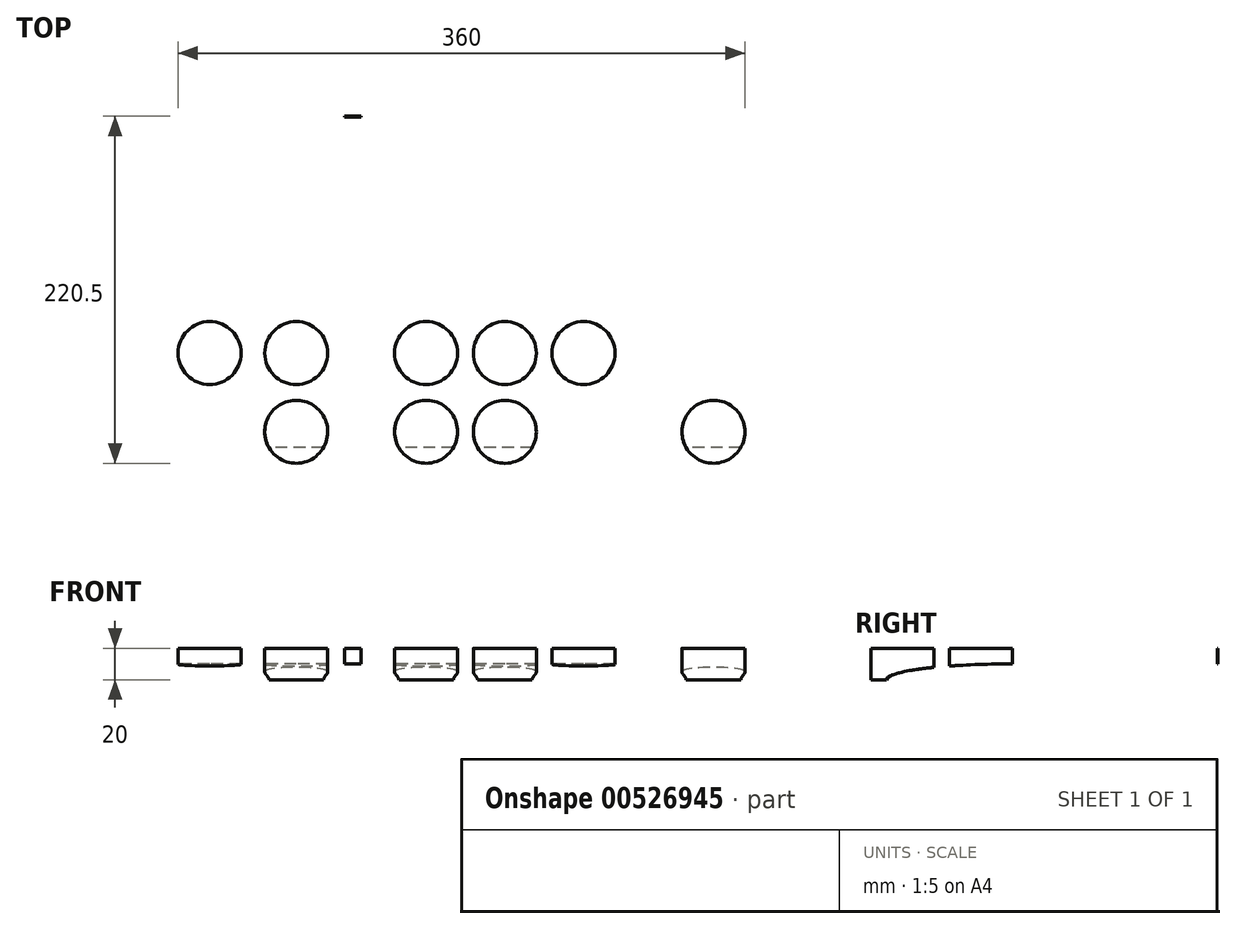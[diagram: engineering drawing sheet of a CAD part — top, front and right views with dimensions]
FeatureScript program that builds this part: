
annotation { "Feature Type Name" : "Feature", "Feature Type Description" : "" }
export const myFeature = defineFeature(function(context is Context, id is Id, definition is map)
    precondition{}
    {
        {
            var Q0;
            Q0=qCreatedBy(makeId("Top.planeOp"),FACE);
            var sketch = newSketch(context, id + "F0", { "sketchPlane" : qUnion([Q0])});
            skLineSegment(sketch, "E0.bottom", {"start": v(-365, 200) * mm, "end": v(365, 200) * mm});
            skLineSegment(sketch, "E0.top", {"start": v(-365, -200) * mm, "end": v(365, -200) * mm});
            skLineSegment(sketch, "E0.left", {"start": v(-365, 200) * mm, "end": v(-365, -200) * mm});
            skLineSegment(sketch, "E0.right", {"start": v(365, 200) * mm, "end": v(365, -200) * mm});
            skPoint(sketch, "E0.middle", {"position": v(0, 0) * mm});
            skEllipticalArc(sketch, "E1", {});
            skEllipticalArc(sketch, "E2.MirrorCS", {});
            skEllipticalArc(sketch, "E3.MirrorCS", {});
            skEllipticalArc(sketch, "E4.MirrorCS", {});
            skLineSegment(sketch, "E5", {"start": v(-365, 200) * mm, "end": v(-105, 200) * mm});
            skLineSegment(sketch, "E6", {"start": v(-365, 200) * mm, "end": v(-365, 50) * mm});
            skLineSegment(sketch, "E7", {"start": v(-365, -200) * mm, "end": v(-365, -50) * mm});
            skLineSegment(sketch, "E8", {"start": v(-365, -200) * mm, "end": v(-182.5, -200) * mm});
            skLineSegment(sketch, "E9", {"start": v(365, 200) * mm, "end": v(105, 200) * mm});
            skLineSegment(sketch, "E10", {"start": v(182.5, -200.11) * mm, "end": v(365, -200) * mm});
            skPoint(sketch, "E11", {"position": v(0, 200) * mm});
            skLineSegment(sketch, "E12", {"start": v(0, 200) * mm, "end": v(-130, 200) * mm});
            skLineSegment(sketch, "E13.MirrorCS", {"start": v(0, -200) * mm, "end": v(-130, -200) * mm});
            skLineSegment(sketch, "E14.MirrorCS", {"start": v(5, 200) * mm, "end": v(130, 200) * mm});
            skLineSegment(sketch, "E15.MirrorCS", {"start": v(-72.5, -200) * mm, "end": v(52.5, -200) * mm});
            skCircle(sketch, "E16", {"center": v(-278.75, 100) * mm, "radius": 20 * mm});
            skCircle(sketch, "E17", {"center": v(-223.75, 150) * mm, "radius": 20 * mm});
            skCircle(sketch, "E18", {"center": v(-223.75, 100) * mm, "radius": 20 * mm});
            skCircle(sketch, "E19", {"center": v(-141.25, 100) * mm, "radius": 20 * mm});
            skCircle(sketch, "E20", {"center": v(-141.25, 150) * mm, "radius": 20 * mm});
            skCircle(sketch, "E21", {"center": v(-91.25, 100) * mm, "radius": 20 * mm});
            skCircle(sketch, "E22", {"center": v(-91.25, 150) * mm, "radius": 20 * mm});
            skCircle(sketch, "E23", {"center": v(-41.25, 100) * mm, "radius": 20 * mm});
            skCircle(sketch, "E24.MirrorC", {"center": v(-41.25, 150) * mm, "radius": 20 * mm});
            skCircle(sketch, "E25.MirrorC", {"center": v(-278.75, -100) * mm, "radius": 20 * mm});
            skCircle(sketch, "E26.MirrorC", {"center": v(-223.75, -150) * mm, "radius": 20 * mm});
            skCircle(sketch, "E27.MirrorC", {"center": v(-223.75, -100) * mm, "radius": 20 * mm});
            skCircle(sketch, "E28.MirrorC", {"center": v(-141.25, -100) * mm, "radius": 20 * mm});
            skCircle(sketch, "E29.MirrorC", {"center": v(-141.25, -150) * mm, "radius": 20 * mm});
            skCircle(sketch, "E30.MirrorC", {"center": v(-91.25, -100) * mm, "radius": 20 * mm});
            skCircle(sketch, "E31.MirrorC", {"center": v(-41.25, -100) * mm, "radius": 20 * mm});
            skCircle(sketch, "E32.MirrorC", {"center": v(-91.25, -150) * mm, "radius": 20 * mm});
            skCircle(sketch, "E33.MirrorC", {"center": v(-41.25, -150) * mm, "radius": 20 * mm});
            skCircle(sketch, "E34.MirrorC", {"center": v(-222.5, -10) * mm, "radius": 20 * mm});
            skLineSegment(sketch, "E35.bottom", {"start": v(210, 15) * mm, "end": v(-210, 15) * mm});
            skLineSegment(sketch, "E35.top", {"start": v(210, -15) * mm, "end": v(-210, -15) * mm});
            skLineSegment(sketch, "E35.left", {"start": v(210, 15) * mm, "end": v(210, -15) * mm});
            skLineSegment(sketch, "E35.right", {"start": v(-210, 15) * mm, "end": v(-210, -15) * mm});
            skLineSegment(sketch, "E36", {"start": v(-365, -50) * mm, "end": v(365, -50) * mm});
            skLineSegment(sketch, "E37", {"start": v(-365, 50) * mm, "end": v(365, 50) * mm});
            skLineSegment(sketch, "E38", {"start": v(-182.5, -200) * mm, "end": v(-182.5, -40.61) * mm});
            skLineSegment(sketch, "E39", {"start": v(0, -200) * mm, "end": v(0, -50) * mm});
            skLineSegment(sketch, "E40", {"start": v(182.5, -200.11) * mm, "end": v(182.4, -40.7) * mm});
            skLineSegment(sketch, "E41.trimOffspring", {"start": v(-182.5, 40.61) * mm, "end": v(-182.5, 200) * mm});
            skLineSegment(sketch, "E42.trimOffspring", {"start": v(-182.5, -15) * mm, "end": v(-182.5, 15) * mm});
            skLineSegment(sketch, "E43.trimOffspring", {"start": v(182.39, -15) * mm, "end": v(182.37, 15) * mm});
            skLineSegment(sketch, "E44.trimOffspring", {"start": v(182.35, 40.73) * mm, "end": v(182.25, 200) * mm});
            skCircle(sketch, "E45", {"center": v(-272.5, 10) * mm, "radius": 20 * mm});
            skCircle(sketch, "E46.MirrorC", {"center": v(-322.5, -8.74) * mm, "radius": 20 * mm});
            skCircle(sketch, "E47.MirrorC", {"center": v(-142.5, -10) * mm, "radius": 20 * mm});
            skCircle(sketch, "E48.MirrorC", {"center": v(-92.5, 10) * mm, "radius": 20 * mm});
            skCircle(sketch, "E49.MirrorC", {"center": v(-42.5, -8.74) * mm, "radius": 20 * mm});
            skCircle(sketch, "E50.MirrorC", {"center": v(42.5, -8.74) * mm, "radius": 20 * mm});
            skCircle(sketch, "E51.MirrorC", {"center": v(142.5, -10) * mm, "radius": 20 * mm});
            skCircle(sketch, "E52.MirrorC", {"center": v(92.5, 10) * mm, "radius": 20 * mm});
            skCircle(sketch, "E53.MirrorC", {"center": v(222.5, -10) * mm, "radius": 20 * mm});
            skCircle(sketch, "E54.MirrorC", {"center": v(272.5, 10) * mm, "radius": 20 * mm});
            skCircle(sketch, "E55.MirrorC", {"center": v(322.5, -8.74) * mm, "radius": 20 * mm});
            skCircle(sketch, "E56.MirrorC", {"center": v(223.75, -100) * mm, "radius": 20 * mm});
            skCircle(sketch, "E57.MirrorC", {"center": v(223.75, -150) * mm, "radius": 20 * mm});
            skCircle(sketch, "E58.MirrorC", {"center": v(278.75, -100) * mm, "radius": 20 * mm});
            skCircle(sketch, "E59.MirrorC", {"center": v(141.25, -100) * mm, "radius": 20 * mm});
            skCircle(sketch, "E60.MirrorC", {"center": v(141.25, -150) * mm, "radius": 20 * mm});
            skCircle(sketch, "E61.MirrorC", {"center": v(91.25, -150) * mm, "radius": 20 * mm});
            skCircle(sketch, "E62.MirrorC", {"center": v(91.25, -100) * mm, "radius": 20 * mm});
            skCircle(sketch, "E63.MirrorC", {"center": v(41.25, -100) * mm, "radius": 20 * mm});
            skCircle(sketch, "E64.MirrorC", {"center": v(41.25, -150) * mm, "radius": 20 * mm});
            skCircle(sketch, "E65.MirrorC", {"center": v(41.25, 100) * mm, "radius": 20 * mm});
            skCircle(sketch, "E66.MirrorC", {"center": v(91.25, 100) * mm, "radius": 20 * mm});
            skCircle(sketch, "E67.MirrorC", {"center": v(141.25, 100) * mm, "radius": 20 * mm});
            skCircle(sketch, "E68.MirrorC", {"center": v(223.75, 100) * mm, "radius": 20 * mm});
            skCircle(sketch, "E69.MirrorC", {"center": v(278.75, 100) * mm, "radius": 20 * mm});
            skCircle(sketch, "E70.MirrorC", {"center": v(223.75, 150) * mm, "radius": 20 * mm});
            skCircle(sketch, "E71.MirrorC", {"center": v(141.25, 150) * mm, "radius": 20 * mm});
            skCircle(sketch, "E72.MirrorC", {"center": v(91.25, 150) * mm, "radius": 20 * mm});
            skCircle(sketch, "E73.MirrorC", {"center": v(41.25, 150) * mm, "radius": 20 * mm});
            const initialGuessF0  = {"E1": [0.215000023161019, -0.00011114199246731203, 0, -1, 0.20000000103052606, 0.15, 6.249845643425636, 1.5707963267948966], "E2.MirrorCS": [-0.215, -0.00011114199246737072, 0, -1, 0.2, 0.15, 4.711833270393751, 0.03333950926130193], "E3.MirrorCS": [-0.215, 0.00011114199246727815, 0, 1, 0.2, 0.15, 6.249845797918284, 1.5707963267948966], "E4.MirrorCS": [0.215, 0.00011114199246735796, 0, 1, 0.2, 0.15, 4.711277560231201, 0.03333950926130226]};
            skSetInitialGuess(sketch, initialGuessF0);
            skSolve(sketch);
        }
        {
            var Q0;
            Q0=qCreatedBy(makeId("Top.planeOp"),FACE);
            cPlane(context, id + "F1", {"entities" : qUnion([Q0]), "cplaneType" : CPlaneType.OFFSET, "offset" : 20 * mm, "width" : 150 * mm, "height" : 150 * mm});
        }
        {
            var Q0;
            Q0=qCreatedBy(id+"F1.planeOp",FACE);
            var sketch = newSketch(context, id + "F2", { "sketchPlane" : qUnion([Q0])});
            skLineSegment(sketch, "E74.bottom", {"start": v(0, 0) * mm, "end": v(365, 0) * mm});
            skLineSegment(sketch, "E74.top", {"start": v(0, -200) * mm, "end": v(210, -200) * mm});
            skLineSegment(sketch, "E74.left", {"start": v(0, 0) * mm, "end": v(0, -200) * mm});
            skLineSegment(sketch, "E75", {"start": v(0, -15) * mm, "end": v(364.58, -15) * mm});
            skLineSegment(sketch, "E76", {"start": v(0, -170) * mm, "end": v(294.02, -170) * mm});
            skLineSegment(sketch, "E77", {"start": v(330, 0) * mm, "end": v(330, -128.4) * mm});
            skLineSegment(sketch, "E78", {"start": v(215, 0) * mm, "end": v(215, -200) * mm});
            skPoint(sketch, "E79", {"position": v(215, -200) * mm});
            skPoint(sketch, "E80", {"position": v(365, 0) * mm});
            skLineSegment(sketch, "E81", {"start": v(275, 0) * mm, "end": v(275, -183.3) * mm});
            skLineSegment(sketch, "E82", {"start": v(275, -140) * mm, "end": v(322.12, -140) * mm});
            skPoint(sketch, "E83", {"position": v(215, -170) * mm});
            skPoint(sketch, "E84", {"position": v(330, 0) * mm});
            skPoint(sketch, "E85", {"position": v(275, -140) * mm});
            skPoint(sketch, "E86", {"position": v(330, -140) * mm});
            skPoint(sketch, "E87", {"position": v(275, -185) * mm});
            skLineSegment(sketch, "E88", {"start": v(315, -149.07) * mm, "end": v(315, 0) * mm});
            skLineSegment(sketch, "E89", {"start": v(210, 0) * mm, "end": v(210, -200) * mm});
            skEllipticalArc(sketch, "E90.trimOffspring", {});
            skEllipticalArc(sketch, "E91", {});
            skPoint(sketch, "E92.orphan", {"position": v(365, -170) * mm});
            skPoint(sketch, "E93.trimOffspring.end.orphan", {"position": v(330, -200) * mm});
            skPoint(sketch, "E94.orphan", {"position": v(365, -200) * mm});
            skPoint(sketch, "E95.orphan", {"position": v(365, -15) * mm});
            skLineSegment(sketch, "E96.MirrorCS", {"start": v(0, 0) * mm, "end": v(-365, 0) * mm});
            skLineSegment(sketch, "E97.MirrorCS", {"start": v(0, -15) * mm, "end": v(-364.58, -15) * mm});
            skLineSegment(sketch, "E98.MirrorCS", {"start": v(0, -170) * mm, "end": v(-294.02, -170) * mm});
            skLineSegment(sketch, "E99.MirrorCS", {"start": v(0, -200) * mm, "end": v(-210, -200) * mm});
            skLineSegment(sketch, "E100.MirrorCS", {"start": v(-210, 0) * mm, "end": v(-210, -200) * mm});
            skLineSegment(sketch, "E101.MirrorCS", {"start": v(-215, 0) * mm, "end": v(-215, -200) * mm});
            skEllipticalArc(sketch, "E102.MirrorCS", {});
            skEllipticalArc(sketch, "E103.MirrorCS", {});
            skLineSegment(sketch, "E104.MirrorCS", {"start": v(-275, 0) * mm, "end": v(-275, -183.3) * mm});
            skLineSegment(sketch, "E105.MirrorCS", {"start": v(-275, -140) * mm, "end": v(-322.12, -140) * mm});
            skLineSegment(sketch, "E106.MirrorCS", {"start": v(-315, -149.07) * mm, "end": v(-315, 0) * mm});
            skLineSegment(sketch, "E107.MirrorCS", {"start": v(-330, 0) * mm, "end": v(-330, -128.4) * mm});
            skLineSegment(sketch, "E108.MirrorCS", {"start": v(0, 15) * mm, "end": v(-364.58, 15) * mm});
            skLineSegment(sketch, "E109.MirrorCS", {"start": v(0, 15) * mm, "end": v(364.58, 15) * mm});
            skEllipticalArc(sketch, "E110.MirrorCS", {});
            skLineSegment(sketch, "E111.MirrorCS", {"start": v(-330, 0) * mm, "end": v(-330, 128.4) * mm});
            skLineSegment(sketch, "E112.MirrorCS", {"start": v(-315, 149.07) * mm, "end": v(-315, 0) * mm});
            skLineSegment(sketch, "E113.MirrorCS", {"start": v(-275, 0) * mm, "end": v(-275, 183.3) * mm});
            skLineSegment(sketch, "E114.MirrorCS", {"start": v(-215, 0) * mm, "end": v(-215, 200) * mm});
            skLineSegment(sketch, "E115.MirrorCS", {"start": v(-210, 0) * mm, "end": v(-210, 200) * mm});
            skLineSegment(sketch, "E116.MirrorCS", {"start": v(0, 0) * mm, "end": v(0, 200) * mm});
            skLineSegment(sketch, "E117.MirrorCS", {"start": v(210, 0) * mm, "end": v(210, 200) * mm});
            skLineSegment(sketch, "E118.MirrorCS", {"start": v(215, 0) * mm, "end": v(215, 200) * mm});
            skLineSegment(sketch, "E119.MirrorCS", {"start": v(275, 0) * mm, "end": v(275, 183.3) * mm});
            skLineSegment(sketch, "E120.MirrorCS", {"start": v(315, 149.07) * mm, "end": v(315, 0) * mm});
            skLineSegment(sketch, "E121.MirrorCS", {"start": v(330, 0) * mm, "end": v(330, 128.4) * mm});
            skEllipticalArc(sketch, "E122.MirrorCS", {});
            skEllipticalArc(sketch, "E123.MirrorCS", {});
            skEllipticalArc(sketch, "E124.MirrorCS", {});
            skLineSegment(sketch, "E125.MirrorCS", {"start": v(-275, 140) * mm, "end": v(-322.12, 140) * mm});
            skLineSegment(sketch, "E126.MirrorCS", {"start": v(0, 170) * mm, "end": v(-294.02, 170) * mm});
            skLineSegment(sketch, "E127.MirrorCS", {"start": v(0, 170) * mm, "end": v(294.02, 170) * mm});
            skLineSegment(sketch, "E128.MirrorCS", {"start": v(0, 200) * mm, "end": v(210, 200) * mm});
            skLineSegment(sketch, "E129.MirrorCS", {"start": v(0, 200) * mm, "end": v(-210, 200) * mm});
            skLineSegment(sketch, "E130.MirrorCS", {"start": v(275, 140) * mm, "end": v(322.12, 140) * mm});
            const initialGuessF2  = {"E90.trimOffspring": [0.215, 0, 1, 0, 0.115, 0.17, 4.71238898038469, 6.283185307179586], "E91": [0.215, 0, 0, -1, 0.2, 0.15, 6.249845797918284, 1.5707963267948966], "E102.MirrorCS": [-0.215, 0, -1, 0, 0.115, 0.17, 6.283185307179586, 1.5707963267948966], "E103.MirrorCS": [-0.215, 0, 0, -1, 0.2, 0.15, 4.71238898038469, 0.03333950926130225], "E110.MirrorCS": [-0.215, 0, 0, 1, 0.2, 0.15, 6.249845797918284, 1.5707963267948966], "E122.MirrorCS": [0.215, 0, 0, 1, 0.2, 0.15, 4.71238898038469, 0.03333950926130225], "E123.MirrorCS": [0.215, 0, 1, 0, 0.115, 0.17, 6.283185307179586, 1.5707963267948966], "E124.MirrorCS": [-0.215, 0, -1, 0, 0.115, 0.17, 4.71238898038469, 6.283185307179586]};
            skSetInitialGuess(sketch, initialGuessF2);
            skSolve(sketch);
        }
        {
            var Q0;
            Q0=qCreatedBy(makeId("Right.planeOp"),FACE);
            var sketch = newSketch(context, id + "F3", { "sketchPlane" : qUnion([Q0])});
            skPoint(sketch, "E131.middle", {"position": v(0, 20) * mm});
            skPoint(sketch, "E132", {"position": v(170, 0) * mm});
            skPoint(sketch, "E133", {"position": v(160, 0) * mm});
            skLineSegment(sketch, "E134.bottom", {"start": v(15, 10.07) * mm, "end": v(80, 10.07) * mm});
            skPoint(sketch, "E135", {"position": v(80, 10.07) * mm});
            skEllipticalArc(sketch, "E136", {});
            skEllipticalArc(sketch, "E137", {});
            skLineSegment(sketch, "E138", {"start": v(0, 20) * mm, "end": v(0, 10.04) * mm});
            skLineSegment(sketch, "E139", {"start": v(0, 20) * mm, "end": v(200, 20) * mm});
            skLineSegment(sketch, "E140", {"start": v(200, 20) * mm, "end": v(0, 20) * mm});
            skLineSegment(sketch, "E141", {"start": v(160, 0) * mm, "end": v(170, 0) * mm});
            skPoint(sketch, "E142.orphan", {"position": v(-200, 20) * mm});
            skLineSegment(sketch, "E143.MirrorCS", {"start": v(-200, 20) * mm, "end": v(0, 20) * mm});
            skLineSegment(sketch, "E144.MirrorCS", {"start": v(-15, 10.07) * mm, "end": v(-80, 10.07) * mm});
            skEllipticalArc(sketch, "E145.MirrorCS", {});
            skLineSegment(sketch, "E146.MirrorCS", {"start": v(-160, 0) * mm, "end": v(-170, 0) * mm});
            skEllipticalArc(sketch, "E147.MirrorCS", {});
            skLineSegment(sketch, "E148.top", {"start": v(-15, 12) * mm, "end": v(15, 12) * mm});
            skLineSegment(sketch, "E148.left", {"start": v(-15, 10.07) * mm, "end": v(-15, 12) * mm});
            skLineSegment(sketch, "E148.right", {"start": v(15, 10.07) * mm, "end": v(15, 12) * mm});
            skLineSegment(sketch, "E149.bottom", {"start": v(15, 18) * mm, "end": v(-15, 18) * mm});
            skLineSegment(sketch, "E149.top", {"start": v(15, 12) * mm, "end": v(-15, 12) * mm});
            skLineSegment(sketch, "E149.left", {"start": v(15, 18) * mm, "end": v(15, 12) * mm});
            skLineSegment(sketch, "E149.right", {"start": v(-15, 18) * mm, "end": v(-15, 12) * mm});
            skLineSegment(sketch, "E150", {"start": v(170, 0) * mm, "end": v(170.12, 20) * mm});
            skLineSegment(sketch, "E151", {"start": v(-170, 0) * mm, "end": v(-170.12, 20) * mm});
            skLineSegment(sketch, "E152", {"start": v(-15, 12) * mm, "end": v(-15, 10.07) * mm});
            skLineSegment(sketch, "E153.bottom", {"start": v(-200, 20) * mm, "end": v(-170, 20) * mm});
            skLineSegment(sketch, "E153.top", {"start": v(-200, 0) * mm, "end": v(-170, 0) * mm});
            skLineSegment(sketch, "E153.left", {"start": v(-200, 20) * mm, "end": v(-200, 0) * mm});
            skLineSegment(sketch, "E153.right", {"start": v(-170, 20) * mm, "end": v(-170, 0) * mm});
            skLineSegment(sketch, "E154.MirrorCS", {"start": v(200, 0) * mm, "end": v(170, 0) * mm});
            skLineSegment(sketch, "E155.MirrorCS", {"start": v(200, 20) * mm, "end": v(200, 0) * mm});
            skLineSegment(sketch, "E156", {"start": v(80, 10.07) * mm, "end": v(80, 20) * mm});
            skLineSegment(sketch, "E157", {"start": v(160, 0) * mm, "end": v(160, 20) * mm});
            skLineSegment(sketch, "E158", {"start": v(149.2, 20) * mm, "end": v(149.2, 5.05) * mm});
            skLineSegment(sketch, "E159", {"start": v(140.08, 20) * mm, "end": v(140.08, 6.65) * mm});
            skLineSegment(sketch, "E160", {"start": v(128.23, 20) * mm, "end": v(128.23, 8.04) * mm});
            skLineSegment(sketch, "E161", {"start": v(102.69, 20) * mm, "end": v(102.69, 9.66) * mm});
            skLineSegment(sketch, "E162.MirrorCS", {"start": v(-80, 10.07) * mm, "end": v(-80, 20) * mm});
            skLineSegment(sketch, "E163.MirrorCS", {"start": v(-102.69, 20) * mm, "end": v(-102.69, 9.66) * mm});
            skLineSegment(sketch, "E164.MirrorCS", {"start": v(-128.23, 20) * mm, "end": v(-128.23, 8.04) * mm});
            skLineSegment(sketch, "E165.MirrorCS", {"start": v(-140.08, 20) * mm, "end": v(-140.08, 6.65) * mm});
            skLineSegment(sketch, "E166.MirrorCS", {"start": v(-149.2, 20) * mm, "end": v(-149.2, 5.05) * mm});
            skLineSegment(sketch, "E167.MirrorCS", {"start": v(-160, 0) * mm, "end": v(-160, 20) * mm});
            skLineSegment(sketch, "E168", {"start": v(45, 20) * mm, "end": v(45, 10.07) * mm});
            skLineSegment(sketch, "E169.MirrorCS", {"start": v(-45, 20) * mm, "end": v(-45, 10.07) * mm});
            const initialGuessF3  = {"E136": [0.17012490332126617, 0.02, -0.006245044279577429, -0.9999804995208388, 0.020000390017188747, 0.02987581400604767, 6.283185307179586, 1.580124845260153], "E137": [0.08, 0, 0, 1, 0.01007139225942586, 0.08, 4.71238898038469, 6.283185307179586], "E145.MirrorCS": [-0.08, 0, 0, 1, 0.01007139225942586, 0.08, 6.283185307179586, 1.5707963267948966], "E147.MirrorCS": [-0.17012490332126617, 0.02, 0.006245044279579518, -0.9999804995208388, 0.020000390017188747, 0.02987581400604767, 4.703060461919433, 6.283185307179586]};
            skSetInitialGuess(sketch, initialGuessF3);
            skSolve(sketch);
        }
        {
            var Q0;
            Q0=qCreatedBy(makeId("Front.planeOp"),FACE);
            var sketch = newSketch(context, id + "F4", { "sketchPlane" : qUnion([Q0])});
            skLineSegment(sketch, "E170", {"start": v(0, 20) * mm, "end": v(365, 20) * mm});
            skPoint(sketch, "E171", {"position": v(210, 20) * mm});
            skLineSegment(sketch, "E172", {"start": v(210, 18) * mm, "end": v(210, 12) * mm});
            skPoint(sketch, "E173", {"position": v(315, 20) * mm});
            skLineSegment(sketch, "E174", {"start": v(315, 18) * mm, "end": v(315, 0) * mm});
            skLineSegment(sketch, "E175", {"start": v(0, 12) * mm, "end": v(0, 20) * mm});
            skLineSegment(sketch, "E176", {"start": v(210, 12) * mm, "end": v(0, 12) * mm});
            skPoint(sketch, "E177", {"position": v(365.07, 0) * mm});
            skPoint(sketch, "E178", {"position": v(365, 20) * mm});
            skEllipticalArc(sketch, "E179", {});
            skLineSegment(sketch, "E180", {"start": v(315, 18) * mm, "end": v(210, 18) * mm});
            skLineSegment(sketch, "E181.MirrorCS", {"start": v(0, 20) * mm, "end": v(-365, 20) * mm});
            skLineSegment(sketch, "E182.MirrorCS", {"start": v(-210, 12) * mm, "end": v(0, 12) * mm});
            skLineSegment(sketch, "E183.MirrorCS", {"start": v(-210, 18) * mm, "end": v(-210, 12) * mm});
            skLineSegment(sketch, "E184.MirrorCS", {"start": v(-315, 18) * mm, "end": v(-210, 18) * mm});
            skLineSegment(sketch, "E185.MirrorCS", {"start": v(-315, 18) * mm, "end": v(-315, 0) * mm});
            skEllipticalArc(sketch, "E186.MirrorCS", {});
            skPoint(sketch, "E187", {"position": v(245, 20) * mm});
            skPoint(sketch, "E188", {"position": v(245, 10.07) * mm});
            skPoint(sketch, "E189", {"position": v(325, 20) * mm});
            skPoint(sketch, "E190", {"position": v(335, 20) * mm});
            skLineSegment(sketch, "E191", {"start": v(335, 20) * mm, "end": v(335, 10.07) * mm});
            skLineSegment(sketch, "E192", {"start": v(335, 10.07) * mm, "end": v(0, 10.07) * mm});
            skLineSegment(sketch, "E193.MirrorCS", {"start": v(-335, 10.07) * mm, "end": v(0, 10.07) * mm});
            skLineSegment(sketch, "E194.MirrorCS", {"start": v(-335, 20) * mm, "end": v(-335, 10.07) * mm});
            skLineSegment(sketch, "E195", {"start": v(365, 20) * mm, "end": v(365.07, 0) * mm});
            skLineSegment(sketch, "E196", {"start": v(315, 0) * mm, "end": v(365.07, 0) * mm});
            skLineSegment(sketch, "E197.MirrorCS", {"start": v(-365, 20) * mm, "end": v(-365.07, 0) * mm});
            skLineSegment(sketch, "E198.MirrorCS", {"start": v(-315, 0) * mm, "end": v(-365.07, 0) * mm});
            skLineSegment(sketch, "E199", {"start": v(335, 10.07) * mm, "end": v(335, 1.67) * mm});
            skLineSegment(sketch, "E200.MirrorCS", {"start": v(-335, 10.07) * mm, "end": v(-335, 1.67) * mm});
            skLineSegment(sketch, "E201", {"start": v(-315, 18) * mm, "end": v(-315, 20) * mm});
            skLineSegment(sketch, "E202", {"start": v(-210, 18) * mm, "end": v(-210, 20) * mm});
            skLineSegment(sketch, "E203.MirrorCS", {"start": v(210, 18) * mm, "end": v(210, 20) * mm});
            skLineSegment(sketch, "E204.MirrorCS", {"start": v(315, 18) * mm, "end": v(315, 20) * mm});
            skPoint(sketch, "E205", {"position": v(275, 20) * mm});
            skPoint(sketch, "E206.MirrorP", {"position": v(-275, 20) * mm});
            skLineSegment(sketch, "E207", {"start": v(275, 20) * mm, "end": v(275, 18) * mm});
            skLineSegment(sketch, "E208.MirrorCS", {"start": v(-275, 20) * mm, "end": v(-275, 18) * mm});
            skPoint(sketch, "E209", {"position": v(-333.25, 14.9) * mm});
            skPoint(sketch, "E210", {"position": v(-218.12, 14.9) * mm});
            skPoint(sketch, "E211", {"position": v(-78.75, 14.9) * mm});
            const initialGuessF4  = {"E179": [0.315, 0.02, 1, 0, 0.05, 0.02, 4.71238898038469, 0], "E186.MirrorCS": [-0.315, 0.02, -1, 0, 0.05, 0.02, 0, 1.5707963267948966]};
            skSetInitialGuess(sketch, initialGuessF4);
            skSolve(sketch);
        }
        {
            var Q0;
            Q0=qSketchRegion(id+"F2",true);
            var Q1;
            {var subQ0=sQuery(id+"F2.wireOp",EDGE,"E125.MirrorCS");var subQ1=sQuery(id+"F2.wireOp",EDGE,"E112.MirrorCS");var subQ2=makeQuery(id+"F2.imprint","INTERSECT",VERTEX,{"derivedFrom":[subQ1,subQ0]});Q1=makeQuery(id+"F2.imprint","IMPRINT",FACE,{"disambiguationData":[TD([[makeQuery(id+"F2.imprint","IMPRINT",EDGE,{"disambiguationData":[TD([[subQ2,-1.0]])],"derivedFrom":subQ1}),1.0]])]});}
            var Q2;
            {var subQ0=sQuery(id+"F2.wireOp",EDGE,"E124.MirrorCS");var subQ1=sQuery(id+"F2.wireOp",EDGE,"E113.MirrorCS");var subQ2=makeQuery(id+"F2.imprint","INTERSECT",VERTEX,{"derivedFrom":[subQ1,subQ0]});Q2=makeQuery(id+"F2.imprint","IMPRINT",FACE,{"disambiguationData":[TD([[makeQuery(id+"F2.imprint","IMPRINT",EDGE,{"disambiguationData":[TD([[subQ2,-1.0]])],"derivedFrom":subQ1}),-1.0]])]});}
            var Q3;
            {var subQ0=sQuery(id+"F2.wireOp",EDGE,"E123.MirrorCS");var subQ1=sQuery(id+"F2.wireOp",EDGE,"E119.MirrorCS");var subQ2=makeQuery(id+"F2.imprint","INTERSECT",VERTEX,{"derivedFrom":[subQ1,subQ0]});Q3=makeQuery(id+"F2.imprint","IMPRINT",FACE,{"disambiguationData":[TD([[makeQuery(id+"F2.imprint","IMPRINT",EDGE,{"disambiguationData":[TD([[subQ2,-1.0]])],"derivedFrom":subQ1}),1.0]])]});}
            var Q4;
            {var subQ0=sQuery(id+"F2.wireOp",EDGE,"E130.MirrorCS");var subQ1=sQuery(id+"F2.wireOp",EDGE,"E120.MirrorCS");var subQ2=makeQuery(id+"F2.imprint","INTERSECT",VERTEX,{"derivedFrom":[subQ1,subQ0]});Q4=makeQuery(id+"F2.imprint","IMPRINT",FACE,{"disambiguationData":[TD([[makeQuery(id+"F2.imprint","IMPRINT",EDGE,{"disambiguationData":[TD([[subQ2,-1.0]])],"derivedFrom":subQ1}),-1.0]])]});}
            var Q5;
            {var subQ0=sQuery(id+"F2.wireOp",EDGE,"E90.trimOffspring");var subQ1=sQuery(id+"F2.wireOp",EDGE,"E82");var subQ2=makeQuery(id+"F2.imprint","INTERSECT",VERTEX,{"derivedFrom":[subQ1,subQ0]});Q5=makeQuery(id+"F2.imprint","IMPRINT",FACE,{"disambiguationData":[TD([[makeQuery(id+"F2.imprint","IMPRINT",EDGE,{"disambiguationData":[TD([[subQ2,-1.0]])],"derivedFrom":subQ1}),1.0]])]});}
            var Q6;
            {var subQ1=sQuery(id+"F2.wireOp",EDGE,"E76");var subQ3=sQuery(id+"F2.wireOp",EDGE,"E81");var subQ4=makeQuery(id+"F2.imprint","INTERSECT",VERTEX,{"derivedFrom":[subQ1,subQ3]});Q6=makeQuery(id+"F2.imprint","IMPRINT",FACE,{"disambiguationData":[TD([[makeQuery(id+"F2.imprint","IMPRINT",EDGE,{"disambiguationData":[TD([[subQ4,1.0]])],"derivedFrom":subQ3}),-1.0]])]});}
            var Q7;
            {var subQ1=sQuery(id+"F2.wireOp",EDGE,"E98.MirrorCS");var subQ3=sQuery(id+"F2.wireOp",EDGE,"E104.MirrorCS");var subQ4=makeQuery(id+"F2.imprint","INTERSECT",VERTEX,{"derivedFrom":[subQ1,subQ3]});Q7=makeQuery(id+"F2.imprint","IMPRINT",FACE,{"disambiguationData":[TD([[makeQuery(id+"F2.imprint","IMPRINT",EDGE,{"disambiguationData":[TD([[subQ4,1.0]])],"derivedFrom":subQ3}),1.0]])]});}
            var Q8;
            {var subQ0=sQuery(id+"F2.wireOp",EDGE,"E106.MirrorCS");var subQ1=sQuery(id+"F2.wireOp",EDGE,"E102.MirrorCS");var subQ2=makeQuery(id+"F2.imprint","INTERSECT",VERTEX,{"derivedFrom":[subQ1,subQ0]});Q8=makeQuery(id+"F2.imprint","IMPRINT",FACE,{"disambiguationData":[TD([[makeQuery(id+"F2.imprint","IMPRINT",EDGE,{"disambiguationData":[TD([[subQ2,-1.0]])],"derivedFrom":subQ1}),-1.0]])]});}
            extrude(context, id + "F5", {"entities" : qUnion([Q0, Q1, Q2, Q3, Q4, Q5, Q6, Q7, Q8]), "oppositeDirection" : true, "depth" : 20 * mm, "offsetDistance" : 25 * mm});
        }
        {
            var Q0;
            {var subQ0=sQuery(id+"F3.wireOp",EDGE,"E149.right");Q0=makeQuery(id+"F3.imprint","IMPRINT",FACE,{"disambiguationData":[TD([[makeQuery(id+"F3.imprint","IMPRINT",EDGE,{"derivedFrom":subQ0}),-1.0]])]});}
            var Q1;
            {var subQ0=sQuery(id+"F3.wireOp",EDGE,"E149.left");Q1=makeQuery(id+"F3.imprint","IMPRINT",FACE,{"disambiguationData":[TD([[makeQuery(id+"F3.imprint","IMPRINT",EDGE,{"derivedFrom":subQ0}),1.0]])]});}
            extrude(context, id + "F6", {"entities" : qUnion([Q0, Q1]), "operationType" : NewBodyOperationType.ADD, "depth" : 420 * mm, "offsetDistance" : 25 * mm, "symmetric" : true});
        }
        {
            var Q0;
            {var subQ0=sQuery(id+"F3.wireOp",EDGE,"E156");Q0=makeQuery(id+"F3.imprint","IMPRINT",FACE,{"disambiguationData":[TD([[makeQuery(id+"F3.imprint","IMPRINT",EDGE,{"derivedFrom":subQ0}),-1.0]])]});}
            var Q1;
            {var subQ0=sQuery(id+"F3.wireOp",EDGE,"E160");Q1=makeQuery(id+"F3.imprint","IMPRINT",FACE,{"disambiguationData":[TD([[makeQuery(id+"F3.imprint","IMPRINT",EDGE,{"derivedFrom":subQ0}),-1.0]])]});}
            var Q2;
            {var subQ0=sQuery(id+"F3.wireOp",EDGE,"E159");Q2=makeQuery(id+"F3.imprint","IMPRINT",FACE,{"disambiguationData":[TD([[makeQuery(id+"F3.imprint","IMPRINT",EDGE,{"derivedFrom":subQ0}),-1.0]])]});}
            var Q3;
            {var subQ0=sQuery(id+"F3.wireOp",EDGE,"E158");Q3=makeQuery(id+"F3.imprint","IMPRINT",FACE,{"disambiguationData":[TD([[makeQuery(id+"F3.imprint","IMPRINT",EDGE,{"derivedFrom":subQ0}),-1.0]])]});}
            var Q4;
            {var subQ0=sQuery(id+"F3.wireOp",EDGE,"E157");Q4=makeQuery(id+"F3.imprint","IMPRINT",FACE,{"disambiguationData":[TD([[makeQuery(id+"F3.imprint","IMPRINT",EDGE,{"derivedFrom":subQ0}),1.0]])]});}
            var Q5;
            Q5=makeQuery(id+"F3.imprint","IMPRINT",FACE,{"disambiguationData":[TD([[makeQuery(id+"F3.imprint","IMPRINT",EDGE,{"derivedFrom":sQuery(id+"F3.wireOp",EDGE,"E141")}),1.0]])]});
            var Q6;
            {var subQ0=sQuery(id+"F3.wireOp",EDGE,"E162.MirrorCS");Q6=makeQuery(id+"F3.imprint","IMPRINT",FACE,{"disambiguationData":[TD([[makeQuery(id+"F3.imprint","IMPRINT",EDGE,{"derivedFrom":subQ0}),1.0]])]});}
            var Q7;
            {var subQ0=sQuery(id+"F3.wireOp",EDGE,"E163.MirrorCS");Q7=makeQuery(id+"F3.imprint","IMPRINT",FACE,{"disambiguationData":[TD([[makeQuery(id+"F3.imprint","IMPRINT",EDGE,{"derivedFrom":subQ0}),-1.0]])]});}
            var Q8;
            {var subQ0=sQuery(id+"F3.wireOp",EDGE,"E164.MirrorCS");Q8=makeQuery(id+"F3.imprint","IMPRINT",FACE,{"disambiguationData":[TD([[makeQuery(id+"F3.imprint","IMPRINT",EDGE,{"derivedFrom":subQ0}),-1.0]])]});}
            var Q9;
            {var subQ0=sQuery(id+"F3.wireOp",EDGE,"E165.MirrorCS");Q9=makeQuery(id+"F3.imprint","IMPRINT",FACE,{"disambiguationData":[TD([[makeQuery(id+"F3.imprint","IMPRINT",EDGE,{"derivedFrom":subQ0}),-1.0]])]});}
            var Q10;
            {var subQ0=sQuery(id+"F3.wireOp",EDGE,"E166.MirrorCS");Q10=makeQuery(id+"F3.imprint","IMPRINT",FACE,{"disambiguationData":[TD([[makeQuery(id+"F3.imprint","IMPRINT",EDGE,{"derivedFrom":subQ0}),-1.0]])]});}
            var Q11;
            Q11=makeQuery(id+"F3.imprint","IMPRINT",FACE,{"disambiguationData":[TD([[makeQuery(id+"F3.imprint","IMPRINT",EDGE,{"derivedFrom":sQuery(id+"F3.wireOp",EDGE,"E146.MirrorCS")}),-1.0]])]});
            var Q12;
            {var subQ0=sQuery(id+"F3.wireOp",EDGE,"E156");Q12=makeQuery(id+"F3.imprint","IMPRINT",FACE,{"disambiguationData":[TD([[makeQuery(id+"F3.imprint","IMPRINT",EDGE,{"derivedFrom":subQ0}),1.0]])]});}
            var Q13;
            {var subQ0=sQuery(id+"F3.wireOp",EDGE,"E162.MirrorCS");Q13=makeQuery(id+"F3.imprint","IMPRINT",FACE,{"disambiguationData":[TD([[makeQuery(id+"F3.imprint","IMPRINT",EDGE,{"derivedFrom":subQ0}),-1.0]])]});}
            extrude(context, id + "F7", {"entities" : qUnion([Q0, Q1, Q2, Q3, Q4, Q5, Q6, Q7, Q8, Q9, Q10, Q11, Q12, Q13]), "operationType" : NewBodyOperationType.ADD, "depth" : 520 * mm, "offsetDistance" : 25 * mm, "symmetric" : true});
        }
        {
            var Q0;
            Q0=makeQuery(id+"F4.imprint","IMPRINT",FACE,{"disambiguationData":[TD([[makeQuery(id+"F4.imprint","IMPRINT",EDGE,{"derivedFrom":sQuery(id+"F4.wireOp",EDGE,"E172")}),-1.0]])]});
            var Q1;
            {var subQ1=sQuery(id+"F4.wireOp",EDGE,"E179");Q1=makeQuery(id+"F4.imprint","IMPRINT",FACE,{"disambiguationData":[TD([[makeQuery(id+"F4.imprint","IMPRINT",EDGE,{"derivedFrom":subQ1}),1.0]])]});}
            var Q2;
            {var subQ2=sQuery(id+"F4.wireOp",EDGE,"E175");Q2=makeQuery(id+"F4.imprint","IMPRINT",FACE,{"disambiguationData":[TD([[makeQuery(id+"F4.imprint","IMPRINT",EDGE,{"derivedFrom":subQ2}),1.0]])]});}
            var Q3;
            {var subQ0=sQuery(id+"F4.wireOp",EDGE,"E186.MirrorCS");Q3=makeQuery(id+"F4.imprint","IMPRINT",FACE,{"disambiguationData":[TD([[makeQuery(id+"F4.imprint","IMPRINT",EDGE,{"derivedFrom":subQ0}),1.0]])]});}
            extrude(context, id + "F8", {"entities" : qUnion([Q0, Q1, Q2, Q3]), "operationType" : NewBodyOperationType.ADD, "depth" : 30 * mm, "offsetDistance" : 25 * mm, "symmetric" : true});
        }
        {
            var Q0;
            {var subQ0=sQuery(id+"F3.wireOp",EDGE,"E153.left");var subQ1=sQuery(id+"F3.wireOp",EDGE,"E147.MirrorCS");var subQ2=makeQuery(id+"F3.imprint","INTERSECT",VERTEX,{"derivedFrom":[subQ1,subQ0]});Q0=makeQuery(id+"F3.imprint","IMPRINT",FACE,{"disambiguationData":[TD([[makeQuery(id+"F3.imprint","IMPRINT",EDGE,{"disambiguationData":[TD([[subQ2,-1.0]])],"derivedFrom":subQ1}),-1.0]])]});}
            var Q1;
            {var subQ0=sQuery(id+"F3.wireOp",EDGE,"E155.MirrorCS");var subQ1=sQuery(id+"F3.wireOp",EDGE,"E136");var subQ2=makeQuery(id+"F3.imprint","INTERSECT",VERTEX,{"derivedFrom":[subQ1,subQ0]});Q1=makeQuery(id+"F3.imprint","IMPRINT",FACE,{"disambiguationData":[TD([[makeQuery(id+"F3.imprint","IMPRINT",EDGE,{"disambiguationData":[TD([[subQ2,1.0]])],"derivedFrom":subQ1}),-1.0]])]});}
            var Q2;
            Q2=sQuery(id+"F3.wireOp",EDGE,"E153.left");
            var Q3;
            Q3=sQuery(id+"F3.wireOp",EDGE,"E153.top");
            var Q4;
            Q4=sQuery(id+"F3.wireOp",EDGE,"E147.MirrorCS");
            extrude(context, id + "F9", {"entities" : qUnion([Q0, Q1]), "operationType" : NewBodyOperationType.REMOVE, "surfaceEntities" : qUnion([Q2, Q3, Q4]), "oppositeDirection" : true, "depth" : 730 * mm, "offsetDistance" : 25 * mm, "symmetric" : true});
        }
        {
            var Q0;
            Q0=makeQuery(id+"F4.imprint","IMPRINT",FACE,{"disambiguationData":[TD([[makeQuery(id+"F4.imprint","IMPRINT",EDGE,{"derivedFrom":sQuery(id+"F4.wireOp",EDGE,"E186.MirrorCS")}),-1.0]])]});
            var Q1;
            Q1=makeQuery(id+"F4.imprint","IMPRINT",FACE,{"disambiguationData":[TD([[makeQuery(id+"F4.imprint","IMPRINT",EDGE,{"derivedFrom":sQuery(id+"F4.wireOp",EDGE,"E179")}),-1.0]])]});
            extrude(context, id + "F10", {"entities" : qUnion([Q0, Q1]), "operationType" : NewBodyOperationType.REMOVE, "oppositeDirection" : true, "depth" : 400 * mm, "offsetDistance" : 25 * mm, "symmetric" : true});
        }
        {
            var Q0;
            Q0=makeQuery(id+"F4.imprint","IMPRINT",FACE,{"disambiguationData":[TD([[makeQuery(id+"F4.imprint","IMPRINT",EDGE,{"derivedFrom":sQuery(id+"F4.wireOp",EDGE,"E172")}),-1.0]])]});
            var Q1;
            {var subQ5=sQuery(id+"F4.wireOp",EDGE,"E199");Q1=makeQuery(id+"F4.imprint","IMPRINT",FACE,{"disambiguationData":[TD([[makeQuery(id+"F4.imprint","IMPRINT",EDGE,{"derivedFrom":subQ5}),-1.0]])]});}
            var Q2;
            {var subQ5=sQuery(id+"F4.wireOp",EDGE,"E200.MirrorCS");Q2=makeQuery(id+"F4.imprint","IMPRINT",FACE,{"disambiguationData":[TD([[makeQuery(id+"F4.imprint","IMPRINT",EDGE,{"derivedFrom":subQ5}),1.0]])]});}
            var Q3;
            {var subQ2=sQuery(id+"F4.wireOp",EDGE,"E175");Q3=makeQuery(id+"F4.imprint","IMPRINT",FACE,{"disambiguationData":[TD([[makeQuery(id+"F4.imprint","IMPRINT",EDGE,{"derivedFrom":subQ2}),1.0]])]});}
            var Q4;
            {var subQ0=sQuery(id+"F4.wireOp",EDGE,"E194.MirrorCS");Q4=makeQuery(id+"F4.imprint","IMPRINT",FACE,{"disambiguationData":[TD([[makeQuery(id+"F4.imprint","IMPRINT",EDGE,{"derivedFrom":subQ0}),1.0]])]});}
            var Q5;
            {var subQ1=sQuery(id+"F4.wireOp",EDGE,"E191");Q5=makeQuery(id+"F4.imprint","IMPRINT",FACE,{"disambiguationData":[TD([[makeQuery(id+"F4.imprint","IMPRINT",EDGE,{"derivedFrom":subQ1}),-1.0]])]});}
            extrude(context, id + "F11", {"entities" : qUnion([Q0, Q1, Q2, Q3, Q4, Q5]), "operationType" : NewBodyOperationType.ADD, "depth" : 169 * mm, "offsetDistance" : 25 * mm, "symmetric" : true});
        }
        {
            var Q0;
            Q0=makeQuery(id+"F4.imprint","IMPRINT",FACE,{"disambiguationData":[TD([[makeQuery(id+"F4.imprint","IMPRINT",EDGE,{"derivedFrom":sQuery(id+"F4.wireOp",EDGE,"E180")}),-1.0]])]});
            var Q1;
            Q1=makeQuery(id+"F4.imprint","IMPRINT",FACE,{"disambiguationData":[TD([[makeQuery(id+"F4.imprint","IMPRINT",EDGE,{"derivedFrom":sQuery(id+"F4.wireOp",EDGE,"E184.MirrorCS")}),1.0]])]});
            extrude(context, id + "F12", {"entities" : qUnion([Q0, Q1]), "operationType" : NewBodyOperationType.ADD, "depth" : 295 * mm, "offsetDistance" : 25 * mm, "symmetric" : true});
        }
        {
            var Q0;
            {var subQ0=sQuery(id+"F4.wireOp",EDGE,"E203.MirrorCS");Q0=makeQuery(id+"F4.imprint","IMPRINT",FACE,{"disambiguationData":[TD([[makeQuery(id+"F4.imprint","IMPRINT",EDGE,{"derivedFrom":subQ0}),-1.0]])]});}
            var Q1;
            {var subQ0=sQuery(id+"F4.wireOp",EDGE,"E202");Q1=makeQuery(id+"F4.imprint","IMPRINT",FACE,{"disambiguationData":[TD([[makeQuery(id+"F4.imprint","IMPRINT",EDGE,{"derivedFrom":subQ0}),1.0]])]});}
            extrude(context, id + "F13", {"entities" : qUnion([Q0, Q1]), "operationType" : NewBodyOperationType.ADD, "depth" : 350 * mm, "offsetDistance" : 25 * mm, "symmetric" : true});
        }
        {
            var Q0;
            {var subQ0=sQuery(id+"F2.wireOp",EDGE,"E122.MirrorCS");var subQ1=sQuery(id+"F2.wireOp",EDGE,"E91");Q0=makeQuery(id+"F10.boolean.opBoolean","SPLIT",EDGE,{"disambiguationData":[TD([makeQuery(id+"F9.boolean.opBoolean","COPY",FACE,{"derivedFrom":makeQuery(id+"F9.opExtrude","SWEPT_FACE",FACE,{"disambiguationData":[OSD([sQuery(id+"F3.wireOp",EDGE,"E136")])]})})])],"derivedFrom":makeQuery(id+"F5.opExtrude","CAP_EDGE",EDGE,{"disambiguationData":[OSD([subQ1,subQ0])],"isStart":false})});}
            var Q1;
            {var subQ0=sQuery(id+"F2.wireOp",EDGE,"E122.MirrorCS");var subQ1=sQuery(id+"F2.wireOp",EDGE,"E91");Q1=makeQuery(id+"F10.boolean.opBoolean","SPLIT",EDGE,{"disambiguationData":[TD([makeQuery(id+"F9.boolean.opBoolean","COPY",FACE,{"derivedFrom":makeQuery(id+"F9.opExtrude","SWEPT_FACE",FACE,{"disambiguationData":[OSD([sQuery(id+"F3.wireOp",EDGE,"E147.MirrorCS")])]})})])],"derivedFrom":makeQuery(id+"F5.opExtrude","CAP_EDGE",EDGE,{"disambiguationData":[OSD([subQ1,subQ0])],"isStart":false})});}
            var Q2;
            {var subQ0=sQuery(id+"F2.wireOp",EDGE,"E110.MirrorCS");var subQ1=sQuery(id+"F2.wireOp",EDGE,"E103.MirrorCS");Q2=makeQuery(id+"F10.boolean.opBoolean","SPLIT",EDGE,{"disambiguationData":[TD([makeQuery(id+"F9.boolean.opBoolean","COPY",FACE,{"derivedFrom":makeQuery(id+"F9.opExtrude","SWEPT_FACE",FACE,{"disambiguationData":[OSD([sQuery(id+"F3.wireOp",EDGE,"E147.MirrorCS")])]})})])],"derivedFrom":makeQuery(id+"F5.opExtrude","CAP_EDGE",EDGE,{"disambiguationData":[OSD([subQ1,subQ0])],"isStart":false})});}
            var Q3;
            {var subQ0=sQuery(id+"F2.wireOp",EDGE,"E110.MirrorCS");var subQ1=sQuery(id+"F2.wireOp",EDGE,"E103.MirrorCS");Q3=makeQuery(id+"F10.boolean.opBoolean","SPLIT",EDGE,{"disambiguationData":[TD([makeQuery(id+"F9.boolean.opBoolean","COPY",FACE,{"derivedFrom":makeQuery(id+"F9.opExtrude","SWEPT_FACE",FACE,{"disambiguationData":[OSD([sQuery(id+"F3.wireOp",EDGE,"E136")])]})})])],"derivedFrom":makeQuery(id+"F5.opExtrude","CAP_EDGE",EDGE,{"disambiguationData":[OSD([subQ1,subQ0])],"isStart":false})});}
            fillet(context, id + "F14", {"entities" : qUnion([Q0, Q1, Q2, Q3]), "radius" : 18 * mm, "tangentPropagation" : true, "allowEdgeOverflow" : false});
        }
        {
            var Q0;
            {var subQ0=sQuery(id+"F3.wireOp",EDGE,"E162.MirrorCS");Q0=makeQuery(id+"F3.imprint","IMPRINT",FACE,{"disambiguationData":[TD([[makeQuery(id+"F3.imprint","IMPRINT",EDGE,{"derivedFrom":subQ0}),-1.0]])]});}
            var Q1;
            {var subQ0=sQuery(id+"F3.wireOp",EDGE,"E156");Q1=makeQuery(id+"F3.imprint","IMPRINT",FACE,{"disambiguationData":[TD([[makeQuery(id+"F3.imprint","IMPRINT",EDGE,{"derivedFrom":subQ0}),1.0]])]});}
            extrude(context, id + "F15", {"entities" : qUnion([Q0, Q1]), "operationType" : NewBodyOperationType.ADD, "depth" : 670 * mm, "offsetDistance" : 25 * mm, "symmetric" : true});
        }
        {
            var Q0;
            {var subQ0=sQuery(id+"F3.wireOp",EDGE,"E156");Q0=makeQuery(id+"F3.imprint","IMPRINT",FACE,{"disambiguationData":[TD([[makeQuery(id+"F3.imprint","IMPRINT",EDGE,{"derivedFrom":subQ0}),-1.0]])]});}
            var Q1;
            {var subQ0=sQuery(id+"F3.wireOp",EDGE,"E162.MirrorCS");Q1=makeQuery(id+"F3.imprint","IMPRINT",FACE,{"disambiguationData":[TD([[makeQuery(id+"F3.imprint","IMPRINT",EDGE,{"derivedFrom":subQ0}),1.0]])]});}
            extrude(context, id + "F16", {"entities" : qUnion([Q0, Q1]), "operationType" : NewBodyOperationType.ADD, "depth" : 630 * mm, "offsetDistance" : 25 * mm, "symmetric" : true});
        }
        {
            var Q0;
            {var subQ0=sQuery(id+"F3.wireOp",EDGE,"E166.MirrorCS");Q0=makeQuery(id+"F3.imprint","IMPRINT",FACE,{"disambiguationData":[TD([[makeQuery(id+"F3.imprint","IMPRINT",EDGE,{"derivedFrom":subQ0}),-1.0]])]});}
            var Q1;
            {var subQ0=sQuery(id+"F3.wireOp",EDGE,"E157");Q1=makeQuery(id+"F3.imprint","IMPRINT",FACE,{"disambiguationData":[TD([[makeQuery(id+"F3.imprint","IMPRINT",EDGE,{"derivedFrom":subQ0}),1.0]])]});}
            extrude(context, id + "F17", {"entities" : qUnion([Q0, Q1]), "operationType" : NewBodyOperationType.ADD, "depth" : 550 * mm, "offsetDistance" : 25 * mm, "symmetric" : true});
        }
        {
            var Q0;
            {var subQ0=sQuery(id+"F3.wireOp",EDGE,"E158");Q0=makeQuery(id+"F3.imprint","IMPRINT",FACE,{"disambiguationData":[TD([[makeQuery(id+"F3.imprint","IMPRINT",EDGE,{"derivedFrom":subQ0}),-1.0]])]});}
            var Q1;
            {var subQ0=sQuery(id+"F3.wireOp",EDGE,"E165.MirrorCS");Q1=makeQuery(id+"F3.imprint","IMPRINT",FACE,{"disambiguationData":[TD([[makeQuery(id+"F3.imprint","IMPRINT",EDGE,{"derivedFrom":subQ0}),-1.0]])]});}
            extrude(context, id + "F18", {"entities" : qUnion([Q0, Q1]), "operationType" : NewBodyOperationType.ADD, "depth" : 600 * mm, "offsetDistance" : 25 * mm, "symmetric" : true});
        }
        {
            var Q0;
            {var subQ0=sQuery(id+"F3.wireOp",EDGE,"E159");Q0=makeQuery(id+"F3.imprint","IMPRINT",FACE,{"disambiguationData":[TD([[makeQuery(id+"F3.imprint","IMPRINT",EDGE,{"derivedFrom":subQ0}),-1.0]])]});}
            var Q1;
            {var subQ0=sQuery(id+"F3.wireOp",EDGE,"E164.MirrorCS");Q1=makeQuery(id+"F3.imprint","IMPRINT",FACE,{"disambiguationData":[TD([[makeQuery(id+"F3.imprint","IMPRINT",EDGE,{"derivedFrom":subQ0}),-1.0]])]});}
            extrude(context, id + "F19", {"entities" : qUnion([Q0, Q1]), "operationType" : NewBodyOperationType.ADD, "depth" : 620 * mm, "offsetDistance" : 25 * mm, "symmetric" : true});
        }
        {
            var Q0;
            {var subQ0=sQuery(id+"F3.wireOp",EDGE,"E163.MirrorCS");Q0=makeQuery(id+"F3.imprint","IMPRINT",FACE,{"disambiguationData":[TD([[makeQuery(id+"F3.imprint","IMPRINT",EDGE,{"derivedFrom":subQ0}),-1.0]])]});}
            var Q1;
            {var subQ0=sQuery(id+"F3.wireOp",EDGE,"E160");Q1=makeQuery(id+"F3.imprint","IMPRINT",FACE,{"disambiguationData":[TD([[makeQuery(id+"F3.imprint","IMPRINT",EDGE,{"derivedFrom":subQ0}),-1.0]])]});}
            extrude(context, id + "F20", {"entities" : qUnion([Q0, Q1]), "operationType" : NewBodyOperationType.ADD, "depth" : 620 * mm, "offsetDistance" : 25 * mm, "symmetric" : true});
        }
        {
            var Q0;
            Q0=makeQuery(id+"F5.opExtrude","CAP_EDGE",EDGE,{"disambiguationData":[OSD([sQuery(id+"F2.wireOp",EDGE,"E124.MirrorCS")])],"isStart":false});
            var Q1;
            Q1=makeQuery(id+"F5.opExtrude","CAP_EDGE",EDGE,{"disambiguationData":[OSD([sQuery(id+"F2.wireOp",EDGE,"E123.MirrorCS")])],"isStart":false});
            var Q2;
            Q2=makeQuery(id+"F5.opExtrude","CAP_EDGE",EDGE,{"disambiguationData":[OSD([sQuery(id+"F2.wireOp",EDGE,"E90.trimOffspring")])],"isStart":false});
            var Q3;
            Q3=makeQuery(id+"F5.opExtrude","CAP_EDGE",EDGE,{"disambiguationData":[OSD([sQuery(id+"F2.wireOp",EDGE,"E102.MirrorCS")])],"isStart":false});
            chamfer(context, id + "F21", {"entities" : qUnion([Q0, Q1, Q2, Q3]), "chamferType" : ChamferType.OFFSET_ANGLE, "width" : 15 * mm, "oppositeDirection" : false, "angle" : 35 * degree, "tangentPropagation" : true});
        }
        {
            var Q0;
            {var subQ0=sQuery(id+"F4.wireOp",EDGE,"E198.MirrorCS");var subQ1=sQuery(id+"F4.wireOp",EDGE,"E186.MirrorCS");var subQ2=sQuery(id+"F4.wireOp",EDGE,"E185.MirrorCS");Q0=makeQuery(id+"F11.boolean.opBoolean","MERGE",EDGE,{"derivedFrom":[makeQuery(id+"F8.opExtrude","SWEPT_EDGE",EDGE,{"disambiguationData":[OSD([subQ2,subQ1,subQ0])]}),makeQuery(id+"F11.opExtrude","SWEPT_EDGE",EDGE,{"disambiguationData":[OSD([subQ2,subQ1,subQ0])]})]});}
            chamfer(context, id + "F22", {"entities" : qUnion([Q0]), "chamferType" : ChamferType.OFFSET_ANGLE, "width" : 10 * mm, "oppositeDirection" : false, "angle" : 42 * degree, "tangentPropagation" : true});
        }
        {
            var Q0;
            {var subQ0=sQuery(id+"F4.wireOp",EDGE,"E196");var subQ1=sQuery(id+"F4.wireOp",EDGE,"E179");var subQ2=sQuery(id+"F4.wireOp",EDGE,"E174");Q0=makeQuery(id+"F11.boolean.opBoolean","MERGE",EDGE,{"derivedFrom":[makeQuery(id+"F8.opExtrude","SWEPT_EDGE",EDGE,{"disambiguationData":[OSD([subQ2,subQ1,subQ0])]}),makeQuery(id+"F11.opExtrude","SWEPT_EDGE",EDGE,{"disambiguationData":[OSD([subQ2,subQ1,subQ0])]})]});}
            chamfer(context, id + "F23", {"entities" : qUnion([Q0]), "chamferType" : ChamferType.OFFSET_ANGLE, "width" : 10 * mm, "oppositeDirection" : false, "angle" : 42 * degree, "tangentPropagation" : true});
        }
        {
            var Q0;
            {var subQ0=sQuery(id+"F0.wireOp",EDGE,"E35.top");var subQ1=sQuery(id+"F0.wireOp",EDGE,"E34.MirrorC");var subQ2=makeQuery(id+"F0.imprint","INTERSECT",VERTEX,{"derivedFrom":[subQ1,subQ0]});Q0=makeQuery(id+"F0.imprint","IMPRINT",FACE,{"disambiguationData":[TD([[makeQuery(id+"F0.imprint","IMPRINT",EDGE,{"disambiguationData":[TD([[subQ2,1.0]])],"derivedFrom":subQ1}),1.0]])]});}
            var Q1;
            {var subQ0=sQuery(id+"F0.wireOp",EDGE,"E10");var subQ3=sQuery(id+"F0.wireOp",EDGE,"E1");var subQ5=makeQuery(id+"F0.imprint","INTERSECT",VERTEX,{"disambiguationData":[OD(0.0)],"derivedFrom":[subQ3,subQ0]});Q1=makeQuery(id+"F0.imprint","IMPRINT",FACE,{"disambiguationData":[TD([[makeQuery(id+"F0.imprint","IMPRINT",EDGE,{"disambiguationData":[TD([[subQ5,-1.0]])],"derivedFrom":subQ3}),-1.0]])]});}
            var Q2;
            {var subQ0=sQuery(id+"F0.wireOp",EDGE,"E36");var subQ1=sQuery(id+"F0.wireOp",EDGE,"E0.right");var subQ2=makeQuery(id+"F0.imprint","INTERSECT",VERTEX,{"derivedFrom":[subQ1,subQ0]});Q2=makeQuery(id+"F0.imprint","IMPRINT",FACE,{"disambiguationData":[TD([[makeQuery(id+"F0.imprint","IMPRINT",EDGE,{"disambiguationData":[TD([[subQ2,1.0]])],"derivedFrom":subQ1}),-1.0]])]});}
            var Q3;
            {var subQ1=sQuery(id+"F0.wireOp",EDGE,"E0.left");var subQ3=sQuery(id+"F0.wireOp",EDGE,"E2.MirrorCS");var subQ4=makeQuery(id+"F0.imprint","INTERSECT",VERTEX,{"disambiguationData":[OD(1.0)],"derivedFrom":[subQ1,subQ3]});Q3=makeQuery(id+"F0.imprint","IMPRINT",FACE,{"disambiguationData":[TD([[makeQuery(id+"F0.imprint","IMPRINT",EDGE,{"disambiguationData":[TD([[subQ4,-1.0]])],"derivedFrom":subQ3}),-1.0]])]});}
            var Q4;
            {var subQ1=sQuery(id+"F0.wireOp",EDGE,"E0.left");var subQ3=sQuery(id+"F0.wireOp",EDGE,"E3.MirrorCS");var subQ4=makeQuery(id+"F0.imprint","INTERSECT",VERTEX,{"derivedFrom":[subQ1,subQ3]});Q4=makeQuery(id+"F0.imprint","IMPRINT",FACE,{"disambiguationData":[TD([[makeQuery(id+"F0.imprint","IMPRINT",EDGE,{"disambiguationData":[TD([[subQ4,1.0]])],"derivedFrom":subQ3}),-1.0]])]});}
            var Q5;
            {var subQ0=sQuery(id+"F0.wireOp",EDGE,"E9");var subQ1=sQuery(id+"F0.wireOp",EDGE,"E0.right");var subQ2=makeQuery(id+"F0.imprint","INTERSECT",VERTEX,{"derivedFrom":[subQ1,subQ0]});Q5=makeQuery(id+"F0.imprint","IMPRINT",FACE,{"disambiguationData":[TD([[makeQuery(id+"F0.imprint","IMPRINT",EDGE,{"disambiguationData":[TD([[subQ2,-1.0]])],"derivedFrom":subQ1}),-1.0]])]});}
            var Q6;
            Q6=makeQuery(id+"F0.imprint","IMPRINT",FACE,{"disambiguationData":[TD([[makeQuery(id+"F0.imprint","IMPRINT",EDGE,{"derivedFrom":sQuery(id+"F0.wireOp",EDGE,"E23")}),1.0]])]});
            var Q7;
            Q7=makeQuery(id+"F0.imprint","IMPRINT",FACE,{"disambiguationData":[TD([[makeQuery(id+"F0.imprint","IMPRINT",EDGE,{"derivedFrom":sQuery(id+"F0.wireOp",EDGE,"E21")}),1.0]])]});
            var Q8;
            Q8=makeQuery(id+"F0.imprint","IMPRINT",FACE,{"disambiguationData":[TD([[makeQuery(id+"F0.imprint","IMPRINT",EDGE,{"derivedFrom":sQuery(id+"F0.wireOp",EDGE,"E22")}),1.0]])]});
            var Q9;
            Q9=makeQuery(id+"F0.imprint","IMPRINT",FACE,{"disambiguationData":[TD([[makeQuery(id+"F0.imprint","IMPRINT",EDGE,{"derivedFrom":sQuery(id+"F0.wireOp",EDGE,"E24.MirrorC")}),-1.0]])]});
            var Q10;
            Q10=makeQuery(id+"F0.imprint","IMPRINT",FACE,{"disambiguationData":[TD([[makeQuery(id+"F0.imprint","IMPRINT",EDGE,{"derivedFrom":sQuery(id+"F0.wireOp",EDGE,"E30.MirrorC")}),-1.0]])]});
            var Q11;
            Q11=makeQuery(id+"F0.imprint","IMPRINT",FACE,{"disambiguationData":[TD([[makeQuery(id+"F0.imprint","IMPRINT",EDGE,{"derivedFrom":sQuery(id+"F0.wireOp",EDGE,"E31.MirrorC")}),-1.0]])]});
            var Q12;
            Q12=makeQuery(id+"F0.imprint","IMPRINT",FACE,{"disambiguationData":[TD([[makeQuery(id+"F0.imprint","IMPRINT",EDGE,{"derivedFrom":sQuery(id+"F0.wireOp",EDGE,"E33.MirrorC")}),1.0]])]});
            var Q13;
            Q13=makeQuery(id+"F0.imprint","IMPRINT",FACE,{"disambiguationData":[TD([[makeQuery(id+"F0.imprint","IMPRINT",EDGE,{"derivedFrom":sQuery(id+"F0.wireOp",EDGE,"E32.MirrorC")}),-1.0]])]});
            var Q14;
            Q14=makeQuery(id+"F0.imprint","IMPRINT",FACE,{"disambiguationData":[TD([[makeQuery(id+"F0.imprint","IMPRINT",EDGE,{"derivedFrom":sQuery(id+"F0.wireOp",EDGE,"E19")}),1.0]])]});
            var Q15;
            Q15=makeQuery(id+"F0.imprint","IMPRINT",FACE,{"disambiguationData":[TD([[makeQuery(id+"F0.imprint","IMPRINT",EDGE,{"derivedFrom":sQuery(id+"F0.wireOp",EDGE,"E20")}),1.0]])]});
            var Q16;
            Q16=makeQuery(id+"F0.imprint","IMPRINT",FACE,{"disambiguationData":[TD([[makeQuery(id+"F0.imprint","IMPRINT",EDGE,{"derivedFrom":sQuery(id+"F0.wireOp",EDGE,"E17")}),1.0]])]});
            var Q17;
            Q17=makeQuery(id+"F0.imprint","IMPRINT",FACE,{"disambiguationData":[TD([[makeQuery(id+"F0.imprint","IMPRINT",EDGE,{"derivedFrom":sQuery(id+"F0.wireOp",EDGE,"E18")}),1.0]])]});
            var Q18;
            Q18=makeQuery(id+"F0.imprint","IMPRINT",FACE,{"disambiguationData":[TD([[makeQuery(id+"F0.imprint","IMPRINT",EDGE,{"derivedFrom":sQuery(id+"F0.wireOp",EDGE,"E16")}),1.0]])]});
            var Q19;
            Q19=makeQuery(id+"F0.imprint","IMPRINT",FACE,{"disambiguationData":[TD([[makeQuery(id+"F0.imprint","IMPRINT",EDGE,{"derivedFrom":sQuery(id+"F0.wireOp",EDGE,"E28.MirrorC")}),-1.0]])]});
            var Q20;
            Q20=makeQuery(id+"F0.imprint","IMPRINT",FACE,{"disambiguationData":[TD([[makeQuery(id+"F0.imprint","IMPRINT",EDGE,{"derivedFrom":sQuery(id+"F0.wireOp",EDGE,"E27.MirrorC")}),-1.0]])]});
            var Q21;
            Q21=makeQuery(id+"F0.imprint","IMPRINT",FACE,{"disambiguationData":[TD([[makeQuery(id+"F0.imprint","IMPRINT",EDGE,{"derivedFrom":sQuery(id+"F0.wireOp",EDGE,"E25.MirrorC")}),-1.0]])]});
            var Q22;
            Q22=makeQuery(id+"F0.imprint","IMPRINT",FACE,{"disambiguationData":[TD([[makeQuery(id+"F0.imprint","IMPRINT",EDGE,{"derivedFrom":sQuery(id+"F0.wireOp",EDGE,"E26.MirrorC")}),-1.0]])]});
            var Q23;
            Q23=makeQuery(id+"F0.imprint","IMPRINT",FACE,{"disambiguationData":[TD([[makeQuery(id+"F0.imprint","IMPRINT",EDGE,{"derivedFrom":sQuery(id+"F0.wireOp",EDGE,"E29.MirrorC")}),-1.0]])]});
            var Q24;
            {var subQ5=sQuery(id+"F0.wireOp",EDGE,"E7");Q24=makeQuery(id+"F0.imprint","IMPRINT",FACE,{"disambiguationData":[TD([[makeQuery(id+"F0.imprint","IMPRINT",EDGE,{"derivedFrom":subQ5}),-1.0]])]});}
            var Q25;
            {var subQ0=sQuery(id+"F0.wireOp",EDGE,"E37");var subQ1=sQuery(id+"F0.wireOp",EDGE,"E0.right");var subQ2=makeQuery(id+"F0.imprint","INTERSECT",VERTEX,{"derivedFrom":[subQ1,subQ0]});Q25=makeQuery(id+"F0.imprint","IMPRINT",FACE,{"disambiguationData":[TD([[makeQuery(id+"F0.imprint","IMPRINT",EDGE,{"disambiguationData":[TD([[subQ2,-1.0]])],"derivedFrom":subQ1}),-1.0]])]});}
            var Q26;
            {var subQ5=sQuery(id+"F0.wireOp",EDGE,"E6");Q26=makeQuery(id+"F0.imprint","IMPRINT",FACE,{"disambiguationData":[TD([[makeQuery(id+"F0.imprint","IMPRINT",EDGE,{"derivedFrom":subQ5}),1.0]])]});}
            var Q27;
            Q27=makeQuery(id+"F0.imprint","IMPRINT",FACE,{"disambiguationData":[TD([[makeQuery(id+"F0.imprint","IMPRINT",EDGE,{"derivedFrom":sQuery(id+"F0.wireOp",EDGE,"E46.MirrorC")}),-1.0]])]});
            var Q28;
            Q28=makeQuery(id+"F0.imprint","IMPRINT",FACE,{"disambiguationData":[TD([[makeQuery(id+"F0.imprint","IMPRINT",EDGE,{"derivedFrom":sQuery(id+"F0.wireOp",EDGE,"E45")}),1.0]])]});
            var Q29;
            {var subQ0=sQuery(id+"F0.wireOp",EDGE,"E47.MirrorC");var subQ1=sQuery(id+"F0.wireOp",EDGE,"E35.top");var subQ2=makeQuery(id+"F0.imprint","INTERSECT",VERTEX,{"disambiguationData":[OD(0.0)],"derivedFrom":[subQ1,subQ0]});Q29=makeQuery(id+"F0.imprint","IMPRINT",FACE,{"disambiguationData":[TD([[makeQuery(id+"F0.imprint","IMPRINT",EDGE,{"disambiguationData":[TD([[subQ2,-1.0]])],"derivedFrom":subQ1}),1.0]])]});}
            var Q30;
            {var subQ0=sQuery(id+"F0.wireOp",EDGE,"E48.MirrorC");var subQ1=sQuery(id+"F0.wireOp",EDGE,"E35.bottom");var subQ2=makeQuery(id+"F0.imprint","INTERSECT",VERTEX,{"disambiguationData":[OD(0.0)],"derivedFrom":[subQ1,subQ0]});Q30=makeQuery(id+"F0.imprint","IMPRINT",FACE,{"disambiguationData":[TD([[makeQuery(id+"F0.imprint","IMPRINT",EDGE,{"disambiguationData":[TD([[subQ2,-1.0]])],"derivedFrom":subQ1}),-1.0]])]});}
            var Q31;
            {var subQ0=sQuery(id+"F0.wireOp",EDGE,"E49.MirrorC");var subQ1=sQuery(id+"F0.wireOp",EDGE,"E35.top");var subQ2=makeQuery(id+"F0.imprint","INTERSECT",VERTEX,{"disambiguationData":[OD(0.0)],"derivedFrom":[subQ1,subQ0]});Q31=makeQuery(id+"F0.imprint","IMPRINT",FACE,{"disambiguationData":[TD([[makeQuery(id+"F0.imprint","IMPRINT",EDGE,{"disambiguationData":[TD([[subQ2,-1.0]])],"derivedFrom":subQ1}),1.0]])]});}
            var Q32;
            {var subQ0=sQuery(id+"F0.wireOp",EDGE,"E50.MirrorC");var subQ1=sQuery(id+"F0.wireOp",EDGE,"E35.top");var subQ2=makeQuery(id+"F0.imprint","INTERSECT",VERTEX,{"disambiguationData":[OD(0.0)],"derivedFrom":[subQ1,subQ0]});Q32=makeQuery(id+"F0.imprint","IMPRINT",FACE,{"disambiguationData":[TD([[makeQuery(id+"F0.imprint","IMPRINT",EDGE,{"disambiguationData":[TD([[subQ2,-1.0]])],"derivedFrom":subQ1}),1.0]])]});}
            var Q33;
            {var subQ0=sQuery(id+"F0.wireOp",EDGE,"E52.MirrorC");var subQ1=sQuery(id+"F0.wireOp",EDGE,"E35.bottom");var subQ2=makeQuery(id+"F0.imprint","INTERSECT",VERTEX,{"disambiguationData":[OD(0.0)],"derivedFrom":[subQ1,subQ0]});Q33=makeQuery(id+"F0.imprint","IMPRINT",FACE,{"disambiguationData":[TD([[makeQuery(id+"F0.imprint","IMPRINT",EDGE,{"disambiguationData":[TD([[subQ2,-1.0]])],"derivedFrom":subQ1}),-1.0]])]});}
            var Q34;
            {var subQ0=sQuery(id+"F0.wireOp",EDGE,"E51.MirrorC");var subQ1=sQuery(id+"F0.wireOp",EDGE,"E35.top");var subQ2=makeQuery(id+"F0.imprint","INTERSECT",VERTEX,{"disambiguationData":[OD(0.0)],"derivedFrom":[subQ1,subQ0]});Q34=makeQuery(id+"F0.imprint","IMPRINT",FACE,{"disambiguationData":[TD([[makeQuery(id+"F0.imprint","IMPRINT",EDGE,{"disambiguationData":[TD([[subQ2,-1.0]])],"derivedFrom":subQ1}),1.0]])]});}
            var Q35;
            {var subQ0=sQuery(id+"F0.wireOp",EDGE,"E35.left");var subQ1=sQuery(id+"F0.wireOp",EDGE,"E35.top");var subQ2=makeQuery(id+"F0.imprint","INTERSECT",VERTEX,{"derivedFrom":[subQ1,subQ0]});Q35=makeQuery(id+"F0.imprint","IMPRINT",FACE,{"disambiguationData":[TD([[makeQuery(id+"F0.imprint","IMPRINT",EDGE,{"disambiguationData":[TD([[subQ2,-1.0]])],"derivedFrom":subQ1}),1.0]])]});}
            var Q36;
            Q36=makeQuery(id+"F0.imprint","IMPRINT",FACE,{"disambiguationData":[TD([[makeQuery(id+"F0.imprint","IMPRINT",EDGE,{"derivedFrom":sQuery(id+"F0.wireOp",EDGE,"E54.MirrorC")}),-1.0]])]});
            var Q37;
            Q37=makeQuery(id+"F0.imprint","IMPRINT",FACE,{"disambiguationData":[TD([[makeQuery(id+"F0.imprint","IMPRINT",EDGE,{"derivedFrom":sQuery(id+"F0.wireOp",EDGE,"E55.MirrorC")}),1.0]])]});
            var Q38;
            Q38=makeQuery(id+"F0.imprint","IMPRINT",FACE,{"disambiguationData":[TD([[makeQuery(id+"F0.imprint","IMPRINT",EDGE,{"derivedFrom":sQuery(id+"F0.wireOp",EDGE,"E64.MirrorC")}),-1.0]])]});
            var Q39;
            Q39=makeQuery(id+"F0.imprint","IMPRINT",FACE,{"disambiguationData":[TD([[makeQuery(id+"F0.imprint","IMPRINT",EDGE,{"derivedFrom":sQuery(id+"F0.wireOp",EDGE,"E63.MirrorC")}),1.0]])]});
            var Q40;
            Q40=makeQuery(id+"F0.imprint","IMPRINT",FACE,{"disambiguationData":[TD([[makeQuery(id+"F0.imprint","IMPRINT",EDGE,{"derivedFrom":sQuery(id+"F0.wireOp",EDGE,"E62.MirrorC")}),1.0]])]});
            var Q41;
            Q41=makeQuery(id+"F0.imprint","IMPRINT",FACE,{"disambiguationData":[TD([[makeQuery(id+"F0.imprint","IMPRINT",EDGE,{"derivedFrom":sQuery(id+"F0.wireOp",EDGE,"E61.MirrorC")}),1.0]])]});
            var Q42;
            Q42=makeQuery(id+"F0.imprint","IMPRINT",FACE,{"disambiguationData":[TD([[makeQuery(id+"F0.imprint","IMPRINT",EDGE,{"derivedFrom":sQuery(id+"F0.wireOp",EDGE,"E60.MirrorC")}),1.0]])]});
            var Q43;
            Q43=makeQuery(id+"F0.imprint","IMPRINT",FACE,{"disambiguationData":[TD([[makeQuery(id+"F0.imprint","IMPRINT",EDGE,{"derivedFrom":sQuery(id+"F0.wireOp",EDGE,"E59.MirrorC")}),1.0]])]});
            var Q44;
            Q44=makeQuery(id+"F0.imprint","IMPRINT",FACE,{"disambiguationData":[TD([[makeQuery(id+"F0.imprint","IMPRINT",EDGE,{"derivedFrom":sQuery(id+"F0.wireOp",EDGE,"E57.MirrorC")}),1.0]])]});
            var Q45;
            Q45=makeQuery(id+"F0.imprint","IMPRINT",FACE,{"disambiguationData":[TD([[makeQuery(id+"F0.imprint","IMPRINT",EDGE,{"derivedFrom":sQuery(id+"F0.wireOp",EDGE,"E56.MirrorC")}),1.0]])]});
            var Q46;
            Q46=makeQuery(id+"F0.imprint","IMPRINT",FACE,{"disambiguationData":[TD([[makeQuery(id+"F0.imprint","IMPRINT",EDGE,{"derivedFrom":sQuery(id+"F0.wireOp",EDGE,"E58.MirrorC")}),1.0]])]});
            var Q47;
            Q47=makeQuery(id+"F0.imprint","IMPRINT",FACE,{"disambiguationData":[TD([[makeQuery(id+"F0.imprint","IMPRINT",EDGE,{"derivedFrom":sQuery(id+"F0.wireOp",EDGE,"E69.MirrorC")}),-1.0]])]});
            var Q48;
            Q48=makeQuery(id+"F0.imprint","IMPRINT",FACE,{"disambiguationData":[TD([[makeQuery(id+"F0.imprint","IMPRINT",EDGE,{"derivedFrom":sQuery(id+"F0.wireOp",EDGE,"E68.MirrorC")}),-1.0]])]});
            var Q49;
            Q49=makeQuery(id+"F0.imprint","IMPRINT",FACE,{"disambiguationData":[TD([[makeQuery(id+"F0.imprint","IMPRINT",EDGE,{"derivedFrom":sQuery(id+"F0.wireOp",EDGE,"E70.MirrorC")}),-1.0]])]});
            var Q50;
            Q50=makeQuery(id+"F0.imprint","IMPRINT",FACE,{"disambiguationData":[TD([[makeQuery(id+"F0.imprint","IMPRINT",EDGE,{"derivedFrom":sQuery(id+"F0.wireOp",EDGE,"E67.MirrorC")}),-1.0]])]});
            var Q51;
            Q51=makeQuery(id+"F0.imprint","IMPRINT",FACE,{"disambiguationData":[TD([[makeQuery(id+"F0.imprint","IMPRINT",EDGE,{"derivedFrom":sQuery(id+"F0.wireOp",EDGE,"E71.MirrorC")}),-1.0]])]});
            var Q52;
            Q52=makeQuery(id+"F0.imprint","IMPRINT",FACE,{"disambiguationData":[TD([[makeQuery(id+"F0.imprint","IMPRINT",EDGE,{"derivedFrom":sQuery(id+"F0.wireOp",EDGE,"E72.MirrorC")}),-1.0]])]});
            var Q53;
            Q53=makeQuery(id+"F0.imprint","IMPRINT",FACE,{"disambiguationData":[TD([[makeQuery(id+"F0.imprint","IMPRINT",EDGE,{"derivedFrom":sQuery(id+"F0.wireOp",EDGE,"E66.MirrorC")}),-1.0]])]});
            var Q54;
            Q54=makeQuery(id+"F0.imprint","IMPRINT",FACE,{"disambiguationData":[TD([[makeQuery(id+"F0.imprint","IMPRINT",EDGE,{"derivedFrom":sQuery(id+"F0.wireOp",EDGE,"E65.MirrorC")}),-1.0]])]});
            var Q55;
            Q55=makeQuery(id+"F0.imprint","IMPRINT",FACE,{"disambiguationData":[TD([[makeQuery(id+"F0.imprint","IMPRINT",EDGE,{"derivedFrom":sQuery(id+"F0.wireOp",EDGE,"E73.MirrorC")}),1.0]])]});
            extrude(context, id + "F24", {"entities" : qUnion([Q0, Q1, Q2, Q3, Q4, Q5, Q6, Q7, Q8, Q9, Q10, Q11, Q12, Q13, Q14, Q15, Q16, Q17, Q18, Q19, Q20, Q21, Q22, Q23, Q24, Q25, Q26, Q27, Q28, Q29, Q30, Q31, Q32, Q33, Q34, Q35, Q36, Q37, Q38, Q39, Q40, Q41, Q42, Q43, Q44, Q45, Q46, Q47, Q48, Q49, Q50, Q51, Q52, Q53, Q54, Q55]), "operationType" : NewBodyOperationType.REMOVE, "depth" : 25 * mm, "offsetDistance" : 25 * mm});
        }
        {
            var Q0;
            Q0=qCreatedBy(makeId("Top.planeOp"),FACE);
            var sketch = newSketch(context, id + "F25", { "sketchPlane" : qUnion([Q0])});
            skLineSegment(sketch, "E212.bottom", {"start": v(-365, -200) * mm, "end": v(365, -200) * mm});
            skLineSegment(sketch, "E212.top", {"start": v(-365, 200) * mm, "end": v(365, 200) * mm});
            skLineSegment(sketch, "E212.left", {"start": v(-365, -200) * mm, "end": v(-365, 200) * mm});
            skLineSegment(sketch, "E212.right", {"start": v(365, -200) * mm, "end": v(365, 200) * mm});
            skPoint(sketch, "E213", {"position": v(0, -200) * mm});
            skPoint(sketch, "E214", {"position": v(-182.5, -200) * mm});
            skPoint(sketch, "E215", {"position": v(182.5, -200) * mm});
            skPoint(sketch, "E216", {"position": v(-365, -50) * mm});
            skPoint(sketch, "E217", {"position": v(-365, 50) * mm});
            skPoint(sketch, "E218", {"position": v(-365, 0) * mm});
            skPoint(sketch, "E219", {"position": v(-365, -125) * mm});
            skPoint(sketch, "E220", {"position": v(-365, -162.5) * mm});
            skPoint(sketch, "E221", {"position": v(-365, -87.5) * mm});
            skLineSegment(sketch, "E222.bottom", {"start": v(-193, 0) * mm, "end": v(-172, 0) * mm});
            skLineSegment(sketch, "E222.right", {"start": v(0, 0) * mm, "end": v(0, -0.5) * mm});
            skLineSegment(sketch, "E223.right", {"start": v(0, -20) * mm, "end": v(0, -20.5) * mm});
            skLineSegment(sketch, "E224.right", {"start": v(0, -20) * mm, "end": v(0, -19.5) * mm});
            skPoint(sketch, "E225", {"position": v(-192.5, -200) * mm});
            skPoint(sketch, "E226", {"position": v(-172.5, -200) * mm});
            skPoint(sketch, "E227", {"position": v(-10, -200) * mm});
            skPoint(sketch, "E228", {"position": v(-365, -60) * mm});
            skPoint(sketch, "E229", {"position": v(-365, -40) * mm});
            skPoint(sketch, "E230", {"position": v(-365, 40) * mm});
            skPoint(sketch, "E231", {"position": v(-365, 60) * mm});
            skLineSegment(sketch, "E232.bottom", {"start": v(-365, -40) * mm, "end": v(-274.25, -40) * mm});
            skLineSegment(sketch, "E232.top", {"start": v(-365, -39.5) * mm, "end": v(-318.88, -39.5) * mm});
            skLineSegment(sketch, "E232.left", {"start": v(-365, -40) * mm, "end": v(-365, -39.5) * mm});
            skLineSegment(sketch, "E232.right", {"start": v(0, -40) * mm, "end": v(0, -39.5) * mm});
            skLineSegment(sketch, "E233.bottom", {"start": v(-193, 0) * mm, "end": v(0, 0) * mm});
            skLineSegment(sketch, "E233.right", {"start": v(0, 0) * mm, "end": v(0, 0.5) * mm});
            skLineSegment(sketch, "E234.bottom", {"start": v(-365, -40) * mm, "end": v(-318.88, -40) * mm});
            skLineSegment(sketch, "E234.top", {"start": v(-365, -40.5) * mm, "end": v(-318.88, -40.5) * mm});
            skLineSegment(sketch, "E234.left", {"start": v(-365, -40) * mm, "end": v(-365, -40.5) * mm});
            skLineSegment(sketch, "E234.right", {"start": v(0, -40) * mm, "end": v(0, -40.5) * mm});
            skLineSegment(sketch, "E235.bottom", {"start": v(-319.87, -60) * mm, "end": v(-273.25, -60) * mm});
            skLineSegment(sketch, "E235.top", {"start": v(-319.87, -59.5) * mm, "end": v(-228.62, -59.5) * mm});
            skLineSegment(sketch, "E235.left", {"start": v(-365, -60) * mm, "end": v(-365, -59.5) * mm});
            skLineSegment(sketch, "E235.right", {"start": v(0, -60) * mm, "end": v(0, -59.5) * mm});
            skLineSegment(sketch, "E236.bottom", {"start": v(-319.87, -60) * mm, "end": v(-228.62, -60) * mm});
            skLineSegment(sketch, "E236.top", {"start": v(-319.87, -60.5) * mm, "end": v(-228.62, -60.5) * mm});
            skLineSegment(sketch, "E236.left", {"start": v(-365, -60) * mm, "end": v(-365, -60.5) * mm});
            skLineSegment(sketch, "E236.right", {"start": v(0, -60) * mm, "end": v(0, -60.5) * mm});
            skLineSegment(sketch, "E237.left", {"start": v(-365, -87.5) * mm, "end": v(-365, -87) * mm});
            skLineSegment(sketch, "E237.right", {"start": v(0, -87.5) * mm, "end": v(0, -87) * mm});
            skLineSegment(sketch, "E238.left", {"start": v(-365, -87.5) * mm, "end": v(-365, -88) * mm});
            skLineSegment(sketch, "E238.right", {"start": v(0, -87.5) * mm, "end": v(0, -88) * mm});
            skLineSegment(sketch, "E239.left", {"start": v(-365, -125) * mm, "end": v(-365, -124.5) * mm});
            skLineSegment(sketch, "E239.right", {"start": v(0, -125) * mm, "end": v(0, -124.5) * mm});
            skLineSegment(sketch, "E240.left", {"start": v(-365, -125) * mm, "end": v(-365, -125.5) * mm});
            skLineSegment(sketch, "E240.right", {"start": v(0, -125) * mm, "end": v(0, -125.5) * mm});
            skLineSegment(sketch, "E241.left", {"start": v(-365, -162.5) * mm, "end": v(-365, -162) * mm});
            skLineSegment(sketch, "E241.right", {"start": v(0, -162.5) * mm, "end": v(0, -162) * mm});
            skLineSegment(sketch, "E242.left", {"start": v(-365, -162.5) * mm, "end": v(-365, -163) * mm});
            skLineSegment(sketch, "E242.right", {"start": v(0, -162.5) * mm, "end": v(0, -163) * mm});
            skLineSegment(sketch, "E243.bottom", {"start": v(-192.5, -200) * mm, "end": v(-193, -200) * mm});
            skLineSegment(sketch, "E243.top", {"start": v(-192.5, 0) * mm, "end": v(-193, 0) * mm});
            skLineSegment(sketch, "E243.left", {"start": v(-192.5, -200) * mm, "end": v(-192.5, -87) * mm});
            skLineSegment(sketch, "E243.right", {"start": v(-193, -200) * mm, "end": v(-193, -87) * mm});
            skLineSegment(sketch, "E244.bottom", {"start": v(-192.5, -200) * mm, "end": v(-192, -200) * mm});
            skLineSegment(sketch, "E244.top", {"start": v(-192.5, 0) * mm, "end": v(-192, 0) * mm});
            skLineSegment(sketch, "E244.right", {"start": v(-192, -200) * mm, "end": v(-192, -87) * mm});
            skLineSegment(sketch, "E245.bottom", {"start": v(-182.5, -200) * mm, "end": v(-183, -200) * mm});
            skLineSegment(sketch, "E245.top", {"start": v(-182.5, 0) * mm, "end": v(-183, 0) * mm});
            skLineSegment(sketch, "E245.left", {"start": v(-182.5, -200) * mm, "end": v(-182.5, -87) * mm});
            skLineSegment(sketch, "E245.right", {"start": v(-183, -200) * mm, "end": v(-183, -87.5) * mm});
            skLineSegment(sketch, "E246.bottom", {"start": v(-182.5, -200) * mm, "end": v(-182, -200) * mm});
            skLineSegment(sketch, "E246.top", {"start": v(-182.5, 0) * mm, "end": v(-182, 0) * mm});
            skLineSegment(sketch, "E246.right", {"start": v(-182, -200) * mm, "end": v(-182, -87) * mm});
            skLineSegment(sketch, "E247.bottom", {"start": v(-172.5, -200) * mm, "end": v(-173, -200) * mm});
            skLineSegment(sketch, "E247.top", {"start": v(-172.5, 0) * mm, "end": v(-173, 0) * mm});
            skLineSegment(sketch, "E247.left", {"start": v(-172.5, -200) * mm, "end": v(-172.5, -59.5) * mm});
            skLineSegment(sketch, "E248.bottom", {"start": v(-172.5, -200) * mm, "end": v(-172, -200) * mm});
            skLineSegment(sketch, "E248.top", {"start": v(-172.5, 0) * mm, "end": v(-172, 0) * mm});
            skLineSegment(sketch, "E248.left", {"start": v(-172.5, -163.05) * mm, "end": v(-172.5, -60) * mm});
            skLineSegment(sketch, "E248.right", {"start": v(-172, -200) * mm, "end": v(-172, -59.5) * mm});
            skLineSegment(sketch, "E249.bottom", {"start": v(0, -200) * mm, "end": v(-0.5, -200) * mm});
            skLineSegment(sketch, "E249.top", {"start": v(0, 0) * mm, "end": v(-0.5, 0) * mm});
            skLineSegment(sketch, "E249.left", {"start": v(0, -200) * mm, "end": v(0, 0) * mm});
            skLineSegment(sketch, "E249.right", {"start": v(-0.5, -200) * mm, "end": v(-0.5, 0) * mm});
            skLineSegment(sketch, "E250.bottom", {"start": v(-10, -200) * mm, "end": v(-9.5, -200) * mm});
            skLineSegment(sketch, "E250.top", {"start": v(-10, 0) * mm, "end": v(-9.5, 0) * mm});
            skLineSegment(sketch, "E250.left", {"start": v(-10, -200) * mm, "end": v(-10, 0) * mm});
            skLineSegment(sketch, "E250.right", {"start": v(-9.5, -200) * mm, "end": v(-9.5, 0) * mm});
            skLineSegment(sketch, "E251.bottom", {"start": v(-10, -200) * mm, "end": v(-10.5, -200) * mm});
            skLineSegment(sketch, "E251.top", {"start": v(-10, 0) * mm, "end": v(-10.5, 0) * mm});
            skLineSegment(sketch, "E251.right", {"start": v(-10.5, -200) * mm, "end": v(-10.5, 0) * mm});
            skLineSegment(sketch, "E252.top", {"start": v(-319.87, -50.5) * mm, "end": v(-318.87, -50.5) * mm});
            skLineSegment(sketch, "E252.left", {"start": v(-365, -50) * mm, "end": v(-365, -50.5) * mm});
            skLineSegment(sketch, "E252.right", {"start": v(0, -50) * mm, "end": v(0, -50.5) * mm});
            skLineSegment(sketch, "E253.bottom", {"start": v(-319.87, -50) * mm, "end": v(-318.87, -50) * mm});
            skLineSegment(sketch, "E253.top", {"start": v(-319.87, -49.5) * mm, "end": v(-318.87, -49.5) * mm});
            skLineSegment(sketch, "E253.left", {"start": v(-365, -50) * mm, "end": v(-365, -49.5) * mm});
            skLineSegment(sketch, "E253.right", {"start": v(0, -50) * mm, "end": v(0, -49.5) * mm});
            skLineSegment(sketch, "E254.trimOffspring", {"start": v(-318.87, -60.5) * mm, "end": v(-318.88, -39.5) * mm});
            skLineSegment(sketch, "E255.trimOffspring", {"start": v(-319.87, -60.5) * mm, "end": v(-319.88, -39.5) * mm});
            skLineSegment(sketch, "E256.trimOffspring", {"start": v(-319.37, -60.5) * mm, "end": v(-319.37, -39.5) * mm});
            skLineSegment(sketch, "E257.trimOffspring", {"start": v(-274.25, -60.5) * mm, "end": v(-274.25, -39.5) * mm});
            skLineSegment(sketch, "E258.trimOffspring", {"start": v(-273.25, -60.5) * mm, "end": v(-273.25, -39.5) * mm});
            skLineSegment(sketch, "E259.trimOffspring", {"start": v(-273.75, -60.5) * mm, "end": v(-273.75, -39.5) * mm});
            skLineSegment(sketch, "E260.trimOffspring", {"start": v(-227.62, -60.5) * mm, "end": v(-227.62, -39.5) * mm});
            skLineSegment(sketch, "E261.trimOffspring", {"start": v(-228.12, -60.5) * mm, "end": v(-228.12, -39.5) * mm});
            skLineSegment(sketch, "E262.trimOffspring", {"start": v(-228.62, -60.5) * mm, "end": v(-228.62, -39.5) * mm});
            skLineSegment(sketch, "E263.trimOffspring", {"start": v(-193, -20.5) * mm, "end": v(-172.5, -20.5) * mm});
            skLineSegment(sketch, "E264.trimOffspring", {"start": v(-193, -19.5) * mm, "end": v(-172, -19.5) * mm});
            skLineSegment(sketch, "E265.trimOffspring", {"start": v(-193, -0.5) * mm, "end": v(-172, -0.5) * mm});
            skLineSegment(sketch, "E266.trimOffspring", {"start": v(-193, -20) * mm, "end": v(-172, -20) * mm});
            skLineSegment(sketch, "E267.trimOffspring", {"start": v(-193, -163) * mm, "end": v(-172, -163) * mm});
            skLineSegment(sketch, "E268.trimOffspring", {"start": v(-193, -162.5) * mm, "end": v(-172, -162.5) * mm});
            skLineSegment(sketch, "E269.trimOffspring", {"start": v(-193, -162) * mm, "end": v(-172, -162) * mm});
            skLineSegment(sketch, "E270.trimOffspring", {"start": v(-193, -125) * mm, "end": v(-172, -125) * mm});
            skLineSegment(sketch, "E271.trimOffspring", {"start": v(-193, -124.5) * mm, "end": v(-172, -124.5) * mm});
            skLineSegment(sketch, "E272.trimOffspring", {"start": v(-193, -88) * mm, "end": v(-172, -88) * mm});
            skLineSegment(sketch, "E273.trimOffspring", {"start": v(-193, -87.5) * mm, "end": v(-172, -87.5) * mm});
            skLineSegment(sketch, "E274.trimOffspring", {"start": v(-193, -125.5) * mm, "end": v(-172, -125.5) * mm});
            skLineSegment(sketch, "E275.trimOffspring", {"start": v(-193, -87) * mm, "end": v(-172, -87) * mm});
            skLineSegment(sketch, "E276.trimOffspring", {"start": v(-137.37, -60.5) * mm, "end": v(-137.37, -39.5) * mm});
            skLineSegment(sketch, "E277.trimOffspring", {"start": v(-136.87, -60.5) * mm, "end": v(-136.87, -39.5) * mm});
            skLineSegment(sketch, "E278.trimOffspring", {"start": v(-91.25, -60.5) * mm, "end": v(-91.25, -40) * mm});
            skLineSegment(sketch, "E279.trimOffspring", {"start": v(-90.75, -60.5) * mm, "end": v(-90.75, -39.5) * mm});
            skLineSegment(sketch, "E280.trimOffspring", {"start": v(-91.75, -60.5) * mm, "end": v(-91.75, -39.5) * mm});
            skLineSegment(sketch, "E281.trimOffspring", {"start": v(-136.38, -60.5) * mm, "end": v(-136.38, -39.5) * mm});
            skLineSegment(sketch, "E282.trimOffspring", {"start": v(-91.25, -60.5) * mm, "end": v(-91.25, -39.5) * mm});
            skLineSegment(sketch, "E283.trimOffspring", {"start": v(-10.5, -19.5) * mm, "end": v(0, -19.5) * mm});
            skLineSegment(sketch, "E284.trimOffspring", {"start": v(-10.5, -0.5) * mm, "end": v(0, -0.5) * mm});
            skLineSegment(sketch, "E285.trimOffspring", {"start": v(-10.5, -20.5) * mm, "end": v(0, -20.5) * mm});
            skLineSegment(sketch, "E286.trimOffspring", {"start": v(-10.5, -20) * mm, "end": v(0, -20) * mm});
            skLineSegment(sketch, "E287.trimOffspring", {"start": v(-46.12, -60.5) * mm, "end": v(-46.12, -39.5) * mm});
            skLineSegment(sketch, "E288.trimOffspring", {"start": v(-10.5, -163) * mm, "end": v(0, -163) * mm});
            skLineSegment(sketch, "E289.trimOffspring", {"start": v(-10.5, -162) * mm, "end": v(0, -162) * mm});
            skLineSegment(sketch, "E290.trimOffspring", {"start": v(-45.62, -60.5) * mm, "end": v(-45.62, -39.5) * mm});
            skLineSegment(sketch, "E291.trimOffspring", {"start": v(-45.13, -60.5) * mm, "end": v(-45.13, -39.5) * mm});
            skLineSegment(sketch, "E292.trimOffspring", {"start": v(-10.5, -162.5) * mm, "end": v(0, -162.5) * mm});
            skLineSegment(sketch, "E293.trimOffspring", {"start": v(-10.5, -125.5) * mm, "end": v(0, -125.5) * mm});
            skLineSegment(sketch, "E294.trimOffspring", {"start": v(-10.5, -124.5) * mm, "end": v(0, -124.5) * mm});
            skLineSegment(sketch, "E295.trimOffspring", {"start": v(-10.5, -88) * mm, "end": v(0, -88) * mm});
            skLineSegment(sketch, "E296.trimOffspring", {"start": v(-10.5, -87.5) * mm, "end": v(0, -87.5) * mm});
            skLineSegment(sketch, "E297.trimOffspring", {"start": v(-10.5, -125) * mm, "end": v(0, -125) * mm});
            skLineSegment(sketch, "E298.trimOffspring", {"start": v(-10.5, -87) * mm, "end": v(0, -87) * mm});
            skLineSegment(sketch, "E299.MirrorCS", {"start": v(172.5, -200) * mm, "end": v(173, -200) * mm});
            skLineSegment(sketch, "E300.MirrorCS", {"start": v(182.5, -200) * mm, "end": v(183, -200) * mm});
            skLineSegment(sketch, "E301.MirrorCS", {"start": v(365, -40) * mm, "end": v(365, -39.5) * mm});
            skLineSegment(sketch, "E302.MirrorCS", {"start": v(182.5, -200) * mm, "end": v(182, -200) * mm});
            skLineSegment(sketch, "E303.MirrorCS", {"start": v(192.5, -200) * mm, "end": v(192, -200) * mm});
            skLineSegment(sketch, "E304.MirrorCS", {"start": v(172.5, -200) * mm, "end": v(172, -200) * mm});
            skLineSegment(sketch, "E305.MirrorCS", {"start": v(192.5, -200) * mm, "end": v(193, -200) * mm});
            skLineSegment(sketch, "E306.MirrorCS", {"start": v(365, -40) * mm, "end": v(365, -40.5) * mm});
            skLineSegment(sketch, "E307.MirrorCS", {"start": v(365, -50) * mm, "end": v(365, -49.5) * mm});
            skLineSegment(sketch, "E308.MirrorCS", {"start": v(365, -50) * mm, "end": v(365, -50.5) * mm});
            skLineSegment(sketch, "E309.MirrorCS", {"start": v(10, -200) * mm, "end": v(10.5, -200) * mm});
            skLineSegment(sketch, "E310.MirrorCS", {"start": v(365, -60) * mm, "end": v(365, -60.5) * mm});
            skLineSegment(sketch, "E311.MirrorCS", {"start": v(0, 0) * mm, "end": v(0.5, 0) * mm});
            skLineSegment(sketch, "E312.MirrorCS", {"start": v(10, -200) * mm, "end": v(9.5, -200) * mm});
            skLineSegment(sketch, "E313.MirrorCS", {"start": v(365, -60) * mm, "end": v(365, -59.5) * mm});
            skLineSegment(sketch, "E314.MirrorCS", {"start": v(10.5, -0.5) * mm, "end": v(0, -0.5) * mm});
            skLineSegment(sketch, "E315.MirrorCS", {"start": v(10, 0) * mm, "end": v(9.5, 0) * mm});
            skLineSegment(sketch, "E316.MirrorCS", {"start": v(10, 0) * mm, "end": v(10.5, 0) * mm});
            skLineSegment(sketch, "E317.MirrorCS", {"start": v(365, -125) * mm, "end": v(365, -125.5) * mm});
            skLineSegment(sketch, "E318.MirrorCS", {"start": v(0, -200) * mm, "end": v(0.5, -200) * mm});
            skLineSegment(sketch, "E319.MirrorCS", {"start": v(365, -87.5) * mm, "end": v(365, -87) * mm});
            skLineSegment(sketch, "E320.MirrorCS", {"start": v(365, -162.5) * mm, "end": v(365, -162) * mm});
            skLineSegment(sketch, "E321.MirrorCS", {"start": v(365, -87.5) * mm, "end": v(365, -88) * mm});
            skLineSegment(sketch, "E322.MirrorCS", {"start": v(365, -125) * mm, "end": v(365, -124.5) * mm});
            skLineSegment(sketch, "E323.MirrorCS", {"start": v(365, -162.5) * mm, "end": v(365, -163) * mm});
            skLineSegment(sketch, "E324.MirrorCS", {"start": v(10.5, -19.5) * mm, "end": v(0, -19.5) * mm});
            skLineSegment(sketch, "E325.MirrorCS", {"start": v(365, -40) * mm, "end": v(0, -40) * mm});
            skLineSegment(sketch, "E326.MirrorCS", {"start": v(318.87, -60.5) * mm, "end": v(318.87, -39.5) * mm});
            skLineSegment(sketch, "E327.MirrorCS", {"start": v(172, -200) * mm, "end": v(172, -39.5) * mm});
            skLineSegment(sketch, "E328.MirrorCS", {"start": v(192, -200) * mm, "end": v(192, -39.5) * mm});
            skLineSegment(sketch, "E329.MirrorCS", {"start": v(193, -88) * mm, "end": v(172, -88) * mm});
            skLineSegment(sketch, "E330.MirrorCS", {"start": v(45.62, -60.5) * mm, "end": v(45.62, -39.5) * mm});
            skLineSegment(sketch, "E331.MirrorCS", {"start": v(193, -125) * mm, "end": v(172, -125) * mm});
            skLineSegment(sketch, "E332.MirrorCS", {"start": v(193, -163) * mm, "end": v(172, -163) * mm});
            skLineSegment(sketch, "E333.MirrorCS", {"start": v(182.5, -200) * mm, "end": v(182.5, -40.5) * mm});
            skLineSegment(sketch, "E334.MirrorCS", {"start": v(10, -200) * mm, "end": v(10, 0) * mm});
            skLineSegment(sketch, "E335.MirrorCS", {"start": v(365, -40.5) * mm, "end": v(0, -40.5) * mm});
            skLineSegment(sketch, "E336.MirrorCS", {"start": v(273.25, -60.5) * mm, "end": v(273.25, -39.5) * mm});
            skLineSegment(sketch, "E337.MirrorCS", {"start": v(192.5, -200) * mm, "end": v(192.5, -40) * mm});
            skLineSegment(sketch, "E338.MirrorCS", {"start": v(172.5, -200) * mm, "end": v(172.5, -40.5) * mm});
            skLineSegment(sketch, "E339.MirrorCS", {"start": v(10.5, -125.5) * mm, "end": v(0, -125.5) * mm});
            skLineSegment(sketch, "E340.MirrorCS", {"start": v(193, -162.5) * mm, "end": v(172, -162.5) * mm});
            skLineSegment(sketch, "E341.MirrorCS", {"start": v(10.5, -163) * mm, "end": v(0, -163) * mm});
            skLineSegment(sketch, "E342.MirrorCS", {"start": v(183, -200) * mm, "end": v(183, -39.5) * mm});
            skLineSegment(sketch, "E343.MirrorCS", {"start": v(136.87, -60.5) * mm, "end": v(136.87, -39.5) * mm});
            skLineSegment(sketch, "E344.MirrorCS", {"start": v(365, -60) * mm, "end": v(0, -60) * mm});
            skLineSegment(sketch, "E345.MirrorCS", {"start": v(193, -87.5) * mm, "end": v(172, -87.5) * mm});
            skLineSegment(sketch, "E346.MirrorCS", {"start": v(45.12, -60.5) * mm, "end": v(45.12, -39.5) * mm});
            skLineSegment(sketch, "E347.MirrorCS", {"start": v(10.5, -88) * mm, "end": v(0, -88) * mm});
            skLineSegment(sketch, "E348.MirrorCS", {"start": v(365, -50) * mm, "end": v(0, -50) * mm});
            skLineSegment(sketch, "E349.MirrorCS", {"start": v(10.5, -20.5) * mm, "end": v(0, -20.5) * mm});
            skLineSegment(sketch, "E350.MirrorCS", {"start": v(228.12, -60.5) * mm, "end": v(228.12, -39.5) * mm});
            skLineSegment(sketch, "E351.MirrorCS", {"start": v(319.87, -60.5) * mm, "end": v(319.87, -39.5) * mm});
            skLineSegment(sketch, "E352.MirrorCS", {"start": v(91.25, -60.5) * mm, "end": v(91.25, -40) * mm});
            skLineSegment(sketch, "E353.MirrorCS", {"start": v(91.75, -60.5) * mm, "end": v(91.75, -39.5) * mm});
            skLineSegment(sketch, "E354.MirrorCS", {"start": v(193, -87) * mm, "end": v(172, -87) * mm});
            skLineSegment(sketch, "E355.MirrorCS", {"start": v(193, -124.5) * mm, "end": v(172, -124.5) * mm});
            skLineSegment(sketch, "E356.MirrorCS", {"start": v(10.5, -162.5) * mm, "end": v(0, -162.5) * mm});
            skLineSegment(sketch, "E357.MirrorCS", {"start": v(319.37, -60.5) * mm, "end": v(319.37, -39.5) * mm});
            skLineSegment(sketch, "E358.MirrorCS", {"start": v(193, -200) * mm, "end": v(193, -39.5) * mm});
            skLineSegment(sketch, "E359.MirrorCS", {"start": v(182.5, -200) * mm, "end": v(182.5, -39.5) * mm});
            skLineSegment(sketch, "E360.MirrorCS", {"start": v(273.75, -60.5) * mm, "end": v(273.75, -39.5) * mm});
            skLineSegment(sketch, "E361.MirrorCS", {"start": v(10.5, -125) * mm, "end": v(0, -125) * mm});
            skLineSegment(sketch, "E362.MirrorCS", {"start": v(10.5, -20) * mm, "end": v(0, -20) * mm});
            skLineSegment(sketch, "E363.MirrorCS", {"start": v(193, -125.5) * mm, "end": v(172, -125.5) * mm});
            skLineSegment(sketch, "E364.MirrorCS", {"start": v(173, -200) * mm, "end": v(173, -39.5) * mm});
            skLineSegment(sketch, "E365.MirrorCS", {"start": v(9.5, -200) * mm, "end": v(9.5, 0) * mm});
            skLineSegment(sketch, "E366.MirrorCS", {"start": v(10.5, -87.5) * mm, "end": v(0, -87.5) * mm});
            skLineSegment(sketch, "E367.MirrorCS", {"start": v(193, -162) * mm, "end": v(172, -162) * mm});
            skLineSegment(sketch, "E368.MirrorCS", {"start": v(365, -39.5) * mm, "end": v(0, -39.5) * mm});
            skLineSegment(sketch, "E369.MirrorCS", {"start": v(365, -49.5) * mm, "end": v(0, -49.5) * mm});
            skLineSegment(sketch, "E370.MirrorCS", {"start": v(90.75, -60.5) * mm, "end": v(90.75, -39.5) * mm});
            skPoint(sketch, "E371.MirrorP", {"position": v(365, 0) * mm});
            skLineSegment(sketch, "E372.MirrorCS", {"start": v(10.5, -124.5) * mm, "end": v(0, -124.5) * mm});
            skLineSegment(sketch, "E373.MirrorCS", {"start": v(365, -59.5) * mm, "end": v(0, -59.5) * mm});
            skLineSegment(sketch, "E374.MirrorCS", {"start": v(10.5, -162) * mm, "end": v(0, -162) * mm});
            skPoint(sketch, "E375.MirrorP", {"position": v(365, -60) * mm});
            skPoint(sketch, "E376.MirrorP", {"position": v(172.5, -200) * mm});
            skPoint(sketch, "E377.MirrorP", {"position": v(365, -50) * mm});
            skLineSegment(sketch, "E378.MirrorCS", {"start": v(365, -50.5) * mm, "end": v(0, -50.5) * mm});
            skPoint(sketch, "E379.MirrorP", {"position": v(365, -40) * mm});
            skLineSegment(sketch, "E380.MirrorCS", {"start": v(137.37, -60.5) * mm, "end": v(137.37, -39.5) * mm});
            skPoint(sketch, "E381.MirrorP", {"position": v(192.5, -200) * mm});
            skPoint(sketch, "E382.MirrorP", {"position": v(365, -87.5) * mm});
            skLineSegment(sketch, "E383.MirrorCS", {"start": v(228.62, -60.5) * mm, "end": v(228.62, -39.5) * mm});
            skLineSegment(sketch, "E384.MirrorCS", {"start": v(365, -60.5) * mm, "end": v(0, -60.5) * mm});
            skLineSegment(sketch, "E385.MirrorCS", {"start": v(46.12, -60.5) * mm, "end": v(46.12, -39.5) * mm});
            skLineSegment(sketch, "E386.MirrorCS", {"start": v(10.5, -200) * mm, "end": v(10.5, 0) * mm});
            skLineSegment(sketch, "E387.MirrorCS", {"start": v(0.5, -200) * mm, "end": v(0.5, 0) * mm});
            skLineSegment(sketch, "E388.MirrorCS", {"start": v(182, -200) * mm, "end": v(182, -39.5) * mm});
            skLineSegment(sketch, "E389.MirrorCS", {"start": v(91.25, -60.5) * mm, "end": v(91.25, -39.5) * mm});
            skLineSegment(sketch, "E390.MirrorCS", {"start": v(136.38, -60.5) * mm, "end": v(136.38, -39.5) * mm});
            skLineSegment(sketch, "E391.MirrorCS", {"start": v(192.5, -200) * mm, "end": v(192.5, -39.5) * mm});
            skLineSegment(sketch, "E392.MirrorCS", {"start": v(172.5, -200) * mm, "end": v(172.5, -39.5) * mm});
            skLineSegment(sketch, "E393.MirrorCS", {"start": v(227.62, -60.5) * mm, "end": v(227.62, -39.5) * mm});
            skLineSegment(sketch, "E394.MirrorCS", {"start": v(274.25, -60.5) * mm, "end": v(274.25, -39.5) * mm});
            skPoint(sketch, "E395.MirrorP", {"position": v(365, -162.5) * mm});
            skPoint(sketch, "E396.MirrorP", {"position": v(365, -125) * mm});
            skPoint(sketch, "E397.MirrorP", {"position": v(10, -200) * mm});
            skLineSegment(sketch, "E398.MirrorCS", {"start": v(10.5, -87) * mm, "end": v(0, -87) * mm});
            skLineSegment(sketch, "E399.MirrorCS", {"start": v(0, 50) * mm, "end": v(0, 50.5) * mm});
            skLineSegment(sketch, "E400.MirrorCS", {"start": v(0, 50) * mm, "end": v(0, 49.5) * mm});
            skLineSegment(sketch, "E401.MirrorCS", {"start": v(0, 40) * mm, "end": v(0, 40.5) * mm});
            skLineSegment(sketch, "E402.MirrorCS", {"start": v(0, 60) * mm, "end": v(0, 59.5) * mm});
            skLineSegment(sketch, "E403.MirrorCS", {"start": v(0, 20) * mm, "end": v(0, 20.5) * mm});
            skLineSegment(sketch, "E404.MirrorCS", {"start": v(0, 20) * mm, "end": v(0, 19.5) * mm});
            skLineSegment(sketch, "E405.MirrorCS", {"start": v(0, 40) * mm, "end": v(0, 39.5) * mm});
            skLineSegment(sketch, "E406.MirrorCS", {"start": v(0, 60) * mm, "end": v(0, 60.5) * mm});
            skLineSegment(sketch, "E407.MirrorCS", {"start": v(-365, 40) * mm, "end": v(-365, 40.5) * mm});
            skLineSegment(sketch, "E408.MirrorCS", {"start": v(-365, 50) * mm, "end": v(-365, 49.5) * mm});
            skLineSegment(sketch, "E409.MirrorCS", {"start": v(10.5, 0.5) * mm, "end": v(0, 0.5) * mm});
            skLineSegment(sketch, "E410.MirrorCS", {"start": v(-365, 60) * mm, "end": v(-365, 59.5) * mm});
            skLineSegment(sketch, "E411.MirrorCS", {"start": v(-365, 50) * mm, "end": v(-365, 50.5) * mm});
            skLineSegment(sketch, "E412.MirrorCS", {"start": v(-365, 60) * mm, "end": v(-365, 60.5) * mm});
            skLineSegment(sketch, "E413.MirrorCS", {"start": v(-365, 40) * mm, "end": v(-365, 39.5) * mm});
            skLineSegment(sketch, "E414.MirrorCS", {"start": v(-193, 0.5) * mm, "end": v(-172, 0.5) * mm});
            skLineSegment(sketch, "E415.MirrorCS", {"start": v(-10.5, 0.5) * mm, "end": v(0, 0.5) * mm});
            skLineSegment(sketch, "E416.MirrorCS", {"start": v(-10.5, 20.5) * mm, "end": v(0, 20.5) * mm});
            skLineSegment(sketch, "E417.MirrorCS", {"start": v(10.5, 20) * mm, "end": v(0, 20) * mm});
            skLineSegment(sketch, "E418.MirrorCS", {"start": v(-10.5, 20) * mm, "end": v(0, 20) * mm});
            skLineSegment(sketch, "E419.MirrorCS", {"start": v(10.5, 20.5) * mm, "end": v(0, 20.5) * mm});
            skLineSegment(sketch, "E420.MirrorCS", {"start": v(10.5, 19.5) * mm, "end": v(0, 19.5) * mm});
            skLineSegment(sketch, "E421.MirrorCS", {"start": v(-10.5, 19.5) * mm, "end": v(0, 19.5) * mm});
            skLineSegment(sketch, "E422.MirrorCS", {"start": v(-91.25, 60.5) * mm, "end": v(-91.25, 40) * mm});
            skLineSegment(sketch, "E423.MirrorCS", {"start": v(-137.37, 60.5) * mm, "end": v(-137.37, 39.5) * mm});
            skLineSegment(sketch, "E424.MirrorCS", {"start": v(-274.25, 60.5) * mm, "end": v(-274.25, 39.5) * mm});
            skLineSegment(sketch, "E425.MirrorCS", {"start": v(-318.87, 60.5) * mm, "end": v(-318.88, 39.5) * mm});
            skLineSegment(sketch, "E426.MirrorCS", {"start": v(-319.88, 40) * mm, "end": v(-228.62, 40) * mm});
            skLineSegment(sketch, "E427.MirrorCS", {"start": v(-136.87, 60.5) * mm, "end": v(-136.87, 39.5) * mm});
            skLineSegment(sketch, "E428.MirrorCS", {"start": v(-319.87, 60.5) * mm, "end": v(-319.88, 39.5) * mm});
            skLineSegment(sketch, "E429.MirrorCS", {"start": v(-273.25, 60.5) * mm, "end": v(-273.25, 39.5) * mm});
            skLineSegment(sketch, "E430.MirrorCS", {"start": v(-319.87, 50) * mm, "end": v(-318.87, 50) * mm});
            skLineSegment(sketch, "E431.MirrorCS", {"start": v(-90.75, 60.5) * mm, "end": v(-90.75, 39.5) * mm});
            skLineSegment(sketch, "E432.MirrorCS", {"start": v(-365, 60) * mm, "end": v(-318.87, 60) * mm});
            skLineSegment(sketch, "E433.MirrorCS", {"start": v(-193, 20.5) * mm, "end": v(-172, 20.5) * mm});
            skLineSegment(sketch, "E434.MirrorCS", {"start": v(-228.12, 60.5) * mm, "end": v(-228.12, 39.5) * mm});
            skLineSegment(sketch, "E435.MirrorCS", {"start": v(-45.62, 60.5) * mm, "end": v(-45.62, 39.5) * mm});
            skLineSegment(sketch, "E436.MirrorCS", {"start": v(-319.37, 40.5) * mm, "end": v(-228.62, 40.5) * mm});
            skLineSegment(sketch, "E437.MirrorCS", {"start": v(-319.37, 60.5) * mm, "end": v(-319.37, 39.5) * mm});
            skLineSegment(sketch, "E438.MirrorCS", {"start": v(-365, 59.5) * mm, "end": v(-318.87, 59.5) * mm});
            skLineSegment(sketch, "E439.MirrorCS", {"start": v(-273.75, 60.5) * mm, "end": v(-273.75, 39.5) * mm});
            skLineSegment(sketch, "E440.MirrorCS", {"start": v(-91.75, 60.5) * mm, "end": v(-91.75, 39.5) * mm});
            skLineSegment(sketch, "E441.MirrorCS", {"start": v(-193, 20) * mm, "end": v(-172, 20) * mm});
            skLineSegment(sketch, "E442.MirrorCS", {"start": v(-319.87, 49.5) * mm, "end": v(-318.87, 49.5) * mm});
            skLineSegment(sketch, "E443.MirrorCS", {"start": v(-227.62, 60.5) * mm, "end": v(-227.62, 39.5) * mm});
            skLineSegment(sketch, "E444.MirrorCS", {"start": v(-45.13, 60.5) * mm, "end": v(-45.13, 39.5) * mm});
            skLineSegment(sketch, "E445.MirrorCS", {"start": v(-228.62, 60.5) * mm, "end": v(-228.62, 39.5) * mm});
            skLineSegment(sketch, "E446.MirrorCS", {"start": v(-46.12, 60.5) * mm, "end": v(-46.12, 39.5) * mm});
            skLineSegment(sketch, "E447.MirrorCS", {"start": v(-365, 60.5) * mm, "end": v(-318.87, 60.5) * mm});
            skLineSegment(sketch, "E448.MirrorCS", {"start": v(-91.25, 60.5) * mm, "end": v(-91.25, 39.5) * mm});
            skLineSegment(sketch, "E449.MirrorCS", {"start": v(-319.88, 39.5) * mm, "end": v(-273.25, 39.5) * mm});
            skLineSegment(sketch, "E450.MirrorCS", {"start": v(-319.37, 40) * mm, "end": v(-273.25, 40) * mm});
            skLineSegment(sketch, "E451.MirrorCS", {"start": v(-136.38, 60.5) * mm, "end": v(-136.38, 39.5) * mm});
            skLineSegment(sketch, "E452.MirrorCS", {"start": v(-319.87, 50.5) * mm, "end": v(-318.87, 50.5) * mm});
            skLineSegment(sketch, "E453.MirrorCS", {"start": v(-365, 60) * mm, "end": v(-274.25, 60) * mm});
            skLineSegment(sketch, "E454.MirrorCS", {"start": v(-193, 19.5) * mm, "end": v(-172, 19.5) * mm});
            skLineSegment(sketch, "E455.MirrorCS", {"start": v(0, 60.5) * mm, "end": v(0, 0) * mm});
            skLineSegment(sketch, "E456.MirrorCS", {"start": v(-193, 20.5) * mm, "end": v(-172.5, 20.5) * mm});
            skLineSegment(sketch, "E457.MirrorCS", {"start": v(-319.88, 40) * mm, "end": v(-273.25, 40) * mm});
            skLineSegment(sketch, "E458.MirrorCS", {"start": v(10.5, 40) * mm, "end": v(0, 40) * mm});
            skLineSegment(sketch, "E459.MirrorCS", {"start": v(10.5, 60) * mm, "end": v(0, 60) * mm});
            skLineSegment(sketch, "E460.MirrorCS", {"start": v(-319.88, 40.5) * mm, "end": v(-273.25, 40.5) * mm});
            skLineSegment(sketch, "E461.MirrorCS", {"start": v(10.5, 50) * mm, "end": v(0, 50) * mm});
            skLineSegment(sketch, "E462.MirrorCS", {"start": v(-365, 59.5) * mm, "end": v(-274.25, 59.5) * mm});
            skLineSegment(sketch, "E463.MirrorCS", {"start": v(-365, 60.5) * mm, "end": v(-274.25, 60.5) * mm});
            skLineSegment(sketch, "E464.MirrorCS", {"start": v(-319.88, 39.5) * mm, "end": v(-228.62, 39.5) * mm});
            skLineSegment(sketch, "E465.MirrorCS", {"start": v(10.5, 49.5) * mm, "end": v(0, 49.5) * mm});
            skLineSegment(sketch, "E466.MirrorCS", {"start": v(10.5, 50.5) * mm, "end": v(0, 50.5) * mm});
            skLineSegment(sketch, "E467.MirrorCS", {"start": v(10.5, 59.5) * mm, "end": v(0, 59.5) * mm});
            skLineSegment(sketch, "E468.MirrorCS", {"start": v(10.5, 39.5) * mm, "end": v(0, 39.5) * mm});
            skLineSegment(sketch, "E469.MirrorCS", {"start": v(10.5, 60.5) * mm, "end": v(0, 60.5) * mm});
            skLineSegment(sketch, "E470.MirrorCS", {"start": v(-365, 60) * mm, "end": v(-319.37, 60) * mm});
            skLineSegment(sketch, "E471.MirrorCS", {"start": v(-319.87, 50) * mm, "end": v(-319.37, 50) * mm});
            skLineSegment(sketch, "E472.MirrorCS", {"start": v(10.5, 40.5) * mm, "end": v(0, 40.5) * mm});
            skLineSegment(sketch, "E473.trimOffspring", {"start": v(-10.5, 60.5) * mm, "end": v(-10.5, 0) * mm});
            skLineSegment(sketch, "E474.trimOffspring", {"start": v(-10, 60.5) * mm, "end": v(-10, 0) * mm});
            skLineSegment(sketch, "E475.trimOffspring", {"start": v(-0.5, 60.5) * mm, "end": v(-0.5, 0) * mm});
            skLineSegment(sketch, "E476.trimOffspring", {"start": v(-9.5, 60.5) * mm, "end": v(-9.5, 0) * mm});
            skLineSegment(sketch, "E477.trimOffspring", {"start": v(0.5, 60.5) * mm, "end": v(0.5, 0) * mm});
            skLineSegment(sketch, "E478.trimOffspring", {"start": v(10.5, 60.5) * mm, "end": v(10.5, 49.5) * mm});
            skLineSegment(sketch, "E479.trimOffspring", {"start": v(10, 60.5) * mm, "end": v(10, 49.5) * mm});
            skLineSegment(sketch, "E480.trimOffspring", {"start": v(9.5, 60.5) * mm, "end": v(9.5, 49.5) * mm});
            skLineSegment(sketch, "E481.trimOffspring", {"start": v(-173, 60.5) * mm, "end": v(-173, 49.5) * mm});
            skLineSegment(sketch, "E482.trimOffspring", {"start": v(-172.5, 60.5) * mm, "end": v(-172.5, 50) * mm});
            skLineSegment(sketch, "E483.trimOffspring", {"start": v(-172, 60.5) * mm, "end": v(-172, 49.5) * mm});
            skLineSegment(sketch, "E484.trimOffspring", {"start": v(-172.5, 60.5) * mm, "end": v(-172.5, 49.5) * mm});
            skPoint(sketch, "E485.orphan", {"position": v(365, 60.5) * mm});
            skPoint(sketch, "E486.orphan", {"position": v(365, 59.5) * mm});
            skPoint(sketch, "E487.orphan", {"position": v(365, 60) * mm});
            skPoint(sketch, "E488.orphan", {"position": v(365, 40) * mm});
            skPoint(sketch, "E489.orphan", {"position": v(365, 39.5) * mm});
            skPoint(sketch, "E490.orphan", {"position": v(365, 49.5) * mm});
            skPoint(sketch, "E491.orphan", {"position": v(365, 50) * mm});
            skPoint(sketch, "E492.orphan", {"position": v(365, 50.5) * mm});
            skPoint(sketch, "E493.orphan", {"position": v(365, 40.5) * mm});
            skPoint(sketch, "E494.orphan", {"position": v(0, 200) * mm});
            skLineSegment(sketch, "E495.trimOffspring", {"start": v(-10.5, 0) * mm, "end": v(0, 0) * mm});
            skLineSegment(sketch, "E496.trimOffspring", {"start": v(-318.88, -39.5) * mm, "end": v(-227.62, -39.5) * mm});
            skLineSegment(sketch, "E497.trimOffspring", {"start": v(-318.88, -40.5) * mm, "end": v(-227.62, -40.5) * mm});
            skLineSegment(sketch, "E498.trimOffspring", {"start": v(-274.25, -40) * mm, "end": v(-227.62, -40) * mm});
            skLineSegment(sketch, "E499.trimOffspring", {"start": v(-274.25, -49.5) * mm, "end": v(-273.25, -49.5) * mm});
            skLineSegment(sketch, "E500.trimOffspring", {"start": v(-274.25, -50) * mm, "end": v(-273.25, -50) * mm});
            skLineSegment(sketch, "E501.trimOffspring", {"start": v(-228.62, -60.5) * mm, "end": v(-192, -60.5) * mm});
            skLineSegment(sketch, "E502.trimOffspring", {"start": v(-228.62, -60) * mm, "end": v(-192, -60) * mm});
            skLineSegment(sketch, "E503.trimOffspring", {"start": v(-228.62, -59.5) * mm, "end": v(-192, -59.5) * mm});
            skLineSegment(sketch, "E504.trimOffspring", {"start": v(-228.62, -60) * mm, "end": v(-192.5, -60) * mm});
            skLineSegment(sketch, "E505.trimOffspring", {"start": v(-228.62, -50.5) * mm, "end": v(-227.62, -50.5) * mm});
            skLineSegment(sketch, "E506.trimOffspring", {"start": v(-228.62, -50) * mm, "end": v(-227.62, -50) * mm});
            skLineSegment(sketch, "E507.trimOffspring", {"start": v(-193, -50.5) * mm, "end": v(0, -50.5) * mm});
            skLineSegment(sketch, "E508.trimOffspring", {"start": v(-193, -39.5) * mm, "end": v(-182, -39.5) * mm});
            skLineSegment(sketch, "E509.trimOffspring", {"start": v(-193, -40) * mm, "end": v(-182, -40) * mm});
            skLineSegment(sketch, "E510.trimOffspring", {"start": v(-193, -49.5) * mm, "end": v(0, -49.5) * mm});
            skLineSegment(sketch, "E511.trimOffspring", {"start": v(-228.62, -49.5) * mm, "end": v(-227.62, -49.5) * mm});
            skLineSegment(sketch, "E512.trimOffspring", {"start": v(-193, -50) * mm, "end": v(0, -50) * mm});
            skLineSegment(sketch, "E513.trimOffspring", {"start": v(-193, -40.5) * mm, "end": v(-182, -40.5) * mm});
            skLineSegment(sketch, "E514.trimOffspring", {"start": v(-193, -40.5) * mm, "end": v(-193, 0) * mm});
            skLineSegment(sketch, "E515.trimOffspring", {"start": v(-192.5, -40.5) * mm, "end": v(-192.5, 0) * mm});
            skLineSegment(sketch, "E516.trimOffspring", {"start": v(-192, -40.5) * mm, "end": v(-192, 0) * mm});
            skLineSegment(sketch, "E517.trimOffspring", {"start": v(-183, -60.5) * mm, "end": v(0, -60.5) * mm});
            skLineSegment(sketch, "E518.trimOffspring", {"start": v(-183, -59.5) * mm, "end": v(0, -59.5) * mm});
            skLineSegment(sketch, "E519.trimOffspring", {"start": v(-183, -60) * mm, "end": v(0, -60) * mm});
            skLineSegment(sketch, "E520.trimOffspring", {"start": v(-172.5, -50.5) * mm, "end": v(-172.5, -39.5) * mm});
            skLineSegment(sketch, "E521.trimOffspring", {"start": v(-172.5, -40) * mm, "end": v(0, -40) * mm});
            skLineSegment(sketch, "E522.trimOffspring", {"start": v(-173, -40.5) * mm, "end": v(0, -40.5) * mm});
            skLineSegment(sketch, "E523.trimOffspring", {"start": v(-172, -50.5) * mm, "end": v(-172, -39.5) * mm});
            skLineSegment(sketch, "E524.trimOffspring", {"start": v(-173, -40) * mm, "end": v(0, -40) * mm});
            skLineSegment(sketch, "E525.trimOffspring", {"start": v(-172.5, -39.5) * mm, "end": v(0, -39.5) * mm});
            skLineSegment(sketch, "E526.trimOffspring", {"start": v(-192.5, -60.5) * mm, "end": v(-192.5, -50) * mm});
            skLineSegment(sketch, "E527.trimOffspring", {"start": v(-182.5, -60.5) * mm, "end": v(-182.5, 0) * mm});
            skLineSegment(sketch, "E528.trimOffspring", {"start": v(-172.5, -20.5) * mm, "end": v(-172.5, 0) * mm});
            skLineSegment(sketch, "E529.trimOffspring", {"start": v(-193, -60.5) * mm, "end": v(-193, -49.5) * mm});
            skLineSegment(sketch, "E530.trimOffspring", {"start": v(-192.5, -60.5) * mm, "end": v(-192.5, -49.5) * mm});
            skLineSegment(sketch, "E531.trimOffspring", {"start": v(-192, -60.5) * mm, "end": v(-192, -49.5) * mm});
            skLineSegment(sketch, "E532.trimOffspring", {"start": v(-183, -60.5) * mm, "end": v(-183, 0) * mm});
            skLineSegment(sketch, "E533.trimOffspring", {"start": v(-182, -60.5) * mm, "end": v(-182, 0) * mm});
            skLineSegment(sketch, "E534.MirrorCS", {"start": v(-173, -200) * mm, "end": v(-173, -59.5) * mm});
            skLineSegment(sketch, "E535.trimOffspring", {"start": v(-173, -50.5) * mm, "end": v(-173, -39.5) * mm});
            skLineSegment(sketch, "E536.trimOffspring", {"start": v(-172, -20) * mm, "end": v(-172, 0) * mm});
            skLineSegment(sketch, "E537.MirrorCS", {"start": v(-172, -39.5) * mm, "end": v(-173, -39.5) * mm});
            skLineSegment(sketch, "E538.trimOffspring", {"start": v(-173, -20.5) * mm, "end": v(-173, 0) * mm});
            skLineSegment(sketch, "E539.MirrorCS", {"start": v(-172, -40.5) * mm, "end": v(-172, -39.5) * mm});
            skLineSegment(sketch, "E540.MirrorCS", {"start": v(-172, -20.5) * mm, "end": v(-192.5, -20.5) * mm});
            skLineSegment(sketch, "E541.trimOffspring", {"start": v(-182, -39.5) * mm, "end": v(-183, -39.5) * mm});
            skLineSegment(sketch, "E542.trimOffspring", {"start": v(-172, -20.5) * mm, "end": v(-172, 0) * mm});
            skPoint(sketch, "E543.orphan", {"position": v(-365, 39.5) * mm});
            skLineSegment(sketch, "E544.trimOffspring", {"start": v(-274.25, 60) * mm, "end": v(-228.12, 60) * mm});
            skLineSegment(sketch, "E545.trimOffspring", {"start": v(-274.25, 50) * mm, "end": v(-273.25, 50) * mm});
            skPoint(sketch, "E546.orphan", {"position": v(-365, 40.5) * mm});
            skLineSegment(sketch, "E547.trimOffspring", {"start": v(-228.62, 50) * mm, "end": v(-227.62, 50) * mm});
            skLineSegment(sketch, "E548.trimOffspring", {"start": v(-228.62, 40) * mm, "end": v(-193, 40) * mm});
            skLineSegment(sketch, "E549.trimOffspring", {"start": v(-228.62, 50) * mm, "end": v(-228.12, 50) * mm});
            skPoint(sketch, "E550.orphan", {"position": v(-365, 49.5) * mm});
            skPoint(sketch, "E551.orphan", {"position": v(-365, 50.5) * mm});
            skLineSegment(sketch, "E552.trimOffspring", {"start": v(-274.25, 59.5) * mm, "end": v(-227.62, 59.5) * mm});
            skLineSegment(sketch, "E553.trimOffspring", {"start": v(-274.25, 49.5) * mm, "end": v(-273.25, 49.5) * mm});
            skLineSegment(sketch, "E554.trimOffspring", {"start": v(-274.25, 50.5) * mm, "end": v(-273.25, 50.5) * mm});
            skLineSegment(sketch, "E555.trimOffspring", {"start": v(-274.25, 60) * mm, "end": v(-227.62, 60) * mm});
            skLineSegment(sketch, "E556.trimOffspring", {"start": v(-274.25, 60.5) * mm, "end": v(-228.12, 60.5) * mm});
            skLineSegment(sketch, "E557.trimOffspring", {"start": v(-228.62, 49.5) * mm, "end": v(-227.62, 49.5) * mm});
            skLineSegment(sketch, "E558.trimOffspring", {"start": v(-228.62, 40) * mm, "end": v(-192, 40) * mm});
            skLineSegment(sketch, "E559.trimOffspring", {"start": v(-228.62, 39.5) * mm, "end": v(-192, 39.5) * mm});
            skLineSegment(sketch, "E560.trimOffspring", {"start": v(-228.62, 40.5) * mm, "end": v(-192, 40.5) * mm});
            skLineSegment(sketch, "E561.trimOffspring", {"start": v(-228.62, 50.5) * mm, "end": v(-228.12, 50.5) * mm});
            skLineSegment(sketch, "E562.trimOffspring", {"start": v(-274.25, 60.5) * mm, "end": v(-227.62, 60.5) * mm});
            skLineSegment(sketch, "E563.trimOffspring", {"start": v(-228.62, 49.5) * mm, "end": v(-228.12, 49.5) * mm});
            skLineSegment(sketch, "E564.trimOffspring", {"start": v(-228.62, 50.5) * mm, "end": v(-227.62, 50.5) * mm});
            skLineSegment(sketch, "E565.trimOffspring", {"start": v(-193, 49.5) * mm, "end": v(0, 49.5) * mm});
            skLineSegment(sketch, "E566.trimOffspring", {"start": v(-193, 50.5) * mm, "end": v(0, 50.5) * mm});
            skLineSegment(sketch, "E567.trimOffspring", {"start": v(-193, 50) * mm, "end": v(0, 50) * mm});
            skLineSegment(sketch, "E568.trimOffspring", {"start": v(-193, 49.5) * mm, "end": v(-173, 49.5) * mm});
            skLineSegment(sketch, "E569.trimOffspring", {"start": v(-193, 50) * mm, "end": v(-172, 50) * mm});
            skLineSegment(sketch, "E570.trimOffspring", {"start": v(-193, 50.5) * mm, "end": v(-172, 50.5) * mm});
            skLineSegment(sketch, "E571.trimOffspring", {"start": v(-193, 50.5) * mm, "end": v(-193, 39.5) * mm});
            skLineSegment(sketch, "E572.trimOffspring", {"start": v(-192.5, 50.5) * mm, "end": v(-192.5, 39.5) * mm});
            skLineSegment(sketch, "E573.trimOffspring", {"start": v(-183, 39.5) * mm, "end": v(-172.5, 39.5) * mm});
            skLineSegment(sketch, "E574.trimOffspring", {"start": v(-192, 20.5) * mm, "end": v(-192, 0) * mm});
            skLineSegment(sketch, "E575.trimOffspring", {"start": v(-183, 40) * mm, "end": v(-172, 40) * mm});
            skLineSegment(sketch, "E576.trimOffspring", {"start": v(-183, 39.5) * mm, "end": v(-172, 39.5) * mm});
            skLineSegment(sketch, "E577.trimOffspring", {"start": v(-193, 20.5) * mm, "end": v(-193, 0) * mm});
            skLineSegment(sketch, "E578.trimOffspring", {"start": v(-192.5, 20.5) * mm, "end": v(-192.5, 0) * mm});
            skLineSegment(sketch, "E579.trimOffspring", {"start": v(-182.5, 20.5) * mm, "end": v(-182.5, 0) * mm});
            skLineSegment(sketch, "E580.trimOffspring", {"start": v(-183, 20.5) * mm, "end": v(-183, 0) * mm});
            skLineSegment(sketch, "E581.trimOffspring", {"start": v(-182, 20.5) * mm, "end": v(-182, 0) * mm});
            skLineSegment(sketch, "E582.trimOffspring", {"start": v(-183, 40.5) * mm, "end": v(-172, 40.5) * mm});
            skLineSegment(sketch, "E583.trimOffspring", {"start": v(-192, 50.5) * mm, "end": v(-192, 39.5) * mm});
            skLineSegment(sketch, "E584.trimOffspring", {"start": v(-173, 59.5) * mm, "end": v(-9.5, 59.5) * mm});
            skLineSegment(sketch, "E585.trimOffspring", {"start": v(-173, 40.5) * mm, "end": v(-173, 0) * mm});
            skLineSegment(sketch, "E586.trimOffspring", {"start": v(-172.5, 40.5) * mm, "end": v(-172.5, 0) * mm});
            skLineSegment(sketch, "E587.trimOffspring", {"start": v(-173, 60) * mm, "end": v(-10, 60) * mm});
            skLineSegment(sketch, "E588.trimOffspring", {"start": v(-183, 40) * mm, "end": v(0, 40) * mm});
            skLineSegment(sketch, "E589.trimOffspring", {"start": v(-172, 40.5) * mm, "end": v(-172, 0.5) * mm});
            skLineSegment(sketch, "E590.trimOffspring", {"start": v(-137.37, 49.5) * mm, "end": v(0, 49.5) * mm});
            skLineSegment(sketch, "E591.trimOffspring", {"start": v(-137.37, 39.5) * mm, "end": v(0, 39.5) * mm});
            skLineSegment(sketch, "E592.trimOffspring", {"start": v(-183, 40) * mm, "end": v(-172.5, 40) * mm});
            skLineSegment(sketch, "E593.trimOffspring", {"start": v(-137.37, 40.5) * mm, "end": v(0, 40.5) * mm});
            skLineSegment(sketch, "E594.trimOffspring", {"start": v(-137.37, 50.5) * mm, "end": v(-136.38, 50.5) * mm});
            skLineSegment(sketch, "E595.trimOffspring", {"start": v(-137.37, 40) * mm, "end": v(0, 40) * mm});
            skLineSegment(sketch, "E596.trimOffspring", {"start": v(-183, 50.5) * mm, "end": v(-183, 39.5) * mm});
            skLineSegment(sketch, "E597.trimOffspring", {"start": v(-182, 50.5) * mm, "end": v(-182, 39.5) * mm});
            skLineSegment(sketch, "E598.trimOffspring", {"start": v(-182.5, 50.5) * mm, "end": v(-182.5, 39.5) * mm});
            skLineSegment(sketch, "E599.trimOffspring", {"start": v(-173, 59.5) * mm, "end": v(-136.38, 59.5) * mm});
            skLineSegment(sketch, "E600.trimOffspring", {"start": v(-173, 60.5) * mm, "end": v(-9.5, 60.5) * mm});
            skLineSegment(sketch, "E601.trimOffspring", {"start": v(-91.75, 50) * mm, "end": v(0, 50) * mm});
            skLineSegment(sketch, "E602.trimOffspring", {"start": v(-91.75, 50.5) * mm, "end": v(0, 50.5) * mm});
            skLineSegment(sketch, "E603.trimOffspring", {"start": v(-91.75, 59.5) * mm, "end": v(-9.5, 59.5) * mm});
            skLineSegment(sketch, "E604.trimOffspring", {"start": v(-91.75, 60) * mm, "end": v(-9.5, 60) * mm});
            skLineSegment(sketch, "E605.trimOffspring", {"start": v(-91.75, 60.5) * mm, "end": v(-9.5, 60.5) * mm});
            skLineSegment(sketch, "E606.trimOffspring", {"start": v(-173, 60) * mm, "end": v(-136.38, 60) * mm});
            skLineSegment(sketch, "E607.trimOffspring", {"start": v(-173, 60.5) * mm, "end": v(-136.38, 60.5) * mm});
            skLineSegment(sketch, "E608.trimOffspring", {"start": v(-173, 60) * mm, "end": v(-9.5, 60) * mm});
            skPoint(sketch, "E609.orphan", {"position": v(-172.5, -163) * mm});
            skPoint(sketch, "E610.orphan", {"position": v(-172.5, -125.5) * mm});
            skPoint(sketch, "E611.orphan", {"position": v(-172.5, -124.5) * mm});
            skPoint(sketch, "E612.orphan", {"position": v(-172.5, 20.5) * mm});
            skPoint(sketch, "E613.orphan", {"position": v(172.5, -125.5) * mm});
            skPoint(sketch, "E614.orphan", {"position": v(172.5, -124.5) * mm});
            skPoint(sketch, "E615.orphan", {"position": v(172.5, -163) * mm});
            skLineSegment(sketch, "E616.trimOffspring", {"start": v(9.5, 40.5) * mm, "end": v(9.5, 0) * mm});
            skLineSegment(sketch, "E617.trimOffspring", {"start": v(10, 40.5) * mm, "end": v(10, 0) * mm});
            skLineSegment(sketch, "E618.trimOffspring", {"start": v(10.5, 40.5) * mm, "end": v(10.5, 0) * mm});
            skLineSegment(sketch, "E619.trimOffspring", {"start": v(-0.5, 59.5) * mm, "end": v(0, 59.5) * mm});
            skLineSegment(sketch, "E620.trimOffspring", {"start": v(-0.5, 60) * mm, "end": v(0, 60) * mm});
            skLineSegment(sketch, "E621.trimOffspring", {"start": v(-0.5, 60.5) * mm, "end": v(0, 60.5) * mm});
            skLineSegment(sketch, "E622", {"start": v(-172, 0.5) * mm, "end": v(-172, 0) * mm});
            skSolve(sketch);
        }
        {
            var Q0;
            Q0=qCreatedBy(makeId("Right.planeOp"),FACE);
            cPlane(context, id + "F26", {"entities" : qUnion([Q0]), "cplaneType" : CPlaneType.OFFSET, "offset" : 182.5 * mm, "width" : 150 * mm, "height" : 150 * mm});
        }
        {
            var Q0;
            Q0=qCreatedBy(makeId("Front.planeOp"),FACE);
            cPlane(context, id + "F27", {"entities" : qUnion([Q0]), "cplaneType" : CPlaneType.OFFSET, "offset" : 50 * mm, "width" : 150 * mm, "height" : 150 * mm});
        }
        {
            var Q0;
            Q0=qCreatedBy(makeId("Right.planeOp"),FACE);
            cPlane(context, id + "F28", {"entities" : qUnion([Q0]), "cplaneType" : CPlaneType.OFFSET, "offset" : 172.5 * mm, "oppositeDirection" : true, "width" : 150 * mm, "height" : 150 * mm});
        }
        {
            var Q0;
            Q0=qCreatedBy(makeId("Front.planeOp"),FACE);
            cPlane(context, id + "F29", {"entities" : qUnion([Q0]), "cplaneType" : CPlaneType.OFFSET, "offset" : 50 * mm, "oppositeDirection" : true, "width" : 150 * mm, "height" : 150 * mm});
        }
        {
            var Q0;
            Q0=qCreatedBy(makeId("Right.planeOp"),FACE);
            var sketch = newSketch(context, id + "F30", { "sketchPlane" : qUnion([Q0])});
            skLineSegment(sketch, "E623", {"start": v(0, 20) * mm, "end": v(-200, 20) * mm});
            skPoint(sketch, "E624", {"position": v(-20, 20) * mm});
            skPoint(sketch, "E625", {"position": v(-40, 20) * mm});
            skPoint(sketch, "E626", {"position": v(-165, 20) * mm});
            skPoint(sketch, "E627", {"position": v(-60, 20) * mm});
            skPoint(sketch, "E628", {"position": v(-95, 20) * mm});
            skPoint(sketch, "E629", {"position": v(-130, 20) * mm});
            skPoint(sketch, "E630", {"position": v(-100, 20) * mm});
            skPoint(sketch, "E631.MirrorP", {"position": v(20, 20) * mm});
            skPoint(sketch, "E632.MirrorP", {"position": v(40, 20) * mm});
            skLineSegment(sketch, "E633", {"start": v(40, 20) * mm, "end": v(0, 20) * mm});
            skLineSegment(sketch, "E634.bottom", {"start": v(40, 20) * mm, "end": v(-200, 20) * mm});
            skLineSegment(sketch, "E634.top", {"start": v(40, 10) * mm, "end": v(-200, 10) * mm});
            skLineSegment(sketch, "E634.left", {"start": v(40, 20) * mm, "end": v(40, 10) * mm});
            skLineSegment(sketch, "E634.right", {"start": v(-200, 20) * mm, "end": v(-200, 10) * mm});
            skLineSegment(sketch, "E635", {"start": v(20, 20) * mm, "end": v(20, 10) * mm});
            skLineSegment(sketch, "E636", {"start": v(40, 15) * mm, "end": v(-200, 15) * mm});
            skLineSegment(sketch, "E637", {"start": v(-20, 20) * mm, "end": v(-20, 10) * mm});
            skLineSegment(sketch, "E638", {"start": v(0, 20) * mm, "end": v(0, 10) * mm});
            skLineSegment(sketch, "E639", {"start": v(-40, 20) * mm, "end": v(-40, 10) * mm});
            skLineSegment(sketch, "E640", {"start": v(-60, 20) * mm, "end": v(-60, 10) * mm});
            skLineSegment(sketch, "E641", {"start": v(-95, 20) * mm, "end": v(-95, 10) * mm});
            skLineSegment(sketch, "E642", {"start": v(-130, 20) * mm, "end": v(-130, 10) * mm});
            skLineSegment(sketch, "E643", {"start": v(-165, 20) * mm, "end": v(-165, 10) * mm});
            skLineSegment(sketch, "E644.bottom", {"start": v(-200, 10) * mm, "end": v(40, 10) * mm});
            skLineSegment(sketch, "E644.top", {"start": v(-200, 0) * mm, "end": v(40, 0) * mm});
            skLineSegment(sketch, "E644.left", {"start": v(-200, 10) * mm, "end": v(-200, 0) * mm});
            skLineSegment(sketch, "E644.right", {"start": v(40, 10) * mm, "end": v(40, 0) * mm});
            skLineSegment(sketch, "E645.bottom", {"start": v(200, 10.5) * mm, "end": v(-200, 10.5) * mm});
            skLineSegment(sketch, "E645.top", {"start": v(200, 9.5) * mm, "end": v(-200, 9.5) * mm});
            skLineSegment(sketch, "E645.left", {"start": v(200, 10.5) * mm, "end": v(200, 9.5) * mm});
            skLineSegment(sketch, "E645.right", {"start": v(-200, 10.5) * mm, "end": v(-200, 9.5) * mm});
            skPoint(sketch, "E645.middle", {"position": v(0, 10) * mm});
            skLineSegment(sketch, "E646.bottom", {"start": v(200, 14.5) * mm, "end": v(-200, 14.5) * mm});
            skLineSegment(sketch, "E646.top", {"start": v(200, 15.5) * mm, "end": v(-200, 15.5) * mm});
            skLineSegment(sketch, "E646.left", {"start": v(200, 14.5) * mm, "end": v(200, 15.5) * mm});
            skLineSegment(sketch, "E646.right", {"start": v(-200, 14.5) * mm, "end": v(-200, 15.5) * mm});
            skPoint(sketch, "E646.middle", {"position": v(0, 15) * mm});
            skLineSegment(sketch, "E647.bottom", {"start": v(-200, 19.5) * mm, "end": v(200, 19.5) * mm});
            skLineSegment(sketch, "E647.top", {"start": v(-200, 20.5) * mm, "end": v(200, 20.5) * mm});
            skLineSegment(sketch, "E647.left", {"start": v(-200, 19.5) * mm, "end": v(-200, 20.5) * mm});
            skLineSegment(sketch, "E647.right", {"start": v(200, 19.5) * mm, "end": v(200, 20.5) * mm});
            skPoint(sketch, "E647.middle", {"position": v(0, 20) * mm});
            skLineSegment(sketch, "E648.bottom", {"start": v(40.5, 20) * mm, "end": v(39.5, 20) * mm});
            skLineSegment(sketch, "E648.top", {"start": v(40.5, 10) * mm, "end": v(39.5, 10) * mm});
            skLineSegment(sketch, "E648.left", {"start": v(40.5, 20) * mm, "end": v(40.5, 10) * mm});
            skLineSegment(sketch, "E648.right", {"start": v(39.5, 20) * mm, "end": v(39.5, 10) * mm});
            skPoint(sketch, "E648.middle", {"position": v(40, 15) * mm});
            skLineSegment(sketch, "E649.bottom", {"start": v(20.5, 20) * mm, "end": v(19.5, 20) * mm});
            skLineSegment(sketch, "E649.top", {"start": v(20.5, 10) * mm, "end": v(19.5, 10) * mm});
            skLineSegment(sketch, "E649.left", {"start": v(20.5, 20) * mm, "end": v(20.5, 10) * mm});
            skLineSegment(sketch, "E649.right", {"start": v(19.5, 20) * mm, "end": v(19.5, 10) * mm});
            skPoint(sketch, "E649.middle", {"position": v(20, 15) * mm});
            skLineSegment(sketch, "E650.bottom", {"start": v(0.5, 20) * mm, "end": v(-0.5, 20) * mm});
            skLineSegment(sketch, "E650.top", {"start": v(0.5, 10) * mm, "end": v(-0.5, 10) * mm});
            skLineSegment(sketch, "E650.left", {"start": v(0.5, 20) * mm, "end": v(0.5, 10) * mm});
            skLineSegment(sketch, "E650.right", {"start": v(-0.5, 20) * mm, "end": v(-0.5, 10) * mm});
            skLineSegment(sketch, "E651.bottom", {"start": v(-19.5, 20) * mm, "end": v(-20.5, 20) * mm});
            skLineSegment(sketch, "E651.top", {"start": v(-19.5, 10) * mm, "end": v(-20.5, 10) * mm});
            skLineSegment(sketch, "E651.left", {"start": v(-19.5, 20) * mm, "end": v(-19.5, 10) * mm});
            skLineSegment(sketch, "E651.right", {"start": v(-20.5, 20) * mm, "end": v(-20.5, 10) * mm});
            skPoint(sketch, "E651.middle", {"position": v(-20, 15) * mm});
            skLineSegment(sketch, "E652.bottom", {"start": v(-39.5, 20) * mm, "end": v(-40.5, 20) * mm});
            skLineSegment(sketch, "E652.top", {"start": v(-39.5, 10) * mm, "end": v(-40.5, 10) * mm});
            skLineSegment(sketch, "E652.left", {"start": v(-39.5, 20) * mm, "end": v(-39.5, 10) * mm});
            skLineSegment(sketch, "E652.right", {"start": v(-40.5, 20) * mm, "end": v(-40.5, 10) * mm});
            skPoint(sketch, "E652.middle", {"position": v(-40, 15) * mm});
            skLineSegment(sketch, "E653.bottom", {"start": v(-59.5, 20) * mm, "end": v(-60.5, 20) * mm});
            skLineSegment(sketch, "E653.top", {"start": v(-59.5, 10) * mm, "end": v(-60.5, 10) * mm});
            skLineSegment(sketch, "E653.left", {"start": v(-59.5, 20) * mm, "end": v(-59.5, 10) * mm});
            skLineSegment(sketch, "E653.right", {"start": v(-60.5, 20) * mm, "end": v(-60.5, 10) * mm});
            skPoint(sketch, "E653.middle", {"position": v(-60, 15) * mm});
            skLineSegment(sketch, "E654.bottom", {"start": v(-95.5, 20) * mm, "end": v(-94.5, 20) * mm});
            skLineSegment(sketch, "E654.top", {"start": v(-95.5, 10) * mm, "end": v(-94.5, 10) * mm});
            skLineSegment(sketch, "E654.left", {"start": v(-95.5, 20) * mm, "end": v(-95.5, 10) * mm});
            skLineSegment(sketch, "E654.right", {"start": v(-94.5, 20) * mm, "end": v(-94.5, 10) * mm});
            skPoint(sketch, "E654.middle", {"position": v(-95, 15) * mm});
            skLineSegment(sketch, "E655.bottom", {"start": v(-129.5, 20) * mm, "end": v(-130.5, 20) * mm});
            skLineSegment(sketch, "E655.top", {"start": v(-129.5, 10) * mm, "end": v(-130.5, 10) * mm});
            skLineSegment(sketch, "E655.left", {"start": v(-129.5, 20) * mm, "end": v(-129.5, 10) * mm});
            skLineSegment(sketch, "E655.right", {"start": v(-130.5, 20) * mm, "end": v(-130.5, 10) * mm});
            skPoint(sketch, "E655.middle", {"position": v(-130, 15) * mm});
            skLineSegment(sketch, "E656.bottom", {"start": v(-164.5, 20) * mm, "end": v(-165.5, 20) * mm});
            skLineSegment(sketch, "E656.top", {"start": v(-164.5, 10) * mm, "end": v(-165.5, 10) * mm});
            skLineSegment(sketch, "E656.left", {"start": v(-164.5, 20) * mm, "end": v(-164.5, 10) * mm});
            skLineSegment(sketch, "E656.right", {"start": v(-165.5, 20) * mm, "end": v(-165.5, 10) * mm});
            skPoint(sketch, "E656.middle", {"position": v(-165, 15) * mm});
            skSolve(sketch);
        }
        {
            var Q0;
            Q0=qCreatedBy(id+"F27.planeOp",FACE);
            var sketch = newSketch(context, id + "F31", { "sketchPlane" : qUnion([Q0])});
            skLineSegment(sketch, "E657.bottom", {"start": v(-365, 20) * mm, "end": v(365, 20) * mm});
            skLineSegment(sketch, "E657.top", {"start": v(-365, 0) * mm, "end": v(365, 0) * mm});
            skLineSegment(sketch, "E657.left", {"start": v(-365, 20) * mm, "end": v(-365, 0) * mm});
            skLineSegment(sketch, "E657.right", {"start": v(365, 20) * mm, "end": v(365, 0) * mm});
            skLineSegment(sketch, "E658", {"start": v(-365, 10) * mm, "end": v(365, 10) * mm});
            skLineSegment(sketch, "E659", {"start": v(-365, 15) * mm, "end": v(365, 15) * mm});
            skPoint(sketch, "E660", {"position": v(10, 20) * mm});
            skPoint(sketch, "E661", {"position": v(50.63, 20) * mm});
            skPoint(sketch, "E662", {"position": v(91.25, 20) * mm});
            skPoint(sketch, "E663", {"position": v(131.88, 20) * mm});
            skPoint(sketch, "E664", {"position": v(172.5, 20) * mm});
            skPoint(sketch, "E665", {"position": v(321.88, 20) * mm});
            skPoint(sketch, "E666", {"position": v(192.5, 20) * mm});
            skPoint(sketch, "E667", {"position": v(235.63, 20) * mm});
            skPoint(sketch, "E668", {"position": v(278.75, 20) * mm});
            skLineSegment(sketch, "E669", {"start": v(10, 20) * mm, "end": v(10, 10) * mm});
            skLineSegment(sketch, "E670", {"start": v(50.63, 20) * mm, "end": v(50.63, 10) * mm});
            skLineSegment(sketch, "E671", {"start": v(91.25, 20) * mm, "end": v(91.25, 10) * mm});
            skLineSegment(sketch, "E672", {"start": v(131.88, 20) * mm, "end": v(131.88, 10) * mm});
            skLineSegment(sketch, "E673", {"start": v(172.5, 20) * mm, "end": v(172.5, 10) * mm});
            skLineSegment(sketch, "E674", {"start": v(192.5, 20) * mm, "end": v(192.5, 10) * mm});
            skLineSegment(sketch, "E675", {"start": v(235.63, 20) * mm, "end": v(235.63, 10) * mm});
            skLineSegment(sketch, "E676", {"start": v(278.75, 20) * mm, "end": v(278.75, 10) * mm});
            skLineSegment(sketch, "E677", {"start": v(321.88, 20) * mm, "end": v(321.88, 10) * mm});
            skLineSegment(sketch, "E678.MirrorCS", {"start": v(-10, 20) * mm, "end": v(-10, 10) * mm});
            skLineSegment(sketch, "E679.MirrorCS", {"start": v(-50.63, 20) * mm, "end": v(-50.63, 10) * mm});
            skLineSegment(sketch, "E680.MirrorCS", {"start": v(-91.25, 20) * mm, "end": v(-91.25, 10) * mm});
            skLineSegment(sketch, "E681.MirrorCS", {"start": v(-131.88, 20) * mm, "end": v(-131.88, 10) * mm});
            skLineSegment(sketch, "E682.MirrorCS", {"start": v(-172.5, 20) * mm, "end": v(-172.5, 10) * mm});
            skLineSegment(sketch, "E683.MirrorCS", {"start": v(-192.5, 20) * mm, "end": v(-192.5, 10) * mm});
            skLineSegment(sketch, "E684.MirrorCS", {"start": v(-235.63, 20) * mm, "end": v(-235.63, 10) * mm});
            skLineSegment(sketch, "E685.MirrorCS", {"start": v(-278.75, 20) * mm, "end": v(-278.75, 10) * mm});
            skLineSegment(sketch, "E686.MirrorCS", {"start": v(-321.88, 20) * mm, "end": v(-321.88, 10) * mm});
            skLineSegment(sketch, "E687.bottom", {"start": v(-365, 10.5) * mm, "end": v(365, 10.5) * mm});
            skLineSegment(sketch, "E687.top", {"start": v(-365, 9.5) * mm, "end": v(365, 9.5) * mm});
            skLineSegment(sketch, "E687.left", {"start": v(-365, 10.5) * mm, "end": v(-365, 9.5) * mm});
            skLineSegment(sketch, "E687.right", {"start": v(365, 10.5) * mm, "end": v(365, 9.5) * mm});
            skPoint(sketch, "E687.middle", {"position": v(0, 10) * mm});
            skLineSegment(sketch, "E688.bottom", {"start": v(-365, 15.5) * mm, "end": v(365, 15.5) * mm});
            skLineSegment(sketch, "E688.top", {"start": v(-365, 14.5) * mm, "end": v(365, 14.5) * mm});
            skLineSegment(sketch, "E688.left", {"start": v(-365, 15.5) * mm, "end": v(-365, 14.5) * mm});
            skLineSegment(sketch, "E688.right", {"start": v(365, 15.5) * mm, "end": v(365, 14.5) * mm});
            skPoint(sketch, "E688.middle", {"position": v(0, 15) * mm});
            skLineSegment(sketch, "E689.bottom", {"start": v(-365, 20.5) * mm, "end": v(365, 20.5) * mm});
            skLineSegment(sketch, "E689.top", {"start": v(-365, 19.5) * mm, "end": v(365, 19.5) * mm});
            skLineSegment(sketch, "E689.left", {"start": v(-365, 20.5) * mm, "end": v(-365, 19.5) * mm});
            skLineSegment(sketch, "E689.right", {"start": v(365, 20.5) * mm, "end": v(365, 19.5) * mm});
            skPoint(sketch, "E689.middle", {"position": v(0, 20) * mm});
            skLineSegment(sketch, "E690.bottom", {"start": v(-10.5, 20) * mm, "end": v(-9.5, 20) * mm});
            skLineSegment(sketch, "E690.top", {"start": v(-10.5, 10) * mm, "end": v(-9.5, 10) * mm});
            skLineSegment(sketch, "E690.left", {"start": v(-10.5, 20) * mm, "end": v(-10.5, 10) * mm});
            skLineSegment(sketch, "E690.right", {"start": v(-9.5, 20) * mm, "end": v(-9.5, 10) * mm});
            skPoint(sketch, "E690.middle", {"position": v(-10, 15) * mm});
            skLineSegment(sketch, "E691.bottom", {"start": v(-0.5, 20) * mm, "end": v(0.5, 20) * mm});
            skLineSegment(sketch, "E691.top", {"start": v(-0.5, 10) * mm, "end": v(0.5, 10) * mm});
            skLineSegment(sketch, "E691.left", {"start": v(-0.5, 20) * mm, "end": v(-0.5, 10) * mm});
            skLineSegment(sketch, "E691.right", {"start": v(0.5, 20) * mm, "end": v(0.5, 10) * mm});
            skLineSegment(sketch, "E692.bottom", {"start": v(-51.13, 20) * mm, "end": v(-50.13, 20) * mm});
            skLineSegment(sketch, "E692.top", {"start": v(-51.13, 10) * mm, "end": v(-50.13, 10) * mm});
            skLineSegment(sketch, "E692.left", {"start": v(-51.13, 20) * mm, "end": v(-51.13, 10) * mm});
            skLineSegment(sketch, "E692.right", {"start": v(-50.13, 20) * mm, "end": v(-50.13, 10) * mm});
            skPoint(sketch, "E692.middle", {"position": v(-50.63, 15) * mm});
            skLineSegment(sketch, "E693.bottom", {"start": v(-91.75, 20) * mm, "end": v(-90.75, 20) * mm});
            skLineSegment(sketch, "E693.top", {"start": v(-91.75, 10) * mm, "end": v(-90.75, 10) * mm});
            skLineSegment(sketch, "E693.left", {"start": v(-91.75, 20) * mm, "end": v(-91.75, 10) * mm});
            skLineSegment(sketch, "E693.right", {"start": v(-90.75, 20) * mm, "end": v(-90.75, 10) * mm});
            skPoint(sketch, "E693.middle", {"position": v(-91.25, 15) * mm});
            skLineSegment(sketch, "E694.bottom", {"start": v(-131.38, 20) * mm, "end": v(-132.38, 20) * mm});
            skLineSegment(sketch, "E694.top", {"start": v(-131.38, 10) * mm, "end": v(-132.38, 10) * mm});
            skLineSegment(sketch, "E694.left", {"start": v(-131.38, 20) * mm, "end": v(-131.38, 10) * mm});
            skLineSegment(sketch, "E694.right", {"start": v(-132.38, 20) * mm, "end": v(-132.38, 10) * mm});
            skPoint(sketch, "E694.middle", {"position": v(-131.88, 15) * mm});
            skLineSegment(sketch, "E695.bottom", {"start": v(-173, 20) * mm, "end": v(-172, 20) * mm});
            skLineSegment(sketch, "E695.top", {"start": v(-173, 10) * mm, "end": v(-172, 10) * mm});
            skLineSegment(sketch, "E695.left", {"start": v(-173, 20) * mm, "end": v(-173, 10) * mm});
            skLineSegment(sketch, "E695.right", {"start": v(-172, 20) * mm, "end": v(-172, 10) * mm});
            skPoint(sketch, "E695.middle", {"position": v(-172.5, 15) * mm});
            skLineSegment(sketch, "E696.bottom", {"start": v(-192, 20) * mm, "end": v(-193, 20) * mm});
            skLineSegment(sketch, "E696.top", {"start": v(-192, 10) * mm, "end": v(-193, 10) * mm});
            skLineSegment(sketch, "E696.left", {"start": v(-192, 20) * mm, "end": v(-192, 10) * mm});
            skLineSegment(sketch, "E696.right", {"start": v(-193, 20) * mm, "end": v(-193, 10) * mm});
            skPoint(sketch, "E696.middle", {"position": v(-192.5, 15) * mm});
            skLineSegment(sketch, "E697.bottom", {"start": v(-235.13, 20) * mm, "end": v(-236.13, 20) * mm});
            skLineSegment(sketch, "E697.top", {"start": v(-235.13, 10) * mm, "end": v(-236.13, 10) * mm});
            skLineSegment(sketch, "E697.left", {"start": v(-235.13, 20) * mm, "end": v(-235.13, 10) * mm});
            skLineSegment(sketch, "E697.right", {"start": v(-236.13, 20) * mm, "end": v(-236.13, 10) * mm});
            skPoint(sketch, "E697.middle", {"position": v(-235.63, 15) * mm});
            skLineSegment(sketch, "E698.bottom", {"start": v(-278.25, 20) * mm, "end": v(-279.25, 20) * mm});
            skLineSegment(sketch, "E698.top", {"start": v(-278.25, 10) * mm, "end": v(-279.25, 10) * mm});
            skLineSegment(sketch, "E698.left", {"start": v(-278.25, 20) * mm, "end": v(-278.25, 10) * mm});
            skLineSegment(sketch, "E698.right", {"start": v(-279.25, 20) * mm, "end": v(-279.25, 10) * mm});
            skPoint(sketch, "E698.middle", {"position": v(-278.75, 15) * mm});
            skLineSegment(sketch, "E699.bottom", {"start": v(-321.38, 20) * mm, "end": v(-322.38, 20) * mm});
            skLineSegment(sketch, "E699.top", {"start": v(-321.38, 10) * mm, "end": v(-322.38, 10) * mm});
            skLineSegment(sketch, "E699.left", {"start": v(-321.38, 20) * mm, "end": v(-321.38, 10) * mm});
            skLineSegment(sketch, "E699.right", {"start": v(-322.38, 20) * mm, "end": v(-322.38, 10) * mm});
            skPoint(sketch, "E699.middle", {"position": v(-321.88, 15) * mm});
            skLineSegment(sketch, "E700.MirrorCS", {"start": v(9.5, 20) * mm, "end": v(9.5, 10) * mm});
            skLineSegment(sketch, "E701.MirrorCS", {"start": v(10.5, 20) * mm, "end": v(10.5, 10) * mm});
            skLineSegment(sketch, "E702.MirrorCS", {"start": v(50.13, 20) * mm, "end": v(50.13, 10) * mm});
            skLineSegment(sketch, "E703.MirrorCS", {"start": v(51.13, 20) * mm, "end": v(51.13, 10) * mm});
            skLineSegment(sketch, "E704.MirrorCS", {"start": v(90.75, 20) * mm, "end": v(90.75, 10) * mm});
            skLineSegment(sketch, "E705.MirrorCS", {"start": v(91.75, 20) * mm, "end": v(91.75, 10) * mm});
            skLineSegment(sketch, "E706.MirrorCS", {"start": v(132.38, 20) * mm, "end": v(132.38, 10) * mm});
            skLineSegment(sketch, "E707.MirrorCS", {"start": v(131.38, 20) * mm, "end": v(131.38, 10) * mm});
            skLineSegment(sketch, "E708.MirrorCS", {"start": v(172, 20) * mm, "end": v(172, 10) * mm});
            skLineSegment(sketch, "E709.MirrorCS", {"start": v(173, 20) * mm, "end": v(173, 10) * mm});
            skLineSegment(sketch, "E710.MirrorCS", {"start": v(192, 20) * mm, "end": v(192, 10) * mm});
            skLineSegment(sketch, "E711.MirrorCS", {"start": v(193, 20) * mm, "end": v(193, 10) * mm});
            skLineSegment(sketch, "E712.MirrorCS", {"start": v(235.13, 20) * mm, "end": v(235.13, 10) * mm});
            skLineSegment(sketch, "E713.MirrorCS", {"start": v(236.13, 20) * mm, "end": v(236.13, 10) * mm});
            skLineSegment(sketch, "E714.MirrorCS", {"start": v(321.38, 20) * mm, "end": v(321.38, 10) * mm});
            skLineSegment(sketch, "E715.MirrorCS", {"start": v(322.38, 20) * mm, "end": v(322.38, 10) * mm});
            skSolve(sketch);
        }
        {
            var Q0;
            {var subQ76=sQuery(id+"F25.wireOp",EDGE,"E212.top");Q0=makeQuery(id+"F25.imprint","IMPRINT",FACE,{"disambiguationData":[TD([[makeQuery(id+"F25.imprint","IMPRINT",EDGE,{"derivedFrom":subQ76}),-1.0]])]});}
            extrude(context, id + "F32", {"entities" : qUnion([Q0]), "operationType" : NewBodyOperationType.REMOVE, "depth" : 25 * mm, "offsetDistance" : 25 * mm});
        }
        {
            var Q0;
            {var subQ0=sQuery(id+"F25.wireOp",EDGE,"E533.trimOffspring");var subQ1=sQuery(id+"F25.wireOp",EDGE,"E517.trimOffspring");var subQ2=makeQuery(id+"F25.imprint","INTERSECT",VERTEX,{"derivedFrom":[subQ1,subQ0]});Q0=makeQuery(id+"F25.imprint","IMPRINT",FACE,{"disambiguationData":[TD([[makeQuery(id+"F25.imprint","IMPRINT",EDGE,{"disambiguationData":[TD([[subQ2,-1.0]])],"derivedFrom":subQ1}),1.0]])]});}
            var Q1;
            {var subQ1=sQuery(id+"F25.wireOp",EDGE,"E248.left");var subQ3=sQuery(id+"F25.wireOp",EDGE,"E517.trimOffspring");var subQ4=makeQuery(id+"F25.imprint","INTERSECT",VERTEX,{"derivedFrom":[subQ1,subQ3]});Q1=makeQuery(id+"F25.imprint","IMPRINT",FACE,{"disambiguationData":[TD([[makeQuery(id+"F25.imprint","IMPRINT",EDGE,{"disambiguationData":[TD([[subQ4,1.0]])],"derivedFrom":subQ3}),1.0]])]});}
            var Q2;
            {var subQ0=sQuery(id+"F25.wireOp",EDGE,"E275.trimOffspring");var subQ1=sQuery(id+"F25.wireOp",EDGE,"E248.left");var subQ2=makeQuery(id+"F25.imprint","INTERSECT",VERTEX,{"derivedFrom":[subQ1,subQ0]});Q2=makeQuery(id+"F25.imprint","IMPRINT",FACE,{"disambiguationData":[TD([[makeQuery(id+"F25.imprint","IMPRINT",EDGE,{"disambiguationData":[TD([[subQ2,-1.0]])],"derivedFrom":subQ1}),1.0]])]});}
            var Q3;
            {var subQ0=sQuery(id+"F25.wireOp",EDGE,"E273.trimOffspring");var subQ1=sQuery(id+"F25.wireOp",EDGE,"E248.left");var subQ2=makeQuery(id+"F25.imprint","INTERSECT",VERTEX,{"derivedFrom":[subQ1,subQ0]});Q3=makeQuery(id+"F25.imprint","IMPRINT",FACE,{"disambiguationData":[TD([[makeQuery(id+"F25.imprint","IMPRINT",EDGE,{"disambiguationData":[TD([[subQ2,-1.0]])],"derivedFrom":subQ1}),1.0]])]});}
            var Q4;
            {var subQ0=sQuery(id+"F25.wireOp",EDGE,"E272.trimOffspring");var subQ1=sQuery(id+"F25.wireOp",EDGE,"E248.left");var subQ2=makeQuery(id+"F25.imprint","INTERSECT",VERTEX,{"derivedFrom":[subQ1,subQ0]});Q4=makeQuery(id+"F25.imprint","IMPRINT",FACE,{"disambiguationData":[TD([[makeQuery(id+"F25.imprint","IMPRINT",EDGE,{"disambiguationData":[TD([[subQ2,-1.0]])],"derivedFrom":subQ1}),1.0]])]});}
            var Q5;
            {var subQ0=sQuery(id+"F25.wireOp",EDGE,"E274.trimOffspring");var subQ1=sQuery(id+"F25.wireOp",EDGE,"E248.left");var subQ2=makeQuery(id+"F25.imprint","INTERSECT",VERTEX,{"derivedFrom":[subQ1,subQ0]});Q5=makeQuery(id+"F25.imprint","IMPRINT",FACE,{"disambiguationData":[TD([[makeQuery(id+"F25.imprint","IMPRINT",EDGE,{"disambiguationData":[TD([[subQ2,-1.0]])],"derivedFrom":subQ1}),1.0]])]});}
            var Q6;
            {var subQ0=sQuery(id+"F25.wireOp",EDGE,"E270.trimOffspring");var subQ1=sQuery(id+"F25.wireOp",EDGE,"E248.left");var subQ2=makeQuery(id+"F25.imprint","INTERSECT",VERTEX,{"derivedFrom":[subQ1,subQ0]});Q6=makeQuery(id+"F25.imprint","IMPRINT",FACE,{"disambiguationData":[TD([[makeQuery(id+"F25.imprint","IMPRINT",EDGE,{"disambiguationData":[TD([[subQ2,-1.0]])],"derivedFrom":subQ1}),1.0]])]});}
            var Q7;
            {var subQ0=sQuery(id+"F25.wireOp",EDGE,"E268.trimOffspring");var subQ1=sQuery(id+"F25.wireOp",EDGE,"E248.left");var subQ2=makeQuery(id+"F25.imprint","INTERSECT",VERTEX,{"derivedFrom":[subQ1,subQ0]});Q7=makeQuery(id+"F25.imprint","IMPRINT",FACE,{"disambiguationData":[TD([[makeQuery(id+"F25.imprint","IMPRINT",EDGE,{"disambiguationData":[TD([[subQ2,-1.0]])],"derivedFrom":subQ1}),1.0]])]});}
            var Q8;
            {var subQ0=sQuery(id+"F25.wireOp",EDGE,"E268.trimOffspring");var subQ1=sQuery(id+"F25.wireOp",EDGE,"E246.right");var subQ2=makeQuery(id+"F25.imprint","INTERSECT",VERTEX,{"derivedFrom":[subQ1,subQ0]});Q8=makeQuery(id+"F25.imprint","IMPRINT",FACE,{"disambiguationData":[TD([[makeQuery(id+"F25.imprint","IMPRINT",EDGE,{"disambiguationData":[TD([[subQ2,-1.0]])],"derivedFrom":subQ1}),-1.0]])]});}
            var Q9;
            {var subQ0=sQuery(id+"F25.wireOp",EDGE,"E268.trimOffspring");var subQ1=sQuery(id+"F25.wireOp",EDGE,"E245.right");var subQ2=makeQuery(id+"F25.imprint","INTERSECT",VERTEX,{"derivedFrom":[subQ1,subQ0]});Q9=makeQuery(id+"F25.imprint","IMPRINT",FACE,{"disambiguationData":[TD([[makeQuery(id+"F25.imprint","IMPRINT",EDGE,{"disambiguationData":[TD([[subQ2,-1.0]])],"derivedFrom":subQ1}),-1.0]])]});}
            var Q10;
            {var subQ0=sQuery(id+"F25.wireOp",EDGE,"E268.trimOffspring");var subQ1=sQuery(id+"F25.wireOp",EDGE,"E245.left");var subQ2=makeQuery(id+"F25.imprint","INTERSECT",VERTEX,{"derivedFrom":[subQ1,subQ0]});Q10=makeQuery(id+"F25.imprint","IMPRINT",FACE,{"disambiguationData":[TD([[makeQuery(id+"F25.imprint","IMPRINT",EDGE,{"disambiguationData":[TD([[subQ2,-1.0]])],"derivedFrom":subQ1}),-1.0]])]});}
            var Q11;
            {var subQ0=sQuery(id+"F25.wireOp",EDGE,"E268.trimOffspring");var subQ1=sQuery(id+"F25.wireOp",EDGE,"E244.right");var subQ2=makeQuery(id+"F25.imprint","INTERSECT",VERTEX,{"derivedFrom":[subQ1,subQ0]});Q11=makeQuery(id+"F25.imprint","IMPRINT",FACE,{"disambiguationData":[TD([[makeQuery(id+"F25.imprint","IMPRINT",EDGE,{"disambiguationData":[TD([[subQ2,-1.0]])],"derivedFrom":subQ1}),-1.0]])]});}
            var Q12;
            {var subQ0=sQuery(id+"F25.wireOp",EDGE,"E268.trimOffspring");var subQ1=sQuery(id+"F25.wireOp",EDGE,"E243.left");var subQ2=makeQuery(id+"F25.imprint","INTERSECT",VERTEX,{"derivedFrom":[subQ1,subQ0]});Q12=makeQuery(id+"F25.imprint","IMPRINT",FACE,{"disambiguationData":[TD([[makeQuery(id+"F25.imprint","IMPRINT",EDGE,{"disambiguationData":[TD([[subQ2,-1.0]])],"derivedFrom":subQ1}),-1.0]])]});}
            var Q13;
            {var subQ0=sQuery(id+"F25.wireOp",EDGE,"E269.trimOffspring");var subQ1=sQuery(id+"F25.wireOp",EDGE,"E243.right");var subQ2=makeQuery(id+"F25.imprint","INTERSECT",VERTEX,{"derivedFrom":[subQ1,subQ0]});Q13=makeQuery(id+"F25.imprint","IMPRINT",FACE,{"disambiguationData":[TD([[makeQuery(id+"F25.imprint","IMPRINT",EDGE,{"disambiguationData":[TD([[subQ2,1.0]])],"derivedFrom":subQ1}),-1.0]])]});}
            var Q14;
            {var subQ0=sQuery(id+"F25.wireOp",EDGE,"E267.trimOffspring");var subQ1=sQuery(id+"F25.wireOp",EDGE,"E243.right");var subQ2=makeQuery(id+"F25.imprint","INTERSECT",VERTEX,{"derivedFrom":[subQ1,subQ0]});Q14=makeQuery(id+"F25.imprint","IMPRINT",FACE,{"disambiguationData":[TD([[makeQuery(id+"F25.imprint","IMPRINT",EDGE,{"disambiguationData":[TD([[subQ2,-1.0]])],"derivedFrom":subQ1}),-1.0]])]});}
            var Q15;
            {var subQ0=sQuery(id+"F25.wireOp",EDGE,"E243.bottom");Q15=makeQuery(id+"F25.imprint","IMPRINT",FACE,{"disambiguationData":[TD([[makeQuery(id+"F25.imprint","IMPRINT",EDGE,{"derivedFrom":subQ0}),-1.0]])]});}
            var Q16;
            {var subQ0=sQuery(id+"F25.wireOp",EDGE,"E533.trimOffspring");var subQ1=sQuery(id+"F25.wireOp",EDGE,"E517.trimOffspring");var subQ2=makeQuery(id+"F25.imprint","INTERSECT",VERTEX,{"derivedFrom":[subQ1,subQ0]});Q16=makeQuery(id+"F25.imprint","IMPRINT",FACE,{"disambiguationData":[TD([[makeQuery(id+"F25.imprint","IMPRINT",EDGE,{"disambiguationData":[TD([[subQ2,1.0]])],"derivedFrom":subQ1}),1.0]])]});}
            var Q17;
            {var subQ0=sQuery(id+"F25.wireOp",EDGE,"E532.trimOffspring");var subQ1=sQuery(id+"F25.wireOp",EDGE,"E517.trimOffspring");var subQ2=makeQuery(id+"F25.imprint","INTERSECT",VERTEX,{"derivedFrom":[subQ1,subQ0]});Q17=makeQuery(id+"F25.imprint","IMPRINT",FACE,{"disambiguationData":[TD([[makeQuery(id+"F25.imprint","IMPRINT",EDGE,{"disambiguationData":[TD([[subQ2,-1.0]])],"derivedFrom":subQ1}),1.0]])]});}
            var Q18;
            {var subQ0=sQuery(id+"F25.wireOp",EDGE,"E532.trimOffspring");var subQ1=sQuery(id+"F25.wireOp",EDGE,"E518.trimOffspring");var subQ2=makeQuery(id+"F25.imprint","INTERSECT",VERTEX,{"derivedFrom":[subQ1,subQ0]});Q18=makeQuery(id+"F25.imprint","IMPRINT",FACE,{"disambiguationData":[TD([[makeQuery(id+"F25.imprint","IMPRINT",EDGE,{"disambiguationData":[TD([[subQ2,-1.0]])],"derivedFrom":subQ1}),-1.0]])]});}
            var Q19;
            {var subQ0=sQuery(id+"F25.wireOp",EDGE,"E532.trimOffspring");var subQ1=sQuery(id+"F25.wireOp",EDGE,"E507.trimOffspring");var subQ2=makeQuery(id+"F25.imprint","INTERSECT",VERTEX,{"derivedFrom":[subQ1,subQ0]});Q19=makeQuery(id+"F25.imprint","IMPRINT",FACE,{"disambiguationData":[TD([[makeQuery(id+"F25.imprint","IMPRINT",EDGE,{"disambiguationData":[TD([[subQ2,-1.0]])],"derivedFrom":subQ1}),-1.0]])]});}
            var Q20;
            {var subQ0=sQuery(id+"F25.wireOp",EDGE,"E532.trimOffspring");var subQ1=sQuery(id+"F25.wireOp",EDGE,"E517.trimOffspring");var subQ2=makeQuery(id+"F25.imprint","INTERSECT",VERTEX,{"derivedFrom":[subQ1,subQ0]});Q20=makeQuery(id+"F25.imprint","IMPRINT",FACE,{"disambiguationData":[TD([[makeQuery(id+"F25.imprint","IMPRINT",EDGE,{"disambiguationData":[TD([[subQ2,-1.0]])],"derivedFrom":subQ1}),1.0]])]});}
            var Q21;
            {var subQ0=sQuery(id+"F25.wireOp",EDGE,"E518.trimOffspring");var subQ1=sQuery(id+"F25.wireOp",EDGE,"E247.left");var subQ2=makeQuery(id+"F25.imprint","INTERSECT",VERTEX,{"derivedFrom":[subQ1,subQ0]});Q21=makeQuery(id+"F25.imprint","IMPRINT",FACE,{"disambiguationData":[TD([[makeQuery(id+"F25.imprint","IMPRINT",EDGE,{"disambiguationData":[TD([[subQ2,1.0]])],"derivedFrom":subQ0}),-1.0]])]});}
            var Q22;
            {var subQ0=sQuery(id+"F25.wireOp",EDGE,"E534.MirrorCS");var subQ1=sQuery(id+"F25.wireOp",EDGE,"E518.trimOffspring");var subQ2=makeQuery(id+"F25.imprint","INTERSECT",VERTEX,{"derivedFrom":[subQ1,subQ0]});Q22=makeQuery(id+"F25.imprint","IMPRINT",FACE,{"disambiguationData":[TD([[makeQuery(id+"F25.imprint","IMPRINT",EDGE,{"disambiguationData":[TD([[subQ2,1.0]])],"derivedFrom":subQ1}),-1.0]])]});}
            var Q23;
            {var subQ0=sQuery(id+"F25.wireOp",EDGE,"E527.trimOffspring");var subQ1=sQuery(id+"F25.wireOp",EDGE,"E518.trimOffspring");var subQ2=makeQuery(id+"F25.imprint","INTERSECT",VERTEX,{"derivedFrom":[subQ1,subQ0]});Q23=makeQuery(id+"F25.imprint","IMPRINT",FACE,{"disambiguationData":[TD([[makeQuery(id+"F25.imprint","IMPRINT",EDGE,{"disambiguationData":[TD([[subQ2,-1.0]])],"derivedFrom":subQ1}),-1.0]])]});}
            var Q24;
            {var subQ0=sQuery(id+"F25.wireOp",EDGE,"E532.trimOffspring");var subQ1=sQuery(id+"F25.wireOp",EDGE,"E507.trimOffspring");var subQ2=makeQuery(id+"F25.imprint","INTERSECT",VERTEX,{"derivedFrom":[subQ1,subQ0]});Q24=makeQuery(id+"F25.imprint","IMPRINT",FACE,{"disambiguationData":[TD([[makeQuery(id+"F25.imprint","IMPRINT",EDGE,{"disambiguationData":[TD([[subQ2,-1.0]])],"derivedFrom":subQ1}),1.0]])]});}
            var Q25;
            {var subQ0=sQuery(id+"F25.wireOp",EDGE,"E527.trimOffspring");var subQ1=sQuery(id+"F25.wireOp",EDGE,"E507.trimOffspring");var subQ2=makeQuery(id+"F25.imprint","INTERSECT",VERTEX,{"derivedFrom":[subQ1,subQ0]});Q25=makeQuery(id+"F25.imprint","IMPRINT",FACE,{"disambiguationData":[TD([[makeQuery(id+"F25.imprint","IMPRINT",EDGE,{"disambiguationData":[TD([[subQ2,-1.0]])],"derivedFrom":subQ1}),1.0]])]});}
            var Q26;
            {var subQ0=sQuery(id+"F25.wireOp",EDGE,"E535.trimOffspring");var subQ1=sQuery(id+"F25.wireOp",EDGE,"E507.trimOffspring");var subQ2=makeQuery(id+"F25.imprint","INTERSECT",VERTEX,{"derivedFrom":[subQ1,subQ0]});Q26=makeQuery(id+"F25.imprint","IMPRINT",FACE,{"disambiguationData":[TD([[makeQuery(id+"F25.imprint","IMPRINT",EDGE,{"disambiguationData":[TD([[subQ2,1.0]])],"derivedFrom":subQ1}),1.0]])]});}
            var Q27;
            {var subQ0=sQuery(id+"F25.wireOp",EDGE,"E527.trimOffspring");var subQ1=sQuery(id+"F25.wireOp",EDGE,"E507.trimOffspring");var subQ2=makeQuery(id+"F25.imprint","INTERSECT",VERTEX,{"derivedFrom":[subQ1,subQ0]});Q27=makeQuery(id+"F25.imprint","IMPRINT",FACE,{"disambiguationData":[TD([[makeQuery(id+"F25.imprint","IMPRINT",EDGE,{"disambiguationData":[TD([[subQ2,-1.0]])],"derivedFrom":subQ1}),-1.0]])]});}
            var Q28;
            {var subQ0=sQuery(id+"F25.wireOp",EDGE,"E520.trimOffspring");var subQ1=sQuery(id+"F25.wireOp",EDGE,"E507.trimOffspring");var subQ2=makeQuery(id+"F25.imprint","INTERSECT",VERTEX,{"derivedFrom":[subQ1,subQ0]});Q28=makeQuery(id+"F25.imprint","IMPRINT",FACE,{"disambiguationData":[TD([[makeQuery(id+"F25.imprint","IMPRINT",EDGE,{"disambiguationData":[TD([[subQ2,1.0]])],"derivedFrom":subQ1}),1.0]])]});}
            var Q29;
            {var subQ0=sQuery(id+"F25.wireOp",EDGE,"E523.trimOffspring");var subQ1=sQuery(id+"F25.wireOp",EDGE,"E507.trimOffspring");var subQ2=makeQuery(id+"F25.imprint","INTERSECT",VERTEX,{"derivedFrom":[subQ1,subQ0]});Q29=makeQuery(id+"F25.imprint","IMPRINT",FACE,{"disambiguationData":[TD([[makeQuery(id+"F25.imprint","IMPRINT",EDGE,{"disambiguationData":[TD([[subQ2,1.0]])],"derivedFrom":subQ1}),1.0]])]});}
            var Q30;
            {var subQ0=sQuery(id+"F25.wireOp",EDGE,"E532.trimOffspring");var subQ1=sQuery(id+"F25.wireOp",EDGE,"E510.trimOffspring");var subQ2=makeQuery(id+"F25.imprint","INTERSECT",VERTEX,{"derivedFrom":[subQ1,subQ0]});Q30=makeQuery(id+"F25.imprint","IMPRINT",FACE,{"disambiguationData":[TD([[makeQuery(id+"F25.imprint","IMPRINT",EDGE,{"disambiguationData":[TD([[subQ2,-1.0]])],"derivedFrom":subQ1}),-1.0]])]});}
            var Q31;
            {var subQ0=sQuery(id+"F25.wireOp",EDGE,"E527.trimOffspring");var subQ1=sQuery(id+"F25.wireOp",EDGE,"E510.trimOffspring");var subQ2=makeQuery(id+"F25.imprint","INTERSECT",VERTEX,{"derivedFrom":[subQ1,subQ0]});Q31=makeQuery(id+"F25.imprint","IMPRINT",FACE,{"disambiguationData":[TD([[makeQuery(id+"F25.imprint","IMPRINT",EDGE,{"disambiguationData":[TD([[subQ2,-1.0]])],"derivedFrom":subQ1}),-1.0]])]});}
            var Q32;
            {var subQ0=sQuery(id+"F25.wireOp",EDGE,"E533.trimOffspring");var subQ1=sQuery(id+"F25.wireOp",EDGE,"E510.trimOffspring");var subQ2=makeQuery(id+"F25.imprint","INTERSECT",VERTEX,{"derivedFrom":[subQ1,subQ0]});Q32=makeQuery(id+"F25.imprint","IMPRINT",FACE,{"disambiguationData":[TD([[makeQuery(id+"F25.imprint","IMPRINT",EDGE,{"disambiguationData":[TD([[subQ2,-1.0]])],"derivedFrom":subQ1}),-1.0]])]});}
            var Q33;
            {var subQ0=sQuery(id+"F25.wireOp",EDGE,"E532.trimOffspring");var subQ1=sQuery(id+"F25.wireOp",EDGE,"E510.trimOffspring");var subQ2=makeQuery(id+"F25.imprint","INTERSECT",VERTEX,{"derivedFrom":[subQ1,subQ0]});Q33=makeQuery(id+"F25.imprint","IMPRINT",FACE,{"disambiguationData":[TD([[makeQuery(id+"F25.imprint","IMPRINT",EDGE,{"disambiguationData":[TD([[subQ2,-1.0]])],"derivedFrom":subQ1}),-1.0]])]});}
            var Q34;
            {var subQ0=sQuery(id+"F25.wireOp",EDGE,"E535.trimOffspring");var subQ1=sQuery(id+"F25.wireOp",EDGE,"E510.trimOffspring");var subQ2=makeQuery(id+"F25.imprint","INTERSECT",VERTEX,{"derivedFrom":[subQ1,subQ0]});Q34=makeQuery(id+"F25.imprint","IMPRINT",FACE,{"disambiguationData":[TD([[makeQuery(id+"F25.imprint","IMPRINT",EDGE,{"disambiguationData":[TD([[subQ2,-1.0]])],"derivedFrom":subQ1}),-1.0]])]});}
            var Q35;
            {var subQ0=sQuery(id+"F25.wireOp",EDGE,"E520.trimOffspring");var subQ1=sQuery(id+"F25.wireOp",EDGE,"E510.trimOffspring");var subQ2=makeQuery(id+"F25.imprint","INTERSECT",VERTEX,{"derivedFrom":[subQ1,subQ0]});Q35=makeQuery(id+"F25.imprint","IMPRINT",FACE,{"disambiguationData":[TD([[makeQuery(id+"F25.imprint","IMPRINT",EDGE,{"disambiguationData":[TD([[subQ2,-1.0]])],"derivedFrom":subQ1}),-1.0]])]});}
            var Q36;
            {var subQ0=sQuery(id+"F25.wireOp",EDGE,"E518.trimOffspring");var subQ5=sQuery(id+"F25.wireOp",EDGE,"E248.right");var subQ7=makeQuery(id+"F25.imprint","INTERSECT",VERTEX,{"derivedFrom":[subQ5,subQ0]});Q36=makeQuery(id+"F25.imprint","IMPRINT",FACE,{"disambiguationData":[TD([[makeQuery(id+"F25.imprint","IMPRINT",EDGE,{"disambiguationData":[TD([[subQ7,1.0]])],"derivedFrom":subQ5}),1.0]])]});}
            var Q37;
            {var subQ3=sQuery(id+"F25.wireOp",EDGE,"E517.trimOffspring");var subQ5=sQuery(id+"F25.wireOp",EDGE,"E248.right");var subQ6=makeQuery(id+"F25.imprint","INTERSECT",VERTEX,{"derivedFrom":[subQ5,subQ3]});Q37=makeQuery(id+"F25.imprint","IMPRINT",FACE,{"disambiguationData":[TD([[makeQuery(id+"F25.imprint","IMPRINT",EDGE,{"disambiguationData":[TD([[subQ6,-1.0]])],"derivedFrom":subQ5}),1.0]])]});}
            var Q38;
            {var subQ0=sQuery(id+"F25.wireOp",EDGE,"E275.trimOffspring");var subQ1=sQuery(id+"F25.wireOp",EDGE,"E248.left");var subQ2=makeQuery(id+"F25.imprint","INTERSECT",VERTEX,{"derivedFrom":[subQ1,subQ0]});Q38=makeQuery(id+"F25.imprint","IMPRINT",FACE,{"disambiguationData":[TD([[makeQuery(id+"F25.imprint","IMPRINT",EDGE,{"disambiguationData":[TD([[subQ2,-1.0]])],"derivedFrom":subQ1}),-1.0]])]});}
            var Q39;
            {var subQ0=sQuery(id+"F25.wireOp",EDGE,"E273.trimOffspring");var subQ1=sQuery(id+"F25.wireOp",EDGE,"E248.left");var subQ2=makeQuery(id+"F25.imprint","INTERSECT",VERTEX,{"derivedFrom":[subQ1,subQ0]});Q39=makeQuery(id+"F25.imprint","IMPRINT",FACE,{"disambiguationData":[TD([[makeQuery(id+"F25.imprint","IMPRINT",EDGE,{"disambiguationData":[TD([[subQ2,-1.0]])],"derivedFrom":subQ1}),-1.0]])]});}
            var Q40;
            {var subQ0=sQuery(id+"F25.wireOp",EDGE,"E272.trimOffspring");var subQ1=sQuery(id+"F25.wireOp",EDGE,"E248.left");var subQ2=makeQuery(id+"F25.imprint","INTERSECT",VERTEX,{"derivedFrom":[subQ1,subQ0]});Q40=makeQuery(id+"F25.imprint","IMPRINT",FACE,{"disambiguationData":[TD([[makeQuery(id+"F25.imprint","IMPRINT",EDGE,{"disambiguationData":[TD([[subQ2,-1.0]])],"derivedFrom":subQ1}),-1.0]])]});}
            var Q41;
            {var subQ0=sQuery(id+"F25.wireOp",EDGE,"E272.trimOffspring");var subQ1=sQuery(id+"F25.wireOp",EDGE,"E246.right");var subQ2=makeQuery(id+"F25.imprint","INTERSECT",VERTEX,{"derivedFrom":[subQ1,subQ0]});Q41=makeQuery(id+"F25.imprint","IMPRINT",FACE,{"disambiguationData":[TD([[makeQuery(id+"F25.imprint","IMPRINT",EDGE,{"disambiguationData":[TD([[subQ2,-1.0]])],"derivedFrom":subQ1}),-1.0]])]});}
            var Q42;
            {var subQ0=sQuery(id+"F25.wireOp",EDGE,"E272.trimOffspring");var subQ1=sQuery(id+"F25.wireOp",EDGE,"E245.left");var subQ2=makeQuery(id+"F25.imprint","INTERSECT",VERTEX,{"derivedFrom":[subQ1,subQ0]});Q42=makeQuery(id+"F25.imprint","IMPRINT",FACE,{"disambiguationData":[TD([[makeQuery(id+"F25.imprint","IMPRINT",EDGE,{"disambiguationData":[TD([[subQ2,-1.0]])],"derivedFrom":subQ1}),-1.0]])]});}
            var Q43;
            {var subQ0=sQuery(id+"F25.wireOp",EDGE,"E273.trimOffspring");var subQ1=sQuery(id+"F25.wireOp",EDGE,"E245.right");var subQ2=makeQuery(id+"F25.imprint","INTERSECT",VERTEX,{"derivedFrom":[subQ1,subQ0]});Q43=makeQuery(id+"F25.imprint","IMPRINT",FACE,{"disambiguationData":[TD([[makeQuery(id+"F25.imprint","IMPRINT",EDGE,{"disambiguationData":[TD([[subQ2,1.0]])],"derivedFrom":subQ1}),-1.0]])]});}
            var Q44;
            {var subQ0=sQuery(id+"F25.wireOp",EDGE,"E272.trimOffspring");var subQ1=sQuery(id+"F25.wireOp",EDGE,"E244.right");var subQ2=makeQuery(id+"F25.imprint","INTERSECT",VERTEX,{"derivedFrom":[subQ1,subQ0]});Q44=makeQuery(id+"F25.imprint","IMPRINT",FACE,{"disambiguationData":[TD([[makeQuery(id+"F25.imprint","IMPRINT",EDGE,{"disambiguationData":[TD([[subQ2,-1.0]])],"derivedFrom":subQ1}),-1.0]])]});}
            var Q45;
            {var subQ0=sQuery(id+"F25.wireOp",EDGE,"E272.trimOffspring");var subQ1=sQuery(id+"F25.wireOp",EDGE,"E243.left");var subQ2=makeQuery(id+"F25.imprint","INTERSECT",VERTEX,{"derivedFrom":[subQ1,subQ0]});Q45=makeQuery(id+"F25.imprint","IMPRINT",FACE,{"disambiguationData":[TD([[makeQuery(id+"F25.imprint","IMPRINT",EDGE,{"disambiguationData":[TD([[subQ2,-1.0]])],"derivedFrom":subQ1}),-1.0]])]});}
            var Q46;
            {var subQ0=sQuery(id+"F25.wireOp",EDGE,"E271.trimOffspring");var subQ1=sQuery(id+"F25.wireOp",EDGE,"E243.left");var subQ2=makeQuery(id+"F25.imprint","INTERSECT",VERTEX,{"derivedFrom":[subQ1,subQ0]});Q46=makeQuery(id+"F25.imprint","IMPRINT",FACE,{"disambiguationData":[TD([[makeQuery(id+"F25.imprint","IMPRINT",EDGE,{"disambiguationData":[TD([[subQ2,-1.0]])],"derivedFrom":subQ1}),-1.0]])]});}
            var Q47;
            {var subQ0=sQuery(id+"F25.wireOp",EDGE,"E270.trimOffspring");var subQ1=sQuery(id+"F25.wireOp",EDGE,"E243.left");var subQ2=makeQuery(id+"F25.imprint","INTERSECT",VERTEX,{"derivedFrom":[subQ1,subQ0]});Q47=makeQuery(id+"F25.imprint","IMPRINT",FACE,{"disambiguationData":[TD([[makeQuery(id+"F25.imprint","IMPRINT",EDGE,{"disambiguationData":[TD([[subQ2,-1.0]])],"derivedFrom":subQ1}),-1.0]])]});}
            var Q48;
            {var subQ0=sQuery(id+"F25.wireOp",EDGE,"E274.trimOffspring");var subQ1=sQuery(id+"F25.wireOp",EDGE,"E243.left");var subQ2=makeQuery(id+"F25.imprint","INTERSECT",VERTEX,{"derivedFrom":[subQ1,subQ0]});Q48=makeQuery(id+"F25.imprint","IMPRINT",FACE,{"disambiguationData":[TD([[makeQuery(id+"F25.imprint","IMPRINT",EDGE,{"disambiguationData":[TD([[subQ2,-1.0]])],"derivedFrom":subQ1}),-1.0]])]});}
            var Q49;
            {var subQ0=sQuery(id+"F25.wireOp",EDGE,"E269.trimOffspring");var subQ1=sQuery(id+"F25.wireOp",EDGE,"E243.left");var subQ2=makeQuery(id+"F25.imprint","INTERSECT",VERTEX,{"derivedFrom":[subQ1,subQ0]});Q49=makeQuery(id+"F25.imprint","IMPRINT",FACE,{"disambiguationData":[TD([[makeQuery(id+"F25.imprint","IMPRINT",EDGE,{"disambiguationData":[TD([[subQ2,-1.0]])],"derivedFrom":subQ1}),-1.0]])]});}
            var Q50;
            {var subQ0=sQuery(id+"F25.wireOp",EDGE,"E274.trimOffspring");var subQ1=sQuery(id+"F25.wireOp",EDGE,"E244.right");var subQ2=makeQuery(id+"F25.imprint","INTERSECT",VERTEX,{"derivedFrom":[subQ1,subQ0]});Q50=makeQuery(id+"F25.imprint","IMPRINT",FACE,{"disambiguationData":[TD([[makeQuery(id+"F25.imprint","IMPRINT",EDGE,{"disambiguationData":[TD([[subQ2,-1.0]])],"derivedFrom":subQ1}),-1.0]])]});}
            var Q51;
            {var subQ0=sQuery(id+"F25.wireOp",EDGE,"E270.trimOffspring");var subQ1=sQuery(id+"F25.wireOp",EDGE,"E244.right");var subQ2=makeQuery(id+"F25.imprint","INTERSECT",VERTEX,{"derivedFrom":[subQ1,subQ0]});Q51=makeQuery(id+"F25.imprint","IMPRINT",FACE,{"disambiguationData":[TD([[makeQuery(id+"F25.imprint","IMPRINT",EDGE,{"disambiguationData":[TD([[subQ2,-1.0]])],"derivedFrom":subQ1}),-1.0]])]});}
            var Q52;
            {var subQ0=sQuery(id+"F25.wireOp",EDGE,"E274.trimOffspring");var subQ1=sQuery(id+"F25.wireOp",EDGE,"E245.right");var subQ2=makeQuery(id+"F25.imprint","INTERSECT",VERTEX,{"derivedFrom":[subQ1,subQ0]});Q52=makeQuery(id+"F25.imprint","IMPRINT",FACE,{"disambiguationData":[TD([[makeQuery(id+"F25.imprint","IMPRINT",EDGE,{"disambiguationData":[TD([[subQ2,-1.0]])],"derivedFrom":subQ1}),-1.0]])]});}
            var Q53;
            {var subQ0=sQuery(id+"F25.wireOp",EDGE,"E270.trimOffspring");var subQ1=sQuery(id+"F25.wireOp",EDGE,"E245.right");var subQ2=makeQuery(id+"F25.imprint","INTERSECT",VERTEX,{"derivedFrom":[subQ1,subQ0]});Q53=makeQuery(id+"F25.imprint","IMPRINT",FACE,{"disambiguationData":[TD([[makeQuery(id+"F25.imprint","IMPRINT",EDGE,{"disambiguationData":[TD([[subQ2,-1.0]])],"derivedFrom":subQ1}),-1.0]])]});}
            var Q54;
            {var subQ0=sQuery(id+"F25.wireOp",EDGE,"E274.trimOffspring");var subQ1=sQuery(id+"F25.wireOp",EDGE,"E245.left");var subQ2=makeQuery(id+"F25.imprint","INTERSECT",VERTEX,{"derivedFrom":[subQ1,subQ0]});Q54=makeQuery(id+"F25.imprint","IMPRINT",FACE,{"disambiguationData":[TD([[makeQuery(id+"F25.imprint","IMPRINT",EDGE,{"disambiguationData":[TD([[subQ2,-1.0]])],"derivedFrom":subQ1}),-1.0]])]});}
            var Q55;
            {var subQ0=sQuery(id+"F25.wireOp",EDGE,"E270.trimOffspring");var subQ1=sQuery(id+"F25.wireOp",EDGE,"E245.left");var subQ2=makeQuery(id+"F25.imprint","INTERSECT",VERTEX,{"derivedFrom":[subQ1,subQ0]});Q55=makeQuery(id+"F25.imprint","IMPRINT",FACE,{"disambiguationData":[TD([[makeQuery(id+"F25.imprint","IMPRINT",EDGE,{"disambiguationData":[TD([[subQ2,-1.0]])],"derivedFrom":subQ1}),-1.0]])]});}
            var Q56;
            {var subQ0=sQuery(id+"F25.wireOp",EDGE,"E274.trimOffspring");var subQ1=sQuery(id+"F25.wireOp",EDGE,"E246.right");var subQ2=makeQuery(id+"F25.imprint","INTERSECT",VERTEX,{"derivedFrom":[subQ1,subQ0]});Q56=makeQuery(id+"F25.imprint","IMPRINT",FACE,{"disambiguationData":[TD([[makeQuery(id+"F25.imprint","IMPRINT",EDGE,{"disambiguationData":[TD([[subQ2,-1.0]])],"derivedFrom":subQ1}),-1.0]])]});}
            var Q57;
            {var subQ0=sQuery(id+"F25.wireOp",EDGE,"E270.trimOffspring");var subQ1=sQuery(id+"F25.wireOp",EDGE,"E246.right");var subQ2=makeQuery(id+"F25.imprint","INTERSECT",VERTEX,{"derivedFrom":[subQ1,subQ0]});Q57=makeQuery(id+"F25.imprint","IMPRINT",FACE,{"disambiguationData":[TD([[makeQuery(id+"F25.imprint","IMPRINT",EDGE,{"disambiguationData":[TD([[subQ2,-1.0]])],"derivedFrom":subQ1}),-1.0]])]});}
            var Q58;
            {var subQ0=sQuery(id+"F25.wireOp",EDGE,"E270.trimOffspring");var subQ1=sQuery(id+"F25.wireOp",EDGE,"E248.left");var subQ2=makeQuery(id+"F25.imprint","INTERSECT",VERTEX,{"derivedFrom":[subQ1,subQ0]});Q58=makeQuery(id+"F25.imprint","IMPRINT",FACE,{"disambiguationData":[TD([[makeQuery(id+"F25.imprint","IMPRINT",EDGE,{"disambiguationData":[TD([[subQ2,-1.0]])],"derivedFrom":subQ1}),-1.0]])]});}
            var Q59;
            {var subQ0=sQuery(id+"F25.wireOp",EDGE,"E274.trimOffspring");var subQ1=sQuery(id+"F25.wireOp",EDGE,"E248.left");var subQ2=makeQuery(id+"F25.imprint","INTERSECT",VERTEX,{"derivedFrom":[subQ1,subQ0]});Q59=makeQuery(id+"F25.imprint","IMPRINT",FACE,{"disambiguationData":[TD([[makeQuery(id+"F25.imprint","IMPRINT",EDGE,{"disambiguationData":[TD([[subQ2,-1.0]])],"derivedFrom":subQ1}),-1.0]])]});}
            var Q60;
            {var subQ0=sQuery(id+"F25.wireOp",EDGE,"E244.bottom");Q60=makeQuery(id+"F25.imprint","IMPRINT",FACE,{"disambiguationData":[TD([[makeQuery(id+"F25.imprint","IMPRINT",EDGE,{"derivedFrom":subQ0}),1.0]])]});}
            var Q61;
            {var subQ0=sQuery(id+"F25.wireOp",EDGE,"E267.trimOffspring");var subQ1=sQuery(id+"F25.wireOp",EDGE,"E243.left");var subQ2=makeQuery(id+"F25.imprint","INTERSECT",VERTEX,{"derivedFrom":[subQ1,subQ0]});Q61=makeQuery(id+"F25.imprint","IMPRINT",FACE,{"disambiguationData":[TD([[makeQuery(id+"F25.imprint","IMPRINT",EDGE,{"disambiguationData":[TD([[subQ2,-1.0]])],"derivedFrom":subQ1}),-1.0]])]});}
            var Q62;
            {var subQ0=sQuery(id+"F25.wireOp",EDGE,"E267.trimOffspring");var subQ1=sQuery(id+"F25.wireOp",EDGE,"E244.right");var subQ2=makeQuery(id+"F25.imprint","INTERSECT",VERTEX,{"derivedFrom":[subQ1,subQ0]});Q62=makeQuery(id+"F25.imprint","IMPRINT",FACE,{"disambiguationData":[TD([[makeQuery(id+"F25.imprint","IMPRINT",EDGE,{"disambiguationData":[TD([[subQ2,-1.0]])],"derivedFrom":subQ1}),-1.0]])]});}
            var Q63;
            {var subQ0=sQuery(id+"F25.wireOp",EDGE,"E267.trimOffspring");var subQ1=sQuery(id+"F25.wireOp",EDGE,"E245.right");var subQ2=makeQuery(id+"F25.imprint","INTERSECT",VERTEX,{"derivedFrom":[subQ1,subQ0]});Q63=makeQuery(id+"F25.imprint","IMPRINT",FACE,{"disambiguationData":[TD([[makeQuery(id+"F25.imprint","IMPRINT",EDGE,{"disambiguationData":[TD([[subQ2,-1.0]])],"derivedFrom":subQ1}),-1.0]])]});}
            var Q64;
            {var subQ0=sQuery(id+"F25.wireOp",EDGE,"E267.trimOffspring");var subQ1=sQuery(id+"F25.wireOp",EDGE,"E245.left");var subQ2=makeQuery(id+"F25.imprint","INTERSECT",VERTEX,{"derivedFrom":[subQ1,subQ0]});Q64=makeQuery(id+"F25.imprint","IMPRINT",FACE,{"disambiguationData":[TD([[makeQuery(id+"F25.imprint","IMPRINT",EDGE,{"disambiguationData":[TD([[subQ2,-1.0]])],"derivedFrom":subQ1}),-1.0]])]});}
            var Q65;
            {var subQ0=sQuery(id+"F25.wireOp",EDGE,"E267.trimOffspring");var subQ1=sQuery(id+"F25.wireOp",EDGE,"E246.right");var subQ2=makeQuery(id+"F25.imprint","INTERSECT",VERTEX,{"derivedFrom":[subQ1,subQ0]});Q65=makeQuery(id+"F25.imprint","IMPRINT",FACE,{"disambiguationData":[TD([[makeQuery(id+"F25.imprint","IMPRINT",EDGE,{"disambiguationData":[TD([[subQ2,-1.0]])],"derivedFrom":subQ1}),-1.0]])]});}
            var Q66;
            {var subQ0=sQuery(id+"F25.wireOp",EDGE,"E267.trimOffspring");var subQ1=sQuery(id+"F25.wireOp",EDGE,"E248.left");var subQ2=makeQuery(id+"F25.imprint","INTERSECT",VERTEX,{"derivedFrom":[subQ1,subQ0]});Q66=makeQuery(id+"F25.imprint","IMPRINT",FACE,{"disambiguationData":[TD([[makeQuery(id+"F25.imprint","IMPRINT",EDGE,{"disambiguationData":[TD([[subQ2,-1.0]])],"derivedFrom":subQ1}),1.0]])]});}
            var Q67;
            {var subQ0=sQuery(id+"F25.wireOp",EDGE,"E267.trimOffspring");var subQ1=sQuery(id+"F25.wireOp",EDGE,"E248.left");var subQ2=makeQuery(id+"F25.imprint","INTERSECT",VERTEX,{"derivedFrom":[subQ1,subQ0]});Q67=makeQuery(id+"F25.imprint","IMPRINT",FACE,{"disambiguationData":[TD([[makeQuery(id+"F25.imprint","IMPRINT",EDGE,{"disambiguationData":[TD([[subQ2,-1.0]])],"derivedFrom":subQ1}),-1.0]])]});}
            var Q68;
            {var subQ0=sQuery(id+"F25.wireOp",EDGE,"E268.trimOffspring");var subQ1=sQuery(id+"F25.wireOp",EDGE,"E248.left");var subQ2=makeQuery(id+"F25.imprint","INTERSECT",VERTEX,{"derivedFrom":[subQ1,subQ0]});Q68=makeQuery(id+"F25.imprint","IMPRINT",FACE,{"disambiguationData":[TD([[makeQuery(id+"F25.imprint","IMPRINT",EDGE,{"disambiguationData":[TD([[subQ2,-1.0]])],"derivedFrom":subQ1}),-1.0]])]});}
            var Q69;
            {var subQ0=sQuery(id+"F25.wireOp",EDGE,"E535.trimOffspring");var subQ1=sQuery(id+"F25.wireOp",EDGE,"E510.trimOffspring");var subQ2=makeQuery(id+"F25.imprint","INTERSECT",VERTEX,{"derivedFrom":[subQ1,subQ0]});Q69=makeQuery(id+"F25.imprint","IMPRINT",FACE,{"disambiguationData":[TD([[makeQuery(id+"F25.imprint","IMPRINT",EDGE,{"disambiguationData":[TD([[subQ2,-1.0]])],"derivedFrom":subQ1}),1.0]])]});}
            var Q70;
            {var subQ0=sQuery(id+"F25.wireOp",EDGE,"E520.trimOffspring");var subQ1=sQuery(id+"F25.wireOp",EDGE,"E510.trimOffspring");var subQ2=makeQuery(id+"F25.imprint","INTERSECT",VERTEX,{"derivedFrom":[subQ1,subQ0]});Q70=makeQuery(id+"F25.imprint","IMPRINT",FACE,{"disambiguationData":[TD([[makeQuery(id+"F25.imprint","IMPRINT",EDGE,{"disambiguationData":[TD([[subQ2,-1.0]])],"derivedFrom":subQ1}),1.0]])]});}
            var Q71;
            {var subQ0=sQuery(id+"F25.wireOp",EDGE,"E535.trimOffspring");var subQ1=sQuery(id+"F25.wireOp",EDGE,"E522.trimOffspring");var subQ2=makeQuery(id+"F25.imprint","INTERSECT",VERTEX,{"derivedFrom":[subQ1,subQ0]});Q71=makeQuery(id+"F25.imprint","IMPRINT",FACE,{"disambiguationData":[TD([[makeQuery(id+"F25.imprint","IMPRINT",EDGE,{"disambiguationData":[TD([[subQ2,-1.0]])],"derivedFrom":subQ1}),1.0]])]});}
            var Q72;
            {var subQ1=sQuery(id+"F25.wireOp",EDGE,"E522.trimOffspring");var subQ3=sQuery(id+"F25.wireOp",EDGE,"E520.trimOffspring");var subQ4=makeQuery(id+"F25.imprint","INTERSECT",VERTEX,{"derivedFrom":[subQ1,subQ3]});Q72=makeQuery(id+"F25.imprint","IMPRINT",FACE,{"disambiguationData":[TD([[makeQuery(id+"F25.imprint","IMPRINT",EDGE,{"disambiguationData":[TD([[subQ4,-1.0]])],"derivedFrom":subQ3}),-1.0]])]});}
            var Q73;
            {var subQ0=sQuery(id+"F25.wireOp",EDGE,"E537.MirrorCS");var subQ1=sQuery(id+"F25.wireOp",EDGE,"E520.trimOffspring");var subQ2=makeQuery(id+"F25.imprint","INTERSECT",VERTEX,{"derivedFrom":[subQ1,subQ0]});Q73=makeQuery(id+"F25.imprint","IMPRINT",FACE,{"disambiguationData":[TD([[makeQuery(id+"F25.imprint","IMPRINT",EDGE,{"disambiguationData":[TD([[subQ2,1.0]])],"derivedFrom":subQ1}),1.0]])]});}
            var Q74;
            {var subQ0=sQuery(id+"F25.wireOp",EDGE,"E537.MirrorCS");var subQ1=sQuery(id+"F25.wireOp",EDGE,"E520.trimOffspring");var subQ2=makeQuery(id+"F25.imprint","INTERSECT",VERTEX,{"derivedFrom":[subQ1,subQ0]});Q74=makeQuery(id+"F25.imprint","IMPRINT",FACE,{"disambiguationData":[TD([[makeQuery(id+"F25.imprint","IMPRINT",EDGE,{"disambiguationData":[TD([[subQ2,1.0]])],"derivedFrom":subQ1}),-1.0]])]});}
            var Q75;
            {var subQ0=sQuery(id+"F25.wireOp",EDGE,"E522.trimOffspring");var subQ1=sQuery(id+"F25.wireOp",EDGE,"E276.trimOffspring");var subQ2=makeQuery(id+"F25.imprint","INTERSECT",VERTEX,{"derivedFrom":[subQ1,subQ0]});Q75=makeQuery(id+"F25.imprint","IMPRINT",FACE,{"disambiguationData":[TD([[makeQuery(id+"F25.imprint","IMPRINT",EDGE,{"disambiguationData":[TD([[subQ2,-1.0]])],"derivedFrom":subQ1}),1.0]])]});}
            var Q76;
            {var subQ0=sQuery(id+"F25.wireOp",EDGE,"E525.trimOffspring");var subQ1=sQuery(id+"F25.wireOp",EDGE,"E276.trimOffspring");var subQ2=makeQuery(id+"F25.imprint","INTERSECT",VERTEX,{"derivedFrom":[subQ1,subQ0]});Q76=makeQuery(id+"F25.imprint","IMPRINT",FACE,{"disambiguationData":[TD([[makeQuery(id+"F25.imprint","IMPRINT",EDGE,{"disambiguationData":[TD([[subQ2,1.0]])],"derivedFrom":subQ1}),1.0]])]});}
            var Q77;
            {var subQ0=sQuery(id+"F25.wireOp",EDGE,"E517.trimOffspring");var subQ1=sQuery(id+"F25.wireOp",EDGE,"E276.trimOffspring");var subQ2=makeQuery(id+"F25.imprint","INTERSECT",VERTEX,{"derivedFrom":[subQ1,subQ0]});Q77=makeQuery(id+"F25.imprint","IMPRINT",FACE,{"disambiguationData":[TD([[makeQuery(id+"F25.imprint","IMPRINT",EDGE,{"disambiguationData":[TD([[subQ2,-1.0]])],"derivedFrom":subQ1}),-1.0]])]});}
            var Q78;
            {var subQ0=sQuery(id+"F25.wireOp",EDGE,"E517.trimOffspring");var subQ1=sQuery(id+"F25.wireOp",EDGE,"E277.trimOffspring");var subQ2=makeQuery(id+"F25.imprint","INTERSECT",VERTEX,{"derivedFrom":[subQ1,subQ0]});Q78=makeQuery(id+"F25.imprint","IMPRINT",FACE,{"disambiguationData":[TD([[makeQuery(id+"F25.imprint","IMPRINT",EDGE,{"disambiguationData":[TD([[subQ2,-1.0]])],"derivedFrom":subQ1}),-1.0]])]});}
            var Q79;
            {var subQ0=sQuery(id+"F25.wireOp",EDGE,"E519.trimOffspring");var subQ1=sQuery(id+"F25.wireOp",EDGE,"E277.trimOffspring");var subQ2=makeQuery(id+"F25.imprint","INTERSECT",VERTEX,{"derivedFrom":[subQ1,subQ0]});Q79=makeQuery(id+"F25.imprint","IMPRINT",FACE,{"disambiguationData":[TD([[makeQuery(id+"F25.imprint","IMPRINT",EDGE,{"disambiguationData":[TD([[subQ2,-1.0]])],"derivedFrom":subQ1}),-1.0]])]});}
            var Q80;
            {var subQ0=sQuery(id+"F25.wireOp",EDGE,"E519.trimOffspring");var subQ1=sQuery(id+"F25.wireOp",EDGE,"E276.trimOffspring");var subQ2=makeQuery(id+"F25.imprint","INTERSECT",VERTEX,{"derivedFrom":[subQ1,subQ0]});Q80=makeQuery(id+"F25.imprint","IMPRINT",FACE,{"disambiguationData":[TD([[makeQuery(id+"F25.imprint","IMPRINT",EDGE,{"disambiguationData":[TD([[subQ2,-1.0]])],"derivedFrom":subQ1}),-1.0]])]});}
            var Q81;
            {var subQ0=sQuery(id+"F25.wireOp",EDGE,"E518.trimOffspring");var subQ1=sQuery(id+"F25.wireOp",EDGE,"E276.trimOffspring");var subQ2=makeQuery(id+"F25.imprint","INTERSECT",VERTEX,{"derivedFrom":[subQ1,subQ0]});Q81=makeQuery(id+"F25.imprint","IMPRINT",FACE,{"disambiguationData":[TD([[makeQuery(id+"F25.imprint","IMPRINT",EDGE,{"disambiguationData":[TD([[subQ2,-1.0]])],"derivedFrom":subQ1}),-1.0]])]});}
            var Q82;
            {var subQ0=sQuery(id+"F25.wireOp",EDGE,"E518.trimOffspring");var subQ1=sQuery(id+"F25.wireOp",EDGE,"E277.trimOffspring");var subQ2=makeQuery(id+"F25.imprint","INTERSECT",VERTEX,{"derivedFrom":[subQ1,subQ0]});Q82=makeQuery(id+"F25.imprint","IMPRINT",FACE,{"disambiguationData":[TD([[makeQuery(id+"F25.imprint","IMPRINT",EDGE,{"disambiguationData":[TD([[subQ2,-1.0]])],"derivedFrom":subQ1}),-1.0]])]});}
            var Q83;
            {var subQ0=sQuery(id+"F25.wireOp",EDGE,"E507.trimOffspring");var subQ1=sQuery(id+"F25.wireOp",EDGE,"E276.trimOffspring");var subQ2=makeQuery(id+"F25.imprint","INTERSECT",VERTEX,{"derivedFrom":[subQ1,subQ0]});Q83=makeQuery(id+"F25.imprint","IMPRINT",FACE,{"disambiguationData":[TD([[makeQuery(id+"F25.imprint","IMPRINT",EDGE,{"disambiguationData":[TD([[subQ2,-1.0]])],"derivedFrom":subQ1}),-1.0]])]});}
            var Q84;
            {var subQ0=sQuery(id+"F25.wireOp",EDGE,"E507.trimOffspring");var subQ1=sQuery(id+"F25.wireOp",EDGE,"E277.trimOffspring");var subQ2=makeQuery(id+"F25.imprint","INTERSECT",VERTEX,{"derivedFrom":[subQ1,subQ0]});Q84=makeQuery(id+"F25.imprint","IMPRINT",FACE,{"disambiguationData":[TD([[makeQuery(id+"F25.imprint","IMPRINT",EDGE,{"disambiguationData":[TD([[subQ2,-1.0]])],"derivedFrom":subQ1}),-1.0]])]});}
            var Q85;
            {var subQ0=sQuery(id+"F25.wireOp",EDGE,"E512.trimOffspring");var subQ1=sQuery(id+"F25.wireOp",EDGE,"E276.trimOffspring");var subQ2=makeQuery(id+"F25.imprint","INTERSECT",VERTEX,{"derivedFrom":[subQ1,subQ0]});Q85=makeQuery(id+"F25.imprint","IMPRINT",FACE,{"disambiguationData":[TD([[makeQuery(id+"F25.imprint","IMPRINT",EDGE,{"disambiguationData":[TD([[subQ2,-1.0]])],"derivedFrom":subQ1}),-1.0]])]});}
            var Q86;
            {var subQ0=sQuery(id+"F25.wireOp",EDGE,"E512.trimOffspring");var subQ1=sQuery(id+"F25.wireOp",EDGE,"E277.trimOffspring");var subQ2=makeQuery(id+"F25.imprint","INTERSECT",VERTEX,{"derivedFrom":[subQ1,subQ0]});Q86=makeQuery(id+"F25.imprint","IMPRINT",FACE,{"disambiguationData":[TD([[makeQuery(id+"F25.imprint","IMPRINT",EDGE,{"disambiguationData":[TD([[subQ2,-1.0]])],"derivedFrom":subQ1}),-1.0]])]});}
            var Q87;
            {var subQ0=sQuery(id+"F25.wireOp",EDGE,"E510.trimOffspring");var subQ1=sQuery(id+"F25.wireOp",EDGE,"E277.trimOffspring");var subQ2=makeQuery(id+"F25.imprint","INTERSECT",VERTEX,{"derivedFrom":[subQ1,subQ0]});Q87=makeQuery(id+"F25.imprint","IMPRINT",FACE,{"disambiguationData":[TD([[makeQuery(id+"F25.imprint","IMPRINT",EDGE,{"disambiguationData":[TD([[subQ2,-1.0]])],"derivedFrom":subQ1}),-1.0]])]});}
            var Q88;
            {var subQ0=sQuery(id+"F25.wireOp",EDGE,"E510.trimOffspring");var subQ1=sQuery(id+"F25.wireOp",EDGE,"E276.trimOffspring");var subQ2=makeQuery(id+"F25.imprint","INTERSECT",VERTEX,{"derivedFrom":[subQ1,subQ0]});Q88=makeQuery(id+"F25.imprint","IMPRINT",FACE,{"disambiguationData":[TD([[makeQuery(id+"F25.imprint","IMPRINT",EDGE,{"disambiguationData":[TD([[subQ2,-1.0]])],"derivedFrom":subQ1}),-1.0]])]});}
            var Q89;
            {var subQ0=sQuery(id+"F25.wireOp",EDGE,"E522.trimOffspring");var subQ1=sQuery(id+"F25.wireOp",EDGE,"E276.trimOffspring");var subQ2=makeQuery(id+"F25.imprint","INTERSECT",VERTEX,{"derivedFrom":[subQ1,subQ0]});Q89=makeQuery(id+"F25.imprint","IMPRINT",FACE,{"disambiguationData":[TD([[makeQuery(id+"F25.imprint","IMPRINT",EDGE,{"disambiguationData":[TD([[subQ2,-1.0]])],"derivedFrom":subQ1}),-1.0]])]});}
            var Q90;
            {var subQ0=sQuery(id+"F25.wireOp",EDGE,"E522.trimOffspring");var subQ1=sQuery(id+"F25.wireOp",EDGE,"E277.trimOffspring");var subQ2=makeQuery(id+"F25.imprint","INTERSECT",VERTEX,{"derivedFrom":[subQ1,subQ0]});Q90=makeQuery(id+"F25.imprint","IMPRINT",FACE,{"disambiguationData":[TD([[makeQuery(id+"F25.imprint","IMPRINT",EDGE,{"disambiguationData":[TD([[subQ2,-1.0]])],"derivedFrom":subQ1}),-1.0]])]});}
            var Q91;
            {var subQ0=sQuery(id+"F25.wireOp",EDGE,"E525.trimOffspring");var subQ1=sQuery(id+"F25.wireOp",EDGE,"E277.trimOffspring");var subQ2=makeQuery(id+"F25.imprint","INTERSECT",VERTEX,{"derivedFrom":[subQ1,subQ0]});Q91=makeQuery(id+"F25.imprint","IMPRINT",FACE,{"disambiguationData":[TD([[makeQuery(id+"F25.imprint","IMPRINT",EDGE,{"disambiguationData":[TD([[subQ2,1.0]])],"derivedFrom":subQ1}),-1.0]])]});}
            var Q92;
            {var subQ0=sQuery(id+"F25.wireOp",EDGE,"E525.trimOffspring");var subQ1=sQuery(id+"F25.wireOp",EDGE,"E276.trimOffspring");var subQ2=makeQuery(id+"F25.imprint","INTERSECT",VERTEX,{"derivedFrom":[subQ1,subQ0]});Q92=makeQuery(id+"F25.imprint","IMPRINT",FACE,{"disambiguationData":[TD([[makeQuery(id+"F25.imprint","IMPRINT",EDGE,{"disambiguationData":[TD([[subQ2,1.0]])],"derivedFrom":subQ1}),-1.0]])]});}
            var Q93;
            {var subQ0=sQuery(id+"F25.wireOp",EDGE,"E522.trimOffspring");var subQ1=sQuery(id+"F25.wireOp",EDGE,"E280.trimOffspring");var subQ2=makeQuery(id+"F25.imprint","INTERSECT",VERTEX,{"derivedFrom":[subQ1,subQ0]});Q93=makeQuery(id+"F25.imprint","IMPRINT",FACE,{"disambiguationData":[TD([[makeQuery(id+"F25.imprint","IMPRINT",EDGE,{"disambiguationData":[TD([[subQ2,-1.0]])],"derivedFrom":subQ1}),1.0]])]});}
            var Q94;
            {var subQ0=sQuery(id+"F25.wireOp",EDGE,"E525.trimOffspring");var subQ1=sQuery(id+"F25.wireOp",EDGE,"E280.trimOffspring");var subQ2=makeQuery(id+"F25.imprint","INTERSECT",VERTEX,{"derivedFrom":[subQ1,subQ0]});Q94=makeQuery(id+"F25.imprint","IMPRINT",FACE,{"disambiguationData":[TD([[makeQuery(id+"F25.imprint","IMPRINT",EDGE,{"disambiguationData":[TD([[subQ2,1.0]])],"derivedFrom":subQ1}),1.0]])]});}
            var Q95;
            {var subQ0=sQuery(id+"F25.wireOp",EDGE,"E525.trimOffspring");var subQ1=sQuery(id+"F25.wireOp",EDGE,"E280.trimOffspring");var subQ2=makeQuery(id+"F25.imprint","INTERSECT",VERTEX,{"derivedFrom":[subQ1,subQ0]});Q95=makeQuery(id+"F25.imprint","IMPRINT",FACE,{"disambiguationData":[TD([[makeQuery(id+"F25.imprint","IMPRINT",EDGE,{"disambiguationData":[TD([[subQ2,1.0]])],"derivedFrom":subQ1}),-1.0]])]});}
            var Q96;
            {var subQ0=sQuery(id+"F25.wireOp",EDGE,"E525.trimOffspring");var subQ1=sQuery(id+"F25.wireOp",EDGE,"E279.trimOffspring");var subQ2=makeQuery(id+"F25.imprint","INTERSECT",VERTEX,{"derivedFrom":[subQ1,subQ0]});Q96=makeQuery(id+"F25.imprint","IMPRINT",FACE,{"disambiguationData":[TD([[makeQuery(id+"F25.imprint","IMPRINT",EDGE,{"disambiguationData":[TD([[subQ2,1.0]])],"derivedFrom":subQ1}),1.0]])]});}
            var Q97;
            {var subQ0=sQuery(id+"F25.wireOp",EDGE,"E522.trimOffspring");var subQ1=sQuery(id+"F25.wireOp",EDGE,"E280.trimOffspring");var subQ2=makeQuery(id+"F25.imprint","INTERSECT",VERTEX,{"derivedFrom":[subQ1,subQ0]});Q97=makeQuery(id+"F25.imprint","IMPRINT",FACE,{"disambiguationData":[TD([[makeQuery(id+"F25.imprint","IMPRINT",EDGE,{"disambiguationData":[TD([[subQ2,-1.0]])],"derivedFrom":subQ1}),-1.0]])]});}
            var Q98;
            {var subQ0=sQuery(id+"F25.wireOp",EDGE,"E510.trimOffspring");var subQ1=sQuery(id+"F25.wireOp",EDGE,"E280.trimOffspring");var subQ2=makeQuery(id+"F25.imprint","INTERSECT",VERTEX,{"derivedFrom":[subQ1,subQ0]});Q98=makeQuery(id+"F25.imprint","IMPRINT",FACE,{"disambiguationData":[TD([[makeQuery(id+"F25.imprint","IMPRINT",EDGE,{"disambiguationData":[TD([[subQ2,-1.0]])],"derivedFrom":subQ1}),-1.0]])]});}
            var Q99;
            {var subQ0=sQuery(id+"F25.wireOp",EDGE,"E510.trimOffspring");var subQ1=sQuery(id+"F25.wireOp",EDGE,"E279.trimOffspring");var subQ2=makeQuery(id+"F25.imprint","INTERSECT",VERTEX,{"derivedFrom":[subQ1,subQ0]});Q99=makeQuery(id+"F25.imprint","IMPRINT",FACE,{"disambiguationData":[TD([[makeQuery(id+"F25.imprint","IMPRINT",EDGE,{"disambiguationData":[TD([[subQ2,-1.0]])],"derivedFrom":subQ1}),1.0]])]});}
            var Q100;
            {var subQ0=sQuery(id+"F25.wireOp",EDGE,"E517.trimOffspring");var subQ1=sQuery(id+"F25.wireOp",EDGE,"E280.trimOffspring");var subQ2=makeQuery(id+"F25.imprint","INTERSECT",VERTEX,{"derivedFrom":[subQ1,subQ0]});Q100=makeQuery(id+"F25.imprint","IMPRINT",FACE,{"disambiguationData":[TD([[makeQuery(id+"F25.imprint","IMPRINT",EDGE,{"disambiguationData":[TD([[subQ2,-1.0]])],"derivedFrom":subQ1}),-1.0]])]});}
            var Q101;
            {var subQ0=sQuery(id+"F25.wireOp",EDGE,"E517.trimOffspring");var subQ1=sQuery(id+"F25.wireOp",EDGE,"E279.trimOffspring");var subQ2=makeQuery(id+"F25.imprint","INTERSECT",VERTEX,{"derivedFrom":[subQ1,subQ0]});Q101=makeQuery(id+"F25.imprint","IMPRINT",FACE,{"disambiguationData":[TD([[makeQuery(id+"F25.imprint","IMPRINT",EDGE,{"disambiguationData":[TD([[subQ2,-1.0]])],"derivedFrom":subQ1}),1.0]])]});}
            var Q102;
            {var subQ0=sQuery(id+"F25.wireOp",EDGE,"E519.trimOffspring");var subQ1=sQuery(id+"F25.wireOp",EDGE,"E279.trimOffspring");var subQ2=makeQuery(id+"F25.imprint","INTERSECT",VERTEX,{"derivedFrom":[subQ1,subQ0]});Q102=makeQuery(id+"F25.imprint","IMPRINT",FACE,{"disambiguationData":[TD([[makeQuery(id+"F25.imprint","IMPRINT",EDGE,{"disambiguationData":[TD([[subQ2,-1.0]])],"derivedFrom":subQ1}),1.0]])]});}
            var Q103;
            {var subQ0=sQuery(id+"F25.wireOp",EDGE,"E519.trimOffspring");var subQ1=sQuery(id+"F25.wireOp",EDGE,"E280.trimOffspring");var subQ2=makeQuery(id+"F25.imprint","INTERSECT",VERTEX,{"derivedFrom":[subQ1,subQ0]});Q103=makeQuery(id+"F25.imprint","IMPRINT",FACE,{"disambiguationData":[TD([[makeQuery(id+"F25.imprint","IMPRINT",EDGE,{"disambiguationData":[TD([[subQ2,-1.0]])],"derivedFrom":subQ1}),-1.0]])]});}
            var Q104;
            {var subQ0=sQuery(id+"F25.wireOp",EDGE,"E518.trimOffspring");var subQ1=sQuery(id+"F25.wireOp",EDGE,"E280.trimOffspring");var subQ2=makeQuery(id+"F25.imprint","INTERSECT",VERTEX,{"derivedFrom":[subQ1,subQ0]});Q104=makeQuery(id+"F25.imprint","IMPRINT",FACE,{"disambiguationData":[TD([[makeQuery(id+"F25.imprint","IMPRINT",EDGE,{"disambiguationData":[TD([[subQ2,-1.0]])],"derivedFrom":subQ1}),-1.0]])]});}
            var Q105;
            {var subQ0=sQuery(id+"F25.wireOp",EDGE,"E518.trimOffspring");var subQ1=sQuery(id+"F25.wireOp",EDGE,"E279.trimOffspring");var subQ2=makeQuery(id+"F25.imprint","INTERSECT",VERTEX,{"derivedFrom":[subQ1,subQ0]});Q105=makeQuery(id+"F25.imprint","IMPRINT",FACE,{"disambiguationData":[TD([[makeQuery(id+"F25.imprint","IMPRINT",EDGE,{"disambiguationData":[TD([[subQ2,-1.0]])],"derivedFrom":subQ1}),1.0]])]});}
            var Q106;
            {var subQ0=sQuery(id+"F25.wireOp",EDGE,"E507.trimOffspring");var subQ1=sQuery(id+"F25.wireOp",EDGE,"E280.trimOffspring");var subQ2=makeQuery(id+"F25.imprint","INTERSECT",VERTEX,{"derivedFrom":[subQ1,subQ0]});Q106=makeQuery(id+"F25.imprint","IMPRINT",FACE,{"disambiguationData":[TD([[makeQuery(id+"F25.imprint","IMPRINT",EDGE,{"disambiguationData":[TD([[subQ2,-1.0]])],"derivedFrom":subQ1}),-1.0]])]});}
            var Q107;
            {var subQ0=sQuery(id+"F25.wireOp",EDGE,"E507.trimOffspring");var subQ1=sQuery(id+"F25.wireOp",EDGE,"E279.trimOffspring");var subQ2=makeQuery(id+"F25.imprint","INTERSECT",VERTEX,{"derivedFrom":[subQ1,subQ0]});Q107=makeQuery(id+"F25.imprint","IMPRINT",FACE,{"disambiguationData":[TD([[makeQuery(id+"F25.imprint","IMPRINT",EDGE,{"disambiguationData":[TD([[subQ2,-1.0]])],"derivedFrom":subQ1}),1.0]])]});}
            var Q108;
            {var subQ0=sQuery(id+"F25.wireOp",EDGE,"E512.trimOffspring");var subQ1=sQuery(id+"F25.wireOp",EDGE,"E280.trimOffspring");var subQ2=makeQuery(id+"F25.imprint","INTERSECT",VERTEX,{"derivedFrom":[subQ1,subQ0]});Q108=makeQuery(id+"F25.imprint","IMPRINT",FACE,{"disambiguationData":[TD([[makeQuery(id+"F25.imprint","IMPRINT",EDGE,{"disambiguationData":[TD([[subQ2,-1.0]])],"derivedFrom":subQ1}),-1.0]])]});}
            var Q109;
            {var subQ0=sQuery(id+"F25.wireOp",EDGE,"E512.trimOffspring");var subQ1=sQuery(id+"F25.wireOp",EDGE,"E279.trimOffspring");var subQ2=makeQuery(id+"F25.imprint","INTERSECT",VERTEX,{"derivedFrom":[subQ1,subQ0]});Q109=makeQuery(id+"F25.imprint","IMPRINT",FACE,{"disambiguationData":[TD([[makeQuery(id+"F25.imprint","IMPRINT",EDGE,{"disambiguationData":[TD([[subQ2,-1.0]])],"derivedFrom":subQ1}),1.0]])]});}
            var Q110;
            {var subQ0=sQuery(id+"F25.wireOp",EDGE,"E522.trimOffspring");var subQ1=sQuery(id+"F25.wireOp",EDGE,"E279.trimOffspring");var subQ2=makeQuery(id+"F25.imprint","INTERSECT",VERTEX,{"derivedFrom":[subQ1,subQ0]});Q110=makeQuery(id+"F25.imprint","IMPRINT",FACE,{"disambiguationData":[TD([[makeQuery(id+"F25.imprint","IMPRINT",EDGE,{"disambiguationData":[TD([[subQ2,-1.0]])],"derivedFrom":subQ1}),1.0]])]});}
            var Q111;
            {var subQ0=sQuery(id+"F25.wireOp",EDGE,"E522.trimOffspring");var subQ1=sQuery(id+"F25.wireOp",EDGE,"E279.trimOffspring");var subQ2=makeQuery(id+"F25.imprint","INTERSECT",VERTEX,{"derivedFrom":[subQ1,subQ0]});Q111=makeQuery(id+"F25.imprint","IMPRINT",FACE,{"disambiguationData":[TD([[makeQuery(id+"F25.imprint","IMPRINT",EDGE,{"disambiguationData":[TD([[subQ2,-1.0]])],"derivedFrom":subQ1}),-1.0]])]});}
            var Q112;
            {var subQ0=sQuery(id+"F25.wireOp",EDGE,"E525.trimOffspring");var subQ1=sQuery(id+"F25.wireOp",EDGE,"E279.trimOffspring");var subQ2=makeQuery(id+"F25.imprint","INTERSECT",VERTEX,{"derivedFrom":[subQ1,subQ0]});Q112=makeQuery(id+"F25.imprint","IMPRINT",FACE,{"disambiguationData":[TD([[makeQuery(id+"F25.imprint","IMPRINT",EDGE,{"disambiguationData":[TD([[subQ2,1.0]])],"derivedFrom":subQ1}),-1.0]])]});}
            var Q113;
            {var subQ0=sQuery(id+"F25.wireOp",EDGE,"E525.trimOffspring");var subQ1=sQuery(id+"F25.wireOp",EDGE,"E287.trimOffspring");var subQ2=makeQuery(id+"F25.imprint","INTERSECT",VERTEX,{"derivedFrom":[subQ1,subQ0]});Q113=makeQuery(id+"F25.imprint","IMPRINT",FACE,{"disambiguationData":[TD([[makeQuery(id+"F25.imprint","IMPRINT",EDGE,{"disambiguationData":[TD([[subQ2,1.0]])],"derivedFrom":subQ1}),-1.0]])]});}
            var Q114;
            {var subQ0=sQuery(id+"F25.wireOp",EDGE,"E525.trimOffspring");var subQ1=sQuery(id+"F25.wireOp",EDGE,"E291.trimOffspring");var subQ2=makeQuery(id+"F25.imprint","INTERSECT",VERTEX,{"derivedFrom":[subQ1,subQ0]});Q114=makeQuery(id+"F25.imprint","IMPRINT",FACE,{"disambiguationData":[TD([[makeQuery(id+"F25.imprint","IMPRINT",EDGE,{"disambiguationData":[TD([[subQ2,1.0]])],"derivedFrom":subQ1}),1.0]])]});}
            var Q115;
            {var subQ0=sQuery(id+"F25.wireOp",EDGE,"E522.trimOffspring");var subQ1=sQuery(id+"F25.wireOp",EDGE,"E287.trimOffspring");var subQ2=makeQuery(id+"F25.imprint","INTERSECT",VERTEX,{"derivedFrom":[subQ1,subQ0]});Q115=makeQuery(id+"F25.imprint","IMPRINT",FACE,{"disambiguationData":[TD([[makeQuery(id+"F25.imprint","IMPRINT",EDGE,{"disambiguationData":[TD([[subQ2,-1.0]])],"derivedFrom":subQ1}),-1.0]])]});}
            var Q116;
            {var subQ0=sQuery(id+"F25.wireOp",EDGE,"E522.trimOffspring");var subQ1=sQuery(id+"F25.wireOp",EDGE,"E291.trimOffspring");var subQ2=makeQuery(id+"F25.imprint","INTERSECT",VERTEX,{"derivedFrom":[subQ1,subQ0]});Q116=makeQuery(id+"F25.imprint","IMPRINT",FACE,{"disambiguationData":[TD([[makeQuery(id+"F25.imprint","IMPRINT",EDGE,{"disambiguationData":[TD([[subQ2,-1.0]])],"derivedFrom":subQ1}),1.0]])]});}
            var Q117;
            {var subQ0=sQuery(id+"F25.wireOp",EDGE,"E510.trimOffspring");var subQ1=sQuery(id+"F25.wireOp",EDGE,"E287.trimOffspring");var subQ2=makeQuery(id+"F25.imprint","INTERSECT",VERTEX,{"derivedFrom":[subQ1,subQ0]});Q117=makeQuery(id+"F25.imprint","IMPRINT",FACE,{"disambiguationData":[TD([[makeQuery(id+"F25.imprint","IMPRINT",EDGE,{"disambiguationData":[TD([[subQ2,-1.0]])],"derivedFrom":subQ1}),-1.0]])]});}
            var Q118;
            {var subQ0=sQuery(id+"F25.wireOp",EDGE,"E510.trimOffspring");var subQ1=sQuery(id+"F25.wireOp",EDGE,"E291.trimOffspring");var subQ2=makeQuery(id+"F25.imprint","INTERSECT",VERTEX,{"derivedFrom":[subQ1,subQ0]});Q118=makeQuery(id+"F25.imprint","IMPRINT",FACE,{"disambiguationData":[TD([[makeQuery(id+"F25.imprint","IMPRINT",EDGE,{"disambiguationData":[TD([[subQ2,-1.0]])],"derivedFrom":subQ1}),1.0]])]});}
            var Q119;
            {var subQ0=sQuery(id+"F25.wireOp",EDGE,"E512.trimOffspring");var subQ1=sQuery(id+"F25.wireOp",EDGE,"E287.trimOffspring");var subQ2=makeQuery(id+"F25.imprint","INTERSECT",VERTEX,{"derivedFrom":[subQ1,subQ0]});Q119=makeQuery(id+"F25.imprint","IMPRINT",FACE,{"disambiguationData":[TD([[makeQuery(id+"F25.imprint","IMPRINT",EDGE,{"disambiguationData":[TD([[subQ2,-1.0]])],"derivedFrom":subQ1}),-1.0]])]});}
            var Q120;
            {var subQ0=sQuery(id+"F25.wireOp",EDGE,"E512.trimOffspring");var subQ1=sQuery(id+"F25.wireOp",EDGE,"E291.trimOffspring");var subQ2=makeQuery(id+"F25.imprint","INTERSECT",VERTEX,{"derivedFrom":[subQ1,subQ0]});Q120=makeQuery(id+"F25.imprint","IMPRINT",FACE,{"disambiguationData":[TD([[makeQuery(id+"F25.imprint","IMPRINT",EDGE,{"disambiguationData":[TD([[subQ2,-1.0]])],"derivedFrom":subQ1}),1.0]])]});}
            var Q121;
            {var subQ0=sQuery(id+"F25.wireOp",EDGE,"E507.trimOffspring");var subQ1=sQuery(id+"F25.wireOp",EDGE,"E291.trimOffspring");var subQ2=makeQuery(id+"F25.imprint","INTERSECT",VERTEX,{"derivedFrom":[subQ1,subQ0]});Q121=makeQuery(id+"F25.imprint","IMPRINT",FACE,{"disambiguationData":[TD([[makeQuery(id+"F25.imprint","IMPRINT",EDGE,{"disambiguationData":[TD([[subQ2,-1.0]])],"derivedFrom":subQ1}),1.0]])]});}
            var Q122;
            {var subQ0=sQuery(id+"F25.wireOp",EDGE,"E507.trimOffspring");var subQ1=sQuery(id+"F25.wireOp",EDGE,"E287.trimOffspring");var subQ2=makeQuery(id+"F25.imprint","INTERSECT",VERTEX,{"derivedFrom":[subQ1,subQ0]});Q122=makeQuery(id+"F25.imprint","IMPRINT",FACE,{"disambiguationData":[TD([[makeQuery(id+"F25.imprint","IMPRINT",EDGE,{"disambiguationData":[TD([[subQ2,-1.0]])],"derivedFrom":subQ1}),-1.0]])]});}
            var Q123;
            {var subQ0=sQuery(id+"F25.wireOp",EDGE,"E518.trimOffspring");var subQ1=sQuery(id+"F25.wireOp",EDGE,"E287.trimOffspring");var subQ2=makeQuery(id+"F25.imprint","INTERSECT",VERTEX,{"derivedFrom":[subQ1,subQ0]});Q123=makeQuery(id+"F25.imprint","IMPRINT",FACE,{"disambiguationData":[TD([[makeQuery(id+"F25.imprint","IMPRINT",EDGE,{"disambiguationData":[TD([[subQ2,-1.0]])],"derivedFrom":subQ1}),-1.0]])]});}
            var Q124;
            {var subQ0=sQuery(id+"F25.wireOp",EDGE,"E518.trimOffspring");var subQ1=sQuery(id+"F25.wireOp",EDGE,"E291.trimOffspring");var subQ2=makeQuery(id+"F25.imprint","INTERSECT",VERTEX,{"derivedFrom":[subQ1,subQ0]});Q124=makeQuery(id+"F25.imprint","IMPRINT",FACE,{"disambiguationData":[TD([[makeQuery(id+"F25.imprint","IMPRINT",EDGE,{"disambiguationData":[TD([[subQ2,-1.0]])],"derivedFrom":subQ1}),1.0]])]});}
            var Q125;
            {var subQ0=sQuery(id+"F25.wireOp",EDGE,"E519.trimOffspring");var subQ1=sQuery(id+"F25.wireOp",EDGE,"E287.trimOffspring");var subQ2=makeQuery(id+"F25.imprint","INTERSECT",VERTEX,{"derivedFrom":[subQ1,subQ0]});Q125=makeQuery(id+"F25.imprint","IMPRINT",FACE,{"disambiguationData":[TD([[makeQuery(id+"F25.imprint","IMPRINT",EDGE,{"disambiguationData":[TD([[subQ2,-1.0]])],"derivedFrom":subQ1}),-1.0]])]});}
            var Q126;
            {var subQ0=sQuery(id+"F25.wireOp",EDGE,"E517.trimOffspring");var subQ1=sQuery(id+"F25.wireOp",EDGE,"E287.trimOffspring");var subQ2=makeQuery(id+"F25.imprint","INTERSECT",VERTEX,{"derivedFrom":[subQ1,subQ0]});Q126=makeQuery(id+"F25.imprint","IMPRINT",FACE,{"disambiguationData":[TD([[makeQuery(id+"F25.imprint","IMPRINT",EDGE,{"disambiguationData":[TD([[subQ2,-1.0]])],"derivedFrom":subQ1}),-1.0]])]});}
            var Q127;
            {var subQ0=sQuery(id+"F25.wireOp",EDGE,"E517.trimOffspring");var subQ1=sQuery(id+"F25.wireOp",EDGE,"E291.trimOffspring");var subQ2=makeQuery(id+"F25.imprint","INTERSECT",VERTEX,{"derivedFrom":[subQ1,subQ0]});Q127=makeQuery(id+"F25.imprint","IMPRINT",FACE,{"disambiguationData":[TD([[makeQuery(id+"F25.imprint","IMPRINT",EDGE,{"disambiguationData":[TD([[subQ2,-1.0]])],"derivedFrom":subQ1}),1.0]])]});}
            var Q128;
            {var subQ0=sQuery(id+"F25.wireOp",EDGE,"E519.trimOffspring");var subQ1=sQuery(id+"F25.wireOp",EDGE,"E291.trimOffspring");var subQ2=makeQuery(id+"F25.imprint","INTERSECT",VERTEX,{"derivedFrom":[subQ1,subQ0]});Q128=makeQuery(id+"F25.imprint","IMPRINT",FACE,{"disambiguationData":[TD([[makeQuery(id+"F25.imprint","IMPRINT",EDGE,{"disambiguationData":[TD([[subQ2,-1.0]])],"derivedFrom":subQ1}),1.0]])]});}
            var Q129;
            {var subQ0=sQuery(id+"F25.wireOp",EDGE,"E517.trimOffspring");var subQ1=sQuery(id+"F25.wireOp",EDGE,"E251.right");var subQ2=makeQuery(id+"F25.imprint","INTERSECT",VERTEX,{"derivedFrom":[subQ1,subQ0]});Q129=makeQuery(id+"F25.imprint","IMPRINT",FACE,{"disambiguationData":[TD([[makeQuery(id+"F25.imprint","IMPRINT",EDGE,{"disambiguationData":[TD([[subQ2,-1.0]])],"derivedFrom":subQ1}),1.0]])]});}
            var Q130;
            {var subQ0=sQuery(id+"F25.wireOp",EDGE,"E519.trimOffspring");var subQ1=sQuery(id+"F25.wireOp",EDGE,"E251.right");var subQ2=makeQuery(id+"F25.imprint","INTERSECT",VERTEX,{"derivedFrom":[subQ1,subQ0]});Q130=makeQuery(id+"F25.imprint","IMPRINT",FACE,{"disambiguationData":[TD([[makeQuery(id+"F25.imprint","IMPRINT",EDGE,{"disambiguationData":[TD([[subQ2,-1.0]])],"derivedFrom":subQ1}),1.0]])]});}
            var Q131;
            {var subQ0=sQuery(id+"F25.wireOp",EDGE,"E519.trimOffspring");var subQ1=sQuery(id+"F25.wireOp",EDGE,"E250.left");var subQ2=makeQuery(id+"F25.imprint","INTERSECT",VERTEX,{"derivedFrom":[subQ1,subQ0]});Q131=makeQuery(id+"F25.imprint","IMPRINT",FACE,{"disambiguationData":[TD([[makeQuery(id+"F25.imprint","IMPRINT",EDGE,{"disambiguationData":[TD([[subQ2,-1.0]])],"derivedFrom":subQ1}),1.0]])]});}
            var Q132;
            {var subQ0=sQuery(id+"F25.wireOp",EDGE,"E517.trimOffspring");var subQ1=sQuery(id+"F25.wireOp",EDGE,"E250.left");var subQ2=makeQuery(id+"F25.imprint","INTERSECT",VERTEX,{"derivedFrom":[subQ1,subQ0]});Q132=makeQuery(id+"F25.imprint","IMPRINT",FACE,{"disambiguationData":[TD([[makeQuery(id+"F25.imprint","IMPRINT",EDGE,{"disambiguationData":[TD([[subQ2,-1.0]])],"derivedFrom":subQ1}),1.0]])]});}
            var Q133;
            {var subQ0=sQuery(id+"F25.wireOp",EDGE,"E517.trimOffspring");var subQ1=sQuery(id+"F25.wireOp",EDGE,"E250.right");var subQ2=makeQuery(id+"F25.imprint","INTERSECT",VERTEX,{"derivedFrom":[subQ1,subQ0]});Q133=makeQuery(id+"F25.imprint","IMPRINT",FACE,{"disambiguationData":[TD([[makeQuery(id+"F25.imprint","IMPRINT",EDGE,{"disambiguationData":[TD([[subQ2,-1.0]])],"derivedFrom":subQ1}),1.0]])]});}
            var Q134;
            {var subQ0=sQuery(id+"F25.wireOp",EDGE,"E519.trimOffspring");var subQ1=sQuery(id+"F25.wireOp",EDGE,"E250.right");var subQ2=makeQuery(id+"F25.imprint","INTERSECT",VERTEX,{"derivedFrom":[subQ1,subQ0]});Q134=makeQuery(id+"F25.imprint","IMPRINT",FACE,{"disambiguationData":[TD([[makeQuery(id+"F25.imprint","IMPRINT",EDGE,{"disambiguationData":[TD([[subQ2,-1.0]])],"derivedFrom":subQ1}),1.0]])]});}
            var Q135;
            {var subQ0=sQuery(id+"F25.wireOp",EDGE,"E518.trimOffspring");var subQ1=sQuery(id+"F25.wireOp",EDGE,"E250.right");var subQ2=makeQuery(id+"F25.imprint","INTERSECT",VERTEX,{"derivedFrom":[subQ1,subQ0]});Q135=makeQuery(id+"F25.imprint","IMPRINT",FACE,{"disambiguationData":[TD([[makeQuery(id+"F25.imprint","IMPRINT",EDGE,{"disambiguationData":[TD([[subQ2,-1.0]])],"derivedFrom":subQ1}),1.0]])]});}
            var Q136;
            {var subQ0=sQuery(id+"F25.wireOp",EDGE,"E518.trimOffspring");var subQ1=sQuery(id+"F25.wireOp",EDGE,"E250.left");var subQ2=makeQuery(id+"F25.imprint","INTERSECT",VERTEX,{"derivedFrom":[subQ1,subQ0]});Q136=makeQuery(id+"F25.imprint","IMPRINT",FACE,{"disambiguationData":[TD([[makeQuery(id+"F25.imprint","IMPRINT",EDGE,{"disambiguationData":[TD([[subQ2,-1.0]])],"derivedFrom":subQ1}),1.0]])]});}
            var Q137;
            {var subQ0=sQuery(id+"F25.wireOp",EDGE,"E507.trimOffspring");var subQ1=sQuery(id+"F25.wireOp",EDGE,"E250.left");var subQ2=makeQuery(id+"F25.imprint","INTERSECT",VERTEX,{"derivedFrom":[subQ1,subQ0]});Q137=makeQuery(id+"F25.imprint","IMPRINT",FACE,{"disambiguationData":[TD([[makeQuery(id+"F25.imprint","IMPRINT",EDGE,{"disambiguationData":[TD([[subQ2,-1.0]])],"derivedFrom":subQ1}),1.0]])]});}
            var Q138;
            {var subQ0=sQuery(id+"F25.wireOp",EDGE,"E507.trimOffspring");var subQ1=sQuery(id+"F25.wireOp",EDGE,"E250.right");var subQ2=makeQuery(id+"F25.imprint","INTERSECT",VERTEX,{"derivedFrom":[subQ1,subQ0]});Q138=makeQuery(id+"F25.imprint","IMPRINT",FACE,{"disambiguationData":[TD([[makeQuery(id+"F25.imprint","IMPRINT",EDGE,{"disambiguationData":[TD([[subQ2,-1.0]])],"derivedFrom":subQ1}),1.0]])]});}
            var Q139;
            {var subQ0=sQuery(id+"F25.wireOp",EDGE,"E512.trimOffspring");var subQ1=sQuery(id+"F25.wireOp",EDGE,"E250.left");var subQ2=makeQuery(id+"F25.imprint","INTERSECT",VERTEX,{"derivedFrom":[subQ1,subQ0]});Q139=makeQuery(id+"F25.imprint","IMPRINT",FACE,{"disambiguationData":[TD([[makeQuery(id+"F25.imprint","IMPRINT",EDGE,{"disambiguationData":[TD([[subQ2,-1.0]])],"derivedFrom":subQ1}),1.0]])]});}
            var Q140;
            {var subQ0=sQuery(id+"F25.wireOp",EDGE,"E512.trimOffspring");var subQ1=sQuery(id+"F25.wireOp",EDGE,"E250.right");var subQ2=makeQuery(id+"F25.imprint","INTERSECT",VERTEX,{"derivedFrom":[subQ1,subQ0]});Q140=makeQuery(id+"F25.imprint","IMPRINT",FACE,{"disambiguationData":[TD([[makeQuery(id+"F25.imprint","IMPRINT",EDGE,{"disambiguationData":[TD([[subQ2,-1.0]])],"derivedFrom":subQ1}),1.0]])]});}
            var Q141;
            {var subQ0=sQuery(id+"F25.wireOp",EDGE,"E512.trimOffspring");var subQ1=sQuery(id+"F25.wireOp",EDGE,"E249.right");var subQ2=makeQuery(id+"F25.imprint","INTERSECT",VERTEX,{"derivedFrom":[subQ1,subQ0]});Q141=makeQuery(id+"F25.imprint","IMPRINT",FACE,{"disambiguationData":[TD([[makeQuery(id+"F25.imprint","IMPRINT",EDGE,{"disambiguationData":[TD([[subQ2,-1.0]])],"derivedFrom":subQ1}),1.0]])]});}
            var Q142;
            {var subQ0=sQuery(id+"F25.wireOp",EDGE,"E507.trimOffspring");var subQ1=sQuery(id+"F25.wireOp",EDGE,"E249.right");var subQ2=makeQuery(id+"F25.imprint","INTERSECT",VERTEX,{"derivedFrom":[subQ1,subQ0]});Q142=makeQuery(id+"F25.imprint","IMPRINT",FACE,{"disambiguationData":[TD([[makeQuery(id+"F25.imprint","IMPRINT",EDGE,{"disambiguationData":[TD([[subQ2,-1.0]])],"derivedFrom":subQ1}),1.0]])]});}
            var Q143;
            {var subQ5=sQuery(id+"F25.wireOp",EDGE,"E253.right");Q143=makeQuery(id+"F25.imprint","IMPRINT",FACE,{"disambiguationData":[TD([[makeQuery(id+"F25.imprint","IMPRINT",EDGE,{"derivedFrom":subQ5}),1.0]])]});}
            var Q144;
            {var subQ5=sQuery(id+"F25.wireOp",EDGE,"E252.right");Q144=makeQuery(id+"F25.imprint","IMPRINT",FACE,{"disambiguationData":[TD([[makeQuery(id+"F25.imprint","IMPRINT",EDGE,{"derivedFrom":subQ5}),-1.0]])]});}
            var Q145;
            {var subQ0=sQuery(id+"F25.wireOp",EDGE,"E253.right");Q145=makeQuery(id+"F25.imprint","IMPRINT",FACE,{"disambiguationData":[TD([[makeQuery(id+"F25.imprint","IMPRINT",EDGE,{"derivedFrom":subQ0}),-1.0]])]});}
            var Q146;
            {var subQ0=sQuery(id+"F25.wireOp",EDGE,"E252.right");Q146=makeQuery(id+"F25.imprint","IMPRINT",FACE,{"disambiguationData":[TD([[makeQuery(id+"F25.imprint","IMPRINT",EDGE,{"derivedFrom":subQ0}),1.0]])]});}
            var Q147;
            {var subQ0=sQuery(id+"F25.wireOp",EDGE,"E518.trimOffspring");var subQ5=sQuery(id+"F25.wireOp",EDGE,"E249.right");var subQ7=makeQuery(id+"F25.imprint","INTERSECT",VERTEX,{"derivedFrom":[subQ5,subQ0]});Q147=makeQuery(id+"F25.imprint","IMPRINT",FACE,{"disambiguationData":[TD([[makeQuery(id+"F25.imprint","IMPRINT",EDGE,{"disambiguationData":[TD([[subQ7,-1.0]])],"derivedFrom":subQ5}),-1.0]])]});}
            var Q148;
            {var subQ0=sQuery(id+"F25.wireOp",EDGE,"E373.MirrorCS");var subQ5=sQuery(id+"F25.wireOp",EDGE,"E387.MirrorCS");var subQ6=makeQuery(id+"F25.imprint","INTERSECT",VERTEX,{"derivedFrom":[subQ0,subQ5]});Q148=makeQuery(id+"F25.imprint","IMPRINT",FACE,{"disambiguationData":[TD([[makeQuery(id+"F25.imprint","IMPRINT",EDGE,{"disambiguationData":[TD([[subQ6,-1.0]])],"derivedFrom":subQ5}),1.0]])]});}
            var Q149;
            {var subQ5=sQuery(id+"F25.wireOp",EDGE,"E236.right");Q149=makeQuery(id+"F25.imprint","IMPRINT",FACE,{"disambiguationData":[TD([[makeQuery(id+"F25.imprint","IMPRINT",EDGE,{"derivedFrom":subQ5}),-1.0]])]});}
            var Q150;
            {var subQ5=sQuery(id+"F25.wireOp",EDGE,"E235.right");Q150=makeQuery(id+"F25.imprint","IMPRINT",FACE,{"disambiguationData":[TD([[makeQuery(id+"F25.imprint","IMPRINT",EDGE,{"derivedFrom":subQ5}),1.0]])]});}
            var Q151;
            {var subQ0=sQuery(id+"F25.wireOp",EDGE,"E365.MirrorCS");var subQ1=sQuery(id+"F25.wireOp",EDGE,"E344.MirrorCS");var subQ2=makeQuery(id+"F25.imprint","INTERSECT",VERTEX,{"derivedFrom":[subQ1,subQ0]});Q151=makeQuery(id+"F25.imprint","IMPRINT",FACE,{"disambiguationData":[TD([[makeQuery(id+"F25.imprint","IMPRINT",EDGE,{"disambiguationData":[TD([[subQ2,-1.0]])],"derivedFrom":subQ1}),-1.0]])]});}
            var Q152;
            {var subQ0=sQuery(id+"F25.wireOp",EDGE,"E334.MirrorCS");var subQ1=sQuery(id+"F25.wireOp",EDGE,"E344.MirrorCS");var subQ2=makeQuery(id+"F25.imprint","INTERSECT",VERTEX,{"derivedFrom":[subQ1,subQ0]});Q152=makeQuery(id+"F25.imprint","IMPRINT",FACE,{"disambiguationData":[TD([[makeQuery(id+"F25.imprint","IMPRINT",EDGE,{"disambiguationData":[TD([[subQ2,-1.0]])],"derivedFrom":subQ1}),1.0]])]});}
            var Q153;
            {var subQ0=sQuery(id+"F25.wireOp",EDGE,"E334.MirrorCS");var subQ1=sQuery(id+"F25.wireOp",EDGE,"E344.MirrorCS");var subQ2=makeQuery(id+"F25.imprint","INTERSECT",VERTEX,{"derivedFrom":[subQ1,subQ0]});Q153=makeQuery(id+"F25.imprint","IMPRINT",FACE,{"disambiguationData":[TD([[makeQuery(id+"F25.imprint","IMPRINT",EDGE,{"disambiguationData":[TD([[subQ2,-1.0]])],"derivedFrom":subQ1}),-1.0]])]});}
            var Q154;
            {var subQ0=sQuery(id+"F25.wireOp",EDGE,"E386.MirrorCS");var subQ1=sQuery(id+"F25.wireOp",EDGE,"E344.MirrorCS");var subQ2=makeQuery(id+"F25.imprint","INTERSECT",VERTEX,{"derivedFrom":[subQ1,subQ0]});Q154=makeQuery(id+"F25.imprint","IMPRINT",FACE,{"disambiguationData":[TD([[makeQuery(id+"F25.imprint","IMPRINT",EDGE,{"disambiguationData":[TD([[subQ2,-1.0]])],"derivedFrom":subQ1}),-1.0]])]});}
            var Q155;
            {var subQ0=sQuery(id+"F25.wireOp",EDGE,"E386.MirrorCS");var subQ1=sQuery(id+"F25.wireOp",EDGE,"E344.MirrorCS");var subQ2=makeQuery(id+"F25.imprint","INTERSECT",VERTEX,{"derivedFrom":[subQ1,subQ0]});Q155=makeQuery(id+"F25.imprint","IMPRINT",FACE,{"disambiguationData":[TD([[makeQuery(id+"F25.imprint","IMPRINT",EDGE,{"disambiguationData":[TD([[subQ2,-1.0]])],"derivedFrom":subQ1}),1.0]])]});}
            var Q156;
            {var subQ0=sQuery(id+"F25.wireOp",EDGE,"E398.MirrorCS");var subQ1=sQuery(id+"F25.wireOp",EDGE,"E334.MirrorCS");var subQ2=makeQuery(id+"F25.imprint","INTERSECT",VERTEX,{"derivedFrom":[subQ1,subQ0]});Q156=makeQuery(id+"F25.imprint","IMPRINT",FACE,{"disambiguationData":[TD([[makeQuery(id+"F25.imprint","IMPRINT",EDGE,{"disambiguationData":[TD([[subQ2,-1.0]])],"derivedFrom":subQ1}),-1.0]])]});}
            var Q157;
            {var subQ0=sQuery(id+"F25.wireOp",EDGE,"E398.MirrorCS");var subQ1=sQuery(id+"F25.wireOp",EDGE,"E365.MirrorCS");var subQ2=makeQuery(id+"F25.imprint","INTERSECT",VERTEX,{"derivedFrom":[subQ1,subQ0]});Q157=makeQuery(id+"F25.imprint","IMPRINT",FACE,{"disambiguationData":[TD([[makeQuery(id+"F25.imprint","IMPRINT",EDGE,{"disambiguationData":[TD([[subQ2,-1.0]])],"derivedFrom":subQ1}),-1.0]])]});}
            var Q158;
            {var subQ0=sQuery(id+"F25.wireOp",EDGE,"E366.MirrorCS");var subQ1=sQuery(id+"F25.wireOp",EDGE,"E334.MirrorCS");var subQ2=makeQuery(id+"F25.imprint","INTERSECT",VERTEX,{"derivedFrom":[subQ1,subQ0]});Q158=makeQuery(id+"F25.imprint","IMPRINT",FACE,{"disambiguationData":[TD([[makeQuery(id+"F25.imprint","IMPRINT",EDGE,{"disambiguationData":[TD([[subQ2,-1.0]])],"derivedFrom":subQ1}),-1.0]])]});}
            var Q159;
            {var subQ0=sQuery(id+"F25.wireOp",EDGE,"E366.MirrorCS");var subQ1=sQuery(id+"F25.wireOp",EDGE,"E365.MirrorCS");var subQ2=makeQuery(id+"F25.imprint","INTERSECT",VERTEX,{"derivedFrom":[subQ1,subQ0]});Q159=makeQuery(id+"F25.imprint","IMPRINT",FACE,{"disambiguationData":[TD([[makeQuery(id+"F25.imprint","IMPRINT",EDGE,{"disambiguationData":[TD([[subQ2,-1.0]])],"derivedFrom":subQ1}),-1.0]])]});}
            var Q160;
            {var subQ0=sQuery(id+"F25.wireOp",EDGE,"E366.MirrorCS");var subQ1=sQuery(id+"F25.wireOp",EDGE,"E365.MirrorCS");var subQ2=makeQuery(id+"F25.imprint","INTERSECT",VERTEX,{"derivedFrom":[subQ1,subQ0]});Q160=makeQuery(id+"F25.imprint","IMPRINT",FACE,{"disambiguationData":[TD([[makeQuery(id+"F25.imprint","IMPRINT",EDGE,{"disambiguationData":[TD([[subQ2,-1.0]])],"derivedFrom":subQ1}),1.0]])]});}
            var Q161;
            {var subQ0=sQuery(id+"F25.wireOp",EDGE,"E365.MirrorCS");var subQ1=sQuery(id+"F25.wireOp",EDGE,"E347.MirrorCS");var subQ2=makeQuery(id+"F25.imprint","INTERSECT",VERTEX,{"derivedFrom":[subQ1,subQ0]});Q161=makeQuery(id+"F25.imprint","IMPRINT",FACE,{"disambiguationData":[TD([[makeQuery(id+"F25.imprint","IMPRINT",EDGE,{"disambiguationData":[TD([[subQ2,-1.0]])],"derivedFrom":subQ1}),-1.0]])]});}
            var Q162;
            {var subQ0=sQuery(id+"F25.wireOp",EDGE,"E334.MirrorCS");var subQ1=sQuery(id+"F25.wireOp",EDGE,"E347.MirrorCS");var subQ2=makeQuery(id+"F25.imprint","INTERSECT",VERTEX,{"derivedFrom":[subQ1,subQ0]});Q162=makeQuery(id+"F25.imprint","IMPRINT",FACE,{"disambiguationData":[TD([[makeQuery(id+"F25.imprint","IMPRINT",EDGE,{"disambiguationData":[TD([[subQ2,-1.0]])],"derivedFrom":subQ1}),-1.0]])]});}
            var Q163;
            {var subQ0=sQuery(id+"F25.wireOp",EDGE,"E386.MirrorCS");var subQ1=sQuery(id+"F25.wireOp",EDGE,"E347.MirrorCS");var subQ2=makeQuery(id+"F25.imprint","INTERSECT",VERTEX,{"derivedFrom":[subQ1,subQ0]});Q163=makeQuery(id+"F25.imprint","IMPRINT",FACE,{"disambiguationData":[TD([[makeQuery(id+"F25.imprint","IMPRINT",EDGE,{"disambiguationData":[TD([[subQ2,-1.0]])],"derivedFrom":subQ1}),-1.0]])]});}
            var Q164;
            {var subQ0=sQuery(id+"F25.wireOp",EDGE,"E386.MirrorCS");var subQ1=sQuery(id+"F25.wireOp",EDGE,"E347.MirrorCS");var subQ2=makeQuery(id+"F25.imprint","INTERSECT",VERTEX,{"derivedFrom":[subQ1,subQ0]});Q164=makeQuery(id+"F25.imprint","IMPRINT",FACE,{"disambiguationData":[TD([[makeQuery(id+"F25.imprint","IMPRINT",EDGE,{"disambiguationData":[TD([[subQ2,-1.0]])],"derivedFrom":subQ1}),1.0]])]});}
            var Q165;
            {var subQ0=sQuery(id+"F25.wireOp",EDGE,"E334.MirrorCS");var subQ1=sQuery(id+"F25.wireOp",EDGE,"E347.MirrorCS");var subQ2=makeQuery(id+"F25.imprint","INTERSECT",VERTEX,{"derivedFrom":[subQ1,subQ0]});Q165=makeQuery(id+"F25.imprint","IMPRINT",FACE,{"disambiguationData":[TD([[makeQuery(id+"F25.imprint","IMPRINT",EDGE,{"disambiguationData":[TD([[subQ2,-1.0]])],"derivedFrom":subQ1}),1.0]])]});}
            var Q166;
            {var subQ0=sQuery(id+"F25.wireOp",EDGE,"E237.right");Q166=makeQuery(id+"F25.imprint","IMPRINT",FACE,{"disambiguationData":[TD([[makeQuery(id+"F25.imprint","IMPRINT",EDGE,{"derivedFrom":subQ0}),-1.0]])]});}
            var Q167;
            {var subQ0=sQuery(id+"F25.wireOp",EDGE,"E238.right");Q167=makeQuery(id+"F25.imprint","IMPRINT",FACE,{"disambiguationData":[TD([[makeQuery(id+"F25.imprint","IMPRINT",EDGE,{"derivedFrom":subQ0}),1.0]])]});}
            var Q168;
            {var subQ0=sQuery(id+"F25.wireOp",EDGE,"E236.right");Q168=makeQuery(id+"F25.imprint","IMPRINT",FACE,{"disambiguationData":[TD([[makeQuery(id+"F25.imprint","IMPRINT",EDGE,{"derivedFrom":subQ0}),1.0]])]});}
            var Q169;
            {var subQ0=sQuery(id+"F25.wireOp",EDGE,"E365.MirrorCS");var subQ1=sQuery(id+"F25.wireOp",EDGE,"E344.MirrorCS");var subQ2=makeQuery(id+"F25.imprint","INTERSECT",VERTEX,{"derivedFrom":[subQ1,subQ0]});Q169=makeQuery(id+"F25.imprint","IMPRINT",FACE,{"disambiguationData":[TD([[makeQuery(id+"F25.imprint","IMPRINT",EDGE,{"disambiguationData":[TD([[subQ2,-1.0]])],"derivedFrom":subQ1}),1.0]])]});}
            var Q170;
            {var subQ5=sQuery(id+"F25.wireOp",EDGE,"E237.right");Q170=makeQuery(id+"F25.imprint","IMPRINT",FACE,{"disambiguationData":[TD([[makeQuery(id+"F25.imprint","IMPRINT",EDGE,{"derivedFrom":subQ5}),1.0]])]});}
            var Q171;
            {var subQ5=sQuery(id+"F25.wireOp",EDGE,"E238.right");Q171=makeQuery(id+"F25.imprint","IMPRINT",FACE,{"disambiguationData":[TD([[makeQuery(id+"F25.imprint","IMPRINT",EDGE,{"derivedFrom":subQ5}),-1.0]])]});}
            var Q172;
            {var subQ0=sQuery(id+"F25.wireOp",EDGE,"E295.trimOffspring");var subQ1=sQuery(id+"F25.wireOp",EDGE,"E249.right");var subQ2=makeQuery(id+"F25.imprint","INTERSECT",VERTEX,{"derivedFrom":[subQ1,subQ0]});Q172=makeQuery(id+"F25.imprint","IMPRINT",FACE,{"disambiguationData":[TD([[makeQuery(id+"F25.imprint","IMPRINT",EDGE,{"disambiguationData":[TD([[subQ2,-1.0]])],"derivedFrom":subQ1}),1.0]])]});}
            var Q173;
            {var subQ0=sQuery(id+"F25.wireOp",EDGE,"E296.trimOffspring");var subQ1=sQuery(id+"F25.wireOp",EDGE,"E249.right");var subQ2=makeQuery(id+"F25.imprint","INTERSECT",VERTEX,{"derivedFrom":[subQ1,subQ0]});Q173=makeQuery(id+"F25.imprint","IMPRINT",FACE,{"disambiguationData":[TD([[makeQuery(id+"F25.imprint","IMPRINT",EDGE,{"disambiguationData":[TD([[subQ2,-1.0]])],"derivedFrom":subQ1}),1.0]])]});}
            var Q174;
            {var subQ0=sQuery(id+"F25.wireOp",EDGE,"E296.trimOffspring");var subQ1=sQuery(id+"F25.wireOp",EDGE,"E250.right");var subQ2=makeQuery(id+"F25.imprint","INTERSECT",VERTEX,{"derivedFrom":[subQ1,subQ0]});Q174=makeQuery(id+"F25.imprint","IMPRINT",FACE,{"disambiguationData":[TD([[makeQuery(id+"F25.imprint","IMPRINT",EDGE,{"disambiguationData":[TD([[subQ2,-1.0]])],"derivedFrom":subQ1}),1.0]])]});}
            var Q175;
            {var subQ0=sQuery(id+"F25.wireOp",EDGE,"E296.trimOffspring");var subQ1=sQuery(id+"F25.wireOp",EDGE,"E250.left");var subQ2=makeQuery(id+"F25.imprint","INTERSECT",VERTEX,{"derivedFrom":[subQ1,subQ0]});Q175=makeQuery(id+"F25.imprint","IMPRINT",FACE,{"disambiguationData":[TD([[makeQuery(id+"F25.imprint","IMPRINT",EDGE,{"disambiguationData":[TD([[subQ2,-1.0]])],"derivedFrom":subQ1}),1.0]])]});}
            var Q176;
            {var subQ0=sQuery(id+"F25.wireOp",EDGE,"E295.trimOffspring");var subQ1=sQuery(id+"F25.wireOp",EDGE,"E250.left");var subQ2=makeQuery(id+"F25.imprint","INTERSECT",VERTEX,{"derivedFrom":[subQ1,subQ0]});Q176=makeQuery(id+"F25.imprint","IMPRINT",FACE,{"disambiguationData":[TD([[makeQuery(id+"F25.imprint","IMPRINT",EDGE,{"disambiguationData":[TD([[subQ2,-1.0]])],"derivedFrom":subQ1}),1.0]])]});}
            var Q177;
            {var subQ0=sQuery(id+"F25.wireOp",EDGE,"E295.trimOffspring");var subQ1=sQuery(id+"F25.wireOp",EDGE,"E250.right");var subQ2=makeQuery(id+"F25.imprint","INTERSECT",VERTEX,{"derivedFrom":[subQ1,subQ0]});Q177=makeQuery(id+"F25.imprint","IMPRINT",FACE,{"disambiguationData":[TD([[makeQuery(id+"F25.imprint","IMPRINT",EDGE,{"disambiguationData":[TD([[subQ2,-1.0]])],"derivedFrom":subQ1}),1.0]])]});}
            var Q178;
            {var subQ0=sQuery(id+"F25.wireOp",EDGE,"E251.bottom");Q178=makeQuery(id+"F25.imprint","IMPRINT",FACE,{"disambiguationData":[TD([[makeQuery(id+"F25.imprint","IMPRINT",EDGE,{"derivedFrom":subQ0}),-1.0]])]});}
            var Q179;
            {var subQ0=sQuery(id+"F25.wireOp",EDGE,"E250.bottom");Q179=makeQuery(id+"F25.imprint","IMPRINT",FACE,{"disambiguationData":[TD([[makeQuery(id+"F25.imprint","IMPRINT",EDGE,{"derivedFrom":subQ0}),1.0]])]});}
            var Q180;
            {var subQ0=sQuery(id+"F25.wireOp",EDGE,"E288.trimOffspring");var subQ1=sQuery(id+"F25.wireOp",EDGE,"E250.left");var subQ2=makeQuery(id+"F25.imprint","INTERSECT",VERTEX,{"derivedFrom":[subQ1,subQ0]});Q180=makeQuery(id+"F25.imprint","IMPRINT",FACE,{"disambiguationData":[TD([[makeQuery(id+"F25.imprint","IMPRINT",EDGE,{"disambiguationData":[TD([[subQ2,-1.0]])],"derivedFrom":subQ1}),1.0]])]});}
            var Q181;
            {var subQ0=sQuery(id+"F25.wireOp",EDGE,"E292.trimOffspring");var subQ1=sQuery(id+"F25.wireOp",EDGE,"E250.left");var subQ2=makeQuery(id+"F25.imprint","INTERSECT",VERTEX,{"derivedFrom":[subQ1,subQ0]});Q181=makeQuery(id+"F25.imprint","IMPRINT",FACE,{"disambiguationData":[TD([[makeQuery(id+"F25.imprint","IMPRINT",EDGE,{"disambiguationData":[TD([[subQ2,-1.0]])],"derivedFrom":subQ1}),1.0]])]});}
            var Q182;
            {var subQ0=sQuery(id+"F25.wireOp",EDGE,"E288.trimOffspring");var subQ1=sQuery(id+"F25.wireOp",EDGE,"E250.right");var subQ2=makeQuery(id+"F25.imprint","INTERSECT",VERTEX,{"derivedFrom":[subQ1,subQ0]});Q182=makeQuery(id+"F25.imprint","IMPRINT",FACE,{"disambiguationData":[TD([[makeQuery(id+"F25.imprint","IMPRINT",EDGE,{"disambiguationData":[TD([[subQ2,-1.0]])],"derivedFrom":subQ1}),1.0]])]});}
            var Q183;
            {var subQ0=sQuery(id+"F25.wireOp",EDGE,"E292.trimOffspring");var subQ1=sQuery(id+"F25.wireOp",EDGE,"E250.right");var subQ2=makeQuery(id+"F25.imprint","INTERSECT",VERTEX,{"derivedFrom":[subQ1,subQ0]});Q183=makeQuery(id+"F25.imprint","IMPRINT",FACE,{"disambiguationData":[TD([[makeQuery(id+"F25.imprint","IMPRINT",EDGE,{"disambiguationData":[TD([[subQ2,-1.0]])],"derivedFrom":subQ1}),1.0]])]});}
            var Q184;
            {var subQ0=sQuery(id+"F25.wireOp",EDGE,"E288.trimOffspring");var subQ1=sQuery(id+"F25.wireOp",EDGE,"E249.right");var subQ2=makeQuery(id+"F25.imprint","INTERSECT",VERTEX,{"derivedFrom":[subQ1,subQ0]});Q184=makeQuery(id+"F25.imprint","IMPRINT",FACE,{"disambiguationData":[TD([[makeQuery(id+"F25.imprint","IMPRINT",EDGE,{"disambiguationData":[TD([[subQ2,-1.0]])],"derivedFrom":subQ1}),1.0]])]});}
            var Q185;
            {var subQ0=sQuery(id+"F25.wireOp",EDGE,"E292.trimOffspring");var subQ1=sQuery(id+"F25.wireOp",EDGE,"E249.right");var subQ2=makeQuery(id+"F25.imprint","INTERSECT",VERTEX,{"derivedFrom":[subQ1,subQ0]});Q185=makeQuery(id+"F25.imprint","IMPRINT",FACE,{"disambiguationData":[TD([[makeQuery(id+"F25.imprint","IMPRINT",EDGE,{"disambiguationData":[TD([[subQ2,-1.0]])],"derivedFrom":subQ1}),1.0]])]});}
            var Q186;
            {var subQ5=sQuery(id+"F25.wireOp",EDGE,"E242.right");Q186=makeQuery(id+"F25.imprint","IMPRINT",FACE,{"disambiguationData":[TD([[makeQuery(id+"F25.imprint","IMPRINT",EDGE,{"derivedFrom":subQ5}),-1.0]])]});}
            var Q187;
            {var subQ0=sQuery(id+"F25.wireOp",EDGE,"E242.right");Q187=makeQuery(id+"F25.imprint","IMPRINT",FACE,{"disambiguationData":[TD([[makeQuery(id+"F25.imprint","IMPRINT",EDGE,{"derivedFrom":subQ0}),1.0]])]});}
            var Q188;
            {var subQ5=sQuery(id+"F25.wireOp",EDGE,"E241.right");Q188=makeQuery(id+"F25.imprint","IMPRINT",FACE,{"disambiguationData":[TD([[makeQuery(id+"F25.imprint","IMPRINT",EDGE,{"derivedFrom":subQ5}),1.0]])]});}
            var Q189;
            {var subQ0=sQuery(id+"F25.wireOp",EDGE,"E241.right");Q189=makeQuery(id+"F25.imprint","IMPRINT",FACE,{"disambiguationData":[TD([[makeQuery(id+"F25.imprint","IMPRINT",EDGE,{"derivedFrom":subQ0}),-1.0]])]});}
            var Q190;
            {var subQ0=sQuery(id+"F25.wireOp",EDGE,"E365.MirrorCS");var subQ1=sQuery(id+"F25.wireOp",EDGE,"E341.MirrorCS");var subQ2=makeQuery(id+"F25.imprint","INTERSECT",VERTEX,{"derivedFrom":[subQ1,subQ0]});Q190=makeQuery(id+"F25.imprint","IMPRINT",FACE,{"disambiguationData":[TD([[makeQuery(id+"F25.imprint","IMPRINT",EDGE,{"disambiguationData":[TD([[subQ2,-1.0]])],"derivedFrom":subQ1}),-1.0]])]});}
            var Q191;
            {var subQ0=sQuery(id+"F25.wireOp",EDGE,"E356.MirrorCS");var subQ1=sQuery(id+"F25.wireOp",EDGE,"E365.MirrorCS");var subQ2=makeQuery(id+"F25.imprint","INTERSECT",VERTEX,{"derivedFrom":[subQ1,subQ0]});Q191=makeQuery(id+"F25.imprint","IMPRINT",FACE,{"disambiguationData":[TD([[makeQuery(id+"F25.imprint","IMPRINT",EDGE,{"disambiguationData":[TD([[subQ2,-1.0]])],"derivedFrom":subQ1}),1.0]])]});}
            var Q192;
            {var subQ0=sQuery(id+"F25.wireOp",EDGE,"E334.MirrorCS");var subQ1=sQuery(id+"F25.wireOp",EDGE,"E341.MirrorCS");var subQ2=makeQuery(id+"F25.imprint","INTERSECT",VERTEX,{"derivedFrom":[subQ1,subQ0]});Q192=makeQuery(id+"F25.imprint","IMPRINT",FACE,{"disambiguationData":[TD([[makeQuery(id+"F25.imprint","IMPRINT",EDGE,{"disambiguationData":[TD([[subQ2,-1.0]])],"derivedFrom":subQ1}),-1.0]])]});}
            var Q193;
            {var subQ0=sQuery(id+"F25.wireOp",EDGE,"E356.MirrorCS");var subQ1=sQuery(id+"F25.wireOp",EDGE,"E365.MirrorCS");var subQ2=makeQuery(id+"F25.imprint","INTERSECT",VERTEX,{"derivedFrom":[subQ1,subQ0]});Q193=makeQuery(id+"F25.imprint","IMPRINT",FACE,{"disambiguationData":[TD([[makeQuery(id+"F25.imprint","IMPRINT",EDGE,{"disambiguationData":[TD([[subQ2,-1.0]])],"derivedFrom":subQ1}),-1.0]])]});}
            var Q194;
            {var subQ0=sQuery(id+"F25.wireOp",EDGE,"E386.MirrorCS");var subQ1=sQuery(id+"F25.wireOp",EDGE,"E341.MirrorCS");var subQ2=makeQuery(id+"F25.imprint","INTERSECT",VERTEX,{"derivedFrom":[subQ1,subQ0]});Q194=makeQuery(id+"F25.imprint","IMPRINT",FACE,{"disambiguationData":[TD([[makeQuery(id+"F25.imprint","IMPRINT",EDGE,{"disambiguationData":[TD([[subQ2,-1.0]])],"derivedFrom":subQ1}),-1.0]])]});}
            var Q195;
            {var subQ0=sQuery(id+"F25.wireOp",EDGE,"E356.MirrorCS");var subQ1=sQuery(id+"F25.wireOp",EDGE,"E334.MirrorCS");var subQ2=makeQuery(id+"F25.imprint","INTERSECT",VERTEX,{"derivedFrom":[subQ1,subQ0]});Q195=makeQuery(id+"F25.imprint","IMPRINT",FACE,{"disambiguationData":[TD([[makeQuery(id+"F25.imprint","IMPRINT",EDGE,{"disambiguationData":[TD([[subQ2,-1.0]])],"derivedFrom":subQ1}),-1.0]])]});}
            var Q196;
            {var subQ0=sQuery(id+"F25.wireOp",EDGE,"E386.MirrorCS");var subQ1=sQuery(id+"F25.wireOp",EDGE,"E339.MirrorCS");var subQ2=makeQuery(id+"F25.imprint","INTERSECT",VERTEX,{"derivedFrom":[subQ1,subQ0]});Q196=makeQuery(id+"F25.imprint","IMPRINT",FACE,{"disambiguationData":[TD([[makeQuery(id+"F25.imprint","IMPRINT",EDGE,{"disambiguationData":[TD([[subQ2,-1.0]])],"derivedFrom":subQ1}),1.0]])]});}
            var Q197;
            {var subQ0=sQuery(id+"F25.wireOp",EDGE,"E334.MirrorCS");var subQ1=sQuery(id+"F25.wireOp",EDGE,"E339.MirrorCS");var subQ2=makeQuery(id+"F25.imprint","INTERSECT",VERTEX,{"derivedFrom":[subQ1,subQ0]});Q197=makeQuery(id+"F25.imprint","IMPRINT",FACE,{"disambiguationData":[TD([[makeQuery(id+"F25.imprint","IMPRINT",EDGE,{"disambiguationData":[TD([[subQ2,-1.0]])],"derivedFrom":subQ1}),1.0]])]});}
            var Q198;
            {var subQ0=sQuery(id+"F25.wireOp",EDGE,"E334.MirrorCS");var subQ1=sQuery(id+"F25.wireOp",EDGE,"E339.MirrorCS");var subQ2=makeQuery(id+"F25.imprint","INTERSECT",VERTEX,{"derivedFrom":[subQ1,subQ0]});Q198=makeQuery(id+"F25.imprint","IMPRINT",FACE,{"disambiguationData":[TD([[makeQuery(id+"F25.imprint","IMPRINT",EDGE,{"disambiguationData":[TD([[subQ2,-1.0]])],"derivedFrom":subQ1}),-1.0]])]});}
            var Q199;
            {var subQ0=sQuery(id+"F25.wireOp",EDGE,"E361.MirrorCS");var subQ1=sQuery(id+"F25.wireOp",EDGE,"E365.MirrorCS");var subQ2=makeQuery(id+"F25.imprint","INTERSECT",VERTEX,{"derivedFrom":[subQ1,subQ0]});Q199=makeQuery(id+"F25.imprint","IMPRINT",FACE,{"disambiguationData":[TD([[makeQuery(id+"F25.imprint","IMPRINT",EDGE,{"disambiguationData":[TD([[subQ2,-1.0]])],"derivedFrom":subQ1}),-1.0]])]});}
            var Q200;
            {var subQ0=sQuery(id+"F25.wireOp",EDGE,"E361.MirrorCS");var subQ1=sQuery(id+"F25.wireOp",EDGE,"E334.MirrorCS");var subQ2=makeQuery(id+"F25.imprint","INTERSECT",VERTEX,{"derivedFrom":[subQ1,subQ0]});Q200=makeQuery(id+"F25.imprint","IMPRINT",FACE,{"disambiguationData":[TD([[makeQuery(id+"F25.imprint","IMPRINT",EDGE,{"disambiguationData":[TD([[subQ2,-1.0]])],"derivedFrom":subQ1}),-1.0]])]});}
            var Q201;
            {var subQ0=sQuery(id+"F25.wireOp",EDGE,"E386.MirrorCS");var subQ1=sQuery(id+"F25.wireOp",EDGE,"E339.MirrorCS");var subQ2=makeQuery(id+"F25.imprint","INTERSECT",VERTEX,{"derivedFrom":[subQ1,subQ0]});Q201=makeQuery(id+"F25.imprint","IMPRINT",FACE,{"disambiguationData":[TD([[makeQuery(id+"F25.imprint","IMPRINT",EDGE,{"disambiguationData":[TD([[subQ2,-1.0]])],"derivedFrom":subQ1}),-1.0]])]});}
            var Q202;
            {var subQ0=sQuery(id+"F25.wireOp",EDGE,"E361.MirrorCS");var subQ1=sQuery(id+"F25.wireOp",EDGE,"E365.MirrorCS");var subQ2=makeQuery(id+"F25.imprint","INTERSECT",VERTEX,{"derivedFrom":[subQ1,subQ0]});Q202=makeQuery(id+"F25.imprint","IMPRINT",FACE,{"disambiguationData":[TD([[makeQuery(id+"F25.imprint","IMPRINT",EDGE,{"disambiguationData":[TD([[subQ2,-1.0]])],"derivedFrom":subQ1}),1.0]])]});}
            var Q203;
            {var subQ0=sQuery(id+"F25.wireOp",EDGE,"E365.MirrorCS");var subQ1=sQuery(id+"F25.wireOp",EDGE,"E339.MirrorCS");var subQ2=makeQuery(id+"F25.imprint","INTERSECT",VERTEX,{"derivedFrom":[subQ1,subQ0]});Q203=makeQuery(id+"F25.imprint","IMPRINT",FACE,{"disambiguationData":[TD([[makeQuery(id+"F25.imprint","IMPRINT",EDGE,{"disambiguationData":[TD([[subQ2,-1.0]])],"derivedFrom":subQ1}),-1.0]])]});}
            var Q204;
            {var subQ0=sQuery(id+"F25.wireOp",EDGE,"E386.MirrorCS");var subQ1=sQuery(id+"F25.wireOp",EDGE,"E339.MirrorCS");var subQ2=makeQuery(id+"F25.imprint","INTERSECT",VERTEX,{"derivedFrom":[subQ1,subQ0]});Q204=makeQuery(id+"F25.imprint","IMPRINT",FACE,{"disambiguationData":[TD([[makeQuery(id+"F25.imprint","IMPRINT",EDGE,{"disambiguationData":[TD([[subQ2,-1.0]])],"derivedFrom":subQ1}),-1.0]])]});}
            var Q205;
            {var subQ0=sQuery(id+"F25.wireOp",EDGE,"E240.right");Q205=makeQuery(id+"F25.imprint","IMPRINT",FACE,{"disambiguationData":[TD([[makeQuery(id+"F25.imprint","IMPRINT",EDGE,{"derivedFrom":subQ0}),1.0]])]});}
            var Q206;
            {var subQ0=sQuery(id+"F25.wireOp",EDGE,"E239.right");Q206=makeQuery(id+"F25.imprint","IMPRINT",FACE,{"disambiguationData":[TD([[makeQuery(id+"F25.imprint","IMPRINT",EDGE,{"derivedFrom":subQ0}),-1.0]])]});}
            var Q207;
            {var subQ5=sQuery(id+"F25.wireOp",EDGE,"E239.right");Q207=makeQuery(id+"F25.imprint","IMPRINT",FACE,{"disambiguationData":[TD([[makeQuery(id+"F25.imprint","IMPRINT",EDGE,{"derivedFrom":subQ5}),1.0]])]});}
            var Q208;
            {var subQ5=sQuery(id+"F25.wireOp",EDGE,"E240.right");Q208=makeQuery(id+"F25.imprint","IMPRINT",FACE,{"disambiguationData":[TD([[makeQuery(id+"F25.imprint","IMPRINT",EDGE,{"derivedFrom":subQ5}),-1.0]])]});}
            var Q209;
            {var subQ0=sQuery(id+"F25.wireOp",EDGE,"E293.trimOffspring");var subQ1=sQuery(id+"F25.wireOp",EDGE,"E249.right");var subQ2=makeQuery(id+"F25.imprint","INTERSECT",VERTEX,{"derivedFrom":[subQ1,subQ0]});Q209=makeQuery(id+"F25.imprint","IMPRINT",FACE,{"disambiguationData":[TD([[makeQuery(id+"F25.imprint","IMPRINT",EDGE,{"disambiguationData":[TD([[subQ2,-1.0]])],"derivedFrom":subQ1}),1.0]])]});}
            var Q210;
            {var subQ0=sQuery(id+"F25.wireOp",EDGE,"E297.trimOffspring");var subQ1=sQuery(id+"F25.wireOp",EDGE,"E249.right");var subQ2=makeQuery(id+"F25.imprint","INTERSECT",VERTEX,{"derivedFrom":[subQ1,subQ0]});Q210=makeQuery(id+"F25.imprint","IMPRINT",FACE,{"disambiguationData":[TD([[makeQuery(id+"F25.imprint","IMPRINT",EDGE,{"disambiguationData":[TD([[subQ2,-1.0]])],"derivedFrom":subQ1}),1.0]])]});}
            var Q211;
            {var subQ0=sQuery(id+"F25.wireOp",EDGE,"E297.trimOffspring");var subQ1=sQuery(id+"F25.wireOp",EDGE,"E250.right");var subQ2=makeQuery(id+"F25.imprint","INTERSECT",VERTEX,{"derivedFrom":[subQ1,subQ0]});Q211=makeQuery(id+"F25.imprint","IMPRINT",FACE,{"disambiguationData":[TD([[makeQuery(id+"F25.imprint","IMPRINT",EDGE,{"disambiguationData":[TD([[subQ2,-1.0]])],"derivedFrom":subQ1}),1.0]])]});}
            var Q212;
            {var subQ0=sQuery(id+"F25.wireOp",EDGE,"E297.trimOffspring");var subQ1=sQuery(id+"F25.wireOp",EDGE,"E250.left");var subQ2=makeQuery(id+"F25.imprint","INTERSECT",VERTEX,{"derivedFrom":[subQ1,subQ0]});Q212=makeQuery(id+"F25.imprint","IMPRINT",FACE,{"disambiguationData":[TD([[makeQuery(id+"F25.imprint","IMPRINT",EDGE,{"disambiguationData":[TD([[subQ2,-1.0]])],"derivedFrom":subQ1}),1.0]])]});}
            var Q213;
            {var subQ0=sQuery(id+"F25.wireOp",EDGE,"E293.trimOffspring");var subQ1=sQuery(id+"F25.wireOp",EDGE,"E250.left");var subQ2=makeQuery(id+"F25.imprint","INTERSECT",VERTEX,{"derivedFrom":[subQ1,subQ0]});Q213=makeQuery(id+"F25.imprint","IMPRINT",FACE,{"disambiguationData":[TD([[makeQuery(id+"F25.imprint","IMPRINT",EDGE,{"disambiguationData":[TD([[subQ2,-1.0]])],"derivedFrom":subQ1}),1.0]])]});}
            var Q214;
            {var subQ0=sQuery(id+"F25.wireOp",EDGE,"E293.trimOffspring");var subQ1=sQuery(id+"F25.wireOp",EDGE,"E250.right");var subQ2=makeQuery(id+"F25.imprint","INTERSECT",VERTEX,{"derivedFrom":[subQ1,subQ0]});Q214=makeQuery(id+"F25.imprint","IMPRINT",FACE,{"disambiguationData":[TD([[makeQuery(id+"F25.imprint","IMPRINT",EDGE,{"disambiguationData":[TD([[subQ2,-1.0]])],"derivedFrom":subQ1}),1.0]])]});}
            var Q215;
            {var subQ0=sQuery(id+"F25.wireOp",EDGE,"E232.left");Q215=makeQuery(id+"F25.imprint","IMPRINT",FACE,{"disambiguationData":[TD([[makeQuery(id+"F25.imprint","IMPRINT",EDGE,{"derivedFrom":subQ0}),-1.0]])]});}
            var Q216;
            {var subQ0=sQuery(id+"F25.wireOp",EDGE,"E255.trimOffspring");var subQ1=sQuery(id+"F25.wireOp",EDGE,"E232.top");var subQ2=makeQuery(id+"F25.imprint","INTERSECT",VERTEX,{"derivedFrom":[subQ1,subQ0]});Q216=makeQuery(id+"F25.imprint","IMPRINT",FACE,{"disambiguationData":[TD([[makeQuery(id+"F25.imprint","IMPRINT",EDGE,{"disambiguationData":[TD([[subQ2,-1.0]])],"derivedFrom":subQ1}),-1.0]])]});}
            var Q217;
            {var subQ1=sQuery(id+"F25.wireOp",EDGE,"E232.top");var subQ3=sQuery(id+"F25.wireOp",EDGE,"E256.trimOffspring");var subQ4=makeQuery(id+"F25.imprint","INTERSECT",VERTEX,{"derivedFrom":[subQ1,subQ3]});Q217=makeQuery(id+"F25.imprint","IMPRINT",FACE,{"disambiguationData":[TD([[makeQuery(id+"F25.imprint","IMPRINT",EDGE,{"disambiguationData":[TD([[subQ4,1.0]])],"derivedFrom":subQ3}),-1.0]])]});}
            var Q218;
            {var subQ1=sQuery(id+"F25.wireOp",EDGE,"E234.bottom");var subQ3=sQuery(id+"F25.wireOp",EDGE,"E256.trimOffspring");var subQ4=makeQuery(id+"F25.imprint","INTERSECT",VERTEX,{"derivedFrom":[subQ1,subQ3]});Q218=makeQuery(id+"F25.imprint","IMPRINT",FACE,{"disambiguationData":[TD([[makeQuery(id+"F25.imprint","IMPRINT",EDGE,{"disambiguationData":[TD([[subQ4,1.0]])],"derivedFrom":subQ3}),-1.0]])]});}
            var Q219;
            {var subQ0=sQuery(id+"F25.wireOp",EDGE,"E254.trimOffspring");var subQ5=sQuery(id+"F25.wireOp",EDGE,"E253.top");var subQ6=makeQuery(id+"F25.imprint","INTERSECT",VERTEX,{"derivedFrom":[subQ5,subQ0]});Q219=makeQuery(id+"F25.imprint","IMPRINT",FACE,{"disambiguationData":[TD([[makeQuery(id+"F25.imprint","IMPRINT",EDGE,{"disambiguationData":[TD([[subQ6,1.0]])],"derivedFrom":subQ5}),1.0]])]});}
            var Q220;
            {var subQ0=sQuery(id+"F25.wireOp",EDGE,"E254.trimOffspring");var subQ1=sQuery(id+"F25.wireOp",EDGE,"E253.bottom");var subQ2=makeQuery(id+"F25.imprint","INTERSECT",VERTEX,{"derivedFrom":[subQ1,subQ0]});Q220=makeQuery(id+"F25.imprint","IMPRINT",FACE,{"disambiguationData":[TD([[makeQuery(id+"F25.imprint","IMPRINT",EDGE,{"disambiguationData":[TD([[subQ2,1.0]])],"derivedFrom":subQ1}),1.0]])]});}
            var Q221;
            {var subQ0=sQuery(id+"F25.wireOp",EDGE,"E254.trimOffspring");var subQ1=sQuery(id+"F25.wireOp",EDGE,"E252.top");var subQ2=makeQuery(id+"F25.imprint","INTERSECT",VERTEX,{"derivedFrom":[subQ1,subQ0]});Q221=makeQuery(id+"F25.imprint","IMPRINT",FACE,{"disambiguationData":[TD([[makeQuery(id+"F25.imprint","IMPRINT",EDGE,{"disambiguationData":[TD([[subQ2,1.0]])],"derivedFrom":subQ1}),1.0]])]});}
            var Q222;
            {var subQ0=sQuery(id+"F25.wireOp",EDGE,"E256.trimOffspring");var subQ1=sQuery(id+"F25.wireOp",EDGE,"E235.top");var subQ2=makeQuery(id+"F25.imprint","INTERSECT",VERTEX,{"derivedFrom":[subQ1,subQ0]});Q222=makeQuery(id+"F25.imprint","IMPRINT",FACE,{"disambiguationData":[TD([[makeQuery(id+"F25.imprint","IMPRINT",EDGE,{"disambiguationData":[TD([[subQ2,-1.0]])],"derivedFrom":subQ1}),1.0]])]});}
            var Q223;
            {var subQ0=sQuery(id+"F25.wireOp",EDGE,"E256.trimOffspring");var subQ1=sQuery(id+"F25.wireOp",EDGE,"E235.top");var subQ2=makeQuery(id+"F25.imprint","INTERSECT",VERTEX,{"derivedFrom":[subQ1,subQ0]});Q223=makeQuery(id+"F25.imprint","IMPRINT",FACE,{"disambiguationData":[TD([[makeQuery(id+"F25.imprint","IMPRINT",EDGE,{"disambiguationData":[TD([[subQ2,-1.0]])],"derivedFrom":subQ1}),-1.0]])]});}
            var Q224;
            {var subQ0=sQuery(id+"F25.wireOp",EDGE,"E254.trimOffspring");var subQ1=sQuery(id+"F25.wireOp",EDGE,"E235.top");var subQ2=makeQuery(id+"F25.imprint","INTERSECT",VERTEX,{"derivedFrom":[subQ1,subQ0]});Q224=makeQuery(id+"F25.imprint","IMPRINT",FACE,{"disambiguationData":[TD([[makeQuery(id+"F25.imprint","IMPRINT",EDGE,{"disambiguationData":[TD([[subQ2,-1.0]])],"derivedFrom":subQ1}),-1.0]])]});}
            var Q225;
            {var subQ0=sQuery(id+"F25.wireOp",EDGE,"E257.trimOffspring");var subQ1=sQuery(id+"F25.wireOp",EDGE,"E235.top");var subQ2=makeQuery(id+"F25.imprint","INTERSECT",VERTEX,{"derivedFrom":[subQ1,subQ0]});Q225=makeQuery(id+"F25.imprint","IMPRINT",FACE,{"disambiguationData":[TD([[makeQuery(id+"F25.imprint","IMPRINT",EDGE,{"disambiguationData":[TD([[subQ2,-1.0]])],"derivedFrom":subQ1}),-1.0]])]});}
            var Q226;
            {var subQ0=sQuery(id+"F25.wireOp",EDGE,"E259.trimOffspring");var subQ1=sQuery(id+"F25.wireOp",EDGE,"E235.top");var subQ2=makeQuery(id+"F25.imprint","INTERSECT",VERTEX,{"derivedFrom":[subQ1,subQ0]});Q226=makeQuery(id+"F25.imprint","IMPRINT",FACE,{"disambiguationData":[TD([[makeQuery(id+"F25.imprint","IMPRINT",EDGE,{"disambiguationData":[TD([[subQ2,-1.0]])],"derivedFrom":subQ1}),-1.0]])]});}
            var Q227;
            {var subQ1=sQuery(id+"F25.wireOp",EDGE,"E235.top");var subQ3=sQuery(id+"F25.wireOp",EDGE,"E258.trimOffspring");var subQ4=makeQuery(id+"F25.imprint","INTERSECT",VERTEX,{"derivedFrom":[subQ1,subQ3]});Q227=makeQuery(id+"F25.imprint","IMPRINT",FACE,{"disambiguationData":[TD([[makeQuery(id+"F25.imprint","IMPRINT",EDGE,{"disambiguationData":[TD([[subQ4,1.0]])],"derivedFrom":subQ3}),-1.0]])]});}
            var Q228;
            {var subQ0=sQuery(id+"F25.wireOp",EDGE,"E257.trimOffspring");var subQ1=sQuery(id+"F25.wireOp",EDGE,"E235.top");var subQ2=makeQuery(id+"F25.imprint","INTERSECT",VERTEX,{"derivedFrom":[subQ1,subQ0]});Q228=makeQuery(id+"F25.imprint","IMPRINT",FACE,{"disambiguationData":[TD([[makeQuery(id+"F25.imprint","IMPRINT",EDGE,{"disambiguationData":[TD([[subQ2,-1.0]])],"derivedFrom":subQ1}),1.0]])]});}
            var Q229;
            {var subQ0=sQuery(id+"F25.wireOp",EDGE,"E259.trimOffspring");var subQ1=sQuery(id+"F25.wireOp",EDGE,"E235.top");var subQ2=makeQuery(id+"F25.imprint","INTERSECT",VERTEX,{"derivedFrom":[subQ1,subQ0]});Q229=makeQuery(id+"F25.imprint","IMPRINT",FACE,{"disambiguationData":[TD([[makeQuery(id+"F25.imprint","IMPRINT",EDGE,{"disambiguationData":[TD([[subQ2,-1.0]])],"derivedFrom":subQ1}),1.0]])]});}
            var Q230;
            {var subQ0=sQuery(id+"F25.wireOp",EDGE,"E499.trimOffspring");var subQ1=sQuery(id+"F25.wireOp",EDGE,"E257.trimOffspring");var subQ2=makeQuery(id+"F25.imprint","INTERSECT",VERTEX,{"derivedFrom":[subQ1,subQ0]});Q230=makeQuery(id+"F25.imprint","IMPRINT",FACE,{"disambiguationData":[TD([[makeQuery(id+"F25.imprint","IMPRINT",EDGE,{"disambiguationData":[TD([[subQ2,1.0]])],"derivedFrom":subQ1}),-1.0]])]});}
            var Q231;
            {var subQ0=sQuery(id+"F25.wireOp",EDGE,"E499.trimOffspring");var subQ1=sQuery(id+"F25.wireOp",EDGE,"E258.trimOffspring");var subQ2=makeQuery(id+"F25.imprint","INTERSECT",VERTEX,{"derivedFrom":[subQ1,subQ0]});Q231=makeQuery(id+"F25.imprint","IMPRINT",FACE,{"disambiguationData":[TD([[makeQuery(id+"F25.imprint","IMPRINT",EDGE,{"disambiguationData":[TD([[subQ2,1.0]])],"derivedFrom":subQ1}),1.0]])]});}
            var Q232;
            {var subQ0=sQuery(id+"F25.wireOp",EDGE,"E499.trimOffspring");var subQ1=sQuery(id+"F25.wireOp",EDGE,"E257.trimOffspring");var subQ2=makeQuery(id+"F25.imprint","INTERSECT",VERTEX,{"derivedFrom":[subQ1,subQ0]});Q232=makeQuery(id+"F25.imprint","IMPRINT",FACE,{"disambiguationData":[TD([[makeQuery(id+"F25.imprint","IMPRINT",EDGE,{"disambiguationData":[TD([[subQ2,-1.0]])],"derivedFrom":subQ1}),-1.0]])]});}
            var Q233;
            {var subQ0=sQuery(id+"F25.wireOp",EDGE,"E499.trimOffspring");var subQ1=sQuery(id+"F25.wireOp",EDGE,"E258.trimOffspring");var subQ2=makeQuery(id+"F25.imprint","INTERSECT",VERTEX,{"derivedFrom":[subQ1,subQ0]});Q233=makeQuery(id+"F25.imprint","IMPRINT",FACE,{"disambiguationData":[TD([[makeQuery(id+"F25.imprint","IMPRINT",EDGE,{"disambiguationData":[TD([[subQ2,-1.0]])],"derivedFrom":subQ1}),1.0]])]});}
            var Q234;
            {var subQ3=sQuery(id+"F25.wireOp",EDGE,"E497.trimOffspring");var subQ5=sQuery(id+"F25.wireOp",EDGE,"E259.trimOffspring");var subQ6=makeQuery(id+"F25.imprint","INTERSECT",VERTEX,{"derivedFrom":[subQ5,subQ3]});Q234=makeQuery(id+"F25.imprint","IMPRINT",FACE,{"disambiguationData":[TD([[makeQuery(id+"F25.imprint","IMPRINT",EDGE,{"disambiguationData":[TD([[subQ6,-1.0]])],"derivedFrom":subQ5}),1.0]])]});}
            var Q235;
            {var subQ0=sQuery(id+"F25.wireOp",EDGE,"E497.trimOffspring");var subQ1=sQuery(id+"F25.wireOp",EDGE,"E258.trimOffspring");var subQ2=makeQuery(id+"F25.imprint","INTERSECT",VERTEX,{"derivedFrom":[subQ1,subQ0]});Q235=makeQuery(id+"F25.imprint","IMPRINT",FACE,{"disambiguationData":[TD([[makeQuery(id+"F25.imprint","IMPRINT",EDGE,{"disambiguationData":[TD([[subQ2,-1.0]])],"derivedFrom":subQ1}),1.0]])]});}
            var Q236;
            {var subQ3=sQuery(id+"F25.wireOp",EDGE,"E496.trimOffspring");var subQ5=sQuery(id+"F25.wireOp",EDGE,"E259.trimOffspring");var subQ6=makeQuery(id+"F25.imprint","INTERSECT",VERTEX,{"derivedFrom":[subQ5,subQ3]});Q236=makeQuery(id+"F25.imprint","IMPRINT",FACE,{"disambiguationData":[TD([[makeQuery(id+"F25.imprint","IMPRINT",EDGE,{"disambiguationData":[TD([[subQ6,1.0]])],"derivedFrom":subQ5}),1.0]])]});}
            var Q237;
            {var subQ0=sQuery(id+"F25.wireOp",EDGE,"E496.trimOffspring");var subQ1=sQuery(id+"F25.wireOp",EDGE,"E258.trimOffspring");var subQ2=makeQuery(id+"F25.imprint","INTERSECT",VERTEX,{"derivedFrom":[subQ1,subQ0]});Q237=makeQuery(id+"F25.imprint","IMPRINT",FACE,{"disambiguationData":[TD([[makeQuery(id+"F25.imprint","IMPRINT",EDGE,{"disambiguationData":[TD([[subQ2,1.0]])],"derivedFrom":subQ1}),1.0]])]});}
            var Q238;
            {var subQ3=sQuery(id+"F25.wireOp",EDGE,"E504.trimOffspring");var subQ5=sQuery(id+"F25.wireOp",EDGE,"E261.trimOffspring");var subQ6=makeQuery(id+"F25.imprint","INTERSECT",VERTEX,{"derivedFrom":[subQ5,subQ3]});Q238=makeQuery(id+"F25.imprint","IMPRINT",FACE,{"disambiguationData":[TD([[makeQuery(id+"F25.imprint","IMPRINT",EDGE,{"disambiguationData":[TD([[subQ6,-1.0]])],"derivedFrom":subQ5}),1.0]])]});}
            var Q239;
            {var subQ0=sQuery(id+"F25.wireOp",EDGE,"E504.trimOffspring");var subQ1=sQuery(id+"F25.wireOp",EDGE,"E260.trimOffspring");var subQ2=makeQuery(id+"F25.imprint","INTERSECT",VERTEX,{"derivedFrom":[subQ1,subQ0]});Q239=makeQuery(id+"F25.imprint","IMPRINT",FACE,{"disambiguationData":[TD([[makeQuery(id+"F25.imprint","IMPRINT",EDGE,{"disambiguationData":[TD([[subQ2,-1.0]])],"derivedFrom":subQ1}),1.0]])]});}
            var Q240;
            {var subQ0=sQuery(id+"F25.wireOp",EDGE,"E504.trimOffspring");var subQ1=sQuery(id+"F25.wireOp",EDGE,"E260.trimOffspring");var subQ2=makeQuery(id+"F25.imprint","INTERSECT",VERTEX,{"derivedFrom":[subQ1,subQ0]});Q240=makeQuery(id+"F25.imprint","IMPRINT",FACE,{"disambiguationData":[TD([[makeQuery(id+"F25.imprint","IMPRINT",EDGE,{"disambiguationData":[TD([[subQ2,-1.0]])],"derivedFrom":subQ1}),-1.0]])]});}
            var Q241;
            {var subQ0=sQuery(id+"F25.wireOp",EDGE,"E503.trimOffspring");var subQ5=sQuery(id+"F25.wireOp",EDGE,"E261.trimOffspring");var subQ6=makeQuery(id+"F25.imprint","INTERSECT",VERTEX,{"derivedFrom":[subQ5,subQ0]});Q241=makeQuery(id+"F25.imprint","IMPRINT",FACE,{"disambiguationData":[TD([[makeQuery(id+"F25.imprint","IMPRINT",EDGE,{"disambiguationData":[TD([[subQ6,-1.0]])],"derivedFrom":subQ5}),1.0]])]});}
            var Q242;
            {var subQ0=sQuery(id+"F25.wireOp",EDGE,"E505.trimOffspring");var subQ1=sQuery(id+"F25.wireOp",EDGE,"E260.trimOffspring");var subQ2=makeQuery(id+"F25.imprint","INTERSECT",VERTEX,{"derivedFrom":[subQ1,subQ0]});Q242=makeQuery(id+"F25.imprint","IMPRINT",FACE,{"disambiguationData":[TD([[makeQuery(id+"F25.imprint","IMPRINT",EDGE,{"disambiguationData":[TD([[subQ2,1.0]])],"derivedFrom":subQ1}),1.0]])]});}
            var Q243;
            {var subQ0=sQuery(id+"F25.wireOp",EDGE,"E505.trimOffspring");var subQ1=sQuery(id+"F25.wireOp",EDGE,"E262.trimOffspring");var subQ2=makeQuery(id+"F25.imprint","INTERSECT",VERTEX,{"derivedFrom":[subQ1,subQ0]});Q243=makeQuery(id+"F25.imprint","IMPRINT",FACE,{"disambiguationData":[TD([[makeQuery(id+"F25.imprint","IMPRINT",EDGE,{"disambiguationData":[TD([[subQ2,-1.0]])],"derivedFrom":subQ1}),-1.0]])]});}
            var Q244;
            {var subQ0=sQuery(id+"F25.wireOp",EDGE,"E505.trimOffspring");var subQ1=sQuery(id+"F25.wireOp",EDGE,"E260.trimOffspring");var subQ2=makeQuery(id+"F25.imprint","INTERSECT",VERTEX,{"derivedFrom":[subQ1,subQ0]});Q244=makeQuery(id+"F25.imprint","IMPRINT",FACE,{"disambiguationData":[TD([[makeQuery(id+"F25.imprint","IMPRINT",EDGE,{"disambiguationData":[TD([[subQ2,-1.0]])],"derivedFrom":subQ1}),1.0]])]});}
            var Q245;
            {var subQ0=sQuery(id+"F25.wireOp",EDGE,"E511.trimOffspring");var subQ1=sQuery(id+"F25.wireOp",EDGE,"E262.trimOffspring");var subQ2=makeQuery(id+"F25.imprint","INTERSECT",VERTEX,{"derivedFrom":[subQ1,subQ0]});Q245=makeQuery(id+"F25.imprint","IMPRINT",FACE,{"disambiguationData":[TD([[makeQuery(id+"F25.imprint","IMPRINT",EDGE,{"disambiguationData":[TD([[subQ2,1.0]])],"derivedFrom":subQ1}),-1.0]])]});}
            var Q246;
            {var subQ0=sQuery(id+"F25.wireOp",EDGE,"E511.trimOffspring");var subQ1=sQuery(id+"F25.wireOp",EDGE,"E260.trimOffspring");var subQ2=makeQuery(id+"F25.imprint","INTERSECT",VERTEX,{"derivedFrom":[subQ1,subQ0]});Q246=makeQuery(id+"F25.imprint","IMPRINT",FACE,{"disambiguationData":[TD([[makeQuery(id+"F25.imprint","IMPRINT",EDGE,{"disambiguationData":[TD([[subQ2,1.0]])],"derivedFrom":subQ1}),1.0]])]});}
            var Q247;
            {var subQ0=sQuery(id+"F25.wireOp",EDGE,"E511.trimOffspring");var subQ1=sQuery(id+"F25.wireOp",EDGE,"E262.trimOffspring");var subQ2=makeQuery(id+"F25.imprint","INTERSECT",VERTEX,{"derivedFrom":[subQ1,subQ0]});Q247=makeQuery(id+"F25.imprint","IMPRINT",FACE,{"disambiguationData":[TD([[makeQuery(id+"F25.imprint","IMPRINT",EDGE,{"disambiguationData":[TD([[subQ2,-1.0]])],"derivedFrom":subQ1}),-1.0]])]});}
            var Q248;
            {var subQ0=sQuery(id+"F25.wireOp",EDGE,"E497.trimOffspring");var subQ1=sQuery(id+"F25.wireOp",EDGE,"E260.trimOffspring");var subQ2=makeQuery(id+"F25.imprint","INTERSECT",VERTEX,{"derivedFrom":[subQ1,subQ0]});Q248=makeQuery(id+"F25.imprint","IMPRINT",FACE,{"disambiguationData":[TD([[makeQuery(id+"F25.imprint","IMPRINT",EDGE,{"disambiguationData":[TD([[subQ2,1.0]])],"derivedFrom":subQ1}),1.0]])]});}
            var Q249;
            {var subQ0=sQuery(id+"F25.wireOp",EDGE,"E497.trimOffspring");var subQ1=sQuery(id+"F25.wireOp",EDGE,"E262.trimOffspring");var subQ2=makeQuery(id+"F25.imprint","INTERSECT",VERTEX,{"derivedFrom":[subQ1,subQ0]});Q249=makeQuery(id+"F25.imprint","IMPRINT",FACE,{"disambiguationData":[TD([[makeQuery(id+"F25.imprint","IMPRINT",EDGE,{"disambiguationData":[TD([[subQ2,-1.0]])],"derivedFrom":subQ1}),-1.0]])]});}
            var Q250;
            {var subQ0=sQuery(id+"F25.wireOp",EDGE,"E497.trimOffspring");var subQ1=sQuery(id+"F25.wireOp",EDGE,"E260.trimOffspring");var subQ2=makeQuery(id+"F25.imprint","INTERSECT",VERTEX,{"derivedFrom":[subQ1,subQ0]});Q250=makeQuery(id+"F25.imprint","IMPRINT",FACE,{"disambiguationData":[TD([[makeQuery(id+"F25.imprint","IMPRINT",EDGE,{"disambiguationData":[TD([[subQ2,-1.0]])],"derivedFrom":subQ1}),1.0]])]});}
            var Q251;
            {var subQ0=sQuery(id+"F25.wireOp",EDGE,"E496.trimOffspring");var subQ1=sQuery(id+"F25.wireOp",EDGE,"E262.trimOffspring");var subQ2=makeQuery(id+"F25.imprint","INTERSECT",VERTEX,{"derivedFrom":[subQ1,subQ0]});Q251=makeQuery(id+"F25.imprint","IMPRINT",FACE,{"disambiguationData":[TD([[makeQuery(id+"F25.imprint","IMPRINT",EDGE,{"disambiguationData":[TD([[subQ2,1.0]])],"derivedFrom":subQ1}),-1.0]])]});}
            var Q252;
            {var subQ0=sQuery(id+"F25.wireOp",EDGE,"E496.trimOffspring");var subQ1=sQuery(id+"F25.wireOp",EDGE,"E260.trimOffspring");var subQ2=makeQuery(id+"F25.imprint","INTERSECT",VERTEX,{"derivedFrom":[subQ1,subQ0]});Q252=makeQuery(id+"F25.imprint","IMPRINT",FACE,{"disambiguationData":[TD([[makeQuery(id+"F25.imprint","IMPRINT",EDGE,{"disambiguationData":[TD([[subQ2,1.0]])],"derivedFrom":subQ1}),1.0]])]});}
            var Q253;
            {var subQ0=sQuery(id+"F25.wireOp",EDGE,"E529.trimOffspring");var subQ1=sQuery(id+"F25.wireOp",EDGE,"E503.trimOffspring");var subQ2=makeQuery(id+"F25.imprint","INTERSECT",VERTEX,{"derivedFrom":[subQ1,subQ0]});Q253=makeQuery(id+"F25.imprint","IMPRINT",FACE,{"disambiguationData":[TD([[makeQuery(id+"F25.imprint","IMPRINT",EDGE,{"disambiguationData":[TD([[subQ2,-1.0]])],"derivedFrom":subQ1}),-1.0]])]});}
            var Q254;
            {var subQ0=sQuery(id+"F25.wireOp",EDGE,"E529.trimOffspring");var subQ1=sQuery(id+"F25.wireOp",EDGE,"E503.trimOffspring");var subQ2=makeQuery(id+"F25.imprint","INTERSECT",VERTEX,{"derivedFrom":[subQ1,subQ0]});Q254=makeQuery(id+"F25.imprint","IMPRINT",FACE,{"disambiguationData":[TD([[makeQuery(id+"F25.imprint","IMPRINT",EDGE,{"disambiguationData":[TD([[subQ2,-1.0]])],"derivedFrom":subQ1}),1.0]])]});}
            var Q255;
            {var subQ0=sQuery(id+"F25.wireOp",EDGE,"E529.trimOffspring");var subQ1=sQuery(id+"F25.wireOp",EDGE,"E507.trimOffspring");var subQ2=makeQuery(id+"F25.imprint","INTERSECT",VERTEX,{"derivedFrom":[subQ1,subQ0]});Q255=makeQuery(id+"F25.imprint","IMPRINT",FACE,{"disambiguationData":[TD([[makeQuery(id+"F25.imprint","IMPRINT",EDGE,{"disambiguationData":[TD([[subQ2,-1.0]])],"derivedFrom":subQ1}),1.0]])]});}
            var Q256;
            {var subQ0=sQuery(id+"F25.wireOp",EDGE,"E529.trimOffspring");var subQ1=sQuery(id+"F25.wireOp",EDGE,"E510.trimOffspring");var subQ2=makeQuery(id+"F25.imprint","INTERSECT",VERTEX,{"derivedFrom":[subQ1,subQ0]});Q256=makeQuery(id+"F25.imprint","IMPRINT",FACE,{"disambiguationData":[TD([[makeQuery(id+"F25.imprint","IMPRINT",EDGE,{"disambiguationData":[TD([[subQ2,-1.0]])],"derivedFrom":subQ1}),-1.0]])]});}
            var Q257;
            {var subQ0=sQuery(id+"F25.wireOp",EDGE,"E530.trimOffspring");var subQ1=sQuery(id+"F25.wireOp",EDGE,"E510.trimOffspring");var subQ2=makeQuery(id+"F25.imprint","INTERSECT",VERTEX,{"derivedFrom":[subQ1,subQ0]});Q257=makeQuery(id+"F25.imprint","IMPRINT",FACE,{"disambiguationData":[TD([[makeQuery(id+"F25.imprint","IMPRINT",EDGE,{"disambiguationData":[TD([[subQ2,-1.0]])],"derivedFrom":subQ1}),-1.0]])]});}
            var Q258;
            {var subQ0=sQuery(id+"F25.wireOp",EDGE,"E531.trimOffspring");var subQ1=sQuery(id+"F25.wireOp",EDGE,"E510.trimOffspring");var subQ2=makeQuery(id+"F25.imprint","INTERSECT",VERTEX,{"derivedFrom":[subQ1,subQ0]});Q258=makeQuery(id+"F25.imprint","IMPRINT",FACE,{"disambiguationData":[TD([[makeQuery(id+"F25.imprint","IMPRINT",EDGE,{"disambiguationData":[TD([[subQ2,-1.0]])],"derivedFrom":subQ1}),-1.0]])]});}
            var Q259;
            {var subQ0=sQuery(id+"F25.wireOp",EDGE,"E532.trimOffspring");var subQ1=sQuery(id+"F25.wireOp",EDGE,"E510.trimOffspring");var subQ2=makeQuery(id+"F25.imprint","INTERSECT",VERTEX,{"derivedFrom":[subQ1,subQ0]});Q259=makeQuery(id+"F25.imprint","IMPRINT",FACE,{"disambiguationData":[TD([[makeQuery(id+"F25.imprint","IMPRINT",EDGE,{"disambiguationData":[TD([[subQ2,-1.0]])],"derivedFrom":subQ1}),1.0]])]});}
            var Q260;
            {var subQ0=sQuery(id+"F25.wireOp",EDGE,"E527.trimOffspring");var subQ1=sQuery(id+"F25.wireOp",EDGE,"E510.trimOffspring");var subQ2=makeQuery(id+"F25.imprint","INTERSECT",VERTEX,{"derivedFrom":[subQ1,subQ0]});Q260=makeQuery(id+"F25.imprint","IMPRINT",FACE,{"disambiguationData":[TD([[makeQuery(id+"F25.imprint","IMPRINT",EDGE,{"disambiguationData":[TD([[subQ2,-1.0]])],"derivedFrom":subQ1}),1.0]])]});}
            var Q261;
            {var subQ0=sQuery(id+"F25.wireOp",EDGE,"E532.trimOffspring");var subQ1=sQuery(id+"F25.wireOp",EDGE,"E509.trimOffspring");var subQ2=makeQuery(id+"F25.imprint","INTERSECT",VERTEX,{"derivedFrom":[subQ1,subQ0]});Q261=makeQuery(id+"F25.imprint","IMPRINT",FACE,{"disambiguationData":[TD([[makeQuery(id+"F25.imprint","IMPRINT",EDGE,{"disambiguationData":[TD([[subQ2,-1.0]])],"derivedFrom":subQ1}),-1.0]])]});}
            var Q262;
            {var subQ0=sQuery(id+"F25.wireOp",EDGE,"E533.trimOffspring");var subQ1=sQuery(id+"F25.wireOp",EDGE,"E509.trimOffspring");var subQ2=makeQuery(id+"F25.imprint","INTERSECT",VERTEX,{"derivedFrom":[subQ1,subQ0]});Q262=makeQuery(id+"F25.imprint","IMPRINT",FACE,{"disambiguationData":[TD([[makeQuery(id+"F25.imprint","IMPRINT",EDGE,{"disambiguationData":[TD([[subQ2,1.0]])],"derivedFrom":subQ1}),-1.0]])]});}
            var Q263;
            {var subQ0=sQuery(id+"F25.wireOp",EDGE,"E533.trimOffspring");var subQ1=sQuery(id+"F25.wireOp",EDGE,"E509.trimOffspring");var subQ2=makeQuery(id+"F25.imprint","INTERSECT",VERTEX,{"derivedFrom":[subQ1,subQ0]});Q263=makeQuery(id+"F25.imprint","IMPRINT",FACE,{"disambiguationData":[TD([[makeQuery(id+"F25.imprint","IMPRINT",EDGE,{"disambiguationData":[TD([[subQ2,1.0]])],"derivedFrom":subQ1}),1.0]])]});}
            var Q264;
            {var subQ0=sQuery(id+"F25.wireOp",EDGE,"E532.trimOffspring");var subQ1=sQuery(id+"F25.wireOp",EDGE,"E509.trimOffspring");var subQ2=makeQuery(id+"F25.imprint","INTERSECT",VERTEX,{"derivedFrom":[subQ1,subQ0]});Q264=makeQuery(id+"F25.imprint","IMPRINT",FACE,{"disambiguationData":[TD([[makeQuery(id+"F25.imprint","IMPRINT",EDGE,{"disambiguationData":[TD([[subQ2,-1.0]])],"derivedFrom":subQ1}),1.0]])]});}
            var Q265;
            {var subQ0=sQuery(id+"F25.wireOp",EDGE,"E516.trimOffspring");var subQ1=sQuery(id+"F25.wireOp",EDGE,"E509.trimOffspring");var subQ2=makeQuery(id+"F25.imprint","INTERSECT",VERTEX,{"derivedFrom":[subQ1,subQ0]});Q265=makeQuery(id+"F25.imprint","IMPRINT",FACE,{"disambiguationData":[TD([[makeQuery(id+"F25.imprint","IMPRINT",EDGE,{"disambiguationData":[TD([[subQ2,-1.0]])],"derivedFrom":subQ1}),-1.0]])]});}
            var Q266;
            {var subQ3=sQuery(id+"F25.wireOp",EDGE,"E516.trimOffspring");var subQ5=sQuery(id+"F25.wireOp",EDGE,"E509.trimOffspring");var subQ6=makeQuery(id+"F25.imprint","INTERSECT",VERTEX,{"derivedFrom":[subQ5,subQ3]});Q266=makeQuery(id+"F25.imprint","IMPRINT",FACE,{"disambiguationData":[TD([[makeQuery(id+"F25.imprint","IMPRINT",EDGE,{"disambiguationData":[TD([[subQ6,-1.0]])],"derivedFrom":subQ5}),1.0]])]});}
            var Q267;
            {var subQ0=sQuery(id+"F25.wireOp",EDGE,"E514.trimOffspring");var subQ1=sQuery(id+"F25.wireOp",EDGE,"E508.trimOffspring");var subQ2=makeQuery(id+"F25.imprint","INTERSECT",VERTEX,{"derivedFrom":[subQ1,subQ0]});Q267=makeQuery(id+"F25.imprint","IMPRINT",FACE,{"disambiguationData":[TD([[makeQuery(id+"F25.imprint","IMPRINT",EDGE,{"disambiguationData":[TD([[subQ2,-1.0]])],"derivedFrom":subQ1}),-1.0]])]});}
            var Q268;
            {var subQ0=sQuery(id+"F25.wireOp",EDGE,"E514.trimOffspring");var subQ1=sQuery(id+"F25.wireOp",EDGE,"E509.trimOffspring");var subQ2=makeQuery(id+"F25.imprint","INTERSECT",VERTEX,{"derivedFrom":[subQ1,subQ0]});Q268=makeQuery(id+"F25.imprint","IMPRINT",FACE,{"disambiguationData":[TD([[makeQuery(id+"F25.imprint","IMPRINT",EDGE,{"disambiguationData":[TD([[subQ2,-1.0]])],"derivedFrom":subQ1}),-1.0]])]});}
            var Q269;
            {var subQ0=sQuery(id+"F25.wireOp",EDGE,"E515.trimOffspring");var subQ1=sQuery(id+"F25.wireOp",EDGE,"E509.trimOffspring");var subQ2=makeQuery(id+"F25.imprint","INTERSECT",VERTEX,{"derivedFrom":[subQ1,subQ0]});Q269=makeQuery(id+"F25.imprint","IMPRINT",FACE,{"disambiguationData":[TD([[makeQuery(id+"F25.imprint","IMPRINT",EDGE,{"disambiguationData":[TD([[subQ2,-1.0]])],"derivedFrom":subQ1}),-1.0]])]});}
            var Q270;
            {var subQ0=sQuery(id+"F25.wireOp",EDGE,"E515.trimOffspring");var subQ1=sQuery(id+"F25.wireOp",EDGE,"E508.trimOffspring");var subQ2=makeQuery(id+"F25.imprint","INTERSECT",VERTEX,{"derivedFrom":[subQ1,subQ0]});Q270=makeQuery(id+"F25.imprint","IMPRINT",FACE,{"disambiguationData":[TD([[makeQuery(id+"F25.imprint","IMPRINT",EDGE,{"disambiguationData":[TD([[subQ2,-1.0]])],"derivedFrom":subQ1}),-1.0]])]});}
            var Q271;
            {var subQ0=sQuery(id+"F25.wireOp",EDGE,"E263.trimOffspring");Q271=makeQuery(id+"F25.imprint","IMPRINT",FACE,{"disambiguationData":[TD([[makeQuery(id+"F25.imprint","IMPRINT",EDGE,{"derivedFrom":subQ0}),-1.0]])]});}
            var Q272;
            {var subQ0=sQuery(id+"F25.wireOp",EDGE,"E515.trimOffspring");var subQ1=sQuery(id+"F25.wireOp",EDGE,"E508.trimOffspring");var subQ2=makeQuery(id+"F25.imprint","INTERSECT",VERTEX,{"derivedFrom":[subQ1,subQ0]});Q272=makeQuery(id+"F25.imprint","IMPRINT",FACE,{"disambiguationData":[TD([[makeQuery(id+"F25.imprint","IMPRINT",EDGE,{"disambiguationData":[TD([[subQ2,-1.0]])],"derivedFrom":subQ1}),1.0]])]});}
            var Q273;
            {var subQ0=sQuery(id+"F25.wireOp",EDGE,"E263.trimOffspring");Q273=makeQuery(id+"F25.imprint","IMPRINT",FACE,{"disambiguationData":[TD([[makeQuery(id+"F25.imprint","IMPRINT",EDGE,{"derivedFrom":subQ0}),1.0]])]});}
            var Q274;
            {var subQ0=sQuery(id+"F25.wireOp",EDGE,"E514.trimOffspring");var subQ1=sQuery(id+"F25.wireOp",EDGE,"E264.trimOffspring");var subQ2=makeQuery(id+"F25.imprint","INTERSECT",VERTEX,{"derivedFrom":[subQ1,subQ0]});Q274=makeQuery(id+"F25.imprint","IMPRINT",FACE,{"disambiguationData":[TD([[makeQuery(id+"F25.imprint","IMPRINT",EDGE,{"disambiguationData":[TD([[subQ2,-1.0]])],"derivedFrom":subQ1}),-1.0]])]});}
            var Q275;
            {var subQ0=sQuery(id+"F25.wireOp",EDGE,"E515.trimOffspring");var subQ1=sQuery(id+"F25.wireOp",EDGE,"E266.trimOffspring");var subQ2=makeQuery(id+"F25.imprint","INTERSECT",VERTEX,{"derivedFrom":[subQ1,subQ0]});Q275=makeQuery(id+"F25.imprint","IMPRINT",FACE,{"disambiguationData":[TD([[makeQuery(id+"F25.imprint","IMPRINT",EDGE,{"disambiguationData":[TD([[subQ2,-1.0]])],"derivedFrom":subQ1}),-1.0]])]});}
            var Q276;
            {var subQ0=sQuery(id+"F25.wireOp",EDGE,"E515.trimOffspring");var subQ1=sQuery(id+"F25.wireOp",EDGE,"E264.trimOffspring");var subQ2=makeQuery(id+"F25.imprint","INTERSECT",VERTEX,{"derivedFrom":[subQ1,subQ0]});Q276=makeQuery(id+"F25.imprint","IMPRINT",FACE,{"disambiguationData":[TD([[makeQuery(id+"F25.imprint","IMPRINT",EDGE,{"disambiguationData":[TD([[subQ2,-1.0]])],"derivedFrom":subQ1}),-1.0]])]});}
            var Q277;
            {var subQ0=sQuery(id+"F25.wireOp",EDGE,"E516.trimOffspring");var subQ1=sQuery(id+"F25.wireOp",EDGE,"E266.trimOffspring");var subQ2=makeQuery(id+"F25.imprint","INTERSECT",VERTEX,{"derivedFrom":[subQ1,subQ0]});Q277=makeQuery(id+"F25.imprint","IMPRINT",FACE,{"disambiguationData":[TD([[makeQuery(id+"F25.imprint","IMPRINT",EDGE,{"disambiguationData":[TD([[subQ2,-1.0]])],"derivedFrom":subQ1}),-1.0]])]});}
            var Q278;
            {var subQ0=sQuery(id+"F25.wireOp",EDGE,"E516.trimOffspring");var subQ1=sQuery(id+"F25.wireOp",EDGE,"E264.trimOffspring");var subQ2=makeQuery(id+"F25.imprint","INTERSECT",VERTEX,{"derivedFrom":[subQ1,subQ0]});Q278=makeQuery(id+"F25.imprint","IMPRINT",FACE,{"disambiguationData":[TD([[makeQuery(id+"F25.imprint","IMPRINT",EDGE,{"disambiguationData":[TD([[subQ2,-1.0]])],"derivedFrom":subQ1}),-1.0]])]});}
            var Q279;
            {var subQ0=sQuery(id+"F25.wireOp",EDGE,"E532.trimOffspring");var subQ1=sQuery(id+"F25.wireOp",EDGE,"E266.trimOffspring");var subQ2=makeQuery(id+"F25.imprint","INTERSECT",VERTEX,{"derivedFrom":[subQ1,subQ0]});Q279=makeQuery(id+"F25.imprint","IMPRINT",FACE,{"disambiguationData":[TD([[makeQuery(id+"F25.imprint","IMPRINT",EDGE,{"disambiguationData":[TD([[subQ2,-1.0]])],"derivedFrom":subQ1}),-1.0]])]});}
            var Q280;
            {var subQ0=sQuery(id+"F25.wireOp",EDGE,"E532.trimOffspring");var subQ1=sQuery(id+"F25.wireOp",EDGE,"E264.trimOffspring");var subQ2=makeQuery(id+"F25.imprint","INTERSECT",VERTEX,{"derivedFrom":[subQ1,subQ0]});Q280=makeQuery(id+"F25.imprint","IMPRINT",FACE,{"disambiguationData":[TD([[makeQuery(id+"F25.imprint","IMPRINT",EDGE,{"disambiguationData":[TD([[subQ2,-1.0]])],"derivedFrom":subQ1}),-1.0]])]});}
            var Q281;
            {var subQ0=sQuery(id+"F25.wireOp",EDGE,"E527.trimOffspring");var subQ1=sQuery(id+"F25.wireOp",EDGE,"E266.trimOffspring");var subQ2=makeQuery(id+"F25.imprint","INTERSECT",VERTEX,{"derivedFrom":[subQ1,subQ0]});Q281=makeQuery(id+"F25.imprint","IMPRINT",FACE,{"disambiguationData":[TD([[makeQuery(id+"F25.imprint","IMPRINT",EDGE,{"disambiguationData":[TD([[subQ2,-1.0]])],"derivedFrom":subQ1}),-1.0]])]});}
            var Q282;
            {var subQ0=sQuery(id+"F25.wireOp",EDGE,"E527.trimOffspring");var subQ1=sQuery(id+"F25.wireOp",EDGE,"E264.trimOffspring");var subQ2=makeQuery(id+"F25.imprint","INTERSECT",VERTEX,{"derivedFrom":[subQ1,subQ0]});Q282=makeQuery(id+"F25.imprint","IMPRINT",FACE,{"disambiguationData":[TD([[makeQuery(id+"F25.imprint","IMPRINT",EDGE,{"disambiguationData":[TD([[subQ2,-1.0]])],"derivedFrom":subQ1}),-1.0]])]});}
            var Q283;
            {var subQ0=sQuery(id+"F25.wireOp",EDGE,"E533.trimOffspring");var subQ1=sQuery(id+"F25.wireOp",EDGE,"E266.trimOffspring");var subQ2=makeQuery(id+"F25.imprint","INTERSECT",VERTEX,{"derivedFrom":[subQ1,subQ0]});Q283=makeQuery(id+"F25.imprint","IMPRINT",FACE,{"disambiguationData":[TD([[makeQuery(id+"F25.imprint","IMPRINT",EDGE,{"disambiguationData":[TD([[subQ2,-1.0]])],"derivedFrom":subQ1}),-1.0]])]});}
            var Q284;
            {var subQ0=sQuery(id+"F25.wireOp",EDGE,"E533.trimOffspring");var subQ1=sQuery(id+"F25.wireOp",EDGE,"E264.trimOffspring");var subQ2=makeQuery(id+"F25.imprint","INTERSECT",VERTEX,{"derivedFrom":[subQ1,subQ0]});Q284=makeQuery(id+"F25.imprint","IMPRINT",FACE,{"disambiguationData":[TD([[makeQuery(id+"F25.imprint","IMPRINT",EDGE,{"disambiguationData":[TD([[subQ2,-1.0]])],"derivedFrom":subQ1}),-1.0]])]});}
            var Q285;
            {var subQ0=sQuery(id+"F25.wireOp",EDGE,"E538.trimOffspring");var subQ1=sQuery(id+"F25.wireOp",EDGE,"E266.trimOffspring");var subQ2=makeQuery(id+"F25.imprint","INTERSECT",VERTEX,{"derivedFrom":[subQ1,subQ0]});Q285=makeQuery(id+"F25.imprint","IMPRINT",FACE,{"disambiguationData":[TD([[makeQuery(id+"F25.imprint","IMPRINT",EDGE,{"disambiguationData":[TD([[subQ2,-1.0]])],"derivedFrom":subQ1}),-1.0]])]});}
            var Q286;
            {var subQ0=sQuery(id+"F25.wireOp",EDGE,"E542.trimOffspring");var subQ1=sQuery(id+"F25.wireOp",EDGE,"E266.trimOffspring");var subQ2=makeQuery(id+"F25.imprint","INTERSECT",VERTEX,{"derivedFrom":[subQ1,subQ0]});Q286=makeQuery(id+"F25.imprint","IMPRINT",FACE,{"disambiguationData":[TD([[makeQuery(id+"F25.imprint","IMPRINT",EDGE,{"disambiguationData":[TD([[subQ2,1.0]])],"derivedFrom":subQ1}),-1.0]])]});}
            var Q287;
            {var subQ0=sQuery(id+"F25.wireOp",EDGE,"E538.trimOffspring");var subQ1=sQuery(id+"F25.wireOp",EDGE,"E264.trimOffspring");var subQ2=makeQuery(id+"F25.imprint","INTERSECT",VERTEX,{"derivedFrom":[subQ1,subQ0]});Q287=makeQuery(id+"F25.imprint","IMPRINT",FACE,{"disambiguationData":[TD([[makeQuery(id+"F25.imprint","IMPRINT",EDGE,{"disambiguationData":[TD([[subQ2,-1.0]])],"derivedFrom":subQ1}),-1.0]])]});}
            var Q288;
            {var subQ0=sQuery(id+"F25.wireOp",EDGE,"E542.trimOffspring");var subQ1=sQuery(id+"F25.wireOp",EDGE,"E264.trimOffspring");var subQ2=makeQuery(id+"F25.imprint","INTERSECT",VERTEX,{"derivedFrom":[subQ1,subQ0]});Q288=makeQuery(id+"F25.imprint","IMPRINT",FACE,{"disambiguationData":[TD([[makeQuery(id+"F25.imprint","IMPRINT",EDGE,{"disambiguationData":[TD([[subQ2,1.0]])],"derivedFrom":subQ1}),-1.0]])]});}
            var Q289;
            {var subQ0=sQuery(id+"F25.wireOp",EDGE,"E243.top");Q289=makeQuery(id+"F25.imprint","IMPRINT",FACE,{"disambiguationData":[TD([[makeQuery(id+"F25.imprint","IMPRINT",EDGE,{"derivedFrom":subQ0}),1.0]])]});}
            var Q290;
            {var subQ0=sQuery(id+"F25.wireOp",EDGE,"E244.top");Q290=makeQuery(id+"F25.imprint","IMPRINT",FACE,{"disambiguationData":[TD([[makeQuery(id+"F25.imprint","IMPRINT",EDGE,{"derivedFrom":subQ0}),-1.0]])]});}
            var Q291;
            {var subQ0=sQuery(id+"F25.wireOp",EDGE,"E516.trimOffspring");var subQ5=sQuery(id+"F25.wireOp",EDGE,"E265.trimOffspring");var subQ6=makeQuery(id+"F25.imprint","INTERSECT",VERTEX,{"derivedFrom":[subQ5,subQ0]});Q291=makeQuery(id+"F25.imprint","IMPRINT",FACE,{"disambiguationData":[TD([[makeQuery(id+"F25.imprint","IMPRINT",EDGE,{"disambiguationData":[TD([[subQ6,-1.0]])],"derivedFrom":subQ5}),1.0]])]});}
            var Q292;
            {var subQ0=sQuery(id+"F25.wireOp",EDGE,"E243.top");Q292=makeQuery(id+"F25.imprint","IMPRINT",FACE,{"disambiguationData":[TD([[makeQuery(id+"F25.imprint","IMPRINT",EDGE,{"derivedFrom":subQ0}),-1.0]])]});}
            var Q293;
            {var subQ0=sQuery(id+"F25.wireOp",EDGE,"E244.top");Q293=makeQuery(id+"F25.imprint","IMPRINT",FACE,{"disambiguationData":[TD([[makeQuery(id+"F25.imprint","IMPRINT",EDGE,{"derivedFrom":subQ0}),1.0]])]});}
            var Q294;
            {var subQ0=sQuery(id+"F25.wireOp",EDGE,"E574.trimOffspring");var subQ5=sQuery(id+"F25.wireOp",EDGE,"E414.MirrorCS");var subQ6=makeQuery(id+"F25.imprint","INTERSECT",VERTEX,{"derivedFrom":[subQ5,subQ0]});Q294=makeQuery(id+"F25.imprint","IMPRINT",FACE,{"disambiguationData":[TD([[makeQuery(id+"F25.imprint","IMPRINT",EDGE,{"disambiguationData":[TD([[subQ6,-1.0]])],"derivedFrom":subQ5}),-1.0]])]});}
            var Q295;
            {var subQ0=sQuery(id+"F25.wireOp",EDGE,"E245.top");Q295=makeQuery(id+"F25.imprint","IMPRINT",FACE,{"disambiguationData":[TD([[makeQuery(id+"F25.imprint","IMPRINT",EDGE,{"derivedFrom":subQ0}),1.0]])]});}
            var Q296;
            {var subQ0=sQuery(id+"F25.wireOp",EDGE,"E245.top");Q296=makeQuery(id+"F25.imprint","IMPRINT",FACE,{"disambiguationData":[TD([[makeQuery(id+"F25.imprint","IMPRINT",EDGE,{"derivedFrom":subQ0}),-1.0]])]});}
            var Q297;
            {var subQ0=sQuery(id+"F25.wireOp",EDGE,"E246.top");Q297=makeQuery(id+"F25.imprint","IMPRINT",FACE,{"disambiguationData":[TD([[makeQuery(id+"F25.imprint","IMPRINT",EDGE,{"derivedFrom":subQ0}),-1.0]])]});}
            var Q298;
            {var subQ0=sQuery(id+"F25.wireOp",EDGE,"E246.top");Q298=makeQuery(id+"F25.imprint","IMPRINT",FACE,{"disambiguationData":[TD([[makeQuery(id+"F25.imprint","IMPRINT",EDGE,{"derivedFrom":subQ0}),1.0]])]});}
            var Q299;
            {var subQ0=sQuery(id+"F25.wireOp",EDGE,"E533.trimOffspring");var subQ5=sQuery(id+"F25.wireOp",EDGE,"E265.trimOffspring");var subQ6=makeQuery(id+"F25.imprint","INTERSECT",VERTEX,{"derivedFrom":[subQ5,subQ0]});Q299=makeQuery(id+"F25.imprint","IMPRINT",FACE,{"disambiguationData":[TD([[makeQuery(id+"F25.imprint","IMPRINT",EDGE,{"disambiguationData":[TD([[subQ6,-1.0]])],"derivedFrom":subQ5}),1.0]])]});}
            var Q300;
            {var subQ0=sQuery(id+"F25.wireOp",EDGE,"E581.trimOffspring");var subQ5=sQuery(id+"F25.wireOp",EDGE,"E414.MirrorCS");var subQ6=makeQuery(id+"F25.imprint","INTERSECT",VERTEX,{"derivedFrom":[subQ5,subQ0]});Q300=makeQuery(id+"F25.imprint","IMPRINT",FACE,{"disambiguationData":[TD([[makeQuery(id+"F25.imprint","IMPRINT",EDGE,{"disambiguationData":[TD([[subQ6,-1.0]])],"derivedFrom":subQ5}),-1.0]])]});}
            var Q301;
            {var subQ0=sQuery(id+"F25.wireOp",EDGE,"E247.top");Q301=makeQuery(id+"F25.imprint","IMPRINT",FACE,{"disambiguationData":[TD([[makeQuery(id+"F25.imprint","IMPRINT",EDGE,{"derivedFrom":subQ0}),-1.0]])]});}
            var Q302;
            {var subQ0=sQuery(id+"F25.wireOp",EDGE,"E247.top");Q302=makeQuery(id+"F25.imprint","IMPRINT",FACE,{"disambiguationData":[TD([[makeQuery(id+"F25.imprint","IMPRINT",EDGE,{"derivedFrom":subQ0}),1.0]])]});}
            var Q303;
            {var subQ5=sQuery(id+"F25.wireOp",EDGE,"E248.top");Q303=makeQuery(id+"F25.imprint","IMPRINT",FACE,{"disambiguationData":[TD([[makeQuery(id+"F25.imprint","IMPRINT",EDGE,{"derivedFrom":subQ5}),-1.0]])]});}
            var Q304;
            {var subQ0=sQuery(id+"F25.wireOp",EDGE,"E410.MirrorCS");Q304=makeQuery(id+"F25.imprint","IMPRINT",FACE,{"disambiguationData":[TD([[makeQuery(id+"F25.imprint","IMPRINT",EDGE,{"derivedFrom":subQ0}),1.0]])]});}
            var Q305;
            {var subQ0=sQuery(id+"F25.wireOp",EDGE,"E470.MirrorCS");var subQ1=sQuery(id+"F25.wireOp",EDGE,"E428.MirrorCS");var subQ2=makeQuery(id+"F25.imprint","INTERSECT",VERTEX,{"derivedFrom":[subQ1,subQ0]});Q305=makeQuery(id+"F25.imprint","IMPRINT",FACE,{"disambiguationData":[TD([[makeQuery(id+"F25.imprint","IMPRINT",EDGE,{"disambiguationData":[TD([[subQ2,-1.0]])],"derivedFrom":subQ1}),1.0]])]});}
            var Q306;
            {var subQ0=sQuery(id+"F25.wireOp",EDGE,"E452.MirrorCS");var subQ1=sQuery(id+"F25.wireOp",EDGE,"E428.MirrorCS");var subQ2=makeQuery(id+"F25.imprint","INTERSECT",VERTEX,{"derivedFrom":[subQ1,subQ0]});Q306=makeQuery(id+"F25.imprint","IMPRINT",FACE,{"disambiguationData":[TD([[makeQuery(id+"F25.imprint","IMPRINT",EDGE,{"disambiguationData":[TD([[subQ2,1.0]])],"derivedFrom":subQ1}),1.0]])]});}
            var Q307;
            {var subQ3=sQuery(id+"F25.wireOp",EDGE,"E471.MirrorCS");Q307=makeQuery(id+"F25.imprint","IMPRINT",FACE,{"disambiguationData":[TD([[makeQuery(id+"F25.imprint","IMPRINT",EDGE,{"derivedFrom":subQ3}),1.0]])]});}
            var Q308;
            {var subQ3=sQuery(id+"F25.wireOp",EDGE,"E471.MirrorCS");Q308=makeQuery(id+"F25.imprint","IMPRINT",FACE,{"disambiguationData":[TD([[makeQuery(id+"F25.imprint","IMPRINT",EDGE,{"derivedFrom":subQ3}),-1.0]])]});}
            var Q309;
            {var subQ0=sQuery(id+"F25.wireOp",EDGE,"E460.MirrorCS");var subQ1=sQuery(id+"F25.wireOp",EDGE,"E428.MirrorCS");var subQ2=makeQuery(id+"F25.imprint","INTERSECT",VERTEX,{"derivedFrom":[subQ1,subQ0]});Q309=makeQuery(id+"F25.imprint","IMPRINT",FACE,{"disambiguationData":[TD([[makeQuery(id+"F25.imprint","IMPRINT",EDGE,{"disambiguationData":[TD([[subQ2,1.0]])],"derivedFrom":subQ1}),1.0]])]});}
            var Q310;
            {var subQ0=sQuery(id+"F25.wireOp",EDGE,"E432.MirrorCS");Q310=makeQuery(id+"F25.imprint","IMPRINT",FACE,{"disambiguationData":[TD([[makeQuery(id+"F25.imprint","IMPRINT",EDGE,{"derivedFrom":subQ0}),-1.0]])]});}
            var Q311;
            {var subQ0=sQuery(id+"F25.wireOp",EDGE,"E453.MirrorCS");Q311=makeQuery(id+"F25.imprint","IMPRINT",FACE,{"disambiguationData":[TD([[makeQuery(id+"F25.imprint","IMPRINT",EDGE,{"derivedFrom":subQ0}),-1.0]])]});}
            var Q312;
            {var subQ0=sQuery(id+"F25.wireOp",EDGE,"E452.MirrorCS");var subQ1=sQuery(id+"F25.wireOp",EDGE,"E425.MirrorCS");var subQ2=makeQuery(id+"F25.imprint","INTERSECT",VERTEX,{"derivedFrom":[subQ1,subQ0]});Q312=makeQuery(id+"F25.imprint","IMPRINT",FACE,{"disambiguationData":[TD([[makeQuery(id+"F25.imprint","IMPRINT",EDGE,{"disambiguationData":[TD([[subQ2,1.0]])],"derivedFrom":subQ1}),-1.0]])]});}
            var Q313;
            {var subQ0=sQuery(id+"F25.wireOp",EDGE,"E430.MirrorCS");Q313=makeQuery(id+"F25.imprint","IMPRINT",FACE,{"disambiguationData":[TD([[makeQuery(id+"F25.imprint","IMPRINT",EDGE,{"derivedFrom":subQ0}),1.0]])]});}
            var Q314;
            {var subQ0=sQuery(id+"F25.wireOp",EDGE,"E430.MirrorCS");Q314=makeQuery(id+"F25.imprint","IMPRINT",FACE,{"disambiguationData":[TD([[makeQuery(id+"F25.imprint","IMPRINT",EDGE,{"derivedFrom":subQ0}),-1.0]])]});}
            var Q315;
            {var subQ0=sQuery(id+"F25.wireOp",EDGE,"E442.MirrorCS");var subQ1=sQuery(id+"F25.wireOp",EDGE,"E425.MirrorCS");var subQ2=makeQuery(id+"F25.imprint","INTERSECT",VERTEX,{"derivedFrom":[subQ1,subQ0]});Q315=makeQuery(id+"F25.imprint","IMPRINT",FACE,{"disambiguationData":[TD([[makeQuery(id+"F25.imprint","IMPRINT",EDGE,{"disambiguationData":[TD([[subQ2,-1.0]])],"derivedFrom":subQ1}),-1.0]])]});}
            var Q316;
            {var subQ0=sQuery(id+"F25.wireOp",EDGE,"E464.MirrorCS");var subQ1=sQuery(id+"F25.wireOp",EDGE,"E428.MirrorCS");var subQ2=makeQuery(id+"F25.imprint","INTERSECT",VERTEX,{"derivedFrom":[subQ1,subQ0]});Q316=makeQuery(id+"F25.imprint","IMPRINT",FACE,{"disambiguationData":[TD([[makeQuery(id+"F25.imprint","IMPRINT",EDGE,{"disambiguationData":[TD([[subQ2,1.0]])],"derivedFrom":subQ1}),1.0]])]});}
            var Q317;
            {var subQ0=sQuery(id+"F25.wireOp",EDGE,"E460.MirrorCS");var subQ1=sQuery(id+"F25.wireOp",EDGE,"E428.MirrorCS");var subQ2=makeQuery(id+"F25.imprint","INTERSECT",VERTEX,{"derivedFrom":[subQ1,subQ0]});Q317=makeQuery(id+"F25.imprint","IMPRINT",FACE,{"disambiguationData":[TD([[makeQuery(id+"F25.imprint","IMPRINT",EDGE,{"disambiguationData":[TD([[subQ2,-1.0]])],"derivedFrom":subQ1}),1.0]])]});}
            var Q318;
            {var subQ0=sQuery(id+"F25.wireOp",EDGE,"E460.MirrorCS");var subQ1=sQuery(id+"F25.wireOp",EDGE,"E425.MirrorCS");var subQ2=makeQuery(id+"F25.imprint","INTERSECT",VERTEX,{"derivedFrom":[subQ1,subQ0]});Q318=makeQuery(id+"F25.imprint","IMPRINT",FACE,{"disambiguationData":[TD([[makeQuery(id+"F25.imprint","IMPRINT",EDGE,{"disambiguationData":[TD([[subQ2,-1.0]])],"derivedFrom":subQ1}),-1.0]])]});}
            var Q319;
            {var subQ0=sQuery(id+"F25.wireOp",EDGE,"E464.MirrorCS");var subQ1=sQuery(id+"F25.wireOp",EDGE,"E425.MirrorCS");var subQ2=makeQuery(id+"F25.imprint","INTERSECT",VERTEX,{"derivedFrom":[subQ1,subQ0]});Q319=makeQuery(id+"F25.imprint","IMPRINT",FACE,{"disambiguationData":[TD([[makeQuery(id+"F25.imprint","IMPRINT",EDGE,{"disambiguationData":[TD([[subQ2,1.0]])],"derivedFrom":subQ1}),-1.0]])]});}
            var Q320;
            {var subQ0=sQuery(id+"F25.wireOp",EDGE,"E555.trimOffspring");var subQ5=sQuery(id+"F25.wireOp",EDGE,"E439.MirrorCS");var subQ6=makeQuery(id+"F25.imprint","INTERSECT",VERTEX,{"derivedFrom":[subQ5,subQ0]});Q320=makeQuery(id+"F25.imprint","IMPRINT",FACE,{"disambiguationData":[TD([[makeQuery(id+"F25.imprint","IMPRINT",EDGE,{"disambiguationData":[TD([[subQ6,-1.0]])],"derivedFrom":subQ5}),-1.0]])]});}
            var Q321;
            {var subQ0=sQuery(id+"F25.wireOp",EDGE,"E555.trimOffspring");var subQ1=sQuery(id+"F25.wireOp",EDGE,"E429.MirrorCS");var subQ2=makeQuery(id+"F25.imprint","INTERSECT",VERTEX,{"derivedFrom":[subQ1,subQ0]});Q321=makeQuery(id+"F25.imprint","IMPRINT",FACE,{"disambiguationData":[TD([[makeQuery(id+"F25.imprint","IMPRINT",EDGE,{"disambiguationData":[TD([[subQ2,-1.0]])],"derivedFrom":subQ1}),-1.0]])]});}
            var Q322;
            {var subQ0=sQuery(id+"F25.wireOp",EDGE,"E555.trimOffspring");var subQ1=sQuery(id+"F25.wireOp",EDGE,"E429.MirrorCS");var subQ2=makeQuery(id+"F25.imprint","INTERSECT",VERTEX,{"derivedFrom":[subQ1,subQ0]});Q322=makeQuery(id+"F25.imprint","IMPRINT",FACE,{"disambiguationData":[TD([[makeQuery(id+"F25.imprint","IMPRINT",EDGE,{"disambiguationData":[TD([[subQ2,-1.0]])],"derivedFrom":subQ1}),1.0]])]});}
            var Q323;
            {var subQ0=sQuery(id+"F25.wireOp",EDGE,"E552.trimOffspring");var subQ5=sQuery(id+"F25.wireOp",EDGE,"E439.MirrorCS");var subQ6=makeQuery(id+"F25.imprint","INTERSECT",VERTEX,{"derivedFrom":[subQ5,subQ0]});Q323=makeQuery(id+"F25.imprint","IMPRINT",FACE,{"disambiguationData":[TD([[makeQuery(id+"F25.imprint","IMPRINT",EDGE,{"disambiguationData":[TD([[subQ6,-1.0]])],"derivedFrom":subQ5}),-1.0]])]});}
            var Q324;
            {var subQ0=sQuery(id+"F25.wireOp",EDGE,"E554.trimOffspring");var subQ1=sQuery(id+"F25.wireOp",EDGE,"E429.MirrorCS");var subQ2=makeQuery(id+"F25.imprint","INTERSECT",VERTEX,{"derivedFrom":[subQ1,subQ0]});Q324=makeQuery(id+"F25.imprint","IMPRINT",FACE,{"disambiguationData":[TD([[makeQuery(id+"F25.imprint","IMPRINT",EDGE,{"disambiguationData":[TD([[subQ2,1.0]])],"derivedFrom":subQ1}),-1.0]])]});}
            var Q325;
            {var subQ0=sQuery(id+"F25.wireOp",EDGE,"E545.trimOffspring");var subQ1=sQuery(id+"F25.wireOp",EDGE,"E424.MirrorCS");var subQ2=makeQuery(id+"F25.imprint","INTERSECT",VERTEX,{"derivedFrom":[subQ1,subQ0]});Q325=makeQuery(id+"F25.imprint","IMPRINT",FACE,{"disambiguationData":[TD([[makeQuery(id+"F25.imprint","IMPRINT",EDGE,{"disambiguationData":[TD([[subQ2,1.0]])],"derivedFrom":subQ1}),1.0]])]});}
            var Q326;
            {var subQ0=sQuery(id+"F25.wireOp",EDGE,"E545.trimOffspring");var subQ1=sQuery(id+"F25.wireOp",EDGE,"E429.MirrorCS");var subQ2=makeQuery(id+"F25.imprint","INTERSECT",VERTEX,{"derivedFrom":[subQ1,subQ0]});Q326=makeQuery(id+"F25.imprint","IMPRINT",FACE,{"disambiguationData":[TD([[makeQuery(id+"F25.imprint","IMPRINT",EDGE,{"disambiguationData":[TD([[subQ2,1.0]])],"derivedFrom":subQ1}),-1.0]])]});}
            var Q327;
            {var subQ0=sQuery(id+"F25.wireOp",EDGE,"E545.trimOffspring");var subQ1=sQuery(id+"F25.wireOp",EDGE,"E424.MirrorCS");var subQ2=makeQuery(id+"F25.imprint","INTERSECT",VERTEX,{"derivedFrom":[subQ1,subQ0]});Q327=makeQuery(id+"F25.imprint","IMPRINT",FACE,{"disambiguationData":[TD([[makeQuery(id+"F25.imprint","IMPRINT",EDGE,{"disambiguationData":[TD([[subQ2,-1.0]])],"derivedFrom":subQ1}),1.0]])]});}
            var Q328;
            {var subQ0=sQuery(id+"F25.wireOp",EDGE,"E545.trimOffspring");var subQ1=sQuery(id+"F25.wireOp",EDGE,"E429.MirrorCS");var subQ2=makeQuery(id+"F25.imprint","INTERSECT",VERTEX,{"derivedFrom":[subQ1,subQ0]});Q328=makeQuery(id+"F25.imprint","IMPRINT",FACE,{"disambiguationData":[TD([[makeQuery(id+"F25.imprint","IMPRINT",EDGE,{"disambiguationData":[TD([[subQ2,-1.0]])],"derivedFrom":subQ1}),-1.0]])]});}
            var Q329;
            {var subQ0=sQuery(id+"F25.wireOp",EDGE,"E553.trimOffspring");var subQ1=sQuery(id+"F25.wireOp",EDGE,"E424.MirrorCS");var subQ2=makeQuery(id+"F25.imprint","INTERSECT",VERTEX,{"derivedFrom":[subQ1,subQ0]});Q329=makeQuery(id+"F25.imprint","IMPRINT",FACE,{"disambiguationData":[TD([[makeQuery(id+"F25.imprint","IMPRINT",EDGE,{"disambiguationData":[TD([[subQ2,-1.0]])],"derivedFrom":subQ1}),1.0]])]});}
            var Q330;
            {var subQ3=sQuery(id+"F25.wireOp",EDGE,"E553.trimOffspring");var subQ5=sQuery(id+"F25.wireOp",EDGE,"E439.MirrorCS");var subQ6=makeQuery(id+"F25.imprint","INTERSECT",VERTEX,{"derivedFrom":[subQ5,subQ3]});Q330=makeQuery(id+"F25.imprint","IMPRINT",FACE,{"disambiguationData":[TD([[makeQuery(id+"F25.imprint","IMPRINT",EDGE,{"disambiguationData":[TD([[subQ6,-1.0]])],"derivedFrom":subQ5}),1.0]])]});}
            var Q331;
            {var subQ0=sQuery(id+"F25.wireOp",EDGE,"E460.MirrorCS");var subQ1=sQuery(id+"F25.wireOp",EDGE,"E424.MirrorCS");var subQ2=makeQuery(id+"F25.imprint","INTERSECT",VERTEX,{"derivedFrom":[subQ1,subQ0]});Q331=makeQuery(id+"F25.imprint","IMPRINT",FACE,{"disambiguationData":[TD([[makeQuery(id+"F25.imprint","IMPRINT",EDGE,{"disambiguationData":[TD([[subQ2,-1.0]])],"derivedFrom":subQ1}),1.0]])]});}
            var Q332;
            {var subQ3=sQuery(id+"F25.wireOp",EDGE,"E460.MirrorCS");var subQ5=sQuery(id+"F25.wireOp",EDGE,"E439.MirrorCS");var subQ6=makeQuery(id+"F25.imprint","INTERSECT",VERTEX,{"derivedFrom":[subQ5,subQ3]});Q332=makeQuery(id+"F25.imprint","IMPRINT",FACE,{"disambiguationData":[TD([[makeQuery(id+"F25.imprint","IMPRINT",EDGE,{"disambiguationData":[TD([[subQ6,-1.0]])],"derivedFrom":subQ5}),1.0]])]});}
            var Q333;
            {var subQ0=sQuery(id+"F25.wireOp",EDGE,"E464.MirrorCS");var subQ1=sQuery(id+"F25.wireOp",EDGE,"E424.MirrorCS");var subQ2=makeQuery(id+"F25.imprint","INTERSECT",VERTEX,{"derivedFrom":[subQ1,subQ0]});Q333=makeQuery(id+"F25.imprint","IMPRINT",FACE,{"disambiguationData":[TD([[makeQuery(id+"F25.imprint","IMPRINT",EDGE,{"disambiguationData":[TD([[subQ2,1.0]])],"derivedFrom":subQ1}),1.0]])]});}
            var Q334;
            {var subQ3=sQuery(id+"F25.wireOp",EDGE,"E464.MirrorCS");var subQ5=sQuery(id+"F25.wireOp",EDGE,"E439.MirrorCS");var subQ6=makeQuery(id+"F25.imprint","INTERSECT",VERTEX,{"derivedFrom":[subQ5,subQ3]});Q334=makeQuery(id+"F25.imprint","IMPRINT",FACE,{"disambiguationData":[TD([[makeQuery(id+"F25.imprint","IMPRINT",EDGE,{"disambiguationData":[TD([[subQ6,1.0]])],"derivedFrom":subQ5}),1.0]])]});}
            var Q335;
            {var subQ0=sQuery(id+"F25.wireOp",EDGE,"E555.trimOffspring");var subQ1=sQuery(id+"F25.wireOp",EDGE,"E445.MirrorCS");var subQ2=makeQuery(id+"F25.imprint","INTERSECT",VERTEX,{"derivedFrom":[subQ1,subQ0]});Q335=makeQuery(id+"F25.imprint","IMPRINT",FACE,{"disambiguationData":[TD([[makeQuery(id+"F25.imprint","IMPRINT",EDGE,{"disambiguationData":[TD([[subQ2,-1.0]])],"derivedFrom":subQ1}),1.0]])]});}
            var Q336;
            {var subQ0=sQuery(id+"F25.wireOp",EDGE,"E564.trimOffspring");var subQ1=sQuery(id+"F25.wireOp",EDGE,"E445.MirrorCS");var subQ2=makeQuery(id+"F25.imprint","INTERSECT",VERTEX,{"derivedFrom":[subQ1,subQ0]});Q336=makeQuery(id+"F25.imprint","IMPRINT",FACE,{"disambiguationData":[TD([[makeQuery(id+"F25.imprint","IMPRINT",EDGE,{"disambiguationData":[TD([[subQ2,1.0]])],"derivedFrom":subQ1}),1.0]])]});}
            var Q337;
            {var subQ0=sQuery(id+"F25.wireOp",EDGE,"E547.trimOffspring");var subQ1=sQuery(id+"F25.wireOp",EDGE,"E445.MirrorCS");var subQ2=makeQuery(id+"F25.imprint","INTERSECT",VERTEX,{"derivedFrom":[subQ1,subQ0]});Q337=makeQuery(id+"F25.imprint","IMPRINT",FACE,{"disambiguationData":[TD([[makeQuery(id+"F25.imprint","IMPRINT",EDGE,{"disambiguationData":[TD([[subQ2,1.0]])],"derivedFrom":subQ1}),1.0]])]});}
            var Q338;
            {var subQ3=sQuery(id+"F25.wireOp",EDGE,"E563.trimOffspring");Q338=makeQuery(id+"F25.imprint","IMPRINT",FACE,{"disambiguationData":[TD([[makeQuery(id+"F25.imprint","IMPRINT",EDGE,{"derivedFrom":subQ3}),1.0]])]});}
            var Q339;
            {var subQ3=sQuery(id+"F25.wireOp",EDGE,"E563.trimOffspring");Q339=makeQuery(id+"F25.imprint","IMPRINT",FACE,{"disambiguationData":[TD([[makeQuery(id+"F25.imprint","IMPRINT",EDGE,{"derivedFrom":subQ3}),-1.0]])]});}
            var Q340;
            {var subQ3=sQuery(id+"F25.wireOp",EDGE,"E560.trimOffspring");var subQ5=sQuery(id+"F25.wireOp",EDGE,"E434.MirrorCS");var subQ6=makeQuery(id+"F25.imprint","INTERSECT",VERTEX,{"derivedFrom":[subQ5,subQ3]});Q340=makeQuery(id+"F25.imprint","IMPRINT",FACE,{"disambiguationData":[TD([[makeQuery(id+"F25.imprint","IMPRINT",EDGE,{"disambiguationData":[TD([[subQ6,-1.0]])],"derivedFrom":subQ5}),-1.0]])]});}
            var Q341;
            {var subQ3=sQuery(id+"F25.wireOp",EDGE,"E559.trimOffspring");var subQ5=sQuery(id+"F25.wireOp",EDGE,"E434.MirrorCS");var subQ6=makeQuery(id+"F25.imprint","INTERSECT",VERTEX,{"derivedFrom":[subQ5,subQ3]});Q341=makeQuery(id+"F25.imprint","IMPRINT",FACE,{"disambiguationData":[TD([[makeQuery(id+"F25.imprint","IMPRINT",EDGE,{"disambiguationData":[TD([[subQ6,1.0]])],"derivedFrom":subQ5}),-1.0]])]});}
            var Q342;
            {var subQ0=sQuery(id+"F25.wireOp",EDGE,"E559.trimOffspring");var subQ1=sQuery(id+"F25.wireOp",EDGE,"E443.MirrorCS");var subQ2=makeQuery(id+"F25.imprint","INTERSECT",VERTEX,{"derivedFrom":[subQ1,subQ0]});Q342=makeQuery(id+"F25.imprint","IMPRINT",FACE,{"disambiguationData":[TD([[makeQuery(id+"F25.imprint","IMPRINT",EDGE,{"disambiguationData":[TD([[subQ2,1.0]])],"derivedFrom":subQ1}),-1.0]])]});}
            var Q343;
            {var subQ0=sQuery(id+"F25.wireOp",EDGE,"E559.trimOffspring");var subQ1=sQuery(id+"F25.wireOp",EDGE,"E443.MirrorCS");var subQ2=makeQuery(id+"F25.imprint","INTERSECT",VERTEX,{"derivedFrom":[subQ1,subQ0]});Q343=makeQuery(id+"F25.imprint","IMPRINT",FACE,{"disambiguationData":[TD([[makeQuery(id+"F25.imprint","IMPRINT",EDGE,{"disambiguationData":[TD([[subQ2,1.0]])],"derivedFrom":subQ1}),1.0]])]});}
            var Q344;
            {var subQ0=sQuery(id+"F25.wireOp",EDGE,"E571.trimOffspring");var subQ1=sQuery(id+"F25.wireOp",EDGE,"E559.trimOffspring");var subQ2=makeQuery(id+"F25.imprint","INTERSECT",VERTEX,{"derivedFrom":[subQ1,subQ0]});Q344=makeQuery(id+"F25.imprint","IMPRINT",FACE,{"disambiguationData":[TD([[makeQuery(id+"F25.imprint","IMPRINT",EDGE,{"disambiguationData":[TD([[subQ2,-1.0]])],"derivedFrom":subQ1}),1.0]])]});}
            var Q345;
            {var subQ0=sQuery(id+"F25.wireOp",EDGE,"E583.trimOffspring");var subQ1=sQuery(id+"F25.wireOp",EDGE,"E559.trimOffspring");var subQ2=makeQuery(id+"F25.imprint","INTERSECT",VERTEX,{"derivedFrom":[subQ1,subQ0]});Q345=makeQuery(id+"F25.imprint","IMPRINT",FACE,{"disambiguationData":[TD([[makeQuery(id+"F25.imprint","IMPRINT",EDGE,{"disambiguationData":[TD([[subQ2,1.0]])],"derivedFrom":subQ1}),1.0]])]});}
            var Q346;
            {var subQ0=sQuery(id+"F25.wireOp",EDGE,"E583.trimOffspring");var subQ1=sQuery(id+"F25.wireOp",EDGE,"E560.trimOffspring");var subQ2=makeQuery(id+"F25.imprint","INTERSECT",VERTEX,{"derivedFrom":[subQ1,subQ0]});Q346=makeQuery(id+"F25.imprint","IMPRINT",FACE,{"disambiguationData":[TD([[makeQuery(id+"F25.imprint","IMPRINT",EDGE,{"disambiguationData":[TD([[subQ2,1.0]])],"derivedFrom":subQ1}),-1.0]])]});}
            var Q347;
            {var subQ0=sQuery(id+"F25.wireOp",EDGE,"E583.trimOffspring");var subQ1=sQuery(id+"F25.wireOp",EDGE,"E560.trimOffspring");var subQ2=makeQuery(id+"F25.imprint","INTERSECT",VERTEX,{"derivedFrom":[subQ1,subQ0]});Q347=makeQuery(id+"F25.imprint","IMPRINT",FACE,{"disambiguationData":[TD([[makeQuery(id+"F25.imprint","IMPRINT",EDGE,{"disambiguationData":[TD([[subQ2,1.0]])],"derivedFrom":subQ1}),1.0]])]});}
            var Q348;
            {var subQ0=sQuery(id+"F25.wireOp",EDGE,"E572.trimOffspring");var subQ1=sQuery(id+"F25.wireOp",EDGE,"E568.trimOffspring");var subQ2=makeQuery(id+"F25.imprint","INTERSECT",VERTEX,{"derivedFrom":[subQ1,subQ0]});Q348=makeQuery(id+"F25.imprint","IMPRINT",FACE,{"disambiguationData":[TD([[makeQuery(id+"F25.imprint","IMPRINT",EDGE,{"disambiguationData":[TD([[subQ2,-1.0]])],"derivedFrom":subQ1}),1.0]])]});}
            var Q349;
            {var subQ0=sQuery(id+"F25.wireOp",EDGE,"E583.trimOffspring");var subQ1=sQuery(id+"F25.wireOp",EDGE,"E568.trimOffspring");var subQ2=makeQuery(id+"F25.imprint","INTERSECT",VERTEX,{"derivedFrom":[subQ1,subQ0]});Q349=makeQuery(id+"F25.imprint","IMPRINT",FACE,{"disambiguationData":[TD([[makeQuery(id+"F25.imprint","IMPRINT",EDGE,{"disambiguationData":[TD([[subQ2,-1.0]])],"derivedFrom":subQ1}),1.0]])]});}
            var Q350;
            {var subQ0=sQuery(id+"F25.wireOp",EDGE,"E596.trimOffspring");var subQ1=sQuery(id+"F25.wireOp",EDGE,"E568.trimOffspring");var subQ2=makeQuery(id+"F25.imprint","INTERSECT",VERTEX,{"derivedFrom":[subQ1,subQ0]});Q350=makeQuery(id+"F25.imprint","IMPRINT",FACE,{"disambiguationData":[TD([[makeQuery(id+"F25.imprint","IMPRINT",EDGE,{"disambiguationData":[TD([[subQ2,-1.0]])],"derivedFrom":subQ1}),1.0]])]});}
            var Q351;
            {var subQ0=sQuery(id+"F25.wireOp",EDGE,"E598.trimOffspring");var subQ1=sQuery(id+"F25.wireOp",EDGE,"E568.trimOffspring");var subQ2=makeQuery(id+"F25.imprint","INTERSECT",VERTEX,{"derivedFrom":[subQ1,subQ0]});Q351=makeQuery(id+"F25.imprint","IMPRINT",FACE,{"disambiguationData":[TD([[makeQuery(id+"F25.imprint","IMPRINT",EDGE,{"disambiguationData":[TD([[subQ2,-1.0]])],"derivedFrom":subQ1}),1.0]])]});}
            var Q352;
            {var subQ1=sQuery(id+"F25.wireOp",EDGE,"E481.trimOffspring");var subQ3=sQuery(id+"F25.wireOp",EDGE,"E567.trimOffspring");var subQ4=makeQuery(id+"F25.imprint","INTERSECT",VERTEX,{"derivedFrom":[subQ1,subQ3]});Q352=makeQuery(id+"F25.imprint","IMPRINT",FACE,{"disambiguationData":[TD([[makeQuery(id+"F25.imprint","IMPRINT",EDGE,{"disambiguationData":[TD([[subQ4,1.0]])],"derivedFrom":subQ3}),-1.0]])]});}
            var Q353;
            {var subQ0=sQuery(id+"F25.wireOp",EDGE,"E608.trimOffspring");var subQ1=sQuery(id+"F25.wireOp",EDGE,"E423.MirrorCS");var subQ2=makeQuery(id+"F25.imprint","INTERSECT",VERTEX,{"derivedFrom":[subQ1,subQ0]});Q353=makeQuery(id+"F25.imprint","IMPRINT",FACE,{"disambiguationData":[TD([[makeQuery(id+"F25.imprint","IMPRINT",EDGE,{"disambiguationData":[TD([[subQ2,-1.0]])],"derivedFrom":subQ1}),-1.0]])]});}
            var Q354;
            {var subQ0=sQuery(id+"F25.wireOp",EDGE,"E608.trimOffspring");var subQ1=sQuery(id+"F25.wireOp",EDGE,"E483.trimOffspring");var subQ2=makeQuery(id+"F25.imprint","INTERSECT",VERTEX,{"derivedFrom":[subQ1,subQ0]});Q354=makeQuery(id+"F25.imprint","IMPRINT",FACE,{"disambiguationData":[TD([[makeQuery(id+"F25.imprint","IMPRINT",EDGE,{"disambiguationData":[TD([[subQ2,-1.0]])],"derivedFrom":subQ1}),-1.0]])]});}
            var Q355;
            {var subQ3=sQuery(id+"F25.wireOp",EDGE,"E599.trimOffspring");var subQ5=sQuery(id+"F25.wireOp",EDGE,"E484.trimOffspring");var subQ6=makeQuery(id+"F25.imprint","INTERSECT",VERTEX,{"derivedFrom":[subQ5,subQ3]});Q355=makeQuery(id+"F25.imprint","IMPRINT",FACE,{"disambiguationData":[TD([[makeQuery(id+"F25.imprint","IMPRINT",EDGE,{"disambiguationData":[TD([[subQ6,-1.0]])],"derivedFrom":subQ5}),1.0]])]});}
            var Q356;
            {var subQ0=sQuery(id+"F25.wireOp",EDGE,"E570.trimOffspring");var subQ5=sQuery(id+"F25.wireOp",EDGE,"E484.trimOffspring");var subQ6=makeQuery(id+"F25.imprint","INTERSECT",VERTEX,{"derivedFrom":[subQ5,subQ0]});Q356=makeQuery(id+"F25.imprint","IMPRINT",FACE,{"disambiguationData":[TD([[makeQuery(id+"F25.imprint","IMPRINT",EDGE,{"disambiguationData":[TD([[subQ6,-1.0]])],"derivedFrom":subQ5}),1.0]])]});}
            var Q357;
            {var subQ0=sQuery(id+"F25.wireOp",EDGE,"E565.trimOffspring");var subQ1=sQuery(id+"F25.wireOp",EDGE,"E483.trimOffspring");var subQ2=makeQuery(id+"F25.imprint","INTERSECT",VERTEX,{"derivedFrom":[subQ1,subQ0]});Q357=makeQuery(id+"F25.imprint","IMPRINT",FACE,{"disambiguationData":[TD([[makeQuery(id+"F25.imprint","IMPRINT",EDGE,{"disambiguationData":[TD([[subQ2,1.0]])],"derivedFrom":subQ1}),-1.0]])]});}
            var Q358;
            {var subQ0=sQuery(id+"F25.wireOp",EDGE,"E565.trimOffspring");var subQ5=sQuery(id+"F25.wireOp",EDGE,"E484.trimOffspring");var subQ6=makeQuery(id+"F25.imprint","INTERSECT",VERTEX,{"derivedFrom":[subQ5,subQ0]});Q358=makeQuery(id+"F25.imprint","IMPRINT",FACE,{"disambiguationData":[TD([[makeQuery(id+"F25.imprint","IMPRINT",EDGE,{"disambiguationData":[TD([[subQ6,1.0]])],"derivedFrom":subQ5}),-1.0]])]});}
            var Q359;
            {var subQ0=sQuery(id+"F25.wireOp",EDGE,"E570.trimOffspring");var subQ5=sQuery(id+"F25.wireOp",EDGE,"E484.trimOffspring");var subQ6=makeQuery(id+"F25.imprint","INTERSECT",VERTEX,{"derivedFrom":[subQ5,subQ0]});Q359=makeQuery(id+"F25.imprint","IMPRINT",FACE,{"disambiguationData":[TD([[makeQuery(id+"F25.imprint","IMPRINT",EDGE,{"disambiguationData":[TD([[subQ6,-1.0]])],"derivedFrom":subQ5}),1.0]])]});}
            var Q360;
            {var subQ0=sQuery(id+"F25.wireOp",EDGE,"E565.trimOffspring");var subQ1=sQuery(id+"F25.wireOp",EDGE,"E483.trimOffspring");var subQ2=makeQuery(id+"F25.imprint","INTERSECT",VERTEX,{"derivedFrom":[subQ1,subQ0]});Q360=makeQuery(id+"F25.imprint","IMPRINT",FACE,{"disambiguationData":[TD([[makeQuery(id+"F25.imprint","IMPRINT",EDGE,{"disambiguationData":[TD([[subQ2,1.0]])],"derivedFrom":subQ1}),-1.0]])]});}
            var Q361;
            {var subQ0=sQuery(id+"F25.wireOp",EDGE,"E598.trimOffspring");var subQ1=sQuery(id+"F25.wireOp",EDGE,"E568.trimOffspring");var subQ2=makeQuery(id+"F25.imprint","INTERSECT",VERTEX,{"derivedFrom":[subQ1,subQ0]});Q361=makeQuery(id+"F25.imprint","IMPRINT",FACE,{"disambiguationData":[TD([[makeQuery(id+"F25.imprint","IMPRINT",EDGE,{"disambiguationData":[TD([[subQ2,-1.0]])],"derivedFrom":subQ1}),-1.0]])]});}
            var Q362;
            {var subQ0=sQuery(id+"F25.wireOp",EDGE,"E596.trimOffspring");var subQ1=sQuery(id+"F25.wireOp",EDGE,"E568.trimOffspring");var subQ2=makeQuery(id+"F25.imprint","INTERSECT",VERTEX,{"derivedFrom":[subQ1,subQ0]});Q362=makeQuery(id+"F25.imprint","IMPRINT",FACE,{"disambiguationData":[TD([[makeQuery(id+"F25.imprint","IMPRINT",EDGE,{"disambiguationData":[TD([[subQ2,-1.0]])],"derivedFrom":subQ1}),-1.0]])]});}
            var Q363;
            {var subQ0=sQuery(id+"F25.wireOp",EDGE,"E577.trimOffspring");var subQ1=sQuery(id+"F25.wireOp",EDGE,"E454.MirrorCS");var subQ2=makeQuery(id+"F25.imprint","INTERSECT",VERTEX,{"derivedFrom":[subQ1,subQ0]});Q363=makeQuery(id+"F25.imprint","IMPRINT",FACE,{"disambiguationData":[TD([[makeQuery(id+"F25.imprint","IMPRINT",EDGE,{"disambiguationData":[TD([[subQ2,-1.0]])],"derivedFrom":subQ1}),1.0]])]});}
            var Q364;
            {var subQ0=sQuery(id+"F25.wireOp",EDGE,"E577.trimOffspring");var subQ1=sQuery(id+"F25.wireOp",EDGE,"E456.MirrorCS");var subQ2=makeQuery(id+"F25.imprint","INTERSECT",VERTEX,{"derivedFrom":[subQ1,subQ0]});Q364=makeQuery(id+"F25.imprint","IMPRINT",FACE,{"disambiguationData":[TD([[makeQuery(id+"F25.imprint","IMPRINT",EDGE,{"disambiguationData":[TD([[subQ2,-1.0]])],"derivedFrom":subQ1}),-1.0]])]});}
            var Q365;
            {var subQ0=sQuery(id+"F25.wireOp",EDGE,"E596.trimOffspring");var subQ1=sQuery(id+"F25.wireOp",EDGE,"E582.trimOffspring");var subQ2=makeQuery(id+"F25.imprint","INTERSECT",VERTEX,{"derivedFrom":[subQ1,subQ0]});Q365=makeQuery(id+"F25.imprint","IMPRINT",FACE,{"disambiguationData":[TD([[makeQuery(id+"F25.imprint","IMPRINT",EDGE,{"disambiguationData":[TD([[subQ2,-1.0]])],"derivedFrom":subQ1}),-1.0]])]});}
            var Q366;
            {var subQ0=sQuery(id+"F25.wireOp",EDGE,"E596.trimOffspring");var subQ1=sQuery(id+"F25.wireOp",EDGE,"E576.trimOffspring");var subQ2=makeQuery(id+"F25.imprint","INTERSECT",VERTEX,{"derivedFrom":[subQ1,subQ0]});Q366=makeQuery(id+"F25.imprint","IMPRINT",FACE,{"disambiguationData":[TD([[makeQuery(id+"F25.imprint","IMPRINT",EDGE,{"disambiguationData":[TD([[subQ2,-1.0]])],"derivedFrom":subQ1}),1.0]])]});}
            var Q367;
            {var subQ0=sQuery(id+"F25.wireOp",EDGE,"E598.trimOffspring");var subQ1=sQuery(id+"F25.wireOp",EDGE,"E582.trimOffspring");var subQ2=makeQuery(id+"F25.imprint","INTERSECT",VERTEX,{"derivedFrom":[subQ1,subQ0]});Q367=makeQuery(id+"F25.imprint","IMPRINT",FACE,{"disambiguationData":[TD([[makeQuery(id+"F25.imprint","IMPRINT",EDGE,{"disambiguationData":[TD([[subQ2,-1.0]])],"derivedFrom":subQ1}),-1.0]])]});}
            var Q368;
            {var subQ0=sQuery(id+"F25.wireOp",EDGE,"E597.trimOffspring");var subQ1=sQuery(id+"F25.wireOp",EDGE,"E576.trimOffspring");var subQ2=makeQuery(id+"F25.imprint","INTERSECT",VERTEX,{"derivedFrom":[subQ1,subQ0]});Q368=makeQuery(id+"F25.imprint","IMPRINT",FACE,{"disambiguationData":[TD([[makeQuery(id+"F25.imprint","IMPRINT",EDGE,{"disambiguationData":[TD([[subQ2,1.0]])],"derivedFrom":subQ1}),1.0]])]});}
            var Q369;
            {var subQ0=sQuery(id+"F25.wireOp",EDGE,"E597.trimOffspring");var subQ1=sQuery(id+"F25.wireOp",EDGE,"E576.trimOffspring");var subQ2=makeQuery(id+"F25.imprint","INTERSECT",VERTEX,{"derivedFrom":[subQ1,subQ0]});Q369=makeQuery(id+"F25.imprint","IMPRINT",FACE,{"disambiguationData":[TD([[makeQuery(id+"F25.imprint","IMPRINT",EDGE,{"disambiguationData":[TD([[subQ2,-1.0]])],"derivedFrom":subQ1}),1.0]])]});}
            var Q370;
            {var subQ0=sQuery(id+"F25.wireOp",EDGE,"E582.trimOffspring");var subQ1=sQuery(id+"F25.wireOp",EDGE,"E585.trimOffspring");var subQ2=makeQuery(id+"F25.imprint","INTERSECT",VERTEX,{"derivedFrom":[subQ1,subQ0]});Q370=makeQuery(id+"F25.imprint","IMPRINT",FACE,{"disambiguationData":[TD([[makeQuery(id+"F25.imprint","IMPRINT",EDGE,{"disambiguationData":[TD([[subQ2,-1.0]])],"derivedFrom":subQ1}),-1.0]])]});}
            var Q371;
            {var subQ0=sQuery(id+"F25.wireOp",EDGE,"E582.trimOffspring");var subQ1=sQuery(id+"F25.wireOp",EDGE,"E585.trimOffspring");var subQ2=makeQuery(id+"F25.imprint","INTERSECT",VERTEX,{"derivedFrom":[subQ1,subQ0]});Q371=makeQuery(id+"F25.imprint","IMPRINT",FACE,{"disambiguationData":[TD([[makeQuery(id+"F25.imprint","IMPRINT",EDGE,{"disambiguationData":[TD([[subQ2,-1.0]])],"derivedFrom":subQ1}),1.0]])]});}
            var Q372;
            {var subQ0=sQuery(id+"F25.wireOp",EDGE,"E585.trimOffspring");var subQ1=sQuery(id+"F25.wireOp",EDGE,"E576.trimOffspring");var subQ2=makeQuery(id+"F25.imprint","INTERSECT",VERTEX,{"derivedFrom":[subQ1,subQ0]});Q372=makeQuery(id+"F25.imprint","IMPRINT",FACE,{"disambiguationData":[TD([[makeQuery(id+"F25.imprint","IMPRINT",EDGE,{"disambiguationData":[TD([[subQ2,-1.0]])],"derivedFrom":subQ1}),1.0]])]});}
            var Q373;
            {var subQ0=sQuery(id+"F25.wireOp",EDGE,"E589.trimOffspring");var subQ1=sQuery(id+"F25.wireOp",EDGE,"E576.trimOffspring");var subQ2=makeQuery(id+"F25.imprint","INTERSECT",VERTEX,{"derivedFrom":[subQ1,subQ0]});Q373=makeQuery(id+"F25.imprint","IMPRINT",FACE,{"disambiguationData":[TD([[makeQuery(id+"F25.imprint","IMPRINT",EDGE,{"disambiguationData":[TD([[subQ2,1.0]])],"derivedFrom":subQ1}),1.0]])]});}
            var Q374;
            {var subQ0=sQuery(id+"F25.wireOp",EDGE,"E433.MirrorCS");Q374=makeQuery(id+"F25.imprint","IMPRINT",FACE,{"disambiguationData":[TD([[makeQuery(id+"F25.imprint","IMPRINT",EDGE,{"derivedFrom":subQ0}),1.0]])]});}
            var Q375;
            {var subQ3=sQuery(id+"F25.wireOp",EDGE,"E585.trimOffspring");var subQ5=sQuery(id+"F25.wireOp",EDGE,"E576.trimOffspring");var subQ6=makeQuery(id+"F25.imprint","INTERSECT",VERTEX,{"derivedFrom":[subQ5,subQ3]});Q375=makeQuery(id+"F25.imprint","IMPRINT",FACE,{"disambiguationData":[TD([[makeQuery(id+"F25.imprint","IMPRINT",EDGE,{"disambiguationData":[TD([[subQ6,-1.0]])],"derivedFrom":subQ5}),-1.0]])]});}
            var Q376;
            {var subQ0=sQuery(id+"F25.wireOp",EDGE,"E589.trimOffspring");var subQ1=sQuery(id+"F25.wireOp",EDGE,"E582.trimOffspring");var subQ2=makeQuery(id+"F25.imprint","INTERSECT",VERTEX,{"derivedFrom":[subQ1,subQ0]});Q376=makeQuery(id+"F25.imprint","IMPRINT",FACE,{"disambiguationData":[TD([[makeQuery(id+"F25.imprint","IMPRINT",EDGE,{"disambiguationData":[TD([[subQ2,1.0]])],"derivedFrom":subQ1}),-1.0]])]});}
            var Q377;
            {var subQ0=sQuery(id+"F25.wireOp",EDGE,"E578.trimOffspring");var subQ1=sQuery(id+"F25.wireOp",EDGE,"E454.MirrorCS");var subQ2=makeQuery(id+"F25.imprint","INTERSECT",VERTEX,{"derivedFrom":[subQ1,subQ0]});Q377=makeQuery(id+"F25.imprint","IMPRINT",FACE,{"disambiguationData":[TD([[makeQuery(id+"F25.imprint","IMPRINT",EDGE,{"disambiguationData":[TD([[subQ2,-1.0]])],"derivedFrom":subQ1}),1.0]])]});}
            var Q378;
            {var subQ0=sQuery(id+"F25.wireOp",EDGE,"E574.trimOffspring");var subQ1=sQuery(id+"F25.wireOp",EDGE,"E456.MirrorCS");var subQ2=makeQuery(id+"F25.imprint","INTERSECT",VERTEX,{"derivedFrom":[subQ1,subQ0]});Q378=makeQuery(id+"F25.imprint","IMPRINT",FACE,{"disambiguationData":[TD([[makeQuery(id+"F25.imprint","IMPRINT",EDGE,{"disambiguationData":[TD([[subQ2,1.0]])],"derivedFrom":subQ1}),-1.0]])]});}
            var Q379;
            {var subQ0=sQuery(id+"F25.wireOp",EDGE,"E574.trimOffspring");var subQ1=sQuery(id+"F25.wireOp",EDGE,"E454.MirrorCS");var subQ2=makeQuery(id+"F25.imprint","INTERSECT",VERTEX,{"derivedFrom":[subQ1,subQ0]});Q379=makeQuery(id+"F25.imprint","IMPRINT",FACE,{"disambiguationData":[TD([[makeQuery(id+"F25.imprint","IMPRINT",EDGE,{"disambiguationData":[TD([[subQ2,-1.0]])],"derivedFrom":subQ1}),1.0]])]});}
            var Q380;
            {var subQ0=sQuery(id+"F25.wireOp",EDGE,"E574.trimOffspring");var subQ1=sQuery(id+"F25.wireOp",EDGE,"E456.MirrorCS");var subQ2=makeQuery(id+"F25.imprint","INTERSECT",VERTEX,{"derivedFrom":[subQ1,subQ0]});Q380=makeQuery(id+"F25.imprint","IMPRINT",FACE,{"disambiguationData":[TD([[makeQuery(id+"F25.imprint","IMPRINT",EDGE,{"disambiguationData":[TD([[subQ2,-1.0]])],"derivedFrom":subQ1}),-1.0]])]});}
            var Q381;
            {var subQ0=sQuery(id+"F25.wireOp",EDGE,"E580.trimOffspring");var subQ1=sQuery(id+"F25.wireOp",EDGE,"E454.MirrorCS");var subQ2=makeQuery(id+"F25.imprint","INTERSECT",VERTEX,{"derivedFrom":[subQ1,subQ0]});Q381=makeQuery(id+"F25.imprint","IMPRINT",FACE,{"disambiguationData":[TD([[makeQuery(id+"F25.imprint","IMPRINT",EDGE,{"disambiguationData":[TD([[subQ2,-1.0]])],"derivedFrom":subQ1}),1.0]])]});}
            var Q382;
            {var subQ0=sQuery(id+"F25.wireOp",EDGE,"E580.trimOffspring");var subQ1=sQuery(id+"F25.wireOp",EDGE,"E456.MirrorCS");var subQ2=makeQuery(id+"F25.imprint","INTERSECT",VERTEX,{"derivedFrom":[subQ1,subQ0]});Q382=makeQuery(id+"F25.imprint","IMPRINT",FACE,{"disambiguationData":[TD([[makeQuery(id+"F25.imprint","IMPRINT",EDGE,{"disambiguationData":[TD([[subQ2,-1.0]])],"derivedFrom":subQ1}),-1.0]])]});}
            var Q383;
            {var subQ0=sQuery(id+"F25.wireOp",EDGE,"E579.trimOffspring");var subQ1=sQuery(id+"F25.wireOp",EDGE,"E454.MirrorCS");var subQ2=makeQuery(id+"F25.imprint","INTERSECT",VERTEX,{"derivedFrom":[subQ1,subQ0]});Q383=makeQuery(id+"F25.imprint","IMPRINT",FACE,{"disambiguationData":[TD([[makeQuery(id+"F25.imprint","IMPRINT",EDGE,{"disambiguationData":[TD([[subQ2,-1.0]])],"derivedFrom":subQ1}),1.0]])]});}
            var Q384;
            {var subQ0=sQuery(id+"F25.wireOp",EDGE,"E581.trimOffspring");var subQ1=sQuery(id+"F25.wireOp",EDGE,"E456.MirrorCS");var subQ2=makeQuery(id+"F25.imprint","INTERSECT",VERTEX,{"derivedFrom":[subQ1,subQ0]});Q384=makeQuery(id+"F25.imprint","IMPRINT",FACE,{"disambiguationData":[TD([[makeQuery(id+"F25.imprint","IMPRINT",EDGE,{"disambiguationData":[TD([[subQ2,1.0]])],"derivedFrom":subQ1}),-1.0]])]});}
            var Q385;
            {var subQ0=sQuery(id+"F25.wireOp",EDGE,"E581.trimOffspring");var subQ1=sQuery(id+"F25.wireOp",EDGE,"E454.MirrorCS");var subQ2=makeQuery(id+"F25.imprint","INTERSECT",VERTEX,{"derivedFrom":[subQ1,subQ0]});Q385=makeQuery(id+"F25.imprint","IMPRINT",FACE,{"disambiguationData":[TD([[makeQuery(id+"F25.imprint","IMPRINT",EDGE,{"disambiguationData":[TD([[subQ2,-1.0]])],"derivedFrom":subQ1}),1.0]])]});}
            var Q386;
            {var subQ0=sQuery(id+"F25.wireOp",EDGE,"E581.trimOffspring");var subQ1=sQuery(id+"F25.wireOp",EDGE,"E456.MirrorCS");var subQ2=makeQuery(id+"F25.imprint","INTERSECT",VERTEX,{"derivedFrom":[subQ1,subQ0]});Q386=makeQuery(id+"F25.imprint","IMPRINT",FACE,{"disambiguationData":[TD([[makeQuery(id+"F25.imprint","IMPRINT",EDGE,{"disambiguationData":[TD([[subQ2,-1.0]])],"derivedFrom":subQ1}),-1.0]])]});}
            var Q387;
            {var subQ0=sQuery(id+"F25.wireOp",EDGE,"E585.trimOffspring");var subQ1=sQuery(id+"F25.wireOp",EDGE,"E454.MirrorCS");var subQ2=makeQuery(id+"F25.imprint","INTERSECT",VERTEX,{"derivedFrom":[subQ1,subQ0]});Q387=makeQuery(id+"F25.imprint","IMPRINT",FACE,{"disambiguationData":[TD([[makeQuery(id+"F25.imprint","IMPRINT",EDGE,{"disambiguationData":[TD([[subQ2,-1.0]])],"derivedFrom":subQ1}),1.0]])]});}
            var Q388;
            {var subQ3=sQuery(id+"F25.wireOp",EDGE,"E585.trimOffspring");var subQ5=sQuery(id+"F25.wireOp",EDGE,"E441.MirrorCS");var subQ6=makeQuery(id+"F25.imprint","INTERSECT",VERTEX,{"derivedFrom":[subQ5,subQ3]});Q388=makeQuery(id+"F25.imprint","IMPRINT",FACE,{"disambiguationData":[TD([[makeQuery(id+"F25.imprint","IMPRINT",EDGE,{"disambiguationData":[TD([[subQ6,-1.0]])],"derivedFrom":subQ5}),1.0]])]});}
            var Q389;
            {var subQ0=sQuery(id+"F25.wireOp",EDGE,"E433.MirrorCS");Q389=makeQuery(id+"F25.imprint","IMPRINT",FACE,{"disambiguationData":[TD([[makeQuery(id+"F25.imprint","IMPRINT",EDGE,{"derivedFrom":subQ0}),-1.0]])]});}
            var Q390;
            {var subQ0=sQuery(id+"F25.wireOp",EDGE,"E589.trimOffspring");var subQ1=sQuery(id+"F25.wireOp",EDGE,"E454.MirrorCS");var subQ2=makeQuery(id+"F25.imprint","INTERSECT",VERTEX,{"derivedFrom":[subQ1,subQ0]});Q390=makeQuery(id+"F25.imprint","IMPRINT",FACE,{"disambiguationData":[TD([[makeQuery(id+"F25.imprint","IMPRINT",EDGE,{"disambiguationData":[TD([[subQ2,1.0]])],"derivedFrom":subQ1}),1.0]])]});}
            var Q391;
            {var subQ0=sQuery(id+"F25.wireOp",EDGE,"E608.trimOffspring");var subQ1=sQuery(id+"F25.wireOp",EDGE,"E423.MirrorCS");var subQ2=makeQuery(id+"F25.imprint","INTERSECT",VERTEX,{"derivedFrom":[subQ1,subQ0]});Q391=makeQuery(id+"F25.imprint","IMPRINT",FACE,{"disambiguationData":[TD([[makeQuery(id+"F25.imprint","IMPRINT",EDGE,{"disambiguationData":[TD([[subQ2,-1.0]])],"derivedFrom":subQ1}),1.0]])]});}
            var Q392;
            {var subQ0=sQuery(id+"F25.wireOp",EDGE,"E608.trimOffspring");var subQ1=sQuery(id+"F25.wireOp",EDGE,"E427.MirrorCS");var subQ2=makeQuery(id+"F25.imprint","INTERSECT",VERTEX,{"derivedFrom":[subQ1,subQ0]});Q392=makeQuery(id+"F25.imprint","IMPRINT",FACE,{"disambiguationData":[TD([[makeQuery(id+"F25.imprint","IMPRINT",EDGE,{"disambiguationData":[TD([[subQ2,-1.0]])],"derivedFrom":subQ1}),1.0]])]});}
            var Q393;
            {var subQ0=sQuery(id+"F25.wireOp",EDGE,"E584.trimOffspring");Q393=makeQuery(id+"F25.imprint","IMPRINT",FACE,{"disambiguationData":[TD([[makeQuery(id+"F25.imprint","IMPRINT",EDGE,{"derivedFrom":subQ0}),1.0]])]});}
            var Q394;
            {var subQ3=sQuery(id+"F25.wireOp",EDGE,"E608.trimOffspring");var subQ5=sQuery(id+"F25.wireOp",EDGE,"E448.MirrorCS");var subQ6=makeQuery(id+"F25.imprint","INTERSECT",VERTEX,{"derivedFrom":[subQ5,subQ3]});Q394=makeQuery(id+"F25.imprint","IMPRINT",FACE,{"disambiguationData":[TD([[makeQuery(id+"F25.imprint","IMPRINT",EDGE,{"disambiguationData":[TD([[subQ6,-1.0]])],"derivedFrom":subQ5}),-1.0]])]});}
            var Q395;
            {var subQ0=sQuery(id+"F25.wireOp",EDGE,"E608.trimOffspring");var subQ1=sQuery(id+"F25.wireOp",EDGE,"E431.MirrorCS");var subQ2=makeQuery(id+"F25.imprint","INTERSECT",VERTEX,{"derivedFrom":[subQ1,subQ0]});Q395=makeQuery(id+"F25.imprint","IMPRINT",FACE,{"disambiguationData":[TD([[makeQuery(id+"F25.imprint","IMPRINT",EDGE,{"disambiguationData":[TD([[subQ2,-1.0]])],"derivedFrom":subQ1}),-1.0]])]});}
            var Q396;
            {var subQ0=sQuery(id+"F25.wireOp",EDGE,"E608.trimOffspring");var subQ1=sQuery(id+"F25.wireOp",EDGE,"E431.MirrorCS");var subQ2=makeQuery(id+"F25.imprint","INTERSECT",VERTEX,{"derivedFrom":[subQ1,subQ0]});Q396=makeQuery(id+"F25.imprint","IMPRINT",FACE,{"disambiguationData":[TD([[makeQuery(id+"F25.imprint","IMPRINT",EDGE,{"disambiguationData":[TD([[subQ2,-1.0]])],"derivedFrom":subQ1}),1.0]])]});}
            var Q397;
            {var subQ0=sQuery(id+"F25.wireOp",EDGE,"E608.trimOffspring");var subQ1=sQuery(id+"F25.wireOp",EDGE,"E446.MirrorCS");var subQ2=makeQuery(id+"F25.imprint","INTERSECT",VERTEX,{"derivedFrom":[subQ1,subQ0]});Q397=makeQuery(id+"F25.imprint","IMPRINT",FACE,{"disambiguationData":[TD([[makeQuery(id+"F25.imprint","IMPRINT",EDGE,{"disambiguationData":[TD([[subQ2,-1.0]])],"derivedFrom":subQ1}),1.0]])]});}
            var Q398;
            {var subQ0=sQuery(id+"F25.wireOp",EDGE,"E608.trimOffspring");var subQ1=sQuery(id+"F25.wireOp",EDGE,"E444.MirrorCS");var subQ2=makeQuery(id+"F25.imprint","INTERSECT",VERTEX,{"derivedFrom":[subQ1,subQ0]});Q398=makeQuery(id+"F25.imprint","IMPRINT",FACE,{"disambiguationData":[TD([[makeQuery(id+"F25.imprint","IMPRINT",EDGE,{"disambiguationData":[TD([[subQ2,-1.0]])],"derivedFrom":subQ1}),-1.0]])]});}
            var Q399;
            {var subQ0=sQuery(id+"F25.wireOp",EDGE,"E603.trimOffspring");var subQ1=sQuery(id+"F25.wireOp",EDGE,"E444.MirrorCS");var subQ2=makeQuery(id+"F25.imprint","INTERSECT",VERTEX,{"derivedFrom":[subQ1,subQ0]});Q399=makeQuery(id+"F25.imprint","IMPRINT",FACE,{"disambiguationData":[TD([[makeQuery(id+"F25.imprint","IMPRINT",EDGE,{"disambiguationData":[TD([[subQ2,-1.0]])],"derivedFrom":subQ1}),-1.0]])]});}
            var Q400;
            {var subQ0=sQuery(id+"F25.wireOp",EDGE,"E603.trimOffspring");var subQ1=sQuery(id+"F25.wireOp",EDGE,"E446.MirrorCS");var subQ2=makeQuery(id+"F25.imprint","INTERSECT",VERTEX,{"derivedFrom":[subQ1,subQ0]});Q400=makeQuery(id+"F25.imprint","IMPRINT",FACE,{"disambiguationData":[TD([[makeQuery(id+"F25.imprint","IMPRINT",EDGE,{"disambiguationData":[TD([[subQ2,-1.0]])],"derivedFrom":subQ1}),1.0]])]});}
            var Q401;
            {var subQ0=sQuery(id+"F25.wireOp",EDGE,"E602.trimOffspring");var subQ1=sQuery(id+"F25.wireOp",EDGE,"E446.MirrorCS");var subQ2=makeQuery(id+"F25.imprint","INTERSECT",VERTEX,{"derivedFrom":[subQ1,subQ0]});Q401=makeQuery(id+"F25.imprint","IMPRINT",FACE,{"disambiguationData":[TD([[makeQuery(id+"F25.imprint","IMPRINT",EDGE,{"disambiguationData":[TD([[subQ2,-1.0]])],"derivedFrom":subQ1}),1.0]])]});}
            var Q402;
            {var subQ0=sQuery(id+"F25.wireOp",EDGE,"E601.trimOffspring");var subQ1=sQuery(id+"F25.wireOp",EDGE,"E446.MirrorCS");var subQ2=makeQuery(id+"F25.imprint","INTERSECT",VERTEX,{"derivedFrom":[subQ1,subQ0]});Q402=makeQuery(id+"F25.imprint","IMPRINT",FACE,{"disambiguationData":[TD([[makeQuery(id+"F25.imprint","IMPRINT",EDGE,{"disambiguationData":[TD([[subQ2,-1.0]])],"derivedFrom":subQ1}),1.0]])]});}
            var Q403;
            {var subQ0=sQuery(id+"F25.wireOp",EDGE,"E590.trimOffspring");var subQ1=sQuery(id+"F25.wireOp",EDGE,"E446.MirrorCS");var subQ2=makeQuery(id+"F25.imprint","INTERSECT",VERTEX,{"derivedFrom":[subQ1,subQ0]});Q403=makeQuery(id+"F25.imprint","IMPRINT",FACE,{"disambiguationData":[TD([[makeQuery(id+"F25.imprint","IMPRINT",EDGE,{"disambiguationData":[TD([[subQ2,-1.0]])],"derivedFrom":subQ1}),1.0]])]});}
            var Q404;
            {var subQ0=sQuery(id+"F25.wireOp",EDGE,"E593.trimOffspring");var subQ1=sQuery(id+"F25.wireOp",EDGE,"E446.MirrorCS");var subQ2=makeQuery(id+"F25.imprint","INTERSECT",VERTEX,{"derivedFrom":[subQ1,subQ0]});Q404=makeQuery(id+"F25.imprint","IMPRINT",FACE,{"disambiguationData":[TD([[makeQuery(id+"F25.imprint","IMPRINT",EDGE,{"disambiguationData":[TD([[subQ2,-1.0]])],"derivedFrom":subQ1}),1.0]])]});}
            var Q405;
            {var subQ0=sQuery(id+"F25.wireOp",EDGE,"E591.trimOffspring");var subQ1=sQuery(id+"F25.wireOp",EDGE,"E446.MirrorCS");var subQ2=makeQuery(id+"F25.imprint","INTERSECT",VERTEX,{"derivedFrom":[subQ1,subQ0]});Q405=makeQuery(id+"F25.imprint","IMPRINT",FACE,{"disambiguationData":[TD([[makeQuery(id+"F25.imprint","IMPRINT",EDGE,{"disambiguationData":[TD([[subQ2,1.0]])],"derivedFrom":subQ1}),1.0]])]});}
            var Q406;
            {var subQ0=sQuery(id+"F25.wireOp",EDGE,"E591.trimOffspring");var subQ1=sQuery(id+"F25.wireOp",EDGE,"E444.MirrorCS");var subQ2=makeQuery(id+"F25.imprint","INTERSECT",VERTEX,{"derivedFrom":[subQ1,subQ0]});Q406=makeQuery(id+"F25.imprint","IMPRINT",FACE,{"disambiguationData":[TD([[makeQuery(id+"F25.imprint","IMPRINT",EDGE,{"disambiguationData":[TD([[subQ2,1.0]])],"derivedFrom":subQ1}),-1.0]])]});}
            var Q407;
            {var subQ0=sQuery(id+"F25.wireOp",EDGE,"E591.trimOffspring");var subQ1=sQuery(id+"F25.wireOp",EDGE,"E444.MirrorCS");var subQ2=makeQuery(id+"F25.imprint","INTERSECT",VERTEX,{"derivedFrom":[subQ1,subQ0]});Q407=makeQuery(id+"F25.imprint","IMPRINT",FACE,{"disambiguationData":[TD([[makeQuery(id+"F25.imprint","IMPRINT",EDGE,{"disambiguationData":[TD([[subQ2,1.0]])],"derivedFrom":subQ1}),1.0]])]});}
            var Q408;
            {var subQ0=sQuery(id+"F25.wireOp",EDGE,"E591.trimOffspring");var subQ5=sQuery(id+"F25.wireOp",EDGE,"E427.MirrorCS");var subQ6=makeQuery(id+"F25.imprint","INTERSECT",VERTEX,{"derivedFrom":[subQ5,subQ0]});Q408=makeQuery(id+"F25.imprint","IMPRINT",FACE,{"disambiguationData":[TD([[makeQuery(id+"F25.imprint","IMPRINT",EDGE,{"disambiguationData":[TD([[subQ6,1.0]])],"derivedFrom":subQ5}),-1.0]])]});}
            var Q409;
            {var subQ0=sQuery(id+"F25.wireOp",EDGE,"E593.trimOffspring");var subQ5=sQuery(id+"F25.wireOp",EDGE,"E427.MirrorCS");var subQ7=makeQuery(id+"F25.imprint","INTERSECT",VERTEX,{"derivedFrom":[subQ5,subQ0]});Q409=makeQuery(id+"F25.imprint","IMPRINT",FACE,{"disambiguationData":[TD([[makeQuery(id+"F25.imprint","IMPRINT",EDGE,{"disambiguationData":[TD([[subQ7,-1.0]])],"derivedFrom":subQ5}),-1.0]])]});}
            var Q410;
            {var subQ0=sQuery(id+"F25.wireOp",EDGE,"E590.trimOffspring");var subQ5=sQuery(id+"F25.wireOp",EDGE,"E427.MirrorCS");var subQ6=makeQuery(id+"F25.imprint","INTERSECT",VERTEX,{"derivedFrom":[subQ5,subQ0]});Q410=makeQuery(id+"F25.imprint","IMPRINT",FACE,{"disambiguationData":[TD([[makeQuery(id+"F25.imprint","IMPRINT",EDGE,{"disambiguationData":[TD([[subQ6,-1.0]])],"derivedFrom":subQ5}),-1.0]])]});}
            var Q411;
            {var subQ3=sQuery(id+"F25.wireOp",EDGE,"E567.trimOffspring");var subQ5=sQuery(id+"F25.wireOp",EDGE,"E427.MirrorCS");var subQ6=makeQuery(id+"F25.imprint","INTERSECT",VERTEX,{"derivedFrom":[subQ5,subQ3]});Q411=makeQuery(id+"F25.imprint","IMPRINT",FACE,{"disambiguationData":[TD([[makeQuery(id+"F25.imprint","IMPRINT",EDGE,{"disambiguationData":[TD([[subQ6,-1.0]])],"derivedFrom":subQ5}),-1.0]])]});}
            var Q412;
            {var subQ0=sQuery(id+"F25.wireOp",EDGE,"E594.trimOffspring");var subQ5=sQuery(id+"F25.wireOp",EDGE,"E427.MirrorCS");var subQ6=makeQuery(id+"F25.imprint","INTERSECT",VERTEX,{"derivedFrom":[subQ5,subQ0]});Q412=makeQuery(id+"F25.imprint","IMPRINT",FACE,{"disambiguationData":[TD([[makeQuery(id+"F25.imprint","IMPRINT",EDGE,{"disambiguationData":[TD([[subQ6,-1.0]])],"derivedFrom":subQ5}),-1.0]])]});}
            var Q413;
            {var subQ3=sQuery(id+"F25.wireOp",EDGE,"E599.trimOffspring");var subQ5=sQuery(id+"F25.wireOp",EDGE,"E427.MirrorCS");var subQ6=makeQuery(id+"F25.imprint","INTERSECT",VERTEX,{"derivedFrom":[subQ5,subQ3]});Q413=makeQuery(id+"F25.imprint","IMPRINT",FACE,{"disambiguationData":[TD([[makeQuery(id+"F25.imprint","IMPRINT",EDGE,{"disambiguationData":[TD([[subQ6,-1.0]])],"derivedFrom":subQ5}),-1.0]])]});}
            var Q414;
            {var subQ0=sQuery(id+"F25.wireOp",EDGE,"E599.trimOffspring");var subQ1=sQuery(id+"F25.wireOp",EDGE,"E427.MirrorCS");var subQ2=makeQuery(id+"F25.imprint","INTERSECT",VERTEX,{"derivedFrom":[subQ1,subQ0]});Q414=makeQuery(id+"F25.imprint","IMPRINT",FACE,{"disambiguationData":[TD([[makeQuery(id+"F25.imprint","IMPRINT",EDGE,{"disambiguationData":[TD([[subQ2,-1.0]])],"derivedFrom":subQ1}),1.0]])]});}
            var Q415;
            {var subQ0=sQuery(id+"F25.wireOp",EDGE,"E594.trimOffspring");var subQ1=sQuery(id+"F25.wireOp",EDGE,"E427.MirrorCS");var subQ2=makeQuery(id+"F25.imprint","INTERSECT",VERTEX,{"derivedFrom":[subQ1,subQ0]});Q415=makeQuery(id+"F25.imprint","IMPRINT",FACE,{"disambiguationData":[TD([[makeQuery(id+"F25.imprint","IMPRINT",EDGE,{"disambiguationData":[TD([[subQ2,-1.0]])],"derivedFrom":subQ1}),1.0]])]});}
            var Q416;
            {var subQ0=sQuery(id+"F25.wireOp",EDGE,"E567.trimOffspring");var subQ1=sQuery(id+"F25.wireOp",EDGE,"E427.MirrorCS");var subQ2=makeQuery(id+"F25.imprint","INTERSECT",VERTEX,{"derivedFrom":[subQ1,subQ0]});Q416=makeQuery(id+"F25.imprint","IMPRINT",FACE,{"disambiguationData":[TD([[makeQuery(id+"F25.imprint","IMPRINT",EDGE,{"disambiguationData":[TD([[subQ2,-1.0]])],"derivedFrom":subQ1}),1.0]])]});}
            var Q417;
            {var subQ0=sQuery(id+"F25.wireOp",EDGE,"E590.trimOffspring");var subQ1=sQuery(id+"F25.wireOp",EDGE,"E427.MirrorCS");var subQ2=makeQuery(id+"F25.imprint","INTERSECT",VERTEX,{"derivedFrom":[subQ1,subQ0]});Q417=makeQuery(id+"F25.imprint","IMPRINT",FACE,{"disambiguationData":[TD([[makeQuery(id+"F25.imprint","IMPRINT",EDGE,{"disambiguationData":[TD([[subQ2,-1.0]])],"derivedFrom":subQ1}),1.0]])]});}
            var Q418;
            {var subQ0=sQuery(id+"F25.wireOp",EDGE,"E593.trimOffspring");var subQ1=sQuery(id+"F25.wireOp",EDGE,"E427.MirrorCS");var subQ2=makeQuery(id+"F25.imprint","INTERSECT",VERTEX,{"derivedFrom":[subQ1,subQ0]});Q418=makeQuery(id+"F25.imprint","IMPRINT",FACE,{"disambiguationData":[TD([[makeQuery(id+"F25.imprint","IMPRINT",EDGE,{"disambiguationData":[TD([[subQ2,-1.0]])],"derivedFrom":subQ1}),1.0]])]});}
            var Q419;
            {var subQ0=sQuery(id+"F25.wireOp",EDGE,"E591.trimOffspring");var subQ1=sQuery(id+"F25.wireOp",EDGE,"E427.MirrorCS");var subQ2=makeQuery(id+"F25.imprint","INTERSECT",VERTEX,{"derivedFrom":[subQ1,subQ0]});Q419=makeQuery(id+"F25.imprint","IMPRINT",FACE,{"disambiguationData":[TD([[makeQuery(id+"F25.imprint","IMPRINT",EDGE,{"disambiguationData":[TD([[subQ2,1.0]])],"derivedFrom":subQ1}),1.0]])]});}
            var Q420;
            {var subQ0=sQuery(id+"F25.wireOp",EDGE,"E591.trimOffspring");var subQ1=sQuery(id+"F25.wireOp",EDGE,"E440.MirrorCS");var subQ2=makeQuery(id+"F25.imprint","INTERSECT",VERTEX,{"derivedFrom":[subQ1,subQ0]});Q420=makeQuery(id+"F25.imprint","IMPRINT",FACE,{"disambiguationData":[TD([[makeQuery(id+"F25.imprint","IMPRINT",EDGE,{"disambiguationData":[TD([[subQ2,1.0]])],"derivedFrom":subQ1}),1.0]])]});}
            var Q421;
            {var subQ0=sQuery(id+"F25.wireOp",EDGE,"E591.trimOffspring");var subQ1=sQuery(id+"F25.wireOp",EDGE,"E431.MirrorCS");var subQ2=makeQuery(id+"F25.imprint","INTERSECT",VERTEX,{"derivedFrom":[subQ1,subQ0]});Q421=makeQuery(id+"F25.imprint","IMPRINT",FACE,{"disambiguationData":[TD([[makeQuery(id+"F25.imprint","IMPRINT",EDGE,{"disambiguationData":[TD([[subQ2,1.0]])],"derivedFrom":subQ1}),-1.0]])]});}
            var Q422;
            {var subQ0=sQuery(id+"F25.wireOp",EDGE,"E593.trimOffspring");var subQ1=sQuery(id+"F25.wireOp",EDGE,"E440.MirrorCS");var subQ2=makeQuery(id+"F25.imprint","INTERSECT",VERTEX,{"derivedFrom":[subQ1,subQ0]});Q422=makeQuery(id+"F25.imprint","IMPRINT",FACE,{"disambiguationData":[TD([[makeQuery(id+"F25.imprint","IMPRINT",EDGE,{"disambiguationData":[TD([[subQ2,-1.0]])],"derivedFrom":subQ1}),1.0]])]});}
            var Q423;
            {var subQ0=sQuery(id+"F25.wireOp",EDGE,"E593.trimOffspring");var subQ1=sQuery(id+"F25.wireOp",EDGE,"E431.MirrorCS");var subQ2=makeQuery(id+"F25.imprint","INTERSECT",VERTEX,{"derivedFrom":[subQ1,subQ0]});Q423=makeQuery(id+"F25.imprint","IMPRINT",FACE,{"disambiguationData":[TD([[makeQuery(id+"F25.imprint","IMPRINT",EDGE,{"disambiguationData":[TD([[subQ2,-1.0]])],"derivedFrom":subQ1}),-1.0]])]});}
            var Q424;
            {var subQ0=sQuery(id+"F25.wireOp",EDGE,"E590.trimOffspring");var subQ1=sQuery(id+"F25.wireOp",EDGE,"E440.MirrorCS");var subQ2=makeQuery(id+"F25.imprint","INTERSECT",VERTEX,{"derivedFrom":[subQ1,subQ0]});Q424=makeQuery(id+"F25.imprint","IMPRINT",FACE,{"disambiguationData":[TD([[makeQuery(id+"F25.imprint","IMPRINT",EDGE,{"disambiguationData":[TD([[subQ2,-1.0]])],"derivedFrom":subQ1}),1.0]])]});}
            var Q425;
            {var subQ0=sQuery(id+"F25.wireOp",EDGE,"E590.trimOffspring");var subQ1=sQuery(id+"F25.wireOp",EDGE,"E431.MirrorCS");var subQ2=makeQuery(id+"F25.imprint","INTERSECT",VERTEX,{"derivedFrom":[subQ1,subQ0]});Q425=makeQuery(id+"F25.imprint","IMPRINT",FACE,{"disambiguationData":[TD([[makeQuery(id+"F25.imprint","IMPRINT",EDGE,{"disambiguationData":[TD([[subQ2,-1.0]])],"derivedFrom":subQ1}),-1.0]])]});}
            var Q426;
            {var subQ0=sQuery(id+"F25.wireOp",EDGE,"E601.trimOffspring");var subQ5=sQuery(id+"F25.wireOp",EDGE,"E448.MirrorCS");var subQ6=makeQuery(id+"F25.imprint","INTERSECT",VERTEX,{"derivedFrom":[subQ5,subQ0]});Q426=makeQuery(id+"F25.imprint","IMPRINT",FACE,{"disambiguationData":[TD([[makeQuery(id+"F25.imprint","IMPRINT",EDGE,{"disambiguationData":[TD([[subQ6,-1.0]])],"derivedFrom":subQ5}),-1.0]])]});}
            var Q427;
            {var subQ0=sQuery(id+"F25.wireOp",EDGE,"E601.trimOffspring");var subQ1=sQuery(id+"F25.wireOp",EDGE,"E431.MirrorCS");var subQ2=makeQuery(id+"F25.imprint","INTERSECT",VERTEX,{"derivedFrom":[subQ1,subQ0]});Q427=makeQuery(id+"F25.imprint","IMPRINT",FACE,{"disambiguationData":[TD([[makeQuery(id+"F25.imprint","IMPRINT",EDGE,{"disambiguationData":[TD([[subQ2,-1.0]])],"derivedFrom":subQ1}),-1.0]])]});}
            var Q428;
            {var subQ0=sQuery(id+"F25.wireOp",EDGE,"E602.trimOffspring");var subQ5=sQuery(id+"F25.wireOp",EDGE,"E448.MirrorCS");var subQ6=makeQuery(id+"F25.imprint","INTERSECT",VERTEX,{"derivedFrom":[subQ5,subQ0]});Q428=makeQuery(id+"F25.imprint","IMPRINT",FACE,{"disambiguationData":[TD([[makeQuery(id+"F25.imprint","IMPRINT",EDGE,{"disambiguationData":[TD([[subQ6,-1.0]])],"derivedFrom":subQ5}),-1.0]])]});}
            var Q429;
            {var subQ0=sQuery(id+"F25.wireOp",EDGE,"E602.trimOffspring");var subQ1=sQuery(id+"F25.wireOp",EDGE,"E431.MirrorCS");var subQ2=makeQuery(id+"F25.imprint","INTERSECT",VERTEX,{"derivedFrom":[subQ1,subQ0]});Q429=makeQuery(id+"F25.imprint","IMPRINT",FACE,{"disambiguationData":[TD([[makeQuery(id+"F25.imprint","IMPRINT",EDGE,{"disambiguationData":[TD([[subQ2,-1.0]])],"derivedFrom":subQ1}),-1.0]])]});}
            var Q430;
            {var subQ3=sQuery(id+"F25.wireOp",EDGE,"E603.trimOffspring");var subQ5=sQuery(id+"F25.wireOp",EDGE,"E448.MirrorCS");var subQ7=makeQuery(id+"F25.imprint","INTERSECT",VERTEX,{"derivedFrom":[subQ5,subQ3]});Q430=makeQuery(id+"F25.imprint","IMPRINT",FACE,{"disambiguationData":[TD([[makeQuery(id+"F25.imprint","IMPRINT",EDGE,{"disambiguationData":[TD([[subQ7,-1.0]])],"derivedFrom":subQ5}),-1.0]])]});}
            var Q431;
            {var subQ0=sQuery(id+"F25.wireOp",EDGE,"E603.trimOffspring");var subQ1=sQuery(id+"F25.wireOp",EDGE,"E431.MirrorCS");var subQ2=makeQuery(id+"F25.imprint","INTERSECT",VERTEX,{"derivedFrom":[subQ1,subQ0]});Q431=makeQuery(id+"F25.imprint","IMPRINT",FACE,{"disambiguationData":[TD([[makeQuery(id+"F25.imprint","IMPRINT",EDGE,{"disambiguationData":[TD([[subQ2,-1.0]])],"derivedFrom":subQ1}),-1.0]])]});}
            var Q432;
            {var subQ0=sQuery(id+"F25.wireOp",EDGE,"E595.trimOffspring");var subQ1=sQuery(id+"F25.wireOp",EDGE,"E473.trimOffspring");var subQ2=makeQuery(id+"F25.imprint","INTERSECT",VERTEX,{"derivedFrom":[subQ1,subQ0]});Q432=makeQuery(id+"F25.imprint","IMPRINT",FACE,{"disambiguationData":[TD([[makeQuery(id+"F25.imprint","IMPRINT",EDGE,{"disambiguationData":[TD([[subQ2,-1.0]])],"derivedFrom":subQ1}),1.0]])]});}
            var Q433;
            {var subQ0=sQuery(id+"F25.wireOp",EDGE,"E595.trimOffspring");var subQ1=sQuery(id+"F25.wireOp",EDGE,"E474.trimOffspring");var subQ2=makeQuery(id+"F25.imprint","INTERSECT",VERTEX,{"derivedFrom":[subQ1,subQ0]});Q433=makeQuery(id+"F25.imprint","IMPRINT",FACE,{"disambiguationData":[TD([[makeQuery(id+"F25.imprint","IMPRINT",EDGE,{"disambiguationData":[TD([[subQ2,-1.0]])],"derivedFrom":subQ1}),1.0]])]});}
            var Q434;
            {var subQ0=sQuery(id+"F25.wireOp",EDGE,"E593.trimOffspring");var subQ1=sQuery(id+"F25.wireOp",EDGE,"E474.trimOffspring");var subQ2=makeQuery(id+"F25.imprint","INTERSECT",VERTEX,{"derivedFrom":[subQ1,subQ0]});Q434=makeQuery(id+"F25.imprint","IMPRINT",FACE,{"disambiguationData":[TD([[makeQuery(id+"F25.imprint","IMPRINT",EDGE,{"disambiguationData":[TD([[subQ2,-1.0]])],"derivedFrom":subQ1}),1.0]])]});}
            var Q435;
            {var subQ0=sQuery(id+"F25.wireOp",EDGE,"E590.trimOffspring");var subQ1=sQuery(id+"F25.wireOp",EDGE,"E474.trimOffspring");var subQ2=makeQuery(id+"F25.imprint","INTERSECT",VERTEX,{"derivedFrom":[subQ1,subQ0]});Q435=makeQuery(id+"F25.imprint","IMPRINT",FACE,{"disambiguationData":[TD([[makeQuery(id+"F25.imprint","IMPRINT",EDGE,{"disambiguationData":[TD([[subQ2,-1.0]])],"derivedFrom":subQ1}),1.0]])]});}
            var Q436;
            {var subQ0=sQuery(id+"F25.wireOp",EDGE,"E601.trimOffspring");var subQ1=sQuery(id+"F25.wireOp",EDGE,"E474.trimOffspring");var subQ2=makeQuery(id+"F25.imprint","INTERSECT",VERTEX,{"derivedFrom":[subQ1,subQ0]});Q436=makeQuery(id+"F25.imprint","IMPRINT",FACE,{"disambiguationData":[TD([[makeQuery(id+"F25.imprint","IMPRINT",EDGE,{"disambiguationData":[TD([[subQ2,-1.0]])],"derivedFrom":subQ1}),1.0]])]});}
            var Q437;
            {var subQ0=sQuery(id+"F25.wireOp",EDGE,"E601.trimOffspring");var subQ1=sQuery(id+"F25.wireOp",EDGE,"E475.trimOffspring");var subQ2=makeQuery(id+"F25.imprint","INTERSECT",VERTEX,{"derivedFrom":[subQ1,subQ0]});Q437=makeQuery(id+"F25.imprint","IMPRINT",FACE,{"disambiguationData":[TD([[makeQuery(id+"F25.imprint","IMPRINT",EDGE,{"disambiguationData":[TD([[subQ2,-1.0]])],"derivedFrom":subQ1}),-1.0]])]});}
            var Q438;
            {var subQ3=sQuery(id+"F25.wireOp",EDGE,"E601.trimOffspring");var subQ5=sQuery(id+"F25.wireOp",EDGE,"E475.trimOffspring");var subQ6=makeQuery(id+"F25.imprint","INTERSECT",VERTEX,{"derivedFrom":[subQ5,subQ3]});Q438=makeQuery(id+"F25.imprint","IMPRINT",FACE,{"disambiguationData":[TD([[makeQuery(id+"F25.imprint","IMPRINT",EDGE,{"disambiguationData":[TD([[subQ6,-1.0]])],"derivedFrom":subQ5}),1.0]])]});}
            var Q439;
            {var subQ0=sQuery(id+"F25.wireOp",EDGE,"E590.trimOffspring");var subQ5=sQuery(id+"F25.wireOp",EDGE,"E475.trimOffspring");var subQ6=makeQuery(id+"F25.imprint","INTERSECT",VERTEX,{"derivedFrom":[subQ5,subQ0]});Q439=makeQuery(id+"F25.imprint","IMPRINT",FACE,{"disambiguationData":[TD([[makeQuery(id+"F25.imprint","IMPRINT",EDGE,{"disambiguationData":[TD([[subQ6,-1.0]])],"derivedFrom":subQ5}),1.0]])]});}
            var Q440;
            {var subQ3=sQuery(id+"F25.wireOp",EDGE,"E593.trimOffspring");var subQ5=sQuery(id+"F25.wireOp",EDGE,"E475.trimOffspring");var subQ6=makeQuery(id+"F25.imprint","INTERSECT",VERTEX,{"derivedFrom":[subQ5,subQ3]});Q440=makeQuery(id+"F25.imprint","IMPRINT",FACE,{"disambiguationData":[TD([[makeQuery(id+"F25.imprint","IMPRINT",EDGE,{"disambiguationData":[TD([[subQ6,-1.0]])],"derivedFrom":subQ5}),1.0]])]});}
            var Q441;
            {var subQ0=sQuery(id+"F25.wireOp",EDGE,"E458.MirrorCS");var subQ5=sQuery(id+"F25.wireOp",EDGE,"E477.trimOffspring");var subQ6=makeQuery(id+"F25.imprint","INTERSECT",VERTEX,{"derivedFrom":[subQ0,subQ5]});Q441=makeQuery(id+"F25.imprint","IMPRINT",FACE,{"disambiguationData":[TD([[makeQuery(id+"F25.imprint","IMPRINT",EDGE,{"disambiguationData":[TD([[subQ6,-1.0]])],"derivedFrom":subQ5}),-1.0]])]});}
            var Q442;
            {var subQ0=sQuery(id+"F25.wireOp",EDGE,"E616.trimOffspring");var subQ1=sQuery(id+"F25.wireOp",EDGE,"E458.MirrorCS");var subQ2=makeQuery(id+"F25.imprint","INTERSECT",VERTEX,{"derivedFrom":[subQ1,subQ0]});Q442=makeQuery(id+"F25.imprint","IMPRINT",FACE,{"disambiguationData":[TD([[makeQuery(id+"F25.imprint","IMPRINT",EDGE,{"disambiguationData":[TD([[subQ2,-1.0]])],"derivedFrom":subQ1}),1.0]])]});}
            var Q443;
            {var subQ0=sQuery(id+"F25.wireOp",EDGE,"E595.trimOffspring");var subQ5=sQuery(id+"F25.wireOp",EDGE,"E475.trimOffspring");var subQ6=makeQuery(id+"F25.imprint","INTERSECT",VERTEX,{"derivedFrom":[subQ5,subQ0]});Q443=makeQuery(id+"F25.imprint","IMPRINT",FACE,{"disambiguationData":[TD([[makeQuery(id+"F25.imprint","IMPRINT",EDGE,{"disambiguationData":[TD([[subQ6,-1.0]])],"derivedFrom":subQ5}),1.0]])]});}
            var Q444;
            {var subQ0=sQuery(id+"F25.wireOp",EDGE,"E617.trimOffspring");var subQ1=sQuery(id+"F25.wireOp",EDGE,"E458.MirrorCS");var subQ2=makeQuery(id+"F25.imprint","INTERSECT",VERTEX,{"derivedFrom":[subQ1,subQ0]});Q444=makeQuery(id+"F25.imprint","IMPRINT",FACE,{"disambiguationData":[TD([[makeQuery(id+"F25.imprint","IMPRINT",EDGE,{"disambiguationData":[TD([[subQ2,-1.0]])],"derivedFrom":subQ1}),1.0]])]});}
            var Q445;
            {var subQ0=sQuery(id+"F25.wireOp",EDGE,"E617.trimOffspring");var subQ1=sQuery(id+"F25.wireOp",EDGE,"E419.MirrorCS");var subQ2=makeQuery(id+"F25.imprint","INTERSECT",VERTEX,{"derivedFrom":[subQ1,subQ0]});Q445=makeQuery(id+"F25.imprint","IMPRINT",FACE,{"disambiguationData":[TD([[makeQuery(id+"F25.imprint","IMPRINT",EDGE,{"disambiguationData":[TD([[subQ2,-1.0]])],"derivedFrom":subQ1}),-1.0]])]});}
            var Q446;
            {var subQ0=sQuery(id+"F25.wireOp",EDGE,"E617.trimOffspring");var subQ1=sQuery(id+"F25.wireOp",EDGE,"E417.MirrorCS");var subQ2=makeQuery(id+"F25.imprint","INTERSECT",VERTEX,{"derivedFrom":[subQ1,subQ0]});Q446=makeQuery(id+"F25.imprint","IMPRINT",FACE,{"disambiguationData":[TD([[makeQuery(id+"F25.imprint","IMPRINT",EDGE,{"disambiguationData":[TD([[subQ2,-1.0]])],"derivedFrom":subQ1}),-1.0]])]});}
            var Q447;
            {var subQ0=sQuery(id+"F25.wireOp",EDGE,"E617.trimOffspring");var subQ1=sQuery(id+"F25.wireOp",EDGE,"E417.MirrorCS");var subQ2=makeQuery(id+"F25.imprint","INTERSECT",VERTEX,{"derivedFrom":[subQ1,subQ0]});Q447=makeQuery(id+"F25.imprint","IMPRINT",FACE,{"disambiguationData":[TD([[makeQuery(id+"F25.imprint","IMPRINT",EDGE,{"disambiguationData":[TD([[subQ2,-1.0]])],"derivedFrom":subQ1}),1.0]])]});}
            var Q448;
            {var subQ0=sQuery(id+"F25.wireOp",EDGE,"E617.trimOffspring");var subQ1=sQuery(id+"F25.wireOp",EDGE,"E409.MirrorCS");var subQ2=makeQuery(id+"F25.imprint","INTERSECT",VERTEX,{"derivedFrom":[subQ1,subQ0]});Q448=makeQuery(id+"F25.imprint","IMPRINT",FACE,{"disambiguationData":[TD([[makeQuery(id+"F25.imprint","IMPRINT",EDGE,{"disambiguationData":[TD([[subQ2,-1.0]])],"derivedFrom":subQ1}),-1.0]])]});}
            var Q449;
            {var subQ0=sQuery(id+"F25.wireOp",EDGE,"E473.trimOffspring");var subQ1=sQuery(id+"F25.wireOp",EDGE,"E421.MirrorCS");var subQ2=makeQuery(id+"F25.imprint","INTERSECT",VERTEX,{"derivedFrom":[subQ1,subQ0]});Q449=makeQuery(id+"F25.imprint","IMPRINT",FACE,{"disambiguationData":[TD([[makeQuery(id+"F25.imprint","IMPRINT",EDGE,{"disambiguationData":[TD([[subQ2,-1.0]])],"derivedFrom":subQ1}),1.0]])]});}
            var Q450;
            {var subQ0=sQuery(id+"F25.wireOp",EDGE,"E473.trimOffspring");var subQ1=sQuery(id+"F25.wireOp",EDGE,"E416.MirrorCS");var subQ2=makeQuery(id+"F25.imprint","INTERSECT",VERTEX,{"derivedFrom":[subQ1,subQ0]});Q450=makeQuery(id+"F25.imprint","IMPRINT",FACE,{"disambiguationData":[TD([[makeQuery(id+"F25.imprint","IMPRINT",EDGE,{"disambiguationData":[TD([[subQ2,-1.0]])],"derivedFrom":subQ1}),-1.0]])]});}
            var Q451;
            {var subQ0=sQuery(id+"F25.wireOp",EDGE,"E474.trimOffspring");var subQ1=sQuery(id+"F25.wireOp",EDGE,"E421.MirrorCS");var subQ2=makeQuery(id+"F25.imprint","INTERSECT",VERTEX,{"derivedFrom":[subQ1,subQ0]});Q451=makeQuery(id+"F25.imprint","IMPRINT",FACE,{"disambiguationData":[TD([[makeQuery(id+"F25.imprint","IMPRINT",EDGE,{"disambiguationData":[TD([[subQ2,-1.0]])],"derivedFrom":subQ1}),1.0]])]});}
            var Q452;
            {var subQ0=sQuery(id+"F25.wireOp",EDGE,"E474.trimOffspring");var subQ1=sQuery(id+"F25.wireOp",EDGE,"E416.MirrorCS");var subQ2=makeQuery(id+"F25.imprint","INTERSECT",VERTEX,{"derivedFrom":[subQ1,subQ0]});Q452=makeQuery(id+"F25.imprint","IMPRINT",FACE,{"disambiguationData":[TD([[makeQuery(id+"F25.imprint","IMPRINT",EDGE,{"disambiguationData":[TD([[subQ2,-1.0]])],"derivedFrom":subQ1}),-1.0]])]});}
            var Q453;
            {var subQ0=sQuery(id+"F25.wireOp",EDGE,"E476.trimOffspring");var subQ1=sQuery(id+"F25.wireOp",EDGE,"E421.MirrorCS");var subQ2=makeQuery(id+"F25.imprint","INTERSECT",VERTEX,{"derivedFrom":[subQ1,subQ0]});Q453=makeQuery(id+"F25.imprint","IMPRINT",FACE,{"disambiguationData":[TD([[makeQuery(id+"F25.imprint","IMPRINT",EDGE,{"disambiguationData":[TD([[subQ2,-1.0]])],"derivedFrom":subQ1}),1.0]])]});}
            var Q454;
            {var subQ0=sQuery(id+"F25.wireOp",EDGE,"E476.trimOffspring");var subQ1=sQuery(id+"F25.wireOp",EDGE,"E416.MirrorCS");var subQ2=makeQuery(id+"F25.imprint","INTERSECT",VERTEX,{"derivedFrom":[subQ1,subQ0]});Q454=makeQuery(id+"F25.imprint","IMPRINT",FACE,{"disambiguationData":[TD([[makeQuery(id+"F25.imprint","IMPRINT",EDGE,{"disambiguationData":[TD([[subQ2,-1.0]])],"derivedFrom":subQ1}),-1.0]])]});}
            var Q455;
            {var subQ1=sQuery(id+"F25.wireOp",EDGE,"E421.MirrorCS");var subQ3=sQuery(id+"F25.wireOp",EDGE,"E475.trimOffspring");var subQ4=makeQuery(id+"F25.imprint","INTERSECT",VERTEX,{"derivedFrom":[subQ1,subQ3]});Q455=makeQuery(id+"F25.imprint","IMPRINT",FACE,{"disambiguationData":[TD([[makeQuery(id+"F25.imprint","IMPRINT",EDGE,{"disambiguationData":[TD([[subQ4,1.0]])],"derivedFrom":subQ3}),1.0]])]});}
            var Q456;
            {var subQ1=sQuery(id+"F25.wireOp",EDGE,"E416.MirrorCS");var subQ3=sQuery(id+"F25.wireOp",EDGE,"E475.trimOffspring");var subQ4=makeQuery(id+"F25.imprint","INTERSECT",VERTEX,{"derivedFrom":[subQ1,subQ3]});Q456=makeQuery(id+"F25.imprint","IMPRINT",FACE,{"disambiguationData":[TD([[makeQuery(id+"F25.imprint","IMPRINT",EDGE,{"disambiguationData":[TD([[subQ4,-1.0]])],"derivedFrom":subQ3}),1.0]])]});}
            var Q457;
            {var subQ1=sQuery(id+"F25.wireOp",EDGE,"E417.MirrorCS");var subQ3=sQuery(id+"F25.wireOp",EDGE,"E477.trimOffspring");var subQ4=makeQuery(id+"F25.imprint","INTERSECT",VERTEX,{"derivedFrom":[subQ1,subQ3]});Q457=makeQuery(id+"F25.imprint","IMPRINT",FACE,{"disambiguationData":[TD([[makeQuery(id+"F25.imprint","IMPRINT",EDGE,{"disambiguationData":[TD([[subQ4,-1.0]])],"derivedFrom":subQ3}),-1.0]])]});}
            var Q458;
            {var subQ1=sQuery(id+"F25.wireOp",EDGE,"E417.MirrorCS");var subQ3=sQuery(id+"F25.wireOp",EDGE,"E477.trimOffspring");var subQ4=makeQuery(id+"F25.imprint","INTERSECT",VERTEX,{"derivedFrom":[subQ1,subQ3]});Q458=makeQuery(id+"F25.imprint","IMPRINT",FACE,{"disambiguationData":[TD([[makeQuery(id+"F25.imprint","IMPRINT",EDGE,{"disambiguationData":[TD([[subQ4,1.0]])],"derivedFrom":subQ3}),-1.0]])]});}
            var Q459;
            {var subQ0=sQuery(id+"F25.wireOp",EDGE,"E616.trimOffspring");var subQ1=sQuery(id+"F25.wireOp",EDGE,"E417.MirrorCS");var subQ2=makeQuery(id+"F25.imprint","INTERSECT",VERTEX,{"derivedFrom":[subQ1,subQ0]});Q459=makeQuery(id+"F25.imprint","IMPRINT",FACE,{"disambiguationData":[TD([[makeQuery(id+"F25.imprint","IMPRINT",EDGE,{"disambiguationData":[TD([[subQ2,-1.0]])],"derivedFrom":subQ1}),-1.0]])]});}
            var Q460;
            {var subQ0=sQuery(id+"F25.wireOp",EDGE,"E616.trimOffspring");var subQ1=sQuery(id+"F25.wireOp",EDGE,"E417.MirrorCS");var subQ2=makeQuery(id+"F25.imprint","INTERSECT",VERTEX,{"derivedFrom":[subQ1,subQ0]});Q460=makeQuery(id+"F25.imprint","IMPRINT",FACE,{"disambiguationData":[TD([[makeQuery(id+"F25.imprint","IMPRINT",EDGE,{"disambiguationData":[TD([[subQ2,-1.0]])],"derivedFrom":subQ1}),1.0]])]});}
            var Q461;
            {var subQ0=sQuery(id+"F25.wireOp",EDGE,"E334.MirrorCS");var subQ1=sQuery(id+"F25.wireOp",EDGE,"E324.MirrorCS");var subQ2=makeQuery(id+"F25.imprint","INTERSECT",VERTEX,{"derivedFrom":[subQ1,subQ0]});Q461=makeQuery(id+"F25.imprint","IMPRINT",FACE,{"disambiguationData":[TD([[makeQuery(id+"F25.imprint","IMPRINT",EDGE,{"disambiguationData":[TD([[subQ2,-1.0]])],"derivedFrom":subQ1}),-1.0]])]});}
            var Q462;
            {var subQ0=sQuery(id+"F25.wireOp",EDGE,"E315.MirrorCS");Q462=makeQuery(id+"F25.imprint","IMPRINT",FACE,{"disambiguationData":[TD([[makeQuery(id+"F25.imprint","IMPRINT",EDGE,{"derivedFrom":subQ0}),1.0]])]});}
            var Q463;
            {var subQ5=sQuery(id+"F25.wireOp",EDGE,"E315.MirrorCS");Q463=makeQuery(id+"F25.imprint","IMPRINT",FACE,{"disambiguationData":[TD([[makeQuery(id+"F25.imprint","IMPRINT",EDGE,{"derivedFrom":subQ5}),-1.0]])]});}
            var Q464;
            {var subQ5=sQuery(id+"F25.wireOp",EDGE,"E616.trimOffspring");var subQ6=sQuery(id+"F25.wireOp",EDGE,"E409.MirrorCS");var subQ7=makeQuery(id+"F25.imprint","INTERSECT",VERTEX,{"derivedFrom":[subQ6,subQ5]});Q464=makeQuery(id+"F25.imprint","IMPRINT",FACE,{"disambiguationData":[TD([[makeQuery(id+"F25.imprint","IMPRINT",EDGE,{"disambiguationData":[TD([[subQ7,-1.0]])],"derivedFrom":subQ6}),1.0]])]});}
            var Q465;
            {var subQ4=sQuery(id+"F25.wireOp",EDGE,"E222.right");Q465=makeQuery(id+"F25.imprint","IMPRINT",FACE,{"disambiguationData":[TD([[makeQuery(id+"F25.imprint","IMPRINT",EDGE,{"derivedFrom":subQ4}),1.0]])]});}
            var Q466;
            {var subQ0=sQuery(id+"F25.wireOp",EDGE,"E311.MirrorCS");Q466=makeQuery(id+"F25.imprint","IMPRINT",FACE,{"disambiguationData":[TD([[makeQuery(id+"F25.imprint","IMPRINT",EDGE,{"derivedFrom":subQ0}),1.0]])]});}
            var Q467;
            {var subQ1=sQuery(id+"F25.wireOp",EDGE,"E415.MirrorCS");var subQ3=sQuery(id+"F25.wireOp",EDGE,"E475.trimOffspring");var subQ4=makeQuery(id+"F25.imprint","INTERSECT",VERTEX,{"derivedFrom":[subQ1,subQ3]});Q467=makeQuery(id+"F25.imprint","IMPRINT",FACE,{"disambiguationData":[TD([[makeQuery(id+"F25.imprint","IMPRINT",EDGE,{"disambiguationData":[TD([[subQ4,-1.0]])],"derivedFrom":subQ1}),-1.0]])]});}
            var Q468;
            {var subQ5=sQuery(id+"F25.wireOp",EDGE,"E222.right");Q468=makeQuery(id+"F25.imprint","IMPRINT",FACE,{"disambiguationData":[TD([[makeQuery(id+"F25.imprint","IMPRINT",EDGE,{"derivedFrom":subQ5}),-1.0]])]});}
            var Q469;
            {var subQ1=sQuery(id+"F25.wireOp",EDGE,"E249.right");var subQ3=sQuery(id+"F25.wireOp",EDGE,"E284.trimOffspring");var subQ4=makeQuery(id+"F25.imprint","INTERSECT",VERTEX,{"derivedFrom":[subQ1,subQ3]});Q469=makeQuery(id+"F25.imprint","IMPRINT",FACE,{"disambiguationData":[TD([[makeQuery(id+"F25.imprint","IMPRINT",EDGE,{"disambiguationData":[TD([[subQ4,1.0]])],"derivedFrom":subQ3}),1.0]])]});}
            var Q470;
            {var subQ0=sQuery(id+"F25.wireOp",EDGE,"E476.trimOffspring");var subQ1=sQuery(id+"F25.wireOp",EDGE,"E415.MirrorCS");var subQ2=makeQuery(id+"F25.imprint","INTERSECT",VERTEX,{"derivedFrom":[subQ1,subQ0]});Q470=makeQuery(id+"F25.imprint","IMPRINT",FACE,{"disambiguationData":[TD([[makeQuery(id+"F25.imprint","IMPRINT",EDGE,{"disambiguationData":[TD([[subQ2,-1.0]])],"derivedFrom":subQ1}),-1.0]])]});}
            var Q471;
            {var subQ0=sQuery(id+"F25.wireOp",EDGE,"E474.trimOffspring");var subQ1=sQuery(id+"F25.wireOp",EDGE,"E415.MirrorCS");var subQ2=makeQuery(id+"F25.imprint","INTERSECT",VERTEX,{"derivedFrom":[subQ1,subQ0]});Q471=makeQuery(id+"F25.imprint","IMPRINT",FACE,{"disambiguationData":[TD([[makeQuery(id+"F25.imprint","IMPRINT",EDGE,{"disambiguationData":[TD([[subQ2,-1.0]])],"derivedFrom":subQ1}),-1.0]])]});}
            var Q472;
            {var subQ0=sQuery(id+"F25.wireOp",EDGE,"E473.trimOffspring");var subQ1=sQuery(id+"F25.wireOp",EDGE,"E415.MirrorCS");var subQ2=makeQuery(id+"F25.imprint","INTERSECT",VERTEX,{"derivedFrom":[subQ1,subQ0]});Q472=makeQuery(id+"F25.imprint","IMPRINT",FACE,{"disambiguationData":[TD([[makeQuery(id+"F25.imprint","IMPRINT",EDGE,{"disambiguationData":[TD([[subQ2,-1.0]])],"derivedFrom":subQ1}),-1.0]])]});}
            var Q473;
            {var subQ1=sQuery(id+"F25.wireOp",EDGE,"E250.right");var subQ3=sQuery(id+"F25.wireOp",EDGE,"E284.trimOffspring");var subQ4=makeQuery(id+"F25.imprint","INTERSECT",VERTEX,{"derivedFrom":[subQ1,subQ3]});Q473=makeQuery(id+"F25.imprint","IMPRINT",FACE,{"disambiguationData":[TD([[makeQuery(id+"F25.imprint","IMPRINT",EDGE,{"disambiguationData":[TD([[subQ4,1.0]])],"derivedFrom":subQ3}),1.0]])]});}
            var Q474;
            {var subQ3=sQuery(id+"F25.wireOp",EDGE,"E284.trimOffspring");var subQ5=sQuery(id+"F25.wireOp",EDGE,"E251.right");var subQ7=makeQuery(id+"F25.imprint","INTERSECT",VERTEX,{"derivedFrom":[subQ5,subQ3]});Q474=makeQuery(id+"F25.imprint","IMPRINT",FACE,{"disambiguationData":[TD([[makeQuery(id+"F25.imprint","IMPRINT",EDGE,{"disambiguationData":[TD([[subQ7,-1.0]])],"derivedFrom":subQ3}),1.0]])]});}
            var Q475;
            {var subQ3=sQuery(id+"F25.wireOp",EDGE,"E510.trimOffspring");var subQ5=sQuery(id+"F25.wireOp",EDGE,"E249.right");var subQ6=makeQuery(id+"F25.imprint","INTERSECT",VERTEX,{"derivedFrom":[subQ5,subQ3]});Q475=makeQuery(id+"F25.imprint","IMPRINT",FACE,{"disambiguationData":[TD([[makeQuery(id+"F25.imprint","IMPRINT",EDGE,{"disambiguationData":[TD([[subQ6,-1.0]])],"derivedFrom":subQ5}),-1.0]])]});}
            var Q476;
            {var subQ0=sQuery(id+"F25.wireOp",EDGE,"E335.MirrorCS");var subQ5=sQuery(id+"F25.wireOp",EDGE,"E387.MirrorCS");var subQ6=makeQuery(id+"F25.imprint","INTERSECT",VERTEX,{"derivedFrom":[subQ0,subQ5]});Q476=makeQuery(id+"F25.imprint","IMPRINT",FACE,{"disambiguationData":[TD([[makeQuery(id+"F25.imprint","IMPRINT",EDGE,{"disambiguationData":[TD([[subQ6,1.0]])],"derivedFrom":subQ5}),1.0]])]});}
            var Q477;
            {var subQ0=sQuery(id+"F25.wireOp",EDGE,"E234.right");Q477=makeQuery(id+"F25.imprint","IMPRINT",FACE,{"disambiguationData":[TD([[makeQuery(id+"F25.imprint","IMPRINT",EDGE,{"derivedFrom":subQ0}),1.0]])]});}
            var Q478;
            {var subQ0=sQuery(id+"F25.wireOp",EDGE,"E232.right");Q478=makeQuery(id+"F25.imprint","IMPRINT",FACE,{"disambiguationData":[TD([[makeQuery(id+"F25.imprint","IMPRINT",EDGE,{"derivedFrom":subQ0}),-1.0]])]});}
            var Q479;
            {var subQ5=sQuery(id+"F25.wireOp",EDGE,"E234.right");Q479=makeQuery(id+"F25.imprint","IMPRINT",FACE,{"disambiguationData":[TD([[makeQuery(id+"F25.imprint","IMPRINT",EDGE,{"derivedFrom":subQ5}),-1.0]])]});}
            var Q480;
            {var subQ5=sQuery(id+"F25.wireOp",EDGE,"E232.right");Q480=makeQuery(id+"F25.imprint","IMPRINT",FACE,{"disambiguationData":[TD([[makeQuery(id+"F25.imprint","IMPRINT",EDGE,{"derivedFrom":subQ5}),1.0]])]});}
            var Q481;
            {var subQ0=sQuery(id+"F25.wireOp",EDGE,"E522.trimOffspring");var subQ1=sQuery(id+"F25.wireOp",EDGE,"E249.right");var subQ2=makeQuery(id+"F25.imprint","INTERSECT",VERTEX,{"derivedFrom":[subQ1,subQ0]});Q481=makeQuery(id+"F25.imprint","IMPRINT",FACE,{"disambiguationData":[TD([[makeQuery(id+"F25.imprint","IMPRINT",EDGE,{"disambiguationData":[TD([[subQ2,-1.0]])],"derivedFrom":subQ1}),1.0]])]});}
            var Q482;
            {var subQ0=sQuery(id+"F25.wireOp",EDGE,"E524.trimOffspring");var subQ1=sQuery(id+"F25.wireOp",EDGE,"E249.right");var subQ2=makeQuery(id+"F25.imprint","INTERSECT",VERTEX,{"derivedFrom":[subQ1,subQ0]});Q482=makeQuery(id+"F25.imprint","IMPRINT",FACE,{"disambiguationData":[TD([[makeQuery(id+"F25.imprint","IMPRINT",EDGE,{"disambiguationData":[TD([[subQ2,-1.0]])],"derivedFrom":subQ1}),1.0]])]});}
            var Q483;
            {var subQ0=sQuery(id+"F25.wireOp",EDGE,"E522.trimOffspring");var subQ1=sQuery(id+"F25.wireOp",EDGE,"E250.right");var subQ2=makeQuery(id+"F25.imprint","INTERSECT",VERTEX,{"derivedFrom":[subQ1,subQ0]});Q483=makeQuery(id+"F25.imprint","IMPRINT",FACE,{"disambiguationData":[TD([[makeQuery(id+"F25.imprint","IMPRINT",EDGE,{"disambiguationData":[TD([[subQ2,-1.0]])],"derivedFrom":subQ1}),1.0]])]});}
            var Q484;
            {var subQ0=sQuery(id+"F25.wireOp",EDGE,"E522.trimOffspring");var subQ1=sQuery(id+"F25.wireOp",EDGE,"E250.left");var subQ2=makeQuery(id+"F25.imprint","INTERSECT",VERTEX,{"derivedFrom":[subQ1,subQ0]});Q484=makeQuery(id+"F25.imprint","IMPRINT",FACE,{"disambiguationData":[TD([[makeQuery(id+"F25.imprint","IMPRINT",EDGE,{"disambiguationData":[TD([[subQ2,-1.0]])],"derivedFrom":subQ1}),1.0]])]});}
            var Q485;
            {var subQ0=sQuery(id+"F25.wireOp",EDGE,"E524.trimOffspring");var subQ1=sQuery(id+"F25.wireOp",EDGE,"E250.left");var subQ2=makeQuery(id+"F25.imprint","INTERSECT",VERTEX,{"derivedFrom":[subQ1,subQ0]});Q485=makeQuery(id+"F25.imprint","IMPRINT",FACE,{"disambiguationData":[TD([[makeQuery(id+"F25.imprint","IMPRINT",EDGE,{"disambiguationData":[TD([[subQ2,-1.0]])],"derivedFrom":subQ1}),1.0]])]});}
            var Q486;
            {var subQ0=sQuery(id+"F25.wireOp",EDGE,"E524.trimOffspring");var subQ1=sQuery(id+"F25.wireOp",EDGE,"E250.right");var subQ2=makeQuery(id+"F25.imprint","INTERSECT",VERTEX,{"derivedFrom":[subQ1,subQ0]});Q486=makeQuery(id+"F25.imprint","IMPRINT",FACE,{"disambiguationData":[TD([[makeQuery(id+"F25.imprint","IMPRINT",EDGE,{"disambiguationData":[TD([[subQ2,-1.0]])],"derivedFrom":subQ1}),1.0]])]});}
            var Q487;
            {var subQ0=sQuery(id+"F25.wireOp",EDGE,"E525.trimOffspring");var subQ1=sQuery(id+"F25.wireOp",EDGE,"E250.right");var subQ2=makeQuery(id+"F25.imprint","INTERSECT",VERTEX,{"derivedFrom":[subQ1,subQ0]});Q487=makeQuery(id+"F25.imprint","IMPRINT",FACE,{"disambiguationData":[TD([[makeQuery(id+"F25.imprint","IMPRINT",EDGE,{"disambiguationData":[TD([[subQ2,-1.0]])],"derivedFrom":subQ1}),1.0]])]});}
            var Q488;
            {var subQ0=sQuery(id+"F25.wireOp",EDGE,"E334.MirrorCS");var subQ1=sQuery(id+"F25.wireOp",EDGE,"E324.MirrorCS");var subQ2=makeQuery(id+"F25.imprint","INTERSECT",VERTEX,{"derivedFrom":[subQ1,subQ0]});Q488=makeQuery(id+"F25.imprint","IMPRINT",FACE,{"disambiguationData":[TD([[makeQuery(id+"F25.imprint","IMPRINT",EDGE,{"disambiguationData":[TD([[subQ2,-1.0]])],"derivedFrom":subQ1}),1.0]])]});}
            var Q489;
            {var subQ0=sQuery(id+"F25.wireOp",EDGE,"E365.MirrorCS");var subQ1=sQuery(id+"F25.wireOp",EDGE,"E324.MirrorCS");var subQ2=makeQuery(id+"F25.imprint","INTERSECT",VERTEX,{"derivedFrom":[subQ1,subQ0]});Q489=makeQuery(id+"F25.imprint","IMPRINT",FACE,{"disambiguationData":[TD([[makeQuery(id+"F25.imprint","IMPRINT",EDGE,{"disambiguationData":[TD([[subQ2,-1.0]])],"derivedFrom":subQ1}),1.0]])]});}
            var Q490;
            {var subQ0=sQuery(id+"F25.wireOp",EDGE,"E334.MirrorCS");var subQ1=sQuery(id+"F25.wireOp",EDGE,"E349.MirrorCS");var subQ2=makeQuery(id+"F25.imprint","INTERSECT",VERTEX,{"derivedFrom":[subQ1,subQ0]});Q490=makeQuery(id+"F25.imprint","IMPRINT",FACE,{"disambiguationData":[TD([[makeQuery(id+"F25.imprint","IMPRINT",EDGE,{"disambiguationData":[TD([[subQ2,-1.0]])],"derivedFrom":subQ1}),-1.0]])]});}
            var Q491;
            {var subQ0=sQuery(id+"F25.wireOp",EDGE,"E365.MirrorCS");var subQ1=sQuery(id+"F25.wireOp",EDGE,"E349.MirrorCS");var subQ2=makeQuery(id+"F25.imprint","INTERSECT",VERTEX,{"derivedFrom":[subQ1,subQ0]});Q491=makeQuery(id+"F25.imprint","IMPRINT",FACE,{"disambiguationData":[TD([[makeQuery(id+"F25.imprint","IMPRINT",EDGE,{"disambiguationData":[TD([[subQ2,-1.0]])],"derivedFrom":subQ1}),-1.0]])]});}
            var Q492;
            {var subQ0=sQuery(id+"F25.wireOp",EDGE,"E525.trimOffspring");var subQ1=sQuery(id+"F25.wireOp",EDGE,"E250.left");var subQ2=makeQuery(id+"F25.imprint","INTERSECT",VERTEX,{"derivedFrom":[subQ1,subQ0]});Q492=makeQuery(id+"F25.imprint","IMPRINT",FACE,{"disambiguationData":[TD([[makeQuery(id+"F25.imprint","IMPRINT",EDGE,{"disambiguationData":[TD([[subQ2,-1.0]])],"derivedFrom":subQ1}),1.0]])]});}
            var Q493;
            {var subQ0=sQuery(id+"F25.wireOp",EDGE,"E285.trimOffspring");var subQ1=sQuery(id+"F25.wireOp",EDGE,"E250.left");var subQ2=makeQuery(id+"F25.imprint","INTERSECT",VERTEX,{"derivedFrom":[subQ1,subQ0]});Q493=makeQuery(id+"F25.imprint","IMPRINT",FACE,{"disambiguationData":[TD([[makeQuery(id+"F25.imprint","IMPRINT",EDGE,{"disambiguationData":[TD([[subQ2,-1.0]])],"derivedFrom":subQ1}),1.0]])]});}
            var Q494;
            {var subQ0=sQuery(id+"F25.wireOp",EDGE,"E286.trimOffspring");var subQ1=sQuery(id+"F25.wireOp",EDGE,"E250.left");var subQ2=makeQuery(id+"F25.imprint","INTERSECT",VERTEX,{"derivedFrom":[subQ1,subQ0]});Q494=makeQuery(id+"F25.imprint","IMPRINT",FACE,{"disambiguationData":[TD([[makeQuery(id+"F25.imprint","IMPRINT",EDGE,{"disambiguationData":[TD([[subQ2,-1.0]])],"derivedFrom":subQ1}),1.0]])]});}
            var Q495;
            {var subQ0=sQuery(id+"F25.wireOp",EDGE,"E285.trimOffspring");var subQ1=sQuery(id+"F25.wireOp",EDGE,"E250.right");var subQ2=makeQuery(id+"F25.imprint","INTERSECT",VERTEX,{"derivedFrom":[subQ1,subQ0]});Q495=makeQuery(id+"F25.imprint","IMPRINT",FACE,{"disambiguationData":[TD([[makeQuery(id+"F25.imprint","IMPRINT",EDGE,{"disambiguationData":[TD([[subQ2,-1.0]])],"derivedFrom":subQ1}),1.0]])]});}
            var Q496;
            {var subQ0=sQuery(id+"F25.wireOp",EDGE,"E286.trimOffspring");var subQ1=sQuery(id+"F25.wireOp",EDGE,"E250.right");var subQ2=makeQuery(id+"F25.imprint","INTERSECT",VERTEX,{"derivedFrom":[subQ1,subQ0]});Q496=makeQuery(id+"F25.imprint","IMPRINT",FACE,{"disambiguationData":[TD([[makeQuery(id+"F25.imprint","IMPRINT",EDGE,{"disambiguationData":[TD([[subQ2,-1.0]])],"derivedFrom":subQ1}),1.0]])]});}
            var Q497;
            {var subQ0=sQuery(id+"F25.wireOp",EDGE,"E223.right");Q497=makeQuery(id+"F25.imprint","IMPRINT",FACE,{"disambiguationData":[TD([[makeQuery(id+"F25.imprint","IMPRINT",EDGE,{"derivedFrom":subQ0}),1.0]])]});}
            var Q498;
            {var subQ0=sQuery(id+"F25.wireOp",EDGE,"E224.right");Q498=makeQuery(id+"F25.imprint","IMPRINT",FACE,{"disambiguationData":[TD([[makeQuery(id+"F25.imprint","IMPRINT",EDGE,{"derivedFrom":subQ0}),-1.0]])]});}
            var Q499;
            {var subQ5=sQuery(id+"F25.wireOp",EDGE,"E224.right");Q499=makeQuery(id+"F25.imprint","IMPRINT",FACE,{"disambiguationData":[TD([[makeQuery(id+"F25.imprint","IMPRINT",EDGE,{"derivedFrom":subQ5}),1.0]])]});}
            var Q500;
            {var subQ5=sQuery(id+"F25.wireOp",EDGE,"E223.right");Q500=makeQuery(id+"F25.imprint","IMPRINT",FACE,{"disambiguationData":[TD([[makeQuery(id+"F25.imprint","IMPRINT",EDGE,{"derivedFrom":subQ5}),-1.0]])]});}
            var Q501;
            {var subQ0=sQuery(id+"F25.wireOp",EDGE,"E285.trimOffspring");var subQ1=sQuery(id+"F25.wireOp",EDGE,"E249.right");var subQ2=makeQuery(id+"F25.imprint","INTERSECT",VERTEX,{"derivedFrom":[subQ1,subQ0]});Q501=makeQuery(id+"F25.imprint","IMPRINT",FACE,{"disambiguationData":[TD([[makeQuery(id+"F25.imprint","IMPRINT",EDGE,{"disambiguationData":[TD([[subQ2,-1.0]])],"derivedFrom":subQ1}),1.0]])]});}
            var Q502;
            {var subQ0=sQuery(id+"F25.wireOp",EDGE,"E286.trimOffspring");var subQ1=sQuery(id+"F25.wireOp",EDGE,"E249.right");var subQ2=makeQuery(id+"F25.imprint","INTERSECT",VERTEX,{"derivedFrom":[subQ1,subQ0]});Q502=makeQuery(id+"F25.imprint","IMPRINT",FACE,{"disambiguationData":[TD([[makeQuery(id+"F25.imprint","IMPRINT",EDGE,{"disambiguationData":[TD([[subQ2,-1.0]])],"derivedFrom":subQ1}),1.0]])]});}
            var Q503;
            {var subQ0=sQuery(id+"F25.wireOp",EDGE,"E235.right");Q503=makeQuery(id+"F25.imprint","IMPRINT",FACE,{"disambiguationData":[TD([[makeQuery(id+"F25.imprint","IMPRINT",EDGE,{"derivedFrom":subQ0}),-1.0]])]});}
            var Q504;
            {var subQ0=sQuery(id+"F25.wireOp",EDGE,"E299.MirrorCS");Q504=makeQuery(id+"F25.imprint","IMPRINT",FACE,{"disambiguationData":[TD([[makeQuery(id+"F25.imprint","IMPRINT",EDGE,{"derivedFrom":subQ0}),1.0]])]});}
            var Q505;
            {var subQ0=sQuery(id+"F25.wireOp",EDGE,"E364.MirrorCS");var subQ1=sQuery(id+"F25.wireOp",EDGE,"E332.MirrorCS");var subQ2=makeQuery(id+"F25.imprint","INTERSECT",VERTEX,{"derivedFrom":[subQ1,subQ0]});Q505=makeQuery(id+"F25.imprint","IMPRINT",FACE,{"disambiguationData":[TD([[makeQuery(id+"F25.imprint","IMPRINT",EDGE,{"disambiguationData":[TD([[subQ2,-1.0]])],"derivedFrom":subQ1}),-1.0]])]});}
            var Q506;
            {var subQ0=sQuery(id+"F25.wireOp",EDGE,"E340.MirrorCS");var subQ1=sQuery(id+"F25.wireOp",EDGE,"E364.MirrorCS");var subQ2=makeQuery(id+"F25.imprint","INTERSECT",VERTEX,{"derivedFrom":[subQ1,subQ0]});Q506=makeQuery(id+"F25.imprint","IMPRINT",FACE,{"disambiguationData":[TD([[makeQuery(id+"F25.imprint","IMPRINT",EDGE,{"disambiguationData":[TD([[subQ2,-1.0]])],"derivedFrom":subQ1}),1.0]])]});}
            var Q507;
            {var subQ0=sQuery(id+"F25.wireOp",EDGE,"E364.MirrorCS");var subQ1=sQuery(id+"F25.wireOp",EDGE,"E363.MirrorCS");var subQ2=makeQuery(id+"F25.imprint","INTERSECT",VERTEX,{"derivedFrom":[subQ1,subQ0]});Q507=makeQuery(id+"F25.imprint","IMPRINT",FACE,{"disambiguationData":[TD([[makeQuery(id+"F25.imprint","IMPRINT",EDGE,{"disambiguationData":[TD([[subQ2,-1.0]])],"derivedFrom":subQ1}),1.0]])]});}
            var Q508;
            {var subQ0=sQuery(id+"F25.wireOp",EDGE,"E388.MirrorCS");var subQ1=sQuery(id+"F25.wireOp",EDGE,"E332.MirrorCS");var subQ2=makeQuery(id+"F25.imprint","INTERSECT",VERTEX,{"derivedFrom":[subQ1,subQ0]});Q508=makeQuery(id+"F25.imprint","IMPRINT",FACE,{"disambiguationData":[TD([[makeQuery(id+"F25.imprint","IMPRINT",EDGE,{"disambiguationData":[TD([[subQ2,-1.0]])],"derivedFrom":subQ1}),-1.0]])]});}
            var Q509;
            {var subQ0=sQuery(id+"F25.wireOp",EDGE,"E340.MirrorCS");var subQ1=sQuery(id+"F25.wireOp",EDGE,"E364.MirrorCS");var subQ2=makeQuery(id+"F25.imprint","INTERSECT",VERTEX,{"derivedFrom":[subQ1,subQ0]});Q509=makeQuery(id+"F25.imprint","IMPRINT",FACE,{"disambiguationData":[TD([[makeQuery(id+"F25.imprint","IMPRINT",EDGE,{"disambiguationData":[TD([[subQ2,-1.0]])],"derivedFrom":subQ1}),-1.0]])]});}
            var Q510;
            {var subQ0=sQuery(id+"F25.wireOp",EDGE,"E359.MirrorCS");var subQ1=sQuery(id+"F25.wireOp",EDGE,"E332.MirrorCS");var subQ2=makeQuery(id+"F25.imprint","INTERSECT",VERTEX,{"derivedFrom":[subQ1,subQ0]});Q510=makeQuery(id+"F25.imprint","IMPRINT",FACE,{"disambiguationData":[TD([[makeQuery(id+"F25.imprint","IMPRINT",EDGE,{"disambiguationData":[TD([[subQ2,-1.0]])],"derivedFrom":subQ1}),-1.0]])]});}
            var Q511;
            {var subQ0=sQuery(id+"F25.wireOp",EDGE,"E340.MirrorCS");var subQ1=sQuery(id+"F25.wireOp",EDGE,"E359.MirrorCS");var subQ2=makeQuery(id+"F25.imprint","INTERSECT",VERTEX,{"derivedFrom":[subQ1,subQ0]});Q511=makeQuery(id+"F25.imprint","IMPRINT",FACE,{"disambiguationData":[TD([[makeQuery(id+"F25.imprint","IMPRINT",EDGE,{"disambiguationData":[TD([[subQ2,-1.0]])],"derivedFrom":subQ1}),1.0]])]});}
            var Q512;
            {var subQ0=sQuery(id+"F25.wireOp",EDGE,"E342.MirrorCS");var subQ1=sQuery(id+"F25.wireOp",EDGE,"E332.MirrorCS");var subQ2=makeQuery(id+"F25.imprint","INTERSECT",VERTEX,{"derivedFrom":[subQ1,subQ0]});Q512=makeQuery(id+"F25.imprint","IMPRINT",FACE,{"disambiguationData":[TD([[makeQuery(id+"F25.imprint","IMPRINT",EDGE,{"disambiguationData":[TD([[subQ2,-1.0]])],"derivedFrom":subQ1}),-1.0]])]});}
            var Q513;
            {var subQ0=sQuery(id+"F25.wireOp",EDGE,"E340.MirrorCS");var subQ1=sQuery(id+"F25.wireOp",EDGE,"E342.MirrorCS");var subQ2=makeQuery(id+"F25.imprint","INTERSECT",VERTEX,{"derivedFrom":[subQ1,subQ0]});Q513=makeQuery(id+"F25.imprint","IMPRINT",FACE,{"disambiguationData":[TD([[makeQuery(id+"F25.imprint","IMPRINT",EDGE,{"disambiguationData":[TD([[subQ2,-1.0]])],"derivedFrom":subQ1}),1.0]])]});}
            var Q514;
            {var subQ0=sQuery(id+"F25.wireOp",EDGE,"E332.MirrorCS");var subQ1=sQuery(id+"F25.wireOp",EDGE,"E328.MirrorCS");var subQ2=makeQuery(id+"F25.imprint","INTERSECT",VERTEX,{"derivedFrom":[subQ1,subQ0]});Q514=makeQuery(id+"F25.imprint","IMPRINT",FACE,{"disambiguationData":[TD([[makeQuery(id+"F25.imprint","IMPRINT",EDGE,{"disambiguationData":[TD([[subQ2,-1.0]])],"derivedFrom":subQ1}),1.0]])]});}
            var Q515;
            {var subQ0=sQuery(id+"F25.wireOp",EDGE,"E340.MirrorCS");var subQ1=sQuery(id+"F25.wireOp",EDGE,"E328.MirrorCS");var subQ2=makeQuery(id+"F25.imprint","INTERSECT",VERTEX,{"derivedFrom":[subQ1,subQ0]});Q515=makeQuery(id+"F25.imprint","IMPRINT",FACE,{"disambiguationData":[TD([[makeQuery(id+"F25.imprint","IMPRINT",EDGE,{"disambiguationData":[TD([[subQ2,-1.0]])],"derivedFrom":subQ1}),1.0]])]});}
            var Q516;
            {var subQ0=sQuery(id+"F25.wireOp",EDGE,"E340.MirrorCS");var subQ1=sQuery(id+"F25.wireOp",EDGE,"E328.MirrorCS");var subQ2=makeQuery(id+"F25.imprint","INTERSECT",VERTEX,{"derivedFrom":[subQ1,subQ0]});Q516=makeQuery(id+"F25.imprint","IMPRINT",FACE,{"disambiguationData":[TD([[makeQuery(id+"F25.imprint","IMPRINT",EDGE,{"disambiguationData":[TD([[subQ2,-1.0]])],"derivedFrom":subQ1}),-1.0]])]});}
            var Q517;
            {var subQ0=sQuery(id+"F25.wireOp",EDGE,"E332.MirrorCS");var subQ1=sQuery(id+"F25.wireOp",EDGE,"E328.MirrorCS");var subQ2=makeQuery(id+"F25.imprint","INTERSECT",VERTEX,{"derivedFrom":[subQ1,subQ0]});Q517=makeQuery(id+"F25.imprint","IMPRINT",FACE,{"disambiguationData":[TD([[makeQuery(id+"F25.imprint","IMPRINT",EDGE,{"disambiguationData":[TD([[subQ2,-1.0]])],"derivedFrom":subQ1}),-1.0]])]});}
            var Q518;
            {var subQ0=sQuery(id+"F25.wireOp",EDGE,"E358.MirrorCS");var subQ1=sQuery(id+"F25.wireOp",EDGE,"E332.MirrorCS");var subQ2=makeQuery(id+"F25.imprint","INTERSECT",VERTEX,{"derivedFrom":[subQ1,subQ0]});Q518=makeQuery(id+"F25.imprint","IMPRINT",FACE,{"disambiguationData":[TD([[makeQuery(id+"F25.imprint","IMPRINT",EDGE,{"disambiguationData":[TD([[subQ2,-1.0]])],"derivedFrom":subQ1}),-1.0]])]});}
            var Q519;
            {var subQ0=sQuery(id+"F25.wireOp",EDGE,"E340.MirrorCS");var subQ1=sQuery(id+"F25.wireOp",EDGE,"E358.MirrorCS");var subQ2=makeQuery(id+"F25.imprint","INTERSECT",VERTEX,{"derivedFrom":[subQ1,subQ0]});Q519=makeQuery(id+"F25.imprint","IMPRINT",FACE,{"disambiguationData":[TD([[makeQuery(id+"F25.imprint","IMPRINT",EDGE,{"disambiguationData":[TD([[subQ2,-1.0]])],"derivedFrom":subQ1}),1.0]])]});}
            var Q520;
            {var subQ0=sQuery(id+"F25.wireOp",EDGE,"E364.MirrorCS");var subQ1=sQuery(id+"F25.wireOp",EDGE,"E331.MirrorCS");var subQ2=makeQuery(id+"F25.imprint","INTERSECT",VERTEX,{"derivedFrom":[subQ1,subQ0]});Q520=makeQuery(id+"F25.imprint","IMPRINT",FACE,{"disambiguationData":[TD([[makeQuery(id+"F25.imprint","IMPRINT",EDGE,{"disambiguationData":[TD([[subQ2,-1.0]])],"derivedFrom":subQ1}),1.0]])]});}
            var Q521;
            {var subQ0=sQuery(id+"F25.wireOp",EDGE,"E388.MirrorCS");var subQ1=sQuery(id+"F25.wireOp",EDGE,"E331.MirrorCS");var subQ2=makeQuery(id+"F25.imprint","INTERSECT",VERTEX,{"derivedFrom":[subQ1,subQ0]});Q521=makeQuery(id+"F25.imprint","IMPRINT",FACE,{"disambiguationData":[TD([[makeQuery(id+"F25.imprint","IMPRINT",EDGE,{"disambiguationData":[TD([[subQ2,-1.0]])],"derivedFrom":subQ1}),1.0]])]});}
            var Q522;
            {var subQ0=sQuery(id+"F25.wireOp",EDGE,"E364.MirrorCS");var subQ1=sQuery(id+"F25.wireOp",EDGE,"E331.MirrorCS");var subQ2=makeQuery(id+"F25.imprint","INTERSECT",VERTEX,{"derivedFrom":[subQ1,subQ0]});Q522=makeQuery(id+"F25.imprint","IMPRINT",FACE,{"disambiguationData":[TD([[makeQuery(id+"F25.imprint","IMPRINT",EDGE,{"disambiguationData":[TD([[subQ2,-1.0]])],"derivedFrom":subQ1}),-1.0]])]});}
            var Q523;
            {var subQ0=sQuery(id+"F25.wireOp",EDGE,"E388.MirrorCS");var subQ1=sQuery(id+"F25.wireOp",EDGE,"E331.MirrorCS");var subQ2=makeQuery(id+"F25.imprint","INTERSECT",VERTEX,{"derivedFrom":[subQ1,subQ0]});Q523=makeQuery(id+"F25.imprint","IMPRINT",FACE,{"disambiguationData":[TD([[makeQuery(id+"F25.imprint","IMPRINT",EDGE,{"disambiguationData":[TD([[subQ2,-1.0]])],"derivedFrom":subQ1}),-1.0]])]});}
            var Q524;
            {var subQ0=sQuery(id+"F25.wireOp",EDGE,"E359.MirrorCS");var subQ1=sQuery(id+"F25.wireOp",EDGE,"E331.MirrorCS");var subQ2=makeQuery(id+"F25.imprint","INTERSECT",VERTEX,{"derivedFrom":[subQ1,subQ0]});Q524=makeQuery(id+"F25.imprint","IMPRINT",FACE,{"disambiguationData":[TD([[makeQuery(id+"F25.imprint","IMPRINT",EDGE,{"disambiguationData":[TD([[subQ2,-1.0]])],"derivedFrom":subQ1}),1.0]])]});}
            var Q525;
            {var subQ0=sQuery(id+"F25.wireOp",EDGE,"E363.MirrorCS");var subQ1=sQuery(id+"F25.wireOp",EDGE,"E342.MirrorCS");var subQ2=makeQuery(id+"F25.imprint","INTERSECT",VERTEX,{"derivedFrom":[subQ1,subQ0]});Q525=makeQuery(id+"F25.imprint","IMPRINT",FACE,{"disambiguationData":[TD([[makeQuery(id+"F25.imprint","IMPRINT",EDGE,{"disambiguationData":[TD([[subQ2,-1.0]])],"derivedFrom":subQ1}),1.0]])]});}
            var Q526;
            {var subQ0=sQuery(id+"F25.wireOp",EDGE,"E363.MirrorCS");var subQ1=sQuery(id+"F25.wireOp",EDGE,"E328.MirrorCS");var subQ2=makeQuery(id+"F25.imprint","INTERSECT",VERTEX,{"derivedFrom":[subQ1,subQ0]});Q526=makeQuery(id+"F25.imprint","IMPRINT",FACE,{"disambiguationData":[TD([[makeQuery(id+"F25.imprint","IMPRINT",EDGE,{"disambiguationData":[TD([[subQ2,-1.0]])],"derivedFrom":subQ1}),1.0]])]});}
            var Q527;
            {var subQ0=sQuery(id+"F25.wireOp",EDGE,"E363.MirrorCS");var subQ1=sQuery(id+"F25.wireOp",EDGE,"E328.MirrorCS");var subQ2=makeQuery(id+"F25.imprint","INTERSECT",VERTEX,{"derivedFrom":[subQ1,subQ0]});Q527=makeQuery(id+"F25.imprint","IMPRINT",FACE,{"disambiguationData":[TD([[makeQuery(id+"F25.imprint","IMPRINT",EDGE,{"disambiguationData":[TD([[subQ2,-1.0]])],"derivedFrom":subQ1}),-1.0]])]});}
            var Q528;
            {var subQ0=sQuery(id+"F25.wireOp",EDGE,"E358.MirrorCS");var subQ1=sQuery(id+"F25.wireOp",EDGE,"E331.MirrorCS");var subQ2=makeQuery(id+"F25.imprint","INTERSECT",VERTEX,{"derivedFrom":[subQ1,subQ0]});Q528=makeQuery(id+"F25.imprint","IMPRINT",FACE,{"disambiguationData":[TD([[makeQuery(id+"F25.imprint","IMPRINT",EDGE,{"disambiguationData":[TD([[subQ2,-1.0]])],"derivedFrom":subQ1}),1.0]])]});}
            var Q529;
            {var subQ0=sQuery(id+"F25.wireOp",EDGE,"E359.MirrorCS");var subQ1=sQuery(id+"F25.wireOp",EDGE,"E331.MirrorCS");var subQ2=makeQuery(id+"F25.imprint","INTERSECT",VERTEX,{"derivedFrom":[subQ1,subQ0]});Q529=makeQuery(id+"F25.imprint","IMPRINT",FACE,{"disambiguationData":[TD([[makeQuery(id+"F25.imprint","IMPRINT",EDGE,{"disambiguationData":[TD([[subQ2,-1.0]])],"derivedFrom":subQ1}),-1.0]])]});}
            var Q530;
            {var subQ0=sQuery(id+"F25.wireOp",EDGE,"E331.MirrorCS");var subQ1=sQuery(id+"F25.wireOp",EDGE,"E342.MirrorCS");var subQ2=makeQuery(id+"F25.imprint","INTERSECT",VERTEX,{"derivedFrom":[subQ1,subQ0]});Q530=makeQuery(id+"F25.imprint","IMPRINT",FACE,{"disambiguationData":[TD([[makeQuery(id+"F25.imprint","IMPRINT",EDGE,{"disambiguationData":[TD([[subQ2,-1.0]])],"derivedFrom":subQ1}),1.0]])]});}
            var Q531;
            {var subQ0=sQuery(id+"F25.wireOp",EDGE,"E331.MirrorCS");var subQ1=sQuery(id+"F25.wireOp",EDGE,"E328.MirrorCS");var subQ2=makeQuery(id+"F25.imprint","INTERSECT",VERTEX,{"derivedFrom":[subQ1,subQ0]});Q531=makeQuery(id+"F25.imprint","IMPRINT",FACE,{"disambiguationData":[TD([[makeQuery(id+"F25.imprint","IMPRINT",EDGE,{"disambiguationData":[TD([[subQ2,-1.0]])],"derivedFrom":subQ1}),1.0]])]});}
            var Q532;
            {var subQ0=sQuery(id+"F25.wireOp",EDGE,"E331.MirrorCS");var subQ1=sQuery(id+"F25.wireOp",EDGE,"E328.MirrorCS");var subQ2=makeQuery(id+"F25.imprint","INTERSECT",VERTEX,{"derivedFrom":[subQ1,subQ0]});Q532=makeQuery(id+"F25.imprint","IMPRINT",FACE,{"disambiguationData":[TD([[makeQuery(id+"F25.imprint","IMPRINT",EDGE,{"disambiguationData":[TD([[subQ2,-1.0]])],"derivedFrom":subQ1}),-1.0]])]});}
            var Q533;
            {var subQ0=sQuery(id+"F25.wireOp",EDGE,"E358.MirrorCS");var subQ1=sQuery(id+"F25.wireOp",EDGE,"E331.MirrorCS");var subQ2=makeQuery(id+"F25.imprint","INTERSECT",VERTEX,{"derivedFrom":[subQ1,subQ0]});Q533=makeQuery(id+"F25.imprint","IMPRINT",FACE,{"disambiguationData":[TD([[makeQuery(id+"F25.imprint","IMPRINT",EDGE,{"disambiguationData":[TD([[subQ2,-1.0]])],"derivedFrom":subQ1}),-1.0]])]});}
            var Q534;
            {var subQ0=sQuery(id+"F25.wireOp",EDGE,"E364.MirrorCS");var subQ1=sQuery(id+"F25.wireOp",EDGE,"E329.MirrorCS");var subQ2=makeQuery(id+"F25.imprint","INTERSECT",VERTEX,{"derivedFrom":[subQ1,subQ0]});Q534=makeQuery(id+"F25.imprint","IMPRINT",FACE,{"disambiguationData":[TD([[makeQuery(id+"F25.imprint","IMPRINT",EDGE,{"disambiguationData":[TD([[subQ2,-1.0]])],"derivedFrom":subQ1}),1.0]])]});}
            var Q535;
            {var subQ0=sQuery(id+"F25.wireOp",EDGE,"E364.MirrorCS");var subQ1=sQuery(id+"F25.wireOp",EDGE,"E329.MirrorCS");var subQ2=makeQuery(id+"F25.imprint","INTERSECT",VERTEX,{"derivedFrom":[subQ1,subQ0]});Q535=makeQuery(id+"F25.imprint","IMPRINT",FACE,{"disambiguationData":[TD([[makeQuery(id+"F25.imprint","IMPRINT",EDGE,{"disambiguationData":[TD([[subQ2,-1.0]])],"derivedFrom":subQ1}),-1.0]])]});}
            var Q536;
            {var subQ0=sQuery(id+"F25.wireOp",EDGE,"E364.MirrorCS");var subQ1=sQuery(id+"F25.wireOp",EDGE,"E354.MirrorCS");var subQ2=makeQuery(id+"F25.imprint","INTERSECT",VERTEX,{"derivedFrom":[subQ1,subQ0]});Q536=makeQuery(id+"F25.imprint","IMPRINT",FACE,{"disambiguationData":[TD([[makeQuery(id+"F25.imprint","IMPRINT",EDGE,{"disambiguationData":[TD([[subQ2,-1.0]])],"derivedFrom":subQ1}),1.0]])]});}
            var Q537;
            {var subQ0=sQuery(id+"F25.wireOp",EDGE,"E388.MirrorCS");var subQ1=sQuery(id+"F25.wireOp",EDGE,"E329.MirrorCS");var subQ2=makeQuery(id+"F25.imprint","INTERSECT",VERTEX,{"derivedFrom":[subQ1,subQ0]});Q537=makeQuery(id+"F25.imprint","IMPRINT",FACE,{"disambiguationData":[TD([[makeQuery(id+"F25.imprint","IMPRINT",EDGE,{"disambiguationData":[TD([[subQ2,-1.0]])],"derivedFrom":subQ1}),-1.0]])]});}
            var Q538;
            {var subQ0=sQuery(id+"F25.wireOp",EDGE,"E388.MirrorCS");var subQ1=sQuery(id+"F25.wireOp",EDGE,"E354.MirrorCS");var subQ2=makeQuery(id+"F25.imprint","INTERSECT",VERTEX,{"derivedFrom":[subQ1,subQ0]});Q538=makeQuery(id+"F25.imprint","IMPRINT",FACE,{"disambiguationData":[TD([[makeQuery(id+"F25.imprint","IMPRINT",EDGE,{"disambiguationData":[TD([[subQ2,-1.0]])],"derivedFrom":subQ1}),1.0]])]});}
            var Q539;
            {var subQ0=sQuery(id+"F25.wireOp",EDGE,"E359.MirrorCS");var subQ1=sQuery(id+"F25.wireOp",EDGE,"E329.MirrorCS");var subQ2=makeQuery(id+"F25.imprint","INTERSECT",VERTEX,{"derivedFrom":[subQ1,subQ0]});Q539=makeQuery(id+"F25.imprint","IMPRINT",FACE,{"disambiguationData":[TD([[makeQuery(id+"F25.imprint","IMPRINT",EDGE,{"disambiguationData":[TD([[subQ2,-1.0]])],"derivedFrom":subQ1}),-1.0]])]});}
            var Q540;
            {var subQ0=sQuery(id+"F25.wireOp",EDGE,"E359.MirrorCS");var subQ1=sQuery(id+"F25.wireOp",EDGE,"E354.MirrorCS");var subQ2=makeQuery(id+"F25.imprint","INTERSECT",VERTEX,{"derivedFrom":[subQ1,subQ0]});Q540=makeQuery(id+"F25.imprint","IMPRINT",FACE,{"disambiguationData":[TD([[makeQuery(id+"F25.imprint","IMPRINT",EDGE,{"disambiguationData":[TD([[subQ2,-1.0]])],"derivedFrom":subQ1}),1.0]])]});}
            var Q541;
            {var subQ0=sQuery(id+"F25.wireOp",EDGE,"E342.MirrorCS");var subQ1=sQuery(id+"F25.wireOp",EDGE,"E329.MirrorCS");var subQ2=makeQuery(id+"F25.imprint","INTERSECT",VERTEX,{"derivedFrom":[subQ1,subQ0]});Q541=makeQuery(id+"F25.imprint","IMPRINT",FACE,{"disambiguationData":[TD([[makeQuery(id+"F25.imprint","IMPRINT",EDGE,{"disambiguationData":[TD([[subQ2,-1.0]])],"derivedFrom":subQ1}),-1.0]])]});}
            var Q542;
            {var subQ0=sQuery(id+"F25.wireOp",EDGE,"E345.MirrorCS");var subQ1=sQuery(id+"F25.wireOp",EDGE,"E342.MirrorCS");var subQ2=makeQuery(id+"F25.imprint","INTERSECT",VERTEX,{"derivedFrom":[subQ1,subQ0]});Q542=makeQuery(id+"F25.imprint","IMPRINT",FACE,{"disambiguationData":[TD([[makeQuery(id+"F25.imprint","IMPRINT",EDGE,{"disambiguationData":[TD([[subQ2,-1.0]])],"derivedFrom":subQ1}),1.0]])]});}
            var Q543;
            {var subQ0=sQuery(id+"F25.wireOp",EDGE,"E329.MirrorCS");var subQ1=sQuery(id+"F25.wireOp",EDGE,"E328.MirrorCS");var subQ2=makeQuery(id+"F25.imprint","INTERSECT",VERTEX,{"derivedFrom":[subQ1,subQ0]});Q543=makeQuery(id+"F25.imprint","IMPRINT",FACE,{"disambiguationData":[TD([[makeQuery(id+"F25.imprint","IMPRINT",EDGE,{"disambiguationData":[TD([[subQ2,-1.0]])],"derivedFrom":subQ1}),1.0]])]});}
            var Q544;
            {var subQ0=sQuery(id+"F25.wireOp",EDGE,"E345.MirrorCS");var subQ1=sQuery(id+"F25.wireOp",EDGE,"E328.MirrorCS");var subQ2=makeQuery(id+"F25.imprint","INTERSECT",VERTEX,{"derivedFrom":[subQ1,subQ0]});Q544=makeQuery(id+"F25.imprint","IMPRINT",FACE,{"disambiguationData":[TD([[makeQuery(id+"F25.imprint","IMPRINT",EDGE,{"disambiguationData":[TD([[subQ2,-1.0]])],"derivedFrom":subQ1}),1.0]])]});}
            var Q545;
            {var subQ0=sQuery(id+"F25.wireOp",EDGE,"E329.MirrorCS");var subQ1=sQuery(id+"F25.wireOp",EDGE,"E328.MirrorCS");var subQ2=makeQuery(id+"F25.imprint","INTERSECT",VERTEX,{"derivedFrom":[subQ1,subQ0]});Q545=makeQuery(id+"F25.imprint","IMPRINT",FACE,{"disambiguationData":[TD([[makeQuery(id+"F25.imprint","IMPRINT",EDGE,{"disambiguationData":[TD([[subQ2,-1.0]])],"derivedFrom":subQ1}),-1.0]])]});}
            var Q546;
            {var subQ0=sQuery(id+"F25.wireOp",EDGE,"E345.MirrorCS");var subQ1=sQuery(id+"F25.wireOp",EDGE,"E328.MirrorCS");var subQ2=makeQuery(id+"F25.imprint","INTERSECT",VERTEX,{"derivedFrom":[subQ1,subQ0]});Q546=makeQuery(id+"F25.imprint","IMPRINT",FACE,{"disambiguationData":[TD([[makeQuery(id+"F25.imprint","IMPRINT",EDGE,{"disambiguationData":[TD([[subQ2,-1.0]])],"derivedFrom":subQ1}),-1.0]])]});}
            var Q547;
            {var subQ0=sQuery(id+"F25.wireOp",EDGE,"E358.MirrorCS");var subQ1=sQuery(id+"F25.wireOp",EDGE,"E329.MirrorCS");var subQ2=makeQuery(id+"F25.imprint","INTERSECT",VERTEX,{"derivedFrom":[subQ1,subQ0]});Q547=makeQuery(id+"F25.imprint","IMPRINT",FACE,{"disambiguationData":[TD([[makeQuery(id+"F25.imprint","IMPRINT",EDGE,{"disambiguationData":[TD([[subQ2,-1.0]])],"derivedFrom":subQ1}),-1.0]])]});}
            var Q548;
            {var subQ0=sQuery(id+"F25.wireOp",EDGE,"E358.MirrorCS");var subQ1=sQuery(id+"F25.wireOp",EDGE,"E354.MirrorCS");var subQ2=makeQuery(id+"F25.imprint","INTERSECT",VERTEX,{"derivedFrom":[subQ1,subQ0]});Q548=makeQuery(id+"F25.imprint","IMPRINT",FACE,{"disambiguationData":[TD([[makeQuery(id+"F25.imprint","IMPRINT",EDGE,{"disambiguationData":[TD([[subQ2,-1.0]])],"derivedFrom":subQ1}),1.0]])]});}
            var Q549;
            {var subQ0=sQuery(id+"F25.wireOp",EDGE,"E358.MirrorCS");var subQ1=sQuery(id+"F25.wireOp",EDGE,"E354.MirrorCS");var subQ2=makeQuery(id+"F25.imprint","INTERSECT",VERTEX,{"derivedFrom":[subQ1,subQ0]});Q549=makeQuery(id+"F25.imprint","IMPRINT",FACE,{"disambiguationData":[TD([[makeQuery(id+"F25.imprint","IMPRINT",EDGE,{"disambiguationData":[TD([[subQ2,-1.0]])],"derivedFrom":subQ1}),-1.0]])]});}
            var Q550;
            {var subQ0=sQuery(id+"F25.wireOp",EDGE,"E384.MirrorCS");var subQ1=sQuery(id+"F25.wireOp",EDGE,"E358.MirrorCS");var subQ2=makeQuery(id+"F25.imprint","INTERSECT",VERTEX,{"derivedFrom":[subQ1,subQ0]});Q550=makeQuery(id+"F25.imprint","IMPRINT",FACE,{"disambiguationData":[TD([[makeQuery(id+"F25.imprint","IMPRINT",EDGE,{"disambiguationData":[TD([[subQ2,-1.0]])],"derivedFrom":subQ1}),1.0]])]});}
            var Q551;
            {var subQ0=sQuery(id+"F25.wireOp",EDGE,"E373.MirrorCS");var subQ1=sQuery(id+"F25.wireOp",EDGE,"E342.MirrorCS");var subQ2=makeQuery(id+"F25.imprint","INTERSECT",VERTEX,{"derivedFrom":[subQ1,subQ0]});Q551=makeQuery(id+"F25.imprint","IMPRINT",FACE,{"disambiguationData":[TD([[makeQuery(id+"F25.imprint","IMPRINT",EDGE,{"disambiguationData":[TD([[subQ2,-1.0]])],"derivedFrom":subQ1}),1.0]])]});}
            var Q552;
            {var subQ0=sQuery(id+"F25.wireOp",EDGE,"E344.MirrorCS");var subQ1=sQuery(id+"F25.wireOp",EDGE,"E342.MirrorCS");var subQ2=makeQuery(id+"F25.imprint","INTERSECT",VERTEX,{"derivedFrom":[subQ1,subQ0]});Q552=makeQuery(id+"F25.imprint","IMPRINT",FACE,{"disambiguationData":[TD([[makeQuery(id+"F25.imprint","IMPRINT",EDGE,{"disambiguationData":[TD([[subQ2,-1.0]])],"derivedFrom":subQ1}),1.0]])]});}
            var Q553;
            {var subQ0=sQuery(id+"F25.wireOp",EDGE,"E344.MirrorCS");var subQ1=sQuery(id+"F25.wireOp",EDGE,"E328.MirrorCS");var subQ2=makeQuery(id+"F25.imprint","INTERSECT",VERTEX,{"derivedFrom":[subQ1,subQ0]});Q553=makeQuery(id+"F25.imprint","IMPRINT",FACE,{"disambiguationData":[TD([[makeQuery(id+"F25.imprint","IMPRINT",EDGE,{"disambiguationData":[TD([[subQ2,-1.0]])],"derivedFrom":subQ1}),1.0]])]});}
            var Q554;
            {var subQ0=sQuery(id+"F25.wireOp",EDGE,"E344.MirrorCS");var subQ1=sQuery(id+"F25.wireOp",EDGE,"E328.MirrorCS");var subQ2=makeQuery(id+"F25.imprint","INTERSECT",VERTEX,{"derivedFrom":[subQ1,subQ0]});Q554=makeQuery(id+"F25.imprint","IMPRINT",FACE,{"disambiguationData":[TD([[makeQuery(id+"F25.imprint","IMPRINT",EDGE,{"disambiguationData":[TD([[subQ2,-1.0]])],"derivedFrom":subQ1}),-1.0]])]});}
            var Q555;
            {var subQ0=sQuery(id+"F25.wireOp",EDGE,"E344.MirrorCS");var subQ1=sQuery(id+"F25.wireOp",EDGE,"E358.MirrorCS");var subQ2=makeQuery(id+"F25.imprint","INTERSECT",VERTEX,{"derivedFrom":[subQ1,subQ0]});Q555=makeQuery(id+"F25.imprint","IMPRINT",FACE,{"disambiguationData":[TD([[makeQuery(id+"F25.imprint","IMPRINT",EDGE,{"disambiguationData":[TD([[subQ2,-1.0]])],"derivedFrom":subQ1}),1.0]])]});}
            var Q556;
            {var subQ0=sQuery(id+"F25.wireOp",EDGE,"E378.MirrorCS");var subQ1=sQuery(id+"F25.wireOp",EDGE,"E342.MirrorCS");var subQ2=makeQuery(id+"F25.imprint","INTERSECT",VERTEX,{"derivedFrom":[subQ1,subQ0]});Q556=makeQuery(id+"F25.imprint","IMPRINT",FACE,{"disambiguationData":[TD([[makeQuery(id+"F25.imprint","IMPRINT",EDGE,{"disambiguationData":[TD([[subQ2,-1.0]])],"derivedFrom":subQ1}),1.0]])]});}
            var Q557;
            {var subQ0=sQuery(id+"F25.wireOp",EDGE,"E378.MirrorCS");var subQ1=sQuery(id+"F25.wireOp",EDGE,"E328.MirrorCS");var subQ2=makeQuery(id+"F25.imprint","INTERSECT",VERTEX,{"derivedFrom":[subQ1,subQ0]});Q557=makeQuery(id+"F25.imprint","IMPRINT",FACE,{"disambiguationData":[TD([[makeQuery(id+"F25.imprint","IMPRINT",EDGE,{"disambiguationData":[TD([[subQ2,-1.0]])],"derivedFrom":subQ1}),1.0]])]});}
            var Q558;
            {var subQ0=sQuery(id+"F25.wireOp",EDGE,"E378.MirrorCS");var subQ1=sQuery(id+"F25.wireOp",EDGE,"E328.MirrorCS");var subQ2=makeQuery(id+"F25.imprint","INTERSECT",VERTEX,{"derivedFrom":[subQ1,subQ0]});Q558=makeQuery(id+"F25.imprint","IMPRINT",FACE,{"disambiguationData":[TD([[makeQuery(id+"F25.imprint","IMPRINT",EDGE,{"disambiguationData":[TD([[subQ2,-1.0]])],"derivedFrom":subQ1}),-1.0]])]});}
            var Q559;
            {var subQ0=sQuery(id+"F25.wireOp",EDGE,"E378.MirrorCS");var subQ1=sQuery(id+"F25.wireOp",EDGE,"E358.MirrorCS");var subQ2=makeQuery(id+"F25.imprint","INTERSECT",VERTEX,{"derivedFrom":[subQ1,subQ0]});Q559=makeQuery(id+"F25.imprint","IMPRINT",FACE,{"disambiguationData":[TD([[makeQuery(id+"F25.imprint","IMPRINT",EDGE,{"disambiguationData":[TD([[subQ2,-1.0]])],"derivedFrom":subQ1}),1.0]])]});}
            var Q560;
            {var subQ0=sQuery(id+"F25.wireOp",EDGE,"E348.MirrorCS");var subQ1=sQuery(id+"F25.wireOp",EDGE,"E358.MirrorCS");var subQ2=makeQuery(id+"F25.imprint","INTERSECT",VERTEX,{"derivedFrom":[subQ1,subQ0]});Q560=makeQuery(id+"F25.imprint","IMPRINT",FACE,{"disambiguationData":[TD([[makeQuery(id+"F25.imprint","IMPRINT",EDGE,{"disambiguationData":[TD([[subQ2,-1.0]])],"derivedFrom":subQ1}),1.0]])]});}
            var Q561;
            {var subQ0=sQuery(id+"F25.wireOp",EDGE,"E358.MirrorCS");var subQ1=sQuery(id+"F25.wireOp",EDGE,"E335.MirrorCS");var subQ2=makeQuery(id+"F25.imprint","INTERSECT",VERTEX,{"derivedFrom":[subQ1,subQ0]});Q561=makeQuery(id+"F25.imprint","IMPRINT",FACE,{"disambiguationData":[TD([[makeQuery(id+"F25.imprint","IMPRINT",EDGE,{"disambiguationData":[TD([[subQ2,-1.0]])],"derivedFrom":subQ1}),1.0]])]});}
            var Q562;
            {var subQ0=sQuery(id+"F25.wireOp",EDGE,"E358.MirrorCS");var subQ1=sQuery(id+"F25.wireOp",EDGE,"E335.MirrorCS");var subQ2=makeQuery(id+"F25.imprint","INTERSECT",VERTEX,{"derivedFrom":[subQ1,subQ0]});Q562=makeQuery(id+"F25.imprint","IMPRINT",FACE,{"disambiguationData":[TD([[makeQuery(id+"F25.imprint","IMPRINT",EDGE,{"disambiguationData":[TD([[subQ2,-1.0]])],"derivedFrom":subQ1}),-1.0]])]});}
            var Q563;
            {var subQ0=sQuery(id+"F25.wireOp",EDGE,"E393.MirrorCS");var subQ1=sQuery(id+"F25.wireOp",EDGE,"E335.MirrorCS");var subQ2=makeQuery(id+"F25.imprint","INTERSECT",VERTEX,{"derivedFrom":[subQ1,subQ0]});Q563=makeQuery(id+"F25.imprint","IMPRINT",FACE,{"disambiguationData":[TD([[makeQuery(id+"F25.imprint","IMPRINT",EDGE,{"disambiguationData":[TD([[subQ2,-1.0]])],"derivedFrom":subQ1}),-1.0]])]});}
            var Q564;
            {var subQ0=sQuery(id+"F25.wireOp",EDGE,"E335.MirrorCS");var subQ1=sQuery(id+"F25.wireOp",EDGE,"E326.MirrorCS");var subQ2=makeQuery(id+"F25.imprint","INTERSECT",VERTEX,{"derivedFrom":[subQ1,subQ0]});Q564=makeQuery(id+"F25.imprint","IMPRINT",FACE,{"disambiguationData":[TD([[makeQuery(id+"F25.imprint","IMPRINT",EDGE,{"disambiguationData":[TD([[subQ2,-1.0]])],"derivedFrom":subQ1}),1.0]])]});}
            var Q565;
            {var subQ0=sQuery(id+"F25.wireOp",EDGE,"E394.MirrorCS");var subQ1=sQuery(id+"F25.wireOp",EDGE,"E335.MirrorCS");var subQ2=makeQuery(id+"F25.imprint","INTERSECT",VERTEX,{"derivedFrom":[subQ1,subQ0]});Q565=makeQuery(id+"F25.imprint","IMPRINT",FACE,{"disambiguationData":[TD([[makeQuery(id+"F25.imprint","IMPRINT",EDGE,{"disambiguationData":[TD([[subQ2,-1.0]])],"derivedFrom":subQ1}),-1.0]])]});}
            var Q566;
            {var subQ0=sQuery(id+"F25.wireOp",EDGE,"E360.MirrorCS");var subQ1=sQuery(id+"F25.wireOp",EDGE,"E335.MirrorCS");var subQ2=makeQuery(id+"F25.imprint","INTERSECT",VERTEX,{"derivedFrom":[subQ1,subQ0]});Q566=makeQuery(id+"F25.imprint","IMPRINT",FACE,{"disambiguationData":[TD([[makeQuery(id+"F25.imprint","IMPRINT",EDGE,{"disambiguationData":[TD([[subQ2,-1.0]])],"derivedFrom":subQ1}),-1.0]])]});}
            var Q567;
            {var subQ0=sQuery(id+"F25.wireOp",EDGE,"E336.MirrorCS");var subQ1=sQuery(id+"F25.wireOp",EDGE,"E335.MirrorCS");var subQ2=makeQuery(id+"F25.imprint","INTERSECT",VERTEX,{"derivedFrom":[subQ1,subQ0]});Q567=makeQuery(id+"F25.imprint","IMPRINT",FACE,{"disambiguationData":[TD([[makeQuery(id+"F25.imprint","IMPRINT",EDGE,{"disambiguationData":[TD([[subQ2,-1.0]])],"derivedFrom":subQ1}),-1.0]])]});}
            var Q568;
            {var subQ0=sQuery(id+"F25.wireOp",EDGE,"E383.MirrorCS");var subQ1=sQuery(id+"F25.wireOp",EDGE,"E335.MirrorCS");var subQ2=makeQuery(id+"F25.imprint","INTERSECT",VERTEX,{"derivedFrom":[subQ1,subQ0]});Q568=makeQuery(id+"F25.imprint","IMPRINT",FACE,{"disambiguationData":[TD([[makeQuery(id+"F25.imprint","IMPRINT",EDGE,{"disambiguationData":[TD([[subQ2,-1.0]])],"derivedFrom":subQ1}),-1.0]])]});}
            var Q569;
            {var subQ0=sQuery(id+"F25.wireOp",EDGE,"E350.MirrorCS");var subQ1=sQuery(id+"F25.wireOp",EDGE,"E335.MirrorCS");var subQ2=makeQuery(id+"F25.imprint","INTERSECT",VERTEX,{"derivedFrom":[subQ1,subQ0]});Q569=makeQuery(id+"F25.imprint","IMPRINT",FACE,{"disambiguationData":[TD([[makeQuery(id+"F25.imprint","IMPRINT",EDGE,{"disambiguationData":[TD([[subQ2,-1.0]])],"derivedFrom":subQ1}),-1.0]])]});}
            var Q570;
            {var subQ0=sQuery(id+"F25.wireOp",EDGE,"E383.MirrorCS");var subQ1=sQuery(id+"F25.wireOp",EDGE,"E335.MirrorCS");var subQ2=makeQuery(id+"F25.imprint","INTERSECT",VERTEX,{"derivedFrom":[subQ1,subQ0]});Q570=makeQuery(id+"F25.imprint","IMPRINT",FACE,{"disambiguationData":[TD([[makeQuery(id+"F25.imprint","IMPRINT",EDGE,{"disambiguationData":[TD([[subQ2,-1.0]])],"derivedFrom":subQ1}),1.0]])]});}
            var Q571;
            {var subQ0=sQuery(id+"F25.wireOp",EDGE,"E350.MirrorCS");var subQ1=sQuery(id+"F25.wireOp",EDGE,"E335.MirrorCS");var subQ2=makeQuery(id+"F25.imprint","INTERSECT",VERTEX,{"derivedFrom":[subQ1,subQ0]});Q571=makeQuery(id+"F25.imprint","IMPRINT",FACE,{"disambiguationData":[TD([[makeQuery(id+"F25.imprint","IMPRINT",EDGE,{"disambiguationData":[TD([[subQ2,-1.0]])],"derivedFrom":subQ1}),1.0]])]});}
            var Q572;
            {var subQ0=sQuery(id+"F25.wireOp",EDGE,"E350.MirrorCS");var subQ1=sQuery(id+"F25.wireOp",EDGE,"E344.MirrorCS");var subQ2=makeQuery(id+"F25.imprint","INTERSECT",VERTEX,{"derivedFrom":[subQ1,subQ0]});Q572=makeQuery(id+"F25.imprint","IMPRINT",FACE,{"disambiguationData":[TD([[makeQuery(id+"F25.imprint","IMPRINT",EDGE,{"disambiguationData":[TD([[subQ2,-1.0]])],"derivedFrom":subQ1}),1.0]])]});}
            var Q573;
            {var subQ0=sQuery(id+"F25.wireOp",EDGE,"E383.MirrorCS");var subQ1=sQuery(id+"F25.wireOp",EDGE,"E344.MirrorCS");var subQ2=makeQuery(id+"F25.imprint","INTERSECT",VERTEX,{"derivedFrom":[subQ1,subQ0]});Q573=makeQuery(id+"F25.imprint","IMPRINT",FACE,{"disambiguationData":[TD([[makeQuery(id+"F25.imprint","IMPRINT",EDGE,{"disambiguationData":[TD([[subQ2,-1.0]])],"derivedFrom":subQ1}),1.0]])]});}
            var Q574;
            {var subQ0=sQuery(id+"F25.wireOp",EDGE,"E350.MirrorCS");var subQ1=sQuery(id+"F25.wireOp",EDGE,"E344.MirrorCS");var subQ2=makeQuery(id+"F25.imprint","INTERSECT",VERTEX,{"derivedFrom":[subQ1,subQ0]});Q574=makeQuery(id+"F25.imprint","IMPRINT",FACE,{"disambiguationData":[TD([[makeQuery(id+"F25.imprint","IMPRINT",EDGE,{"disambiguationData":[TD([[subQ2,-1.0]])],"derivedFrom":subQ1}),-1.0]])]});}
            var Q575;
            {var subQ0=sQuery(id+"F25.wireOp",EDGE,"E383.MirrorCS");var subQ1=sQuery(id+"F25.wireOp",EDGE,"E344.MirrorCS");var subQ2=makeQuery(id+"F25.imprint","INTERSECT",VERTEX,{"derivedFrom":[subQ1,subQ0]});Q575=makeQuery(id+"F25.imprint","IMPRINT",FACE,{"disambiguationData":[TD([[makeQuery(id+"F25.imprint","IMPRINT",EDGE,{"disambiguationData":[TD([[subQ2,-1.0]])],"derivedFrom":subQ1}),-1.0]])]});}
            var Q576;
            {var subQ0=sQuery(id+"F25.wireOp",EDGE,"E373.MirrorCS");var subQ1=sQuery(id+"F25.wireOp",EDGE,"E350.MirrorCS");var subQ2=makeQuery(id+"F25.imprint","INTERSECT",VERTEX,{"derivedFrom":[subQ1,subQ0]});Q576=makeQuery(id+"F25.imprint","IMPRINT",FACE,{"disambiguationData":[TD([[makeQuery(id+"F25.imprint","IMPRINT",EDGE,{"disambiguationData":[TD([[subQ2,-1.0]])],"derivedFrom":subQ1}),1.0]])]});}
            var Q577;
            {var subQ0=sQuery(id+"F25.wireOp",EDGE,"E373.MirrorCS");var subQ1=sQuery(id+"F25.wireOp",EDGE,"E350.MirrorCS");var subQ2=makeQuery(id+"F25.imprint","INTERSECT",VERTEX,{"derivedFrom":[subQ1,subQ0]});Q577=makeQuery(id+"F25.imprint","IMPRINT",FACE,{"disambiguationData":[TD([[makeQuery(id+"F25.imprint","IMPRINT",EDGE,{"disambiguationData":[TD([[subQ2,-1.0]])],"derivedFrom":subQ1}),-1.0]])]});}
            var Q578;
            {var subQ0=sQuery(id+"F25.wireOp",EDGE,"E360.MirrorCS");var subQ1=sQuery(id+"F25.wireOp",EDGE,"E335.MirrorCS");var subQ2=makeQuery(id+"F25.imprint","INTERSECT",VERTEX,{"derivedFrom":[subQ1,subQ0]});Q578=makeQuery(id+"F25.imprint","IMPRINT",FACE,{"disambiguationData":[TD([[makeQuery(id+"F25.imprint","IMPRINT",EDGE,{"disambiguationData":[TD([[subQ2,-1.0]])],"derivedFrom":subQ1}),1.0]])]});}
            var Q579;
            {var subQ0=sQuery(id+"F25.wireOp",EDGE,"E394.MirrorCS");var subQ1=sQuery(id+"F25.wireOp",EDGE,"E335.MirrorCS");var subQ2=makeQuery(id+"F25.imprint","INTERSECT",VERTEX,{"derivedFrom":[subQ1,subQ0]});Q579=makeQuery(id+"F25.imprint","IMPRINT",FACE,{"disambiguationData":[TD([[makeQuery(id+"F25.imprint","IMPRINT",EDGE,{"disambiguationData":[TD([[subQ2,-1.0]])],"derivedFrom":subQ1}),1.0]])]});}
            var Q580;
            {var subQ0=sQuery(id+"F25.wireOp",EDGE,"E350.MirrorCS");var subQ1=sQuery(id+"F25.wireOp",EDGE,"E348.MirrorCS");var subQ2=makeQuery(id+"F25.imprint","INTERSECT",VERTEX,{"derivedFrom":[subQ1,subQ0]});Q580=makeQuery(id+"F25.imprint","IMPRINT",FACE,{"disambiguationData":[TD([[makeQuery(id+"F25.imprint","IMPRINT",EDGE,{"disambiguationData":[TD([[subQ2,-1.0]])],"derivedFrom":subQ1}),-1.0]])]});}
            var Q581;
            {var subQ0=sQuery(id+"F25.wireOp",EDGE,"E383.MirrorCS");var subQ1=sQuery(id+"F25.wireOp",EDGE,"E348.MirrorCS");var subQ2=makeQuery(id+"F25.imprint","INTERSECT",VERTEX,{"derivedFrom":[subQ1,subQ0]});Q581=makeQuery(id+"F25.imprint","IMPRINT",FACE,{"disambiguationData":[TD([[makeQuery(id+"F25.imprint","IMPRINT",EDGE,{"disambiguationData":[TD([[subQ2,-1.0]])],"derivedFrom":subQ1}),-1.0]])]});}
            var Q582;
            {var subQ0=sQuery(id+"F25.wireOp",EDGE,"E383.MirrorCS");var subQ1=sQuery(id+"F25.wireOp",EDGE,"E348.MirrorCS");var subQ2=makeQuery(id+"F25.imprint","INTERSECT",VERTEX,{"derivedFrom":[subQ1,subQ0]});Q582=makeQuery(id+"F25.imprint","IMPRINT",FACE,{"disambiguationData":[TD([[makeQuery(id+"F25.imprint","IMPRINT",EDGE,{"disambiguationData":[TD([[subQ2,-1.0]])],"derivedFrom":subQ1}),1.0]])]});}
            var Q583;
            {var subQ0=sQuery(id+"F25.wireOp",EDGE,"E350.MirrorCS");var subQ1=sQuery(id+"F25.wireOp",EDGE,"E348.MirrorCS");var subQ2=makeQuery(id+"F25.imprint","INTERSECT",VERTEX,{"derivedFrom":[subQ1,subQ0]});Q583=makeQuery(id+"F25.imprint","IMPRINT",FACE,{"disambiguationData":[TD([[makeQuery(id+"F25.imprint","IMPRINT",EDGE,{"disambiguationData":[TD([[subQ2,-1.0]])],"derivedFrom":subQ1}),1.0]])]});}
            var Q584;
            {var subQ0=sQuery(id+"F25.wireOp",EDGE,"E310.MirrorCS");Q584=makeQuery(id+"F25.imprint","IMPRINT",FACE,{"disambiguationData":[TD([[makeQuery(id+"F25.imprint","IMPRINT",EDGE,{"derivedFrom":subQ0}),-1.0]])]});}
            var Q585;
            {var subQ0=sQuery(id+"F25.wireOp",EDGE,"E384.MirrorCS");var subQ1=sQuery(id+"F25.wireOp",EDGE,"E351.MirrorCS");var subQ2=makeQuery(id+"F25.imprint","INTERSECT",VERTEX,{"derivedFrom":[subQ1,subQ0]});Q585=makeQuery(id+"F25.imprint","IMPRINT",FACE,{"disambiguationData":[TD([[makeQuery(id+"F25.imprint","IMPRINT",EDGE,{"disambiguationData":[TD([[subQ2,-1.0]])],"derivedFrom":subQ1}),1.0]])]});}
            var Q586;
            {var subQ0=sQuery(id+"F25.wireOp",EDGE,"E384.MirrorCS");var subQ1=sQuery(id+"F25.wireOp",EDGE,"E326.MirrorCS");var subQ2=makeQuery(id+"F25.imprint","INTERSECT",VERTEX,{"derivedFrom":[subQ1,subQ0]});Q586=makeQuery(id+"F25.imprint","IMPRINT",FACE,{"disambiguationData":[TD([[makeQuery(id+"F25.imprint","IMPRINT",EDGE,{"disambiguationData":[TD([[subQ2,-1.0]])],"derivedFrom":subQ1}),-1.0]])]});}
            var Q587;
            {var subQ0=sQuery(id+"F25.wireOp",EDGE,"E344.MirrorCS");var subQ1=sQuery(id+"F25.wireOp",EDGE,"E326.MirrorCS");var subQ2=makeQuery(id+"F25.imprint","INTERSECT",VERTEX,{"derivedFrom":[subQ1,subQ0]});Q587=makeQuery(id+"F25.imprint","IMPRINT",FACE,{"disambiguationData":[TD([[makeQuery(id+"F25.imprint","IMPRINT",EDGE,{"disambiguationData":[TD([[subQ2,-1.0]])],"derivedFrom":subQ1}),-1.0]])]});}
            var Q588;
            {var subQ0=sQuery(id+"F25.wireOp",EDGE,"E373.MirrorCS");var subQ1=sQuery(id+"F25.wireOp",EDGE,"E326.MirrorCS");var subQ2=makeQuery(id+"F25.imprint","INTERSECT",VERTEX,{"derivedFrom":[subQ1,subQ0]});Q588=makeQuery(id+"F25.imprint","IMPRINT",FACE,{"disambiguationData":[TD([[makeQuery(id+"F25.imprint","IMPRINT",EDGE,{"disambiguationData":[TD([[subQ2,-1.0]])],"derivedFrom":subQ1}),-1.0]])]});}
            var Q589;
            {var subQ0=sQuery(id+"F25.wireOp",EDGE,"E378.MirrorCS");var subQ1=sQuery(id+"F25.wireOp",EDGE,"E326.MirrorCS");var subQ2=makeQuery(id+"F25.imprint","INTERSECT",VERTEX,{"derivedFrom":[subQ1,subQ0]});Q589=makeQuery(id+"F25.imprint","IMPRINT",FACE,{"disambiguationData":[TD([[makeQuery(id+"F25.imprint","IMPRINT",EDGE,{"disambiguationData":[TD([[subQ2,-1.0]])],"derivedFrom":subQ1}),-1.0]])]});}
            var Q590;
            {var subQ0=sQuery(id+"F25.wireOp",EDGE,"E348.MirrorCS");var subQ1=sQuery(id+"F25.wireOp",EDGE,"E326.MirrorCS");var subQ2=makeQuery(id+"F25.imprint","INTERSECT",VERTEX,{"derivedFrom":[subQ1,subQ0]});Q590=makeQuery(id+"F25.imprint","IMPRINT",FACE,{"disambiguationData":[TD([[makeQuery(id+"F25.imprint","IMPRINT",EDGE,{"disambiguationData":[TD([[subQ2,-1.0]])],"derivedFrom":subQ1}),-1.0]])]});}
            var Q591;
            {var subQ0=sQuery(id+"F25.wireOp",EDGE,"E369.MirrorCS");var subQ1=sQuery(id+"F25.wireOp",EDGE,"E326.MirrorCS");var subQ2=makeQuery(id+"F25.imprint","INTERSECT",VERTEX,{"derivedFrom":[subQ1,subQ0]});Q591=makeQuery(id+"F25.imprint","IMPRINT",FACE,{"disambiguationData":[TD([[makeQuery(id+"F25.imprint","IMPRINT",EDGE,{"disambiguationData":[TD([[subQ2,-1.0]])],"derivedFrom":subQ1}),-1.0]])]});}
            var Q592;
            {var subQ0=sQuery(id+"F25.wireOp",EDGE,"E335.MirrorCS");var subQ1=sQuery(id+"F25.wireOp",EDGE,"E326.MirrorCS");var subQ2=makeQuery(id+"F25.imprint","INTERSECT",VERTEX,{"derivedFrom":[subQ1,subQ0]});Q592=makeQuery(id+"F25.imprint","IMPRINT",FACE,{"disambiguationData":[TD([[makeQuery(id+"F25.imprint","IMPRINT",EDGE,{"disambiguationData":[TD([[subQ2,-1.0]])],"derivedFrom":subQ1}),-1.0]])]});}
            var Q593;
            {var subQ0=sQuery(id+"F25.wireOp",EDGE,"E394.MirrorCS");var subQ1=sQuery(id+"F25.wireOp",EDGE,"E348.MirrorCS");var subQ2=makeQuery(id+"F25.imprint","INTERSECT",VERTEX,{"derivedFrom":[subQ1,subQ0]});Q593=makeQuery(id+"F25.imprint","IMPRINT",FACE,{"disambiguationData":[TD([[makeQuery(id+"F25.imprint","IMPRINT",EDGE,{"disambiguationData":[TD([[subQ2,-1.0]])],"derivedFrom":subQ1}),-1.0]])]});}
            var Q594;
            {var subQ0=sQuery(id+"F25.wireOp",EDGE,"E348.MirrorCS");var subQ1=sQuery(id+"F25.wireOp",EDGE,"E336.MirrorCS");var subQ2=makeQuery(id+"F25.imprint","INTERSECT",VERTEX,{"derivedFrom":[subQ1,subQ0]});Q594=makeQuery(id+"F25.imprint","IMPRINT",FACE,{"disambiguationData":[TD([[makeQuery(id+"F25.imprint","IMPRINT",EDGE,{"disambiguationData":[TD([[subQ2,-1.0]])],"derivedFrom":subQ1}),-1.0]])]});}
            var Q595;
            {var subQ0=sQuery(id+"F25.wireOp",EDGE,"E378.MirrorCS");var subQ1=sQuery(id+"F25.wireOp",EDGE,"E336.MirrorCS");var subQ2=makeQuery(id+"F25.imprint","INTERSECT",VERTEX,{"derivedFrom":[subQ1,subQ0]});Q595=makeQuery(id+"F25.imprint","IMPRINT",FACE,{"disambiguationData":[TD([[makeQuery(id+"F25.imprint","IMPRINT",EDGE,{"disambiguationData":[TD([[subQ2,-1.0]])],"derivedFrom":subQ1}),-1.0]])]});}
            var Q596;
            {var subQ0=sQuery(id+"F25.wireOp",EDGE,"E394.MirrorCS");var subQ1=sQuery(id+"F25.wireOp",EDGE,"E348.MirrorCS");var subQ2=makeQuery(id+"F25.imprint","INTERSECT",VERTEX,{"derivedFrom":[subQ1,subQ0]});Q596=makeQuery(id+"F25.imprint","IMPRINT",FACE,{"disambiguationData":[TD([[makeQuery(id+"F25.imprint","IMPRINT",EDGE,{"disambiguationData":[TD([[subQ2,-1.0]])],"derivedFrom":subQ1}),1.0]])]});}
            var Q597;
            {var subQ0=sQuery(id+"F25.wireOp",EDGE,"E394.MirrorCS");var subQ1=sQuery(id+"F25.wireOp",EDGE,"E373.MirrorCS");var subQ2=makeQuery(id+"F25.imprint","INTERSECT",VERTEX,{"derivedFrom":[subQ1,subQ0]});Q597=makeQuery(id+"F25.imprint","IMPRINT",FACE,{"disambiguationData":[TD([[makeQuery(id+"F25.imprint","IMPRINT",EDGE,{"disambiguationData":[TD([[subQ2,-1.0]])],"derivedFrom":subQ1}),-1.0]])]});}
            var Q598;
            {var subQ0=sQuery(id+"F25.wireOp",EDGE,"E373.MirrorCS");var subQ1=sQuery(id+"F25.wireOp",EDGE,"E336.MirrorCS");var subQ2=makeQuery(id+"F25.imprint","INTERSECT",VERTEX,{"derivedFrom":[subQ1,subQ0]});Q598=makeQuery(id+"F25.imprint","IMPRINT",FACE,{"disambiguationData":[TD([[makeQuery(id+"F25.imprint","IMPRINT",EDGE,{"disambiguationData":[TD([[subQ2,-1.0]])],"derivedFrom":subQ1}),-1.0]])]});}
            var Q599;
            {var subQ0=sQuery(id+"F25.wireOp",EDGE,"E344.MirrorCS");var subQ1=sQuery(id+"F25.wireOp",EDGE,"E336.MirrorCS");var subQ2=makeQuery(id+"F25.imprint","INTERSECT",VERTEX,{"derivedFrom":[subQ1,subQ0]});Q599=makeQuery(id+"F25.imprint","IMPRINT",FACE,{"disambiguationData":[TD([[makeQuery(id+"F25.imprint","IMPRINT",EDGE,{"disambiguationData":[TD([[subQ2,-1.0]])],"derivedFrom":subQ1}),-1.0]])]});}
            var Q600;
            {var subQ0=sQuery(id+"F25.wireOp",EDGE,"E394.MirrorCS");var subQ1=sQuery(id+"F25.wireOp",EDGE,"E344.MirrorCS");var subQ2=makeQuery(id+"F25.imprint","INTERSECT",VERTEX,{"derivedFrom":[subQ1,subQ0]});Q600=makeQuery(id+"F25.imprint","IMPRINT",FACE,{"disambiguationData":[TD([[makeQuery(id+"F25.imprint","IMPRINT",EDGE,{"disambiguationData":[TD([[subQ2,-1.0]])],"derivedFrom":subQ1}),-1.0]])]});}
            var Q601;
            {var subQ0=sQuery(id+"F25.wireOp",EDGE,"E394.MirrorCS");var subQ1=sQuery(id+"F25.wireOp",EDGE,"E344.MirrorCS");var subQ2=makeQuery(id+"F25.imprint","INTERSECT",VERTEX,{"derivedFrom":[subQ1,subQ0]});Q601=makeQuery(id+"F25.imprint","IMPRINT",FACE,{"disambiguationData":[TD([[makeQuery(id+"F25.imprint","IMPRINT",EDGE,{"disambiguationData":[TD([[subQ2,-1.0]])],"derivedFrom":subQ1}),1.0]])]});}
            var Q602;
            {var subQ0=sQuery(id+"F25.wireOp",EDGE,"E384.MirrorCS");var subQ1=sQuery(id+"F25.wireOp",EDGE,"E336.MirrorCS");var subQ2=makeQuery(id+"F25.imprint","INTERSECT",VERTEX,{"derivedFrom":[subQ1,subQ0]});Q602=makeQuery(id+"F25.imprint","IMPRINT",FACE,{"disambiguationData":[TD([[makeQuery(id+"F25.imprint","IMPRINT",EDGE,{"disambiguationData":[TD([[subQ2,-1.0]])],"derivedFrom":subQ1}),-1.0]])]});}
            var Q603;
            {var subQ0=sQuery(id+"F25.wireOp",EDGE,"E538.trimOffspring");var subQ1=sQuery(id+"F25.wireOp",EDGE,"E264.trimOffspring");var subQ2=makeQuery(id+"F25.imprint","INTERSECT",VERTEX,{"derivedFrom":[subQ1,subQ0]});Q603=makeQuery(id+"F25.imprint","IMPRINT",FACE,{"disambiguationData":[TD([[makeQuery(id+"F25.imprint","IMPRINT",EDGE,{"disambiguationData":[TD([[subQ2,-1.0]])],"derivedFrom":subQ1}),1.0]])]});}
            var Q604;
            {var subQ0=sQuery(id+"F25.wireOp",EDGE,"E585.trimOffspring");var subQ1=sQuery(id+"F25.wireOp",EDGE,"E414.MirrorCS");var subQ2=makeQuery(id+"F25.imprint","INTERSECT",VERTEX,{"derivedFrom":[subQ1,subQ0]});Q604=makeQuery(id+"F25.imprint","IMPRINT",FACE,{"disambiguationData":[TD([[makeQuery(id+"F25.imprint","IMPRINT",EDGE,{"disambiguationData":[TD([[subQ2,-1.0]])],"derivedFrom":subQ1}),1.0]])]});}
            extrude(context, id + "F33", {"entities" : qUnion([Q0, Q1, Q2, Q3, Q4, Q5, Q6, Q7, Q8, Q9, Q10, Q11, Q12, Q13, Q14, Q15, Q16, Q17, Q18, Q19, Q20, Q21, Q22, Q23, Q24, Q25, Q26, Q27, Q28, Q29, Q30, Q31, Q32, Q33, Q34, Q35, Q36, Q37, Q38, Q39, Q40, Q41, Q42, Q43, Q44, Q45, Q46, Q47, Q48, Q49, Q50, Q51, Q52, Q53, Q54, Q55, Q56, Q57, Q58, Q59, Q60, Q61, Q62, Q63, Q64, Q65, Q66, Q67, Q68, Q69, Q70, Q71, Q72, Q73, Q74, Q75, Q76, Q77, Q78, Q79, Q80, Q81, Q82, Q83, Q84, Q85, Q86, Q87, Q88, Q89, Q90, Q91, Q92, Q93, Q94, Q95, Q96, Q97, Q98, Q99, Q100, Q101, Q102, Q103, Q104, Q105, Q106, Q107, Q108, Q109, Q110, Q111, Q112, Q113, Q114, Q115, Q116, Q117, Q118, Q119, Q120, Q121, Q122, Q123, Q124, Q125, Q126, Q127, Q128, Q129, Q130, Q131, Q132, Q133, Q134, Q135, Q136, Q137, Q138, Q139, Q140, Q141, Q142, Q143, Q144, Q145, Q146, Q147, Q148, Q149, Q150, Q151, Q152, Q153, Q154, Q155, Q156, Q157, Q158, Q159, Q160, Q161, Q162, Q163, Q164, Q165, Q166, Q167, Q168, Q169, Q170, Q171, Q172, Q173, Q174, Q175, Q176, Q177, Q178, Q179, Q180, Q181, Q182, Q183, Q184, Q185, Q186, Q187, Q188, Q189, Q190, Q191, Q192, Q193, Q194, Q195, Q196, Q197, Q198, Q199, Q200, Q201, Q202, Q203, Q204, Q205, Q206, Q207, Q208, Q209, Q210, Q211, Q212, Q213, Q214, Q215, Q216, Q217, Q218, Q219, Q220, Q221, Q222, Q223, Q224, Q225, Q226, Q227, Q228, Q229, Q230, Q231, Q232, Q233, Q234, Q235, Q236, Q237, Q238, Q239, Q240, Q241, Q242, Q243, Q244, Q245, Q246, Q247, Q248, Q249, Q250, Q251, Q252, Q253, Q254, Q255, Q256, Q257, Q258, Q259, Q260, Q261, Q262, Q263, Q264, Q265, Q266, Q267, Q268, Q269, Q270, Q271, Q272, Q273, Q274, Q275, Q276, Q277, Q278, Q279, Q280, Q281, Q282, Q283, Q284, Q285, Q286, Q287, Q288, Q289, Q290, Q291, Q292, Q293, Q294, Q295, Q296, Q297, Q298, Q299, Q300, Q301, Q302, Q303, Q304, Q305, Q306, Q307, Q308, Q309, Q310, Q311, Q312, Q313, Q314, Q315, Q316, Q317, Q318, Q319, Q320, Q321, Q322, Q323, Q324, Q325, Q326, Q327, Q328, Q329, Q330, Q331, Q332, Q333, Q334, Q335, Q336, Q337, Q338, Q339, Q340, Q341, Q342, Q343, Q344, Q345, Q346, Q347, Q348, Q349, Q350, Q351, Q352, Q353, Q354, Q355, Q356, Q357, Q358, Q359, Q360, Q361, Q362, Q363, Q364, Q365, Q366, Q367, Q368, Q369, Q370, Q371, Q372, Q373, Q374, Q375, Q376, Q377, Q378, Q379, Q380, Q381, Q382, Q383, Q384, Q385, Q386, Q387, Q388, Q389, Q390, Q391, Q392, Q393, Q394, Q395, Q396, Q397, Q398, Q399, Q400, Q401, Q402, Q403, Q404, Q405, Q406, Q407, Q408, Q409, Q410, Q411, Q412, Q413, Q414, Q415, Q416, Q417, Q418, Q419, Q420, Q421, Q422, Q423, Q424, Q425, Q426, Q427, Q428, Q429, Q430, Q431, Q432, Q433, Q434, Q435, Q436, Q437, Q438, Q439, Q440, Q441, Q442, Q443, Q444, Q445, Q446, Q447, Q448, Q449, Q450, Q451, Q452, Q453, Q454, Q455, Q456, Q457, Q458, Q459, Q460, Q461, Q462, Q463, Q464, Q465, Q466, Q467, Q468, Q469, Q470, Q471, Q472, Q473, Q474, Q475, Q476, Q477, Q478, Q479, Q480, Q481, Q482, Q483, Q484, Q485, Q486, Q487, Q488, Q489, Q490, Q491, Q492, Q493, Q494, Q495, Q496, Q497, Q498, Q499, Q500, Q501, Q502, Q503, Q504, Q505, Q506, Q507, Q508, Q509, Q510, Q511, Q512, Q513, Q514, Q515, Q516, Q517, Q518, Q519, Q520, Q521, Q522, Q523, Q524, Q525, Q526, Q527, Q528, Q529, Q530, Q531, Q532, Q533, Q534, Q535, Q536, Q537, Q538, Q539, Q540, Q541, Q542, Q543, Q544, Q545, Q546, Q547, Q548, Q549, Q550, Q551, Q552, Q553, Q554, Q555, Q556, Q557, Q558, Q559, Q560, Q561, Q562, Q563, Q564, Q565, Q566, Q567, Q568, Q569, Q570, Q571, Q572, Q573, Q574, Q575, Q576, Q577, Q578, Q579, Q580, Q581, Q582, Q583, Q584, Q585, Q586, Q587, Q588, Q589, Q590, Q591, Q592, Q593, Q594, Q595, Q596, Q597, Q598, Q599, Q600, Q601, Q602, Q603, Q604]), "operationType" : NewBodyOperationType.REMOVE, "depth" : 25 * mm, "offsetDistance" : 25 * mm});
        }
        {
            var Q0;
            Q0=makeQuery(id+"F33.boolean.opBoolean","SPLIT",BODY,{"disambiguationData":[OD(5.0)],"derivedFrom":makeQuery(id+"F5.opExtrude","SWEPT_BODY",BODY,{"disambiguationData":[OSD([sQuery(id+"F2.wireOp",EDGE,"E74.top"),sQuery(id+"F2.wireOp",EDGE,"E75"),sQuery(id+"F2.wireOp",EDGE,"E76"),sQuery(id+"F2.wireOp",EDGE,"E77"),sQuery(id+"F2.wireOp",EDGE,"E89"),sQuery(id+"F2.wireOp",EDGE,"E90.trimOffspring"),sQuery(id+"F2.wireOp",EDGE,"E91"),sQuery(id+"F2.wireOp",EDGE,"E97.MirrorCS"),sQuery(id+"F2.wireOp",EDGE,"E98.MirrorCS"),sQuery(id+"F2.wireOp",EDGE,"E99.MirrorCS"),sQuery(id+"F2.wireOp",EDGE,"E100.MirrorCS"),sQuery(id+"F2.wireOp",EDGE,"E102.MirrorCS"),sQuery(id+"F2.wireOp",EDGE,"E103.MirrorCS"),sQuery(id+"F2.wireOp",EDGE,"E107.MirrorCS"),sQuery(id+"F2.wireOp",EDGE,"E108.MirrorCS"),sQuery(id+"F2.wireOp",EDGE,"E109.MirrorCS"),sQuery(id+"F2.wireOp",EDGE,"E110.MirrorCS"),sQuery(id+"F2.wireOp",EDGE,"E111.MirrorCS"),sQuery(id+"F2.wireOp",EDGE,"E115.MirrorCS"),sQuery(id+"F2.wireOp",EDGE,"E117.MirrorCS"),sQuery(id+"F2.wireOp",EDGE,"E121.MirrorCS"),sQuery(id+"F2.wireOp",EDGE,"E122.MirrorCS"),sQuery(id+"F2.wireOp",EDGE,"E123.MirrorCS"),sQuery(id+"F2.wireOp",EDGE,"E124.MirrorCS"),sQuery(id+"F2.wireOp",EDGE,"E126.MirrorCS"),sQuery(id+"F2.wireOp",EDGE,"E127.MirrorCS"),sQuery(id+"F2.wireOp",EDGE,"E128.MirrorCS"),sQuery(id+"F2.wireOp",EDGE,"E129.MirrorCS")])]})});
            var Q1;
            Q1=makeQuery(id+"F33.boolean.opBoolean","SPLIT",BODY,{"disambiguationData":[OD(0.0)],"derivedFrom":makeQuery(id+"F5.opExtrude","SWEPT_BODY",BODY,{"disambiguationData":[OSD([sQuery(id+"F2.wireOp",EDGE,"E74.top"),sQuery(id+"F2.wireOp",EDGE,"E75"),sQuery(id+"F2.wireOp",EDGE,"E76"),sQuery(id+"F2.wireOp",EDGE,"E77"),sQuery(id+"F2.wireOp",EDGE,"E89"),sQuery(id+"F2.wireOp",EDGE,"E90.trimOffspring"),sQuery(id+"F2.wireOp",EDGE,"E91"),sQuery(id+"F2.wireOp",EDGE,"E97.MirrorCS"),sQuery(id+"F2.wireOp",EDGE,"E98.MirrorCS"),sQuery(id+"F2.wireOp",EDGE,"E99.MirrorCS"),sQuery(id+"F2.wireOp",EDGE,"E100.MirrorCS"),sQuery(id+"F2.wireOp",EDGE,"E102.MirrorCS"),sQuery(id+"F2.wireOp",EDGE,"E103.MirrorCS"),sQuery(id+"F2.wireOp",EDGE,"E107.MirrorCS"),sQuery(id+"F2.wireOp",EDGE,"E108.MirrorCS"),sQuery(id+"F2.wireOp",EDGE,"E109.MirrorCS"),sQuery(id+"F2.wireOp",EDGE,"E110.MirrorCS"),sQuery(id+"F2.wireOp",EDGE,"E111.MirrorCS"),sQuery(id+"F2.wireOp",EDGE,"E115.MirrorCS"),sQuery(id+"F2.wireOp",EDGE,"E117.MirrorCS"),sQuery(id+"F2.wireOp",EDGE,"E121.MirrorCS"),sQuery(id+"F2.wireOp",EDGE,"E122.MirrorCS"),sQuery(id+"F2.wireOp",EDGE,"E123.MirrorCS"),sQuery(id+"F2.wireOp",EDGE,"E124.MirrorCS"),sQuery(id+"F2.wireOp",EDGE,"E126.MirrorCS"),sQuery(id+"F2.wireOp",EDGE,"E127.MirrorCS"),sQuery(id+"F2.wireOp",EDGE,"E128.MirrorCS"),sQuery(id+"F2.wireOp",EDGE,"E129.MirrorCS")])]})});
            var Q2;
            Q2=makeQuery(id+"F33.boolean.opBoolean","SPLIT",BODY,{"disambiguationData":[OD(1.0)],"derivedFrom":makeQuery(id+"F5.opExtrude","SWEPT_BODY",BODY,{"disambiguationData":[OSD([sQuery(id+"F2.wireOp",EDGE,"E74.top"),sQuery(id+"F2.wireOp",EDGE,"E75"),sQuery(id+"F2.wireOp",EDGE,"E76"),sQuery(id+"F2.wireOp",EDGE,"E77"),sQuery(id+"F2.wireOp",EDGE,"E89"),sQuery(id+"F2.wireOp",EDGE,"E90.trimOffspring"),sQuery(id+"F2.wireOp",EDGE,"E91"),sQuery(id+"F2.wireOp",EDGE,"E97.MirrorCS"),sQuery(id+"F2.wireOp",EDGE,"E98.MirrorCS"),sQuery(id+"F2.wireOp",EDGE,"E99.MirrorCS"),sQuery(id+"F2.wireOp",EDGE,"E100.MirrorCS"),sQuery(id+"F2.wireOp",EDGE,"E102.MirrorCS"),sQuery(id+"F2.wireOp",EDGE,"E103.MirrorCS"),sQuery(id+"F2.wireOp",EDGE,"E107.MirrorCS"),sQuery(id+"F2.wireOp",EDGE,"E108.MirrorCS"),sQuery(id+"F2.wireOp",EDGE,"E109.MirrorCS"),sQuery(id+"F2.wireOp",EDGE,"E110.MirrorCS"),sQuery(id+"F2.wireOp",EDGE,"E111.MirrorCS"),sQuery(id+"F2.wireOp",EDGE,"E115.MirrorCS"),sQuery(id+"F2.wireOp",EDGE,"E117.MirrorCS"),sQuery(id+"F2.wireOp",EDGE,"E121.MirrorCS"),sQuery(id+"F2.wireOp",EDGE,"E122.MirrorCS"),sQuery(id+"F2.wireOp",EDGE,"E123.MirrorCS"),sQuery(id+"F2.wireOp",EDGE,"E124.MirrorCS"),sQuery(id+"F2.wireOp",EDGE,"E126.MirrorCS"),sQuery(id+"F2.wireOp",EDGE,"E127.MirrorCS"),sQuery(id+"F2.wireOp",EDGE,"E128.MirrorCS"),sQuery(id+"F2.wireOp",EDGE,"E129.MirrorCS")])]})});
            var Q3;
            Q3=makeQuery(id+"F33.boolean.opBoolean","SPLIT",BODY,{"disambiguationData":[OD(2.0)],"derivedFrom":makeQuery(id+"F5.opExtrude","SWEPT_BODY",BODY,{"disambiguationData":[OSD([sQuery(id+"F2.wireOp",EDGE,"E74.top"),sQuery(id+"F2.wireOp",EDGE,"E75"),sQuery(id+"F2.wireOp",EDGE,"E76"),sQuery(id+"F2.wireOp",EDGE,"E77"),sQuery(id+"F2.wireOp",EDGE,"E89"),sQuery(id+"F2.wireOp",EDGE,"E90.trimOffspring"),sQuery(id+"F2.wireOp",EDGE,"E91"),sQuery(id+"F2.wireOp",EDGE,"E97.MirrorCS"),sQuery(id+"F2.wireOp",EDGE,"E98.MirrorCS"),sQuery(id+"F2.wireOp",EDGE,"E99.MirrorCS"),sQuery(id+"F2.wireOp",EDGE,"E100.MirrorCS"),sQuery(id+"F2.wireOp",EDGE,"E102.MirrorCS"),sQuery(id+"F2.wireOp",EDGE,"E103.MirrorCS"),sQuery(id+"F2.wireOp",EDGE,"E107.MirrorCS"),sQuery(id+"F2.wireOp",EDGE,"E108.MirrorCS"),sQuery(id+"F2.wireOp",EDGE,"E109.MirrorCS"),sQuery(id+"F2.wireOp",EDGE,"E110.MirrorCS"),sQuery(id+"F2.wireOp",EDGE,"E111.MirrorCS"),sQuery(id+"F2.wireOp",EDGE,"E115.MirrorCS"),sQuery(id+"F2.wireOp",EDGE,"E117.MirrorCS"),sQuery(id+"F2.wireOp",EDGE,"E121.MirrorCS"),sQuery(id+"F2.wireOp",EDGE,"E122.MirrorCS"),sQuery(id+"F2.wireOp",EDGE,"E123.MirrorCS"),sQuery(id+"F2.wireOp",EDGE,"E124.MirrorCS"),sQuery(id+"F2.wireOp",EDGE,"E126.MirrorCS"),sQuery(id+"F2.wireOp",EDGE,"E127.MirrorCS"),sQuery(id+"F2.wireOp",EDGE,"E128.MirrorCS"),sQuery(id+"F2.wireOp",EDGE,"E129.MirrorCS")])]})});
            var Q4;
            Q4=makeQuery(id+"F33.boolean.opBoolean","SPLIT",BODY,{"disambiguationData":[OD(3.0)],"derivedFrom":makeQuery(id+"F5.opExtrude","SWEPT_BODY",BODY,{"disambiguationData":[OSD([sQuery(id+"F2.wireOp",EDGE,"E74.top"),sQuery(id+"F2.wireOp",EDGE,"E75"),sQuery(id+"F2.wireOp",EDGE,"E76"),sQuery(id+"F2.wireOp",EDGE,"E77"),sQuery(id+"F2.wireOp",EDGE,"E89"),sQuery(id+"F2.wireOp",EDGE,"E90.trimOffspring"),sQuery(id+"F2.wireOp",EDGE,"E91"),sQuery(id+"F2.wireOp",EDGE,"E97.MirrorCS"),sQuery(id+"F2.wireOp",EDGE,"E98.MirrorCS"),sQuery(id+"F2.wireOp",EDGE,"E99.MirrorCS"),sQuery(id+"F2.wireOp",EDGE,"E100.MirrorCS"),sQuery(id+"F2.wireOp",EDGE,"E102.MirrorCS"),sQuery(id+"F2.wireOp",EDGE,"E103.MirrorCS"),sQuery(id+"F2.wireOp",EDGE,"E107.MirrorCS"),sQuery(id+"F2.wireOp",EDGE,"E108.MirrorCS"),sQuery(id+"F2.wireOp",EDGE,"E109.MirrorCS"),sQuery(id+"F2.wireOp",EDGE,"E110.MirrorCS"),sQuery(id+"F2.wireOp",EDGE,"E111.MirrorCS"),sQuery(id+"F2.wireOp",EDGE,"E115.MirrorCS"),sQuery(id+"F2.wireOp",EDGE,"E117.MirrorCS"),sQuery(id+"F2.wireOp",EDGE,"E121.MirrorCS"),sQuery(id+"F2.wireOp",EDGE,"E122.MirrorCS"),sQuery(id+"F2.wireOp",EDGE,"E123.MirrorCS"),sQuery(id+"F2.wireOp",EDGE,"E124.MirrorCS"),sQuery(id+"F2.wireOp",EDGE,"E126.MirrorCS"),sQuery(id+"F2.wireOp",EDGE,"E127.MirrorCS"),sQuery(id+"F2.wireOp",EDGE,"E128.MirrorCS"),sQuery(id+"F2.wireOp",EDGE,"E129.MirrorCS")])]})});
            deleteBodies(context, id + "F34", {"entities" : qUnion([Q0, Q1, Q2, Q3, Q4])});
        }
        {
            var Q0;
            Q0=qCreatedBy(id+"F1.planeOp",FACE);
            var Q1;
            {var subQ23=sQuery(id+"F4.wireOp",EDGE,"E186.MirrorCS");var subQ25=sQuery(id+"F4.wireOp",EDGE,"E181.MirrorCS");var subQ32=sQuery(id+"F2.wireOp",EDGE,"E110.MirrorCS");var subQ33=sQuery(id+"F2.wireOp",EDGE,"E103.MirrorCS");var subQ48=sQuery(id+"F3.wireOp",EDGE,"E143.MirrorCS");var subQ49=sQuery(id+"F3.wireOp",EDGE,"E140");var subQ72=sQuery(id+"F4.wireOp",EDGE,"E170");Q1=makeQuery(id+"F33.boolean.opBoolean","SPLIT",FACE,{"disambiguationData":[TD([makeQuery(id+"F8.opExtrude","SWEPT_FACE",FACE,{"disambiguationData":[OSD([subQ23])]})])],"derivedFrom":makeQuery(id+"F13.boolean.opBoolean","MERGE",FACE,{"derivedFrom":[makeQuery(id+"F12.boolean.opBoolean","MERGE",FACE,{"derivedFrom":[makeQuery(id+"F11.boolean.opBoolean","MERGE",FACE,{"derivedFrom":[makeQuery(id+"F8.boolean.opBoolean","MERGE",FACE,{"derivedFrom":[makeQuery(id+"F7.boolean.opBoolean","MERGE",FACE,{"derivedFrom":[makeQuery(id+"F5.opExtrude","CAP_FACE",FACE,{"disambiguationData":[OSD([sQuery(id+"F2.wireOp",EDGE,"E74.top"),sQuery(id+"F2.wireOp",EDGE,"E75"),sQuery(id+"F2.wireOp",EDGE,"E76"),sQuery(id+"F2.wireOp",EDGE,"E77"),sQuery(id+"F2.wireOp",EDGE,"E89"),sQuery(id+"F2.wireOp",EDGE,"E90.trimOffspring"),sQuery(id+"F2.wireOp",EDGE,"E91"),sQuery(id+"F2.wireOp",EDGE,"E97.MirrorCS"),sQuery(id+"F2.wireOp",EDGE,"E98.MirrorCS"),sQuery(id+"F2.wireOp",EDGE,"E99.MirrorCS"),sQuery(id+"F2.wireOp",EDGE,"E100.MirrorCS"),sQuery(id+"F2.wireOp",EDGE,"E102.MirrorCS"),subQ33,sQuery(id+"F2.wireOp",EDGE,"E107.MirrorCS"),sQuery(id+"F2.wireOp",EDGE,"E108.MirrorCS"),sQuery(id+"F2.wireOp",EDGE,"E109.MirrorCS"),subQ32,sQuery(id+"F2.wireOp",EDGE,"E111.MirrorCS"),sQuery(id+"F2.wireOp",EDGE,"E115.MirrorCS"),sQuery(id+"F2.wireOp",EDGE,"E117.MirrorCS"),sQuery(id+"F2.wireOp",EDGE,"E121.MirrorCS"),sQuery(id+"F2.wireOp",EDGE,"E122.MirrorCS"),sQuery(id+"F2.wireOp",EDGE,"E123.MirrorCS"),sQuery(id+"F2.wireOp",EDGE,"E124.MirrorCS"),sQuery(id+"F2.wireOp",EDGE,"E126.MirrorCS"),sQuery(id+"F2.wireOp",EDGE,"E127.MirrorCS"),sQuery(id+"F2.wireOp",EDGE,"E128.MirrorCS"),sQuery(id+"F2.wireOp",EDGE,"E129.MirrorCS")])],"isStart":true}),makeQuery(id+"F7.opExtrude","SWEPT_FACE",FACE,{"disambiguationData":[OSD([subQ49])]}),makeQuery(id+"F7.opExtrude","SWEPT_FACE",FACE,{"disambiguationData":[OSD([subQ48])]})]}),makeQuery(id+"F8.opExtrude","SWEPT_FACE",FACE,{"disambiguationData":[OSD([subQ72])]}),makeQuery(id+"F8.opExtrude","SWEPT_FACE",FACE,{"disambiguationData":[OSD([subQ25])]})]}),makeQuery(id+"F6.opExtrude","SWEPT_FACE",FACE,{"disambiguationData":[OSD([subQ49,subQ48])]}),makeQuery(id+"F11.opExtrude","SWEPT_FACE",FACE,{"disambiguationData":[OSD([subQ72,subQ25])]}),makeQuery(id+"F11.opExtrude","SWEPT_FACE",FACE,{"disambiguationData":[OSD([subQ72])]}),makeQuery(id+"F11.opExtrude","SWEPT_FACE",FACE,{"disambiguationData":[OSD([subQ25])]})]}),makeQuery(id+"F12.opExtrude","SWEPT_FACE",FACE,{"disambiguationData":[OSD([subQ72])]}),makeQuery(id+"F12.opExtrude","SWEPT_FACE",FACE,{"disambiguationData":[OSD([subQ25])]})]}),makeQuery(id+"F13.opExtrude","SWEPT_FACE",FACE,{"disambiguationData":[OSD([subQ72])]}),makeQuery(id+"F13.opExtrude","SWEPT_FACE",FACE,{"disambiguationData":[OSD([subQ25])]})]})});}
            var sketch = newSketch(context, id + "F35", { "sketchPlane" : qUnion([Q0, Q1])});
            skLineSegment(sketch, "E716.bottom", {"start": v(-365, 200) * mm, "end": v(365, 200) * mm});
            skLineSegment(sketch, "E716.top", {"start": v(-365, -200) * mm, "end": v(365, -200) * mm});
            skLineSegment(sketch, "E716.left", {"start": v(-365, 200) * mm, "end": v(-365, -200) * mm});
            skLineSegment(sketch, "E716.right", {"start": v(365, 200) * mm, "end": v(365, -200) * mm});
            skPoint(sketch, "E716.middle", {"position": v(0, 0) * mm});
            skLineSegment(sketch, "E717.bottom", {"start": v(0, 0) * mm, "end": v(-365, 0) * mm});
            skLineSegment(sketch, "E717.top", {"start": v(0, -200) * mm, "end": v(-365, -200) * mm});
            skLineSegment(sketch, "E717.left", {"start": v(0, 0) * mm, "end": v(0, -200) * mm});
            skLineSegment(sketch, "E717.right", {"start": v(-365, 0) * mm, "end": v(-365, -200) * mm});
            skLineSegment(sketch, "E718.top", {"start": v(0, 50) * mm, "end": v(-365, 50) * mm});
            skLineSegment(sketch, "E718.left", {"start": v(0, 0) * mm, "end": v(0, 50) * mm});
            skLineSegment(sketch, "E718.right", {"start": v(-365, 0) * mm, "end": v(-365, 50) * mm});
            skLineSegment(sketch, "E719.bottom", {"start": v(0, 0) * mm, "end": v(-182.5, 0) * mm});
            skLineSegment(sketch, "E719.top", {"start": v(0, -50) * mm, "end": v(-182.5, -50) * mm});
            skLineSegment(sketch, "E719.left", {"start": v(0, 0) * mm, "end": v(0, -50) * mm});
            skLineSegment(sketch, "E719.right", {"start": v(-182.5, 0) * mm, "end": v(-182.5, -50) * mm});
            skPoint(sketch, "E720", {"position": v(-319.37, 0) * mm});
            skPoint(sketch, "E721", {"position": v(-273.75, 0) * mm});
            skPoint(sketch, "E722", {"position": v(-228.12, 0) * mm});
            skPoint(sketch, "E723", {"position": v(-192.5, 0) * mm});
            skPoint(sketch, "E724", {"position": v(-172.5, 0) * mm});
            skPoint(sketch, "E725", {"position": v(-136.88, 0) * mm});
            skPoint(sketch, "E726", {"position": v(-91.25, 0) * mm});
            skPoint(sketch, "E727", {"position": v(-45.62, 0) * mm});
            skPoint(sketch, "E728", {"position": v(-10, 0) * mm});
            skPoint(sketch, "E729", {"position": v(10, 0) * mm});
            skPoint(sketch, "E730", {"position": v(-365, -20) * mm});
            skPoint(sketch, "E731", {"position": v(-365, -40) * mm});
            skPoint(sketch, "E732", {"position": v(-365, -60) * mm});
            skPoint(sketch, "E733", {"position": v(-365, -87.5) * mm});
            skPoint(sketch, "E734", {"position": v(-365, -125) * mm});
            skPoint(sketch, "E735", {"position": v(-365, -162.5) * mm});
            skLineSegment(sketch, "E736.bottom", {"start": v(-365, 0) * mm, "end": v(0, 0) * mm});
            skLineSegment(sketch, "E736.top", {"start": v(-365, -0.5) * mm, "end": v(0, -0.5) * mm});
            skLineSegment(sketch, "E736.left", {"start": v(-365, 0) * mm, "end": v(-365, -0.5) * mm});
            skLineSegment(sketch, "E736.right", {"start": v(0, 0) * mm, "end": v(0, -0.5) * mm});
            skLineSegment(sketch, "E737.bottom", {"start": v(-365, -20) * mm, "end": v(0, -20) * mm});
            skLineSegment(sketch, "E737.top", {"start": v(-365, -20.5) * mm, "end": v(0, -20.5) * mm});
            skLineSegment(sketch, "E737.left", {"start": v(-365, -20) * mm, "end": v(-365, -20.5) * mm});
            skLineSegment(sketch, "E737.right", {"start": v(0, -20) * mm, "end": v(0, -20.5) * mm});
            skLineSegment(sketch, "E738.top", {"start": v(-365, -19.5) * mm, "end": v(0, -19.5) * mm});
            skLineSegment(sketch, "E738.left", {"start": v(-365, -20) * mm, "end": v(-365, -19.5) * mm});
            skLineSegment(sketch, "E738.right", {"start": v(0, -20) * mm, "end": v(0, -19.5) * mm});
            skLineSegment(sketch, "E739.bottom", {"start": v(-365, -40) * mm, "end": v(0, -40) * mm});
            skLineSegment(sketch, "E739.top", {"start": v(-365, -39.5) * mm, "end": v(0, -39.5) * mm});
            skLineSegment(sketch, "E739.left", {"start": v(-365, -40) * mm, "end": v(-365, -39.5) * mm});
            skLineSegment(sketch, "E739.right", {"start": v(0, -40) * mm, "end": v(0, -39.5) * mm});
            skLineSegment(sketch, "E740.top", {"start": v(-365, -40.5) * mm, "end": v(0, -40.5) * mm});
            skLineSegment(sketch, "E740.left", {"start": v(-365, -40) * mm, "end": v(-365, -40.5) * mm});
            skLineSegment(sketch, "E740.right", {"start": v(0, -40) * mm, "end": v(0, -40.5) * mm});
            skLineSegment(sketch, "E741.bottom", {"start": v(-365, -50) * mm, "end": v(0, -50) * mm});
            skLineSegment(sketch, "E741.top", {"start": v(-365, -49.5) * mm, "end": v(0, -49.5) * mm});
            skLineSegment(sketch, "E741.left", {"start": v(-365, -50) * mm, "end": v(-365, -49.5) * mm});
            skLineSegment(sketch, "E741.right", {"start": v(0, -50) * mm, "end": v(0, -49.5) * mm});
            skLineSegment(sketch, "E742.top", {"start": v(-365, -50.5) * mm, "end": v(0, -50.5) * mm});
            skLineSegment(sketch, "E742.left", {"start": v(-365, -50) * mm, "end": v(-365, -50.5) * mm});
            skLineSegment(sketch, "E742.right", {"start": v(0, -50) * mm, "end": v(0, -50.5) * mm});
            skLineSegment(sketch, "E743.bottom", {"start": v(-365, -60) * mm, "end": v(0, -60) * mm});
            skLineSegment(sketch, "E743.top", {"start": v(-365, -59.5) * mm, "end": v(0, -59.5) * mm});
            skLineSegment(sketch, "E743.left", {"start": v(-365, -60) * mm, "end": v(-365, -59.5) * mm});
            skLineSegment(sketch, "E743.right", {"start": v(0, -60) * mm, "end": v(0, -59.5) * mm});
            skLineSegment(sketch, "E744.top", {"start": v(-365, -60.5) * mm, "end": v(0, -60.5) * mm});
            skLineSegment(sketch, "E744.left", {"start": v(-365, -60) * mm, "end": v(-365, -60.5) * mm});
            skLineSegment(sketch, "E744.right", {"start": v(0, -60) * mm, "end": v(0, -60.5) * mm});
            skLineSegment(sketch, "E745.bottom", {"start": v(-365, -87.5) * mm, "end": v(0, -87.5) * mm});
            skLineSegment(sketch, "E745.top", {"start": v(-365, -87) * mm, "end": v(0, -87) * mm});
            skLineSegment(sketch, "E745.left", {"start": v(-365, -87.5) * mm, "end": v(-365, -87) * mm});
            skLineSegment(sketch, "E745.right", {"start": v(0, -87.5) * mm, "end": v(0, -87) * mm});
            skLineSegment(sketch, "E746.top", {"start": v(-365, -88) * mm, "end": v(0, -88) * mm});
            skLineSegment(sketch, "E746.left", {"start": v(-365, -87.5) * mm, "end": v(-365, -88) * mm});
            skLineSegment(sketch, "E746.right", {"start": v(0, -87.5) * mm, "end": v(0, -88) * mm});
            skLineSegment(sketch, "E747.bottom", {"start": v(-365, -125) * mm, "end": v(0, -125) * mm});
            skLineSegment(sketch, "E747.top", {"start": v(-365, -124.5) * mm, "end": v(0, -124.5) * mm});
            skLineSegment(sketch, "E747.left", {"start": v(-365, -125) * mm, "end": v(-365, -124.5) * mm});
            skLineSegment(sketch, "E747.right", {"start": v(0, -125) * mm, "end": v(0, -124.5) * mm});
            skLineSegment(sketch, "E748.top", {"start": v(-365, -125.5) * mm, "end": v(0, -125.5) * mm});
            skLineSegment(sketch, "E748.left", {"start": v(-365, -125) * mm, "end": v(-365, -125.5) * mm});
            skLineSegment(sketch, "E748.right", {"start": v(0, -125) * mm, "end": v(0, -125.5) * mm});
            skLineSegment(sketch, "E749.bottom", {"start": v(-365, -162.5) * mm, "end": v(0, -162.5) * mm});
            skLineSegment(sketch, "E749.top", {"start": v(-365, -162) * mm, "end": v(0, -162) * mm});
            skLineSegment(sketch, "E749.left", {"start": v(-365, -162.5) * mm, "end": v(-365, -162) * mm});
            skLineSegment(sketch, "E749.right", {"start": v(0, -162.5) * mm, "end": v(0, -162) * mm});
            skLineSegment(sketch, "E750.top", {"start": v(-365, -163) * mm, "end": v(0, -163) * mm});
            skLineSegment(sketch, "E750.left", {"start": v(-365, -162.5) * mm, "end": v(-365, -163) * mm});
            skLineSegment(sketch, "E750.right", {"start": v(0, -162.5) * mm, "end": v(0, -163) * mm});
            skLineSegment(sketch, "E751.bottom", {"start": v(-319.37, 0) * mm, "end": v(-319.87, 0) * mm});
            skLineSegment(sketch, "E751.top", {"start": v(-319.37, -200) * mm, "end": v(-319.87, -200) * mm});
            skLineSegment(sketch, "E751.left", {"start": v(-319.37, 0) * mm, "end": v(-319.37, -200) * mm});
            skLineSegment(sketch, "E751.right", {"start": v(-319.87, 0) * mm, "end": v(-319.87, -200) * mm});
            skLineSegment(sketch, "E752.bottom", {"start": v(-319.37, 0) * mm, "end": v(-318.87, 0) * mm});
            skLineSegment(sketch, "E752.top", {"start": v(-319.37, -200) * mm, "end": v(-318.87, -200) * mm});
            skLineSegment(sketch, "E752.right", {"start": v(-318.87, 0) * mm, "end": v(-318.87, -200) * mm});
            skLineSegment(sketch, "E753.bottom", {"start": v(-273.75, 0) * mm, "end": v(-274.25, 0) * mm});
            skLineSegment(sketch, "E753.top", {"start": v(-273.75, -200) * mm, "end": v(-274.25, -200) * mm});
            skLineSegment(sketch, "E753.left", {"start": v(-273.75, 0) * mm, "end": v(-273.75, -200) * mm});
            skLineSegment(sketch, "E753.right", {"start": v(-274.25, 0) * mm, "end": v(-274.25, -200) * mm});
            skLineSegment(sketch, "E754.bottom", {"start": v(-273.75, 0) * mm, "end": v(-273.25, 0) * mm});
            skLineSegment(sketch, "E754.top", {"start": v(-273.75, -200) * mm, "end": v(-273.25, -200) * mm});
            skLineSegment(sketch, "E754.right", {"start": v(-273.25, 0) * mm, "end": v(-273.25, -200) * mm});
            skLineSegment(sketch, "E755.bottom", {"start": v(-228.12, 0) * mm, "end": v(-228.62, 0) * mm});
            skLineSegment(sketch, "E755.top", {"start": v(-228.12, -200) * mm, "end": v(-228.62, -200) * mm});
            skLineSegment(sketch, "E755.left", {"start": v(-228.12, 0) * mm, "end": v(-228.12, -200) * mm});
            skLineSegment(sketch, "E755.right", {"start": v(-228.62, 0) * mm, "end": v(-228.62, -200) * mm});
            skLineSegment(sketch, "E756.bottom", {"start": v(-228.12, 0) * mm, "end": v(-227.62, 0) * mm});
            skLineSegment(sketch, "E756.top", {"start": v(-228.12, -200) * mm, "end": v(-227.62, -200) * mm});
            skLineSegment(sketch, "E756.right", {"start": v(-227.62, 0) * mm, "end": v(-227.62, -200) * mm});
            skLineSegment(sketch, "E757.bottom", {"start": v(-192.5, 0) * mm, "end": v(-193, 0) * mm});
            skLineSegment(sketch, "E757.top", {"start": v(-192.5, -200) * mm, "end": v(-193, -200) * mm});
            skLineSegment(sketch, "E757.left", {"start": v(-192.5, 0) * mm, "end": v(-192.5, -200) * mm});
            skLineSegment(sketch, "E757.right", {"start": v(-193, 0) * mm, "end": v(-193, -200) * mm});
            skLineSegment(sketch, "E758.bottom", {"start": v(-192.5, 0) * mm, "end": v(-192, 0) * mm});
            skLineSegment(sketch, "E758.top", {"start": v(-192.5, -200) * mm, "end": v(-192, -200) * mm});
            skLineSegment(sketch, "E758.right", {"start": v(-192, 0) * mm, "end": v(-192, -200) * mm});
            skLineSegment(sketch, "E759.bottom", {"start": v(-182.5, 0) * mm, "end": v(-183, 0) * mm});
            skLineSegment(sketch, "E759.top", {"start": v(-182.5, -200) * mm, "end": v(-183, -200) * mm});
            skLineSegment(sketch, "E759.left", {"start": v(-182.5, 0) * mm, "end": v(-182.5, -200) * mm});
            skLineSegment(sketch, "E759.right", {"start": v(-183, 0) * mm, "end": v(-183, -200) * mm});
            skLineSegment(sketch, "E760.bottom", {"start": v(-182.5, 0) * mm, "end": v(-182, 0) * mm});
            skLineSegment(sketch, "E760.top", {"start": v(-182.5, -200) * mm, "end": v(-182, -200) * mm});
            skLineSegment(sketch, "E760.right", {"start": v(-182, 0) * mm, "end": v(-182, -200) * mm});
            skLineSegment(sketch, "E761.bottom", {"start": v(-172.5, 0) * mm, "end": v(-173, 0) * mm});
            skLineSegment(sketch, "E761.top", {"start": v(-172.5, -200) * mm, "end": v(-173, -200) * mm});
            skLineSegment(sketch, "E761.left", {"start": v(-172.5, 0) * mm, "end": v(-172.5, -200) * mm});
            skLineSegment(sketch, "E761.right", {"start": v(-173, 0) * mm, "end": v(-173, -200) * mm});
            skLineSegment(sketch, "E762.bottom", {"start": v(-172.5, 0) * mm, "end": v(-172, 0) * mm});
            skLineSegment(sketch, "E762.top", {"start": v(-172.5, -200) * mm, "end": v(-172, -200) * mm});
            skLineSegment(sketch, "E762.right", {"start": v(-172, 0) * mm, "end": v(-172, -200) * mm});
            skLineSegment(sketch, "E763.bottom", {"start": v(-136.88, 0) * mm, "end": v(-137.38, 0) * mm});
            skLineSegment(sketch, "E763.top", {"start": v(-136.87, -200) * mm, "end": v(-137.37, -200) * mm});
            skLineSegment(sketch, "E763.left", {"start": v(-136.88, 0) * mm, "end": v(-136.88, -200) * mm});
            skLineSegment(sketch, "E763.right", {"start": v(-137.38, 0) * mm, "end": v(-137.37, -200) * mm});
            skLineSegment(sketch, "E764.bottom", {"start": v(-136.88, 0) * mm, "end": v(-136.38, 0) * mm});
            skLineSegment(sketch, "E764.top", {"start": v(-136.88, -200) * mm, "end": v(-136.38, -200) * mm});
            skLineSegment(sketch, "E764.right", {"start": v(-136.38, 0) * mm, "end": v(-136.38, -200) * mm});
            skLineSegment(sketch, "E765.bottom", {"start": v(-91.25, 0) * mm, "end": v(-91.75, 0) * mm});
            skLineSegment(sketch, "E765.top", {"start": v(-91.25, -200) * mm, "end": v(-91.75, -200) * mm});
            skLineSegment(sketch, "E765.left", {"start": v(-91.25, 0) * mm, "end": v(-91.25, -200) * mm});
            skLineSegment(sketch, "E765.right", {"start": v(-91.75, 0) * mm, "end": v(-91.75, -200) * mm});
            skLineSegment(sketch, "E766.bottom", {"start": v(-91.25, 0) * mm, "end": v(-90.75, 0) * mm});
            skLineSegment(sketch, "E766.top", {"start": v(-91.25, -200) * mm, "end": v(-90.75, -200) * mm});
            skLineSegment(sketch, "E766.right", {"start": v(-90.75, 0) * mm, "end": v(-90.75, -200) * mm});
            skLineSegment(sketch, "E767.bottom", {"start": v(-45.62, 0) * mm, "end": v(-46.12, 0) * mm});
            skLineSegment(sketch, "E767.top", {"start": v(-45.62, -200) * mm, "end": v(-46.12, -200) * mm});
            skLineSegment(sketch, "E767.left", {"start": v(-45.62, 0) * mm, "end": v(-45.62, -200) * mm});
            skLineSegment(sketch, "E767.right", {"start": v(-46.12, 0) * mm, "end": v(-46.12, -200) * mm});
            skLineSegment(sketch, "E768.bottom", {"start": v(-45.62, 0) * mm, "end": v(-45.12, 0) * mm});
            skLineSegment(sketch, "E768.top", {"start": v(-45.62, -200) * mm, "end": v(-45.12, -200) * mm});
            skLineSegment(sketch, "E768.right", {"start": v(-45.12, 0) * mm, "end": v(-45.12, -200) * mm});
            skLineSegment(sketch, "E769.bottom", {"start": v(0, 0) * mm, "end": v(-0.5, 0) * mm});
            skLineSegment(sketch, "E769.top", {"start": v(0, -200) * mm, "end": v(-0.5, -200) * mm});
            skLineSegment(sketch, "E769.right", {"start": v(-0.5, 0) * mm, "end": v(-0.5, -200) * mm});
            skLineSegment(sketch, "E770.bottom", {"start": v(-10, 0) * mm, "end": v(-9.5, 0) * mm});
            skLineSegment(sketch, "E770.top", {"start": v(-10, -200) * mm, "end": v(-9.5, -200) * mm});
            skLineSegment(sketch, "E770.left", {"start": v(-10, 0) * mm, "end": v(-10, -200) * mm});
            skLineSegment(sketch, "E770.right", {"start": v(-9.5, 0) * mm, "end": v(-9.5, -200) * mm});
            skLineSegment(sketch, "E771.bottom", {"start": v(-10, 0) * mm, "end": v(-10.5, 0) * mm});
            skLineSegment(sketch, "E771.top", {"start": v(-10, -200) * mm, "end": v(-10.5, -200) * mm});
            skLineSegment(sketch, "E771.right", {"start": v(-10.5, 0) * mm, "end": v(-10.5, -200) * mm});
            skLineSegment(sketch, "E772.MirrorCS", {"start": v(365, 0) * mm, "end": v(0, 0) * mm});
            skLineSegment(sketch, "E773.MirrorCS", {"start": v(365, -0.5) * mm, "end": v(0, -0.5) * mm});
            skLineSegment(sketch, "E774.MirrorCS", {"start": v(365, -19.5) * mm, "end": v(0, -19.5) * mm});
            skLineSegment(sketch, "E775.MirrorCS", {"start": v(365, -20) * mm, "end": v(0, -20) * mm});
            skLineSegment(sketch, "E776.MirrorCS", {"start": v(365, -20.5) * mm, "end": v(0, -20.5) * mm});
            skLineSegment(sketch, "E777.MirrorCS", {"start": v(0.5, 0) * mm, "end": v(0.5, -200) * mm});
            skLineSegment(sketch, "E778.MirrorCS", {"start": v(365, -39.5) * mm, "end": v(0, -39.5) * mm});
            skLineSegment(sketch, "E779.MirrorCS", {"start": v(365, -40) * mm, "end": v(0, -40) * mm});
            skLineSegment(sketch, "E780.MirrorCS", {"start": v(365, -40.5) * mm, "end": v(0, -40.5) * mm});
            skLineSegment(sketch, "E781.MirrorCS", {"start": v(365, -49.5) * mm, "end": v(0, -49.5) * mm});
            skLineSegment(sketch, "E782.MirrorCS", {"start": v(0, -50) * mm, "end": v(182.5, -50) * mm});
            skLineSegment(sketch, "E783.MirrorCS", {"start": v(365, -50.5) * mm, "end": v(0, -50.5) * mm});
            skLineSegment(sketch, "E784.MirrorCS", {"start": v(365, -59.5) * mm, "end": v(0, -59.5) * mm});
            skLineSegment(sketch, "E785.MirrorCS", {"start": v(365, -60) * mm, "end": v(0, -60) * mm});
            skLineSegment(sketch, "E786.MirrorCS", {"start": v(365, -60.5) * mm, "end": v(0, -60.5) * mm});
            skLineSegment(sketch, "E787.MirrorCS", {"start": v(365, -87) * mm, "end": v(0, -87) * mm});
            skLineSegment(sketch, "E788.MirrorCS", {"start": v(365, -87.5) * mm, "end": v(0, -87.5) * mm});
            skLineSegment(sketch, "E789.MirrorCS", {"start": v(365, -88) * mm, "end": v(0, -88) * mm});
            skLineSegment(sketch, "E790.MirrorCS", {"start": v(365, -124.5) * mm, "end": v(0, -124.5) * mm});
            skLineSegment(sketch, "E791.MirrorCS", {"start": v(365, -125) * mm, "end": v(0, -125) * mm});
            skLineSegment(sketch, "E792.MirrorCS", {"start": v(365, -125.5) * mm, "end": v(0, -125.5) * mm});
            skLineSegment(sketch, "E793.MirrorCS", {"start": v(365, -162) * mm, "end": v(0, -162) * mm});
            skLineSegment(sketch, "E794.MirrorCS", {"start": v(365, -162.5) * mm, "end": v(0, -162.5) * mm});
            skLineSegment(sketch, "E795.MirrorCS", {"start": v(365, -163) * mm, "end": v(0, -163) * mm});
            skLineSegment(sketch, "E796.MirrorCS", {"start": v(9.5, 0) * mm, "end": v(9.5, -200) * mm});
            skLineSegment(sketch, "E797.MirrorCS", {"start": v(10, 0) * mm, "end": v(10, -200) * mm});
            skLineSegment(sketch, "E798.MirrorCS", {"start": v(10.5, 0) * mm, "end": v(10.5, -200) * mm});
            skLineSegment(sketch, "E799.MirrorCS", {"start": v(45.12, 0) * mm, "end": v(45.12, -200) * mm});
            skLineSegment(sketch, "E800.MirrorCS", {"start": v(45.62, 0) * mm, "end": v(45.62, -200) * mm});
            skLineSegment(sketch, "E801.MirrorCS", {"start": v(46.12, 0) * mm, "end": v(46.12, -200) * mm});
            skLineSegment(sketch, "E802.MirrorCS", {"start": v(90.75, 0) * mm, "end": v(90.75, -200) * mm});
            skLineSegment(sketch, "E803.MirrorCS", {"start": v(91.25, 0) * mm, "end": v(91.25, -200) * mm});
            skLineSegment(sketch, "E804.MirrorCS", {"start": v(91.75, 0) * mm, "end": v(91.75, -200) * mm});
            skLineSegment(sketch, "E805.MirrorCS", {"start": v(136.38, 0) * mm, "end": v(136.38, -200) * mm});
            skLineSegment(sketch, "E806.MirrorCS", {"start": v(136.88, 0) * mm, "end": v(136.88, -200) * mm});
            skLineSegment(sketch, "E807.MirrorCS", {"start": v(137.38, 0) * mm, "end": v(137.37, -200) * mm});
            skLineSegment(sketch, "E808.MirrorCS", {"start": v(172, 0) * mm, "end": v(172, -200) * mm});
            skLineSegment(sketch, "E809.MirrorCS", {"start": v(172.5, 0) * mm, "end": v(172.5, -200) * mm});
            skLineSegment(sketch, "E810.MirrorCS", {"start": v(173, 0) * mm, "end": v(173, -200) * mm});
            skLineSegment(sketch, "E811.MirrorCS", {"start": v(182, 0) * mm, "end": v(182, -200) * mm});
            skLineSegment(sketch, "E812.MirrorCS", {"start": v(183, 0) * mm, "end": v(183, -200) * mm});
            skLineSegment(sketch, "E813.MirrorCS", {"start": v(192, 0) * mm, "end": v(192, -200) * mm});
            skLineSegment(sketch, "E814.MirrorCS", {"start": v(192.5, 0) * mm, "end": v(192.5, -200) * mm});
            skLineSegment(sketch, "E815.MirrorCS", {"start": v(193, 0) * mm, "end": v(193, -200) * mm});
            skLineSegment(sketch, "E816.MirrorCS", {"start": v(319.87, 0) * mm, "end": v(319.87, -200) * mm});
            skLineSegment(sketch, "E817.MirrorCS", {"start": v(319.37, 0) * mm, "end": v(319.37, -200) * mm});
            skLineSegment(sketch, "E818.MirrorCS", {"start": v(318.87, 0) * mm, "end": v(318.87, -200) * mm});
            skLineSegment(sketch, "E819.MirrorCS", {"start": v(274.25, 0) * mm, "end": v(274.25, -200) * mm});
            skLineSegment(sketch, "E820.MirrorCS", {"start": v(273.75, 0) * mm, "end": v(273.75, -200) * mm});
            skLineSegment(sketch, "E821.MirrorCS", {"start": v(273.25, 0) * mm, "end": v(273.25, -200) * mm});
            skLineSegment(sketch, "E822.MirrorCS", {"start": v(228.62, 0) * mm, "end": v(228.62, -200) * mm});
            skLineSegment(sketch, "E823.MirrorCS", {"start": v(228.12, 0) * mm, "end": v(228.12, -200) * mm});
            skLineSegment(sketch, "E824.MirrorCS", {"start": v(227.62, 0) * mm, "end": v(227.62, -200) * mm});
            skLineSegment(sketch, "E825.MirrorCS", {"start": v(-365, 0.5) * mm, "end": v(0, 0.5) * mm});
            skLineSegment(sketch, "E826.MirrorCS", {"start": v(365, 0.5) * mm, "end": v(0, 0.5) * mm});
            skLineSegment(sketch, "E827.MirrorCS", {"start": v(-365, 39.5) * mm, "end": v(0, 39.5) * mm});
            skLineSegment(sketch, "E828.MirrorCS", {"start": v(-365, 40.5) * mm, "end": v(0, 40.5) * mm});
            skLineSegment(sketch, "E829.MirrorCS", {"start": v(-365, 49.5) * mm, "end": v(0, 49.5) * mm});
            skLineSegment(sketch, "E830.MirrorCS", {"start": v(-365, 50.5) * mm, "end": v(0, 50.5) * mm});
            skLineSegment(sketch, "E831.MirrorCS", {"start": v(-365, 59.5) * mm, "end": v(0, 59.5) * mm});
            skLineSegment(sketch, "E832.MirrorCS", {"start": v(-365, 60.5) * mm, "end": v(0, 60.5) * mm});
            skLineSegment(sketch, "E833.MirrorCS", {"start": v(-365, 19.5) * mm, "end": v(0, 19.5) * mm});
            skLineSegment(sketch, "E834.MirrorCS", {"start": v(-365, 20.5) * mm, "end": v(0, 20.5) * mm});
            skLineSegment(sketch, "E835.MirrorCS", {"start": v(-319.87, 0) * mm, "end": v(-319.87, 200) * mm});
            skLineSegment(sketch, "E836.MirrorCS", {"start": v(-318.87, 0) * mm, "end": v(-318.87, 200) * mm});
            skLineSegment(sketch, "E837.MirrorCS", {"start": v(-274.25, 0) * mm, "end": v(-274.25, 200) * mm});
            skLineSegment(sketch, "E838.MirrorCS", {"start": v(-273.25, 0) * mm, "end": v(-273.25, 200) * mm});
            skLineSegment(sketch, "E839.MirrorCS", {"start": v(-228.62, 0) * mm, "end": v(-228.62, 200) * mm});
            skLineSegment(sketch, "E840.MirrorCS", {"start": v(-227.62, 0) * mm, "end": v(-227.62, 200) * mm});
            skLineSegment(sketch, "E841.MirrorCS", {"start": v(-193, 0) * mm, "end": v(-193, 200) * mm});
            skLineSegment(sketch, "E842.MirrorCS", {"start": v(-192, 0) * mm, "end": v(-192, 200) * mm});
            skLineSegment(sketch, "E843.MirrorCS", {"start": v(-183, 0) * mm, "end": v(-183, 200) * mm});
            skLineSegment(sketch, "E844.MirrorCS", {"start": v(-182, 0) * mm, "end": v(-182, 200) * mm});
            skLineSegment(sketch, "E845.MirrorCS", {"start": v(-173, 0) * mm, "end": v(-173, 200) * mm});
            skLineSegment(sketch, "E846.MirrorCS", {"start": v(-172, 0) * mm, "end": v(-172, 200) * mm});
            skLineSegment(sketch, "E847.MirrorCS", {"start": v(-137.38, 0) * mm, "end": v(-137.37, 200) * mm});
            skLineSegment(sketch, "E848.MirrorCS", {"start": v(-136.38, 0) * mm, "end": v(-136.38, 200) * mm});
            skLineSegment(sketch, "E849.MirrorCS", {"start": v(-91.75, 0) * mm, "end": v(-91.75, 200) * mm});
            skLineSegment(sketch, "E850.MirrorCS", {"start": v(-90.75, 0) * mm, "end": v(-90.75, 200) * mm});
            skLineSegment(sketch, "E851.MirrorCS", {"start": v(-46.12, 0) * mm, "end": v(-46.12, 200) * mm});
            skLineSegment(sketch, "E852.MirrorCS", {"start": v(-45.12, 0) * mm, "end": v(-45.12, 200) * mm});
            skLineSegment(sketch, "E853.MirrorCS", {"start": v(-10.5, 0) * mm, "end": v(-10.5, 200) * mm});
            skLineSegment(sketch, "E854.MirrorCS", {"start": v(-9.5, 0) * mm, "end": v(-9.5, 200) * mm});
            skLineSegment(sketch, "E855.MirrorCS", {"start": v(-0.5, 0) * mm, "end": v(-0.5, 200) * mm});
            skLineSegment(sketch, "E856.MirrorCS", {"start": v(0.5, 0) * mm, "end": v(0.5, 200) * mm});
            skLineSegment(sketch, "E857.MirrorCS", {"start": v(9.5, 0) * mm, "end": v(9.5, 200) * mm});
            skLineSegment(sketch, "E858.MirrorCS", {"start": v(10.5, 0) * mm, "end": v(10.5, 200) * mm});
            skLineSegment(sketch, "E859.MirrorCS", {"start": v(365, 19.5) * mm, "end": v(0, 19.5) * mm});
            skLineSegment(sketch, "E860.MirrorCS", {"start": v(365, 20.5) * mm, "end": v(0, 20.5) * mm});
            skLineSegment(sketch, "E861.MirrorCS", {"start": v(365, 39.5) * mm, "end": v(0, 39.5) * mm});
            skLineSegment(sketch, "E862.MirrorCS", {"start": v(365, 40.5) * mm, "end": v(0, 40.5) * mm});
            skLineSegment(sketch, "E863.MirrorCS", {"start": v(365, 49.5) * mm, "end": v(0, 49.5) * mm});
            skLineSegment(sketch, "E864.MirrorCS", {"start": v(365, 50.5) * mm, "end": v(0, 50.5) * mm});
            skLineSegment(sketch, "E865.MirrorCS", {"start": v(365, 59.5) * mm, "end": v(0, 59.5) * mm});
            skLineSegment(sketch, "E866.MirrorCS", {"start": v(365, 60.5) * mm, "end": v(0, 60.5) * mm});
            skSolve(sketch);
        }
        {
            var Q0;
            {var subQ0=sQuery(id+"F25.wireOp",EDGE,"E258.trimOffspring");var subQ7=makeQuery(id+"F25.imprint","INTERSECT",VERTEX,{"derivedFrom":[subQ0,sQuery(id+"F25.wireOp",EDGE,"E500.trimOffspring")]});Q0=makeQuery(id+"F25.imprint","IMPRINT",FACE,{"disambiguationData":[TD([[makeQuery(id+"F25.imprint","IMPRINT",EDGE,{"disambiguationData":[TD([[subQ7,1.0]])],"derivedFrom":subQ0}),-1.0]])]});}
            var Q1;
            {var subQ0=sQuery(id+"F25.wireOp",EDGE,"E497.trimOffspring");var subQ1=sQuery(id+"F25.wireOp",EDGE,"E258.trimOffspring");var subQ2=makeQuery(id+"F25.imprint","INTERSECT",VERTEX,{"derivedFrom":[subQ1,subQ0]});Q1=makeQuery(id+"F25.imprint","IMPRINT",FACE,{"disambiguationData":[TD([[makeQuery(id+"F25.imprint","IMPRINT",EDGE,{"disambiguationData":[TD([[subQ2,-1.0]])],"derivedFrom":subQ1}),-1.0]])]});}
            var Q2;
            {var subQ0=sQuery(id+"F25.wireOp",EDGE,"E496.trimOffspring");var subQ1=sQuery(id+"F25.wireOp",EDGE,"E258.trimOffspring");var subQ2=makeQuery(id+"F25.imprint","INTERSECT",VERTEX,{"derivedFrom":[subQ1,subQ0]});Q2=makeQuery(id+"F25.imprint","IMPRINT",FACE,{"disambiguationData":[TD([[makeQuery(id+"F25.imprint","IMPRINT",EDGE,{"disambiguationData":[TD([[subQ2,1.0]])],"derivedFrom":subQ1}),-1.0]])]});}
            var Q3;
            {var subQ0=sQuery(id+"F25.wireOp",EDGE,"E581.trimOffspring");var subQ1=sQuery(id+"F25.wireOp",EDGE,"E414.MirrorCS");var subQ2=makeQuery(id+"F25.imprint","INTERSECT",VERTEX,{"derivedFrom":[subQ1,subQ0]});Q3=makeQuery(id+"F25.imprint","IMPRINT",FACE,{"disambiguationData":[TD([[makeQuery(id+"F25.imprint","IMPRINT",EDGE,{"disambiguationData":[TD([[subQ2,-1.0]])],"derivedFrom":subQ1}),1.0]])]});}
            var Q4;
            {var subQ0=sQuery(id+"F25.wireOp",EDGE,"E579.trimOffspring");var subQ1=sQuery(id+"F25.wireOp",EDGE,"E414.MirrorCS");var subQ2=makeQuery(id+"F25.imprint","INTERSECT",VERTEX,{"derivedFrom":[subQ1,subQ0]});Q4=makeQuery(id+"F25.imprint","IMPRINT",FACE,{"disambiguationData":[TD([[makeQuery(id+"F25.imprint","IMPRINT",EDGE,{"disambiguationData":[TD([[subQ2,-1.0]])],"derivedFrom":subQ1}),1.0]])]});}
            var Q5;
            {var subQ0=sQuery(id+"F25.wireOp",EDGE,"E580.trimOffspring");var subQ1=sQuery(id+"F25.wireOp",EDGE,"E414.MirrorCS");var subQ2=makeQuery(id+"F25.imprint","INTERSECT",VERTEX,{"derivedFrom":[subQ1,subQ0]});Q5=makeQuery(id+"F25.imprint","IMPRINT",FACE,{"disambiguationData":[TD([[makeQuery(id+"F25.imprint","IMPRINT",EDGE,{"disambiguationData":[TD([[subQ2,-1.0]])],"derivedFrom":subQ1}),1.0]])]});}
            var Q6;
            {var subQ0=sQuery(id+"F25.wireOp",EDGE,"E574.trimOffspring");var subQ1=sQuery(id+"F25.wireOp",EDGE,"E414.MirrorCS");var subQ2=makeQuery(id+"F25.imprint","INTERSECT",VERTEX,{"derivedFrom":[subQ1,subQ0]});Q6=makeQuery(id+"F25.imprint","IMPRINT",FACE,{"disambiguationData":[TD([[makeQuery(id+"F25.imprint","IMPRINT",EDGE,{"disambiguationData":[TD([[subQ2,-1.0]])],"derivedFrom":subQ1}),1.0]])]});}
            var Q7;
            {var subQ0=sQuery(id+"F25.wireOp",EDGE,"E578.trimOffspring");var subQ1=sQuery(id+"F25.wireOp",EDGE,"E414.MirrorCS");var subQ2=makeQuery(id+"F25.imprint","INTERSECT",VERTEX,{"derivedFrom":[subQ1,subQ0]});Q7=makeQuery(id+"F25.imprint","IMPRINT",FACE,{"disambiguationData":[TD([[makeQuery(id+"F25.imprint","IMPRINT",EDGE,{"disambiguationData":[TD([[subQ2,-1.0]])],"derivedFrom":subQ1}),1.0]])]});}
            var Q8;
            {var subQ0=sQuery(id+"F25.wireOp",EDGE,"E577.trimOffspring");var subQ1=sQuery(id+"F25.wireOp",EDGE,"E414.MirrorCS");var subQ2=makeQuery(id+"F25.imprint","INTERSECT",VERTEX,{"derivedFrom":[subQ1,subQ0]});Q8=makeQuery(id+"F25.imprint","IMPRINT",FACE,{"disambiguationData":[TD([[makeQuery(id+"F25.imprint","IMPRINT",EDGE,{"disambiguationData":[TD([[subQ2,-1.0]])],"derivedFrom":subQ1}),1.0]])]});}
            var Q9;
            {var subQ0=sQuery(id+"F25.wireOp",EDGE,"E424.MirrorCS");var subQ6=makeQuery(id+"F25.imprint","INTERSECT",VERTEX,{"derivedFrom":[subQ0,sQuery(id+"F25.wireOp",EDGE,"E545.trimOffspring")]});Q9=makeQuery(id+"F25.imprint","IMPRINT",FACE,{"disambiguationData":[TD([[makeQuery(id+"F25.imprint","IMPRINT",EDGE,{"disambiguationData":[TD([[subQ6,1.0]])],"derivedFrom":subQ0}),-1.0]])]});}
            var Q10;
            {var subQ0=sQuery(id+"F25.wireOp",EDGE,"E460.MirrorCS");var subQ1=sQuery(id+"F25.wireOp",EDGE,"E424.MirrorCS");var subQ2=makeQuery(id+"F25.imprint","INTERSECT",VERTEX,{"derivedFrom":[subQ1,subQ0]});Q10=makeQuery(id+"F25.imprint","IMPRINT",FACE,{"disambiguationData":[TD([[makeQuery(id+"F25.imprint","IMPRINT",EDGE,{"disambiguationData":[TD([[subQ2,-1.0]])],"derivedFrom":subQ1}),-1.0]])]});}
            var Q11;
            {var subQ0=sQuery(id+"F25.wireOp",EDGE,"E464.MirrorCS");var subQ1=sQuery(id+"F25.wireOp",EDGE,"E424.MirrorCS");var subQ2=makeQuery(id+"F25.imprint","INTERSECT",VERTEX,{"derivedFrom":[subQ1,subQ0]});Q11=makeQuery(id+"F25.imprint","IMPRINT",FACE,{"disambiguationData":[TD([[makeQuery(id+"F25.imprint","IMPRINT",EDGE,{"disambiguationData":[TD([[subQ2,1.0]])],"derivedFrom":subQ1}),-1.0]])]});}
            extrude(context, id + "F36", {"entities" : qUnion([Q0, Q1, Q2, Q3, Q4, Q5, Q6, Q7, Q8, Q9, Q10, Q11]), "operationType" : NewBodyOperationType.REMOVE, "depth" : 19.5 * mm, "offsetDistance" : 25 * mm});
        }
        {
            var Q0;
            {var subQ0=sQuery(id+"F35.wireOp",EDGE,"E752.right");var subQ1=sQuery(id+"F35.wireOp",EDGE,"E741.top");var subQ2=makeQuery(id+"F35.imprint","INTERSECT",VERTEX,{"derivedFrom":[subQ1,subQ0]});Q0=makeQuery(id+"F35.imprint","IMPRINT",FACE,{"disambiguationData":[TD([[makeQuery(id+"F35.imprint","IMPRINT",EDGE,{"disambiguationData":[TD([[subQ2,-1.0]])],"derivedFrom":subQ1}),-1.0]])]});}
            var Q1;
            {var subQ0=sQuery(id+"F35.wireOp",EDGE,"E752.right");var subQ1=sQuery(id+"F35.wireOp",EDGE,"E740.top");var subQ2=makeQuery(id+"F35.imprint","INTERSECT",VERTEX,{"derivedFrom":[subQ1,subQ0]});Q1=makeQuery(id+"F35.imprint","IMPRINT",FACE,{"disambiguationData":[TD([[makeQuery(id+"F35.imprint","IMPRINT",EDGE,{"disambiguationData":[TD([[subQ2,-1.0]])],"derivedFrom":subQ1}),-1.0]])]});}
            var Q2;
            {var subQ0=sQuery(id+"F35.wireOp",EDGE,"E752.right");var subQ1=sQuery(id+"F35.wireOp",EDGE,"E739.top");var subQ2=makeQuery(id+"F35.imprint","INTERSECT",VERTEX,{"derivedFrom":[subQ1,subQ0]});var subQ3=sQuery(id+"F35.wireOp",EDGE,"E753.right");var subQ4=makeQuery(id+"F35.imprint","INTERSECT",VERTEX,{"derivedFrom":[subQ1,subQ3]});Q2=makeQuery(id+"F35.imprint","IMPRINT",FACE,{"disambiguationData":[TD([[makeQuery(id+"F35.imprint","IMPRINT",EDGE,{"disambiguationData":[TD([[subQ2,-1.0],[subQ4,1.0]])],"derivedFrom":subQ1}),-1.0]])]});}
            var Q3;
            {var subQ0=sQuery(id+"F35.wireOp",EDGE,"E752.right");var subQ1=sQuery(id+"F35.wireOp",EDGE,"E739.bottom");var subQ2=makeQuery(id+"F35.imprint","INTERSECT",VERTEX,{"derivedFrom":[subQ1,subQ0]});Q3=makeQuery(id+"F35.imprint","IMPRINT",FACE,{"disambiguationData":[TD([[makeQuery(id+"F35.imprint","IMPRINT",EDGE,{"disambiguationData":[TD([[subQ2,-1.0]])],"derivedFrom":subQ1}),-1.0]])]});}
            var Q4;
            {var subQ0=sQuery(id+"F35.wireOp",EDGE,"E752.right");var subQ1=sQuery(id+"F35.wireOp",EDGE,"E741.bottom");var subQ2=makeQuery(id+"F35.imprint","INTERSECT",VERTEX,{"derivedFrom":[subQ1,subQ0]});Q4=makeQuery(id+"F35.imprint","IMPRINT",FACE,{"disambiguationData":[TD([[makeQuery(id+"F35.imprint","IMPRINT",EDGE,{"disambiguationData":[TD([[subQ2,-1.0]])],"derivedFrom":subQ1}),-1.0]])]});}
            var Q5;
            {var subQ0=sQuery(id+"F35.wireOp",EDGE,"E752.right");var subQ1=sQuery(id+"F35.wireOp",EDGE,"E742.top");var subQ2=makeQuery(id+"F35.imprint","INTERSECT",VERTEX,{"derivedFrom":[subQ1,subQ0]});Q5=makeQuery(id+"F35.imprint","IMPRINT",FACE,{"disambiguationData":[TD([[makeQuery(id+"F35.imprint","IMPRINT",EDGE,{"disambiguationData":[TD([[subQ2,-1.0]])],"derivedFrom":subQ1}),-1.0]])]});}
            var Q6;
            {var subQ1=sQuery(id+"F35.wireOp",EDGE,"E736.top");var subQ3=sQuery(id+"F35.wireOp",EDGE,"E760.right");var subQ4=makeQuery(id+"F35.imprint","INTERSECT",VERTEX,{"derivedFrom":[subQ1,subQ3]});Q6=makeQuery(id+"F35.imprint","IMPRINT",FACE,{"disambiguationData":[TD([[makeQuery(id+"F35.imprint","IMPRINT",EDGE,{"disambiguationData":[TD([[subQ4,1.0]])],"derivedFrom":subQ1}),1.0]])]});}
            var Q7;
            {var subQ0=sQuery(id+"F35.wireOp",EDGE,"E760.right");var subQ1=sQuery(id+"F35.wireOp",EDGE,"E736.top");var subQ2=makeQuery(id+"F35.imprint","INTERSECT",VERTEX,{"derivedFrom":[subQ1,subQ0]});Q7=makeQuery(id+"F35.imprint","IMPRINT",FACE,{"disambiguationData":[TD([[makeQuery(id+"F35.imprint","IMPRINT",EDGE,{"disambiguationData":[TD([[subQ2,-1.0]])],"derivedFrom":subQ1}),1.0]])]});}
            var Q8;
            {var subQ0=sQuery(id+"F35.wireOp",EDGE,"E759.left");var subQ1=sQuery(id+"F35.wireOp",EDGE,"E736.top");var subQ2=makeQuery(id+"F35.imprint","INTERSECT",VERTEX,{"derivedFrom":[subQ1,subQ0]});Q8=makeQuery(id+"F35.imprint","IMPRINT",FACE,{"disambiguationData":[TD([[makeQuery(id+"F35.imprint","IMPRINT",EDGE,{"disambiguationData":[TD([[subQ2,-1.0]])],"derivedFrom":subQ1}),1.0]])]});}
            var Q9;
            {var subQ0=sQuery(id+"F35.wireOp",EDGE,"E759.right");var subQ1=sQuery(id+"F35.wireOp",EDGE,"E736.top");var subQ2=makeQuery(id+"F35.imprint","INTERSECT",VERTEX,{"derivedFrom":[subQ1,subQ0]});Q9=makeQuery(id+"F35.imprint","IMPRINT",FACE,{"disambiguationData":[TD([[makeQuery(id+"F35.imprint","IMPRINT",EDGE,{"disambiguationData":[TD([[subQ2,-1.0]])],"derivedFrom":subQ1}),1.0]])]});}
            var Q10;
            {var subQ0=sQuery(id+"F35.wireOp",EDGE,"E758.right");var subQ1=sQuery(id+"F35.wireOp",EDGE,"E736.top");var subQ2=makeQuery(id+"F35.imprint","INTERSECT",VERTEX,{"derivedFrom":[subQ1,subQ0]});Q10=makeQuery(id+"F35.imprint","IMPRINT",FACE,{"disambiguationData":[TD([[makeQuery(id+"F35.imprint","IMPRINT",EDGE,{"disambiguationData":[TD([[subQ2,-1.0]])],"derivedFrom":subQ1}),1.0]])]});}
            var Q11;
            {var subQ1=sQuery(id+"F35.wireOp",EDGE,"E736.top");var subQ3=sQuery(id+"F35.wireOp",EDGE,"E757.left");var subQ4=makeQuery(id+"F35.imprint","INTERSECT",VERTEX,{"derivedFrom":[subQ1,subQ3]});Q11=makeQuery(id+"F35.imprint","IMPRINT",FACE,{"disambiguationData":[TD([[makeQuery(id+"F35.imprint","IMPRINT",EDGE,{"disambiguationData":[TD([[subQ4,-1.0]])],"derivedFrom":subQ1}),1.0]])]});}
            var Q12;
            {var subQ0=sQuery(id+"F35.wireOp",EDGE,"E838.MirrorCS");var subQ1=sQuery(id+"F35.wireOp",EDGE,"E830.MirrorCS");var subQ2=makeQuery(id+"F35.imprint","INTERSECT",VERTEX,{"derivedFrom":[subQ1,subQ0]});Q12=makeQuery(id+"F35.imprint","IMPRINT",FACE,{"disambiguationData":[TD([[makeQuery(id+"F35.imprint","IMPRINT",EDGE,{"disambiguationData":[TD([[subQ2,-1.0]])],"derivedFrom":subQ1}),1.0]])]});}
            var Q13;
            {var subQ0=sQuery(id+"F35.wireOp",EDGE,"E839.MirrorCS");var subQ1=sQuery(id+"F35.wireOp",EDGE,"E718.top");var subQ2=makeQuery(id+"F35.imprint","INTERSECT",VERTEX,{"derivedFrom":[subQ1,subQ0]});Q13=makeQuery(id+"F35.imprint","IMPRINT",FACE,{"disambiguationData":[TD([[makeQuery(id+"F35.imprint","IMPRINT",EDGE,{"disambiguationData":[TD([[subQ2,-1.0]])],"derivedFrom":subQ1}),-1.0]])]});}
            var Q14;
            {var subQ0=sQuery(id+"F35.wireOp",EDGE,"E839.MirrorCS");var subQ1=sQuery(id+"F35.wireOp",EDGE,"E718.top");var subQ2=makeQuery(id+"F35.imprint","INTERSECT",VERTEX,{"derivedFrom":[subQ1,subQ0]});Q14=makeQuery(id+"F35.imprint","IMPRINT",FACE,{"disambiguationData":[TD([[makeQuery(id+"F35.imprint","IMPRINT",EDGE,{"disambiguationData":[TD([[subQ2,-1.0]])],"derivedFrom":subQ1}),1.0]])]});}
            var Q15;
            {var subQ0=sQuery(id+"F35.wireOp",EDGE,"E838.MirrorCS");var subQ1=sQuery(id+"F35.wireOp",EDGE,"E828.MirrorCS");var subQ2=makeQuery(id+"F35.imprint","INTERSECT",VERTEX,{"derivedFrom":[subQ1,subQ0]});Q15=makeQuery(id+"F35.imprint","IMPRINT",FACE,{"disambiguationData":[TD([[makeQuery(id+"F35.imprint","IMPRINT",EDGE,{"disambiguationData":[TD([[subQ2,-1.0]])],"derivedFrom":subQ1}),1.0]])]});}
            var Q16;
            {var subQ0=sQuery(id+"F35.wireOp",EDGE,"E838.MirrorCS");var subQ1=sQuery(id+"F35.wireOp",EDGE,"E827.MirrorCS");var subQ2=makeQuery(id+"F35.imprint","INTERSECT",VERTEX,{"derivedFrom":[subQ1,subQ0]});var subQ3=sQuery(id+"F35.wireOp",EDGE,"E839.MirrorCS");var subQ4=makeQuery(id+"F35.imprint","INTERSECT",VERTEX,{"derivedFrom":[subQ1,subQ3]});Q16=makeQuery(id+"F35.imprint","IMPRINT",FACE,{"disambiguationData":[TD([[makeQuery(id+"F35.imprint","IMPRINT",EDGE,{"disambiguationData":[TD([[subQ2,-1.0],[subQ4,1.0]])],"derivedFrom":subQ1}),1.0]])]});}
            extrude(context, id + "F37", {"entities" : qUnion([Q0, Q1, Q2, Q3, Q4, Q5, Q6, Q7, Q8, Q9, Q10, Q11, Q12, Q13, Q14, Q15, Q16]), "operationType" : NewBodyOperationType.REMOVE, "oppositeDirection" : true, "depth" : 1.5 * mm, "offsetDistance" : 25 * mm});
        }
    });
